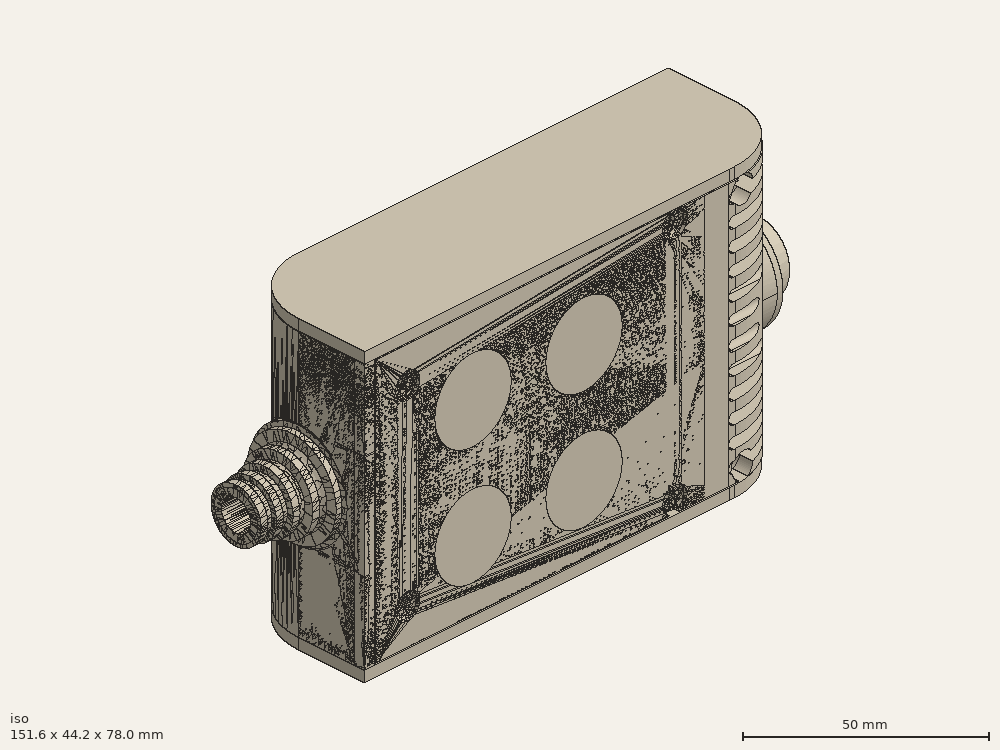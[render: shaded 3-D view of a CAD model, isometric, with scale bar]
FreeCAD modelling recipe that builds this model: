
FCSTD DOCUMENT  (FreeCAD 0.19R0.19.2)
Label: enclosure_192FCStd
License: All rights reserved
LicenseURL: http://en.wikipedia.org/wiki/All_rights_reserved
objects: Part::Revolution×152, Part::MultiFuse×146, Part::Feature×146, Sketcher::SketchObject×84, Part::Cut×70, Part::Cylinder×70, Part::Extrusion×67, Part::Fillet×58, Part::Box×36, App::MeasureDistance×4, PartDesign::Body×2, Image::ImagePlane×1
note: 831 computed .brp shape members not serialized (recipe doc carries the construction recipe); baked Part::Feature solids carry a one-line shape summary decoded from their .brp

FEATURE [Sketcher::SketchObject] Sketch  label="topSketch"
  FullyConstrained = true
  sketch-geometry (20):
    g0: LineSegment StartX=5.21097e-06 StartY=3 StartZ=0 EndX=5.21097e-06 EndY=19 EndZ=0
    g1: ArcOfCircle CenterX=19 CenterY=19 CenterZ=0 NormalX=0 NormalY=0 NormalZ=1 AngleXU=0 Radius=19 StartAngle=1.5708 EndAngle=3.14159
    g2: ArcOfCircle CenterX=19 CenterY=19 CenterZ=0 NormalX=0 NormalY=0 NormalZ=1 AngleXU=0 Radius=16 StartAngle=1.5708 EndAngle=3.14159
    g3: LineSegment StartX=114 StartY=35 StartZ=0 EndX=19 EndY=35 EndZ=0
    g4: LineSegment StartX=5.21097e-06 StartY=3 StartZ=0 EndX=5.21097e-06 EndY=0 EndZ=0
    g5: LineSegment StartX=3 StartY=0 StartZ=0 EndX=5.21097e-06 EndY=0 EndZ=0
    g6: LineSegment StartX=3 StartY=19 StartZ=0 EndX=3 EndY=0 EndZ=0
    g7: LineSegment StartX=19 StartY=38 StartZ=0 EndX=124 EndY=38 EndZ=0
    g8: Circle CenterX=119 CenterY=35 CenterZ=0 NormalX=0 NormalY=0 NormalZ=1 AngleXU=0 Radius=1
    g9: Circle CenterX=121 CenterY=35 CenterZ=0 NormalX=0 NormalY=0 NormalZ=1 AngleXU=0 Radius=1
    g10: Circle CenterX=121 CenterY=33 CenterZ=0 NormalX=0 NormalY=0 NormalZ=1 AngleXU=0 Radius=1
    g11: BSplineCurve PolesCount=3 KnotsCount=2 Degree=2 IsPeriodic=0
    g12: GeomPoint X=119 Y=35 Z=0
    g13: GeomPoint X=121 Y=33 Z=0
    g14: LineSegment StartX=119 StartY=35 StartZ=0 EndX=114 EndY=35 EndZ=0
    g15: ArcOfCircle CenterX=105 CenterY=19 CenterZ=0 NormalX=0 NormalY=0 NormalZ=1 AngleXU=0 Radius=19 StartAngle=5.7297 EndAngle=6.28319
    g16: ArcOfCircle CenterX=105 CenterY=19 CenterZ=0 NormalX=0 NormalY=0 NormalZ=1 AngleXU=0 Radius=16 StartAngle=5.60905 EndAngle=6.28319
    g17: LineSegment StartX=121 StartY=33 StartZ=0 EndX=121 EndY=19 EndZ=0
    g18: LineSegment StartX=124 StartY=38 StartZ=0 EndX=124 EndY=19 EndZ=0
    g19: LineSegment StartX=117.5 StartY=9.01251 StartZ=0 EndX=121.163 EndY=9.0125 EndZ=0
  constraints (46):
    c: Vertical(g0)
    c: Block(g0)
    c: Coincident(g1,g0)
    c: Block(g1)
    c: Coincident(g2,g1)
    c: Block(g2)
    c: Coincident(g3,g2)
    c: Horizontal(g3)
    c: Tangent(g3,g2)
    c: Coincident(g4,g0)
    c: Distance(g4) = 3
    c: Vertical(g4)
    c: Coincident(g5,g4)
    c: Horizontal(g5)
    c: Coincident(g6,g2)
    c: Coincident(g6,g5)
    c: Vertical(g6)
    c: Horizontal(g7)
    c: Distance(g7) = 105
    c: Coincident(g7,g1)
    c: Block(g3)
    c: Weight(g8) = 1
    c: Equal(g8,g9)
    c: Equal(g8,g10)
    c: InternalAlignment(g8,g11)
    c: InternalAlignment(g9,g11)
    c: InternalAlignment(g10,g11)
    c: InternalAlignment(g12,g11)
    c: InternalAlignment(g13,g11)
    c: Block(g11)
    c: Coincident(g14,g11)
    c: Coincident(g14,g3)
    c: Horizontal(g14)
    c: Block(g15)
    c: Coincident(g16,g15)
    c: Block(g16)
    c: Coincident(g17,g11)
    c: Coincident(g17,g16)
    c: Vertical(g17)
    c: Distance(g17) = 14
    c: Coincident(g18,g7)
    c: Coincident(g18,g15)
    c: Vertical(g18)
    c: Distance(g18) = 19
    c: Coincident(g19,g16)
    c: Coincident(g19,g15)
FEATURE [Sketcher::SketchObject] Sketch001  label="bottomSketch"
  FullyConstrained = true
  sketch-geometry (32):
    g0: LineSegment StartX=3.3 StartY=-6.03275e-07 StartZ=0 EndX=98 EndY=-6.03275e-07 EndZ=0
    g1: ArcOfCircle CenterX=98 CenterY=19 CenterZ=0 NormalX=0 NormalY=0 NormalZ=1 AngleXU=0 Radius=19 StartAngle=4.71239 EndAngle=5.71103
    g2: LineSegment StartX=6.3 StartY=8 StartZ=0 EndX=3.3 EndY=8 EndZ=0
    g3: LineSegment StartX=3.3 StartY=8 StartZ=0 EndX=3.3 EndY=-6.03275e-07 EndZ=0
    g4: ArcOfCircle CenterX=8.3 CenterY=5 CenterZ=0 NormalX=0 NormalY=0 NormalZ=1 AngleXU=0 Radius=2 StartAngle=3.14159 EndAngle=4.71239
    g5: LineSegment StartX=6.3 StartY=8 StartZ=0 EndX=6.3 EndY=5 EndZ=0
    g6: ArcOfCircle CenterX=98 CenterY=19 CenterZ=0 NormalX=0 NormalY=0 NormalZ=1 AngleXU=0 Radius=12.7 StartAngle=4.71239 EndAngle=6.28319
    g7: LineSegment StartX=94.7 StartY=3 StartZ=0 EndX=8.3 EndY=3 EndZ=0
    g8-g12: Circle x5 (B-spline internal-alignment scaffolding for g13; pole/knot coordinates omitted)
    g13: BSplineCurve PolesCount=5 KnotsCount=3 Degree=3 IsPeriodic=0
    g14: GeomPoint X=98 Y=6.3 Z=0
    g15: GeomPoint X=96.3938 Y=4.71946 Z=0
    g16: GeomPoint X=94.7 Y=3 Z=0
    g17-g23: Circle x7 (B-spline internal-alignment scaffolding for g24; pole/knot coordinates omitted)
    g24: BSplineCurve PolesCount=7 KnotsCount=5 Degree=3 IsPeriodic=0
    g25-g29: GeomPoint x5 (B-spline internal-alignment scaffolding for g24; pole/knot coordinates omitted)
    g30: ArcOfCircle CenterX=98 CenterY=19 CenterZ=0 NormalX=0 NormalY=0 NormalZ=1 AngleXU=0 Radius=15.7 StartAngle=5.81226 EndAngle=6.28319
    g31: LineSegment StartX=110.7 StartY=19 StartZ=0 EndX=113.7 EndY=19 EndZ=0
  constraints (41):
    c: Horizontal(g0)
    c: Coincident(g1,g0)
    c: Block(g1)
    c: Horizontal(g2)
    c: Distance(g2) = 3
    c: Coincident(g3,g2)
    c: Vertical(g3)
    c: Coincident(g3,g0)
    c: Block(g4)
    c: Block(g2)
    c: Coincident(g5,g2)
    c: Coincident(g5,g4)
    c: Vertical(g5)
    c: Coincident(g6,g1)
    c: Block(g6)
    c: Coincident(g7,g4)
    c: Horizontal(g7)
    c: Block(g0)
    c: Block(g7)
    c: Block(g3)
    c: Coincident(g13,g6)
    c: Weight(g8) = 1
    c: Equal(g8, g9-g12) x4
    c: Coincident(g13,g7)
    c: InternalAlignment(g8-g12 -> g13) x5
    c: InternalAlignment(g14,g13)
    c: InternalAlignment(g15,g13)
    c: InternalAlignment(g16,g13)
    c: Block(g13)
    c: Weight(g17) = 1
    c: Equal(g17, g18-g23) x6
    c: Coincident(g24,g1)
    c: InternalAlignment(g17-g23 -> g24) x7
    c: InternalAlignment(g25-g29 -> g24) x5
    c: Block(g24)
    c: Coincident(g30,g24)
    c: Coincident(g31,g6)
    c: Coincident(g31,g30)
    c: Horizontal(g31)
    c: Block(g31)
    c: Block(g30)
FEATURE [Part::Extrusion] Extrude  label="top"
  Base = -> Sketch
  Dir = (0,0,1)
  DirMode = 2
  FaceMakerClass = Part::FaceMakerBullseye
  LengthFwd = 72
  LengthRev = 0
  Solid = true
  Symmetric = false
FEATURE [Part::Extrusion] Extrude001  label="bottom"
  Base = -> Sketch001
  Dir = (0,0,1)
  DirMode = 2
  FaceMakerClass = Part::FaceMakerBullseye
  LengthFwd = 71.4
  LengthRev = 0
  Placement = pos=(0,0,0.3) rot=(0,0,1;0rad)
  Solid = true
  Symmetric = false
FEATURE [Sketcher::SketchObject] Sketch002  label="topSketch001"
  FullyConstrained = true
  sketch-geometry (8):
    g0: ArcOfCircle CenterX=19 CenterY=19.0975 CenterZ=0 NormalX=0 NormalY=0 NormalZ=1 AngleXU=0 Radius=18.9025 StartAngle=1.5708 EndAngle=3.14674
    g1: LineSegment StartX=0.0977805 StartY=19.0003 StartZ=0 EndX=0.0977805 EndY=0.000251602 EndZ=0
    g2: LineSegment StartX=19 StartY=38 StartZ=0 EndX=124 EndY=38 EndZ=0
    g3: LineSegment StartX=0.0977805 StartY=0.000251602 StartZ=0 EndX=105.098 EndY=0.000251602 EndZ=0
    g4: LineSegment StartX=124 StartY=38 StartZ=0 EndX=125.616 EndY=38 EndZ=0
    g5: LineSegment StartX=105.098 StartY=0.000251602 StartZ=0 EndX=106.713 EndY=0.000251602 EndZ=0
    g6: ArcOfCircle CenterX=106.616 CenterY=19 CenterZ=0 NormalX=0 NormalY=0 NormalZ=1 AngleXU=0 Radius=19 StartAngle=4.71754 EndAngle=6.28319
    g7: LineSegment StartX=125.616 StartY=38 StartZ=0 EndX=125.616 EndY=19 EndZ=0
  constraints (21):
    c: Block(g0)
    c: Coincident(g1,g0)
    c: Vertical(g1)
    c: Horizontal(g2)
    c: Distance(g2) = 105
    c: Coincident(g2,g0)
    c: Distance(g1) = 19
    c: Coincident(g3,g1)
    c: Horizontal(g3)
    c: Distance(g3) = 105
    c: Coincident(g4,g2)
    c: Horizontal(g4)
    c: Distance(g4) = 1.61553
    c: Horizontal(g5)
    c: Equal(g4,g5) = 1.61553
    c: Coincident(g5,g3)
    c: Block(g6)
    c: Coincident(g6,g5)
    c: Coincident(g7,g4)
    c: Coincident(g7,g6)
    c: Vertical(g7)
FEATURE [Part::Extrusion] Extrude002  label="sideA"
  Base = -> Sketch002
  Dir = (0,0,1)
  DirMode = 2
  FaceMakerClass = Part::FaceMakerBullseye
  LengthFwd = 3
  LengthRev = 0
  Placement = pos=(0,0,-3) rot=(0,0,1;0rad)
  Solid = true
  Symmetric = false
FEATURE [Sketcher::SketchObject] Sketch003  label="topSketch002"
  FullyConstrained = true
  sketch-geometry (6):
    g0: LineSegment StartX=19 StartY=38 StartZ=0 EndX=117 EndY=38 EndZ=0
    g1: ArcOfCircle CenterX=19 CenterY=19 CenterZ=0 NormalX=0 NormalY=0 NormalZ=1 AngleXU=0 Radius=19 StartAngle=1.5708 EndAngle=3.14159
    g2: LineSegment StartX=117 StartY=38 StartZ=0 EndX=117 EndY=19 EndZ=0
    g3: LineSegment StartX=98 StartY=1.0161e-12 StartZ=0 EndX=5.22862e-06 EndY=1.0161e-12 EndZ=0
    g4: LineSegment StartX=5.22862e-06 StartY=19 StartZ=0 EndX=5.22862e-06 EndY=1.0161e-12 EndZ=0
    g5: ArcOfCircle CenterX=98 CenterY=19 CenterZ=0 NormalX=0 NormalY=0 NormalZ=1 AngleXU=0 Radius=19 StartAngle=4.71239 EndAngle=6.28319
  constraints (16):
    c: Horizontal(g0)
    c: Distance(g0) = 98
    c: Coincident(g1,g0)
    c: Block(g1)
    c: Coincident(g2,g0)
    c: Vertical(g2)
    c: Distance(g2) = 19
    c: Horizontal(g3)
    c: Coincident(g4,g1)
    c: Vertical(g4)
    c: Coincident(g3,g4)
    c: Block(g3)
    c: Coincident(g5,g2)
    c: Coincident(g5,g3)
    c: Block(g0)
    c: Block(g5)
FEATURE [Sketcher::SketchObject] Sketch004
  FullyConstrained = true
  MapMode = 3
  Placement = pos=(0,0,0) rot=(1,0,0;1.5708rad)
  Support = -> [Extrude]
  sketch-geometry (8):
    g0: Circle CenterX=80.351 CenterY=-67.6202 CenterZ=0 NormalX=0 NormalY=0 NormalZ=1 AngleXU=0 Radius=2
    g1: Circle CenterX=80.351 CenterY=-67.6202 CenterZ=0 NormalX=0 NormalY=0 NormalZ=1 AngleXU=0 Radius=3
    g2: Circle CenterX=80.351 CenterY=-4.92017 CenterZ=0 NormalX=0 NormalY=0 NormalZ=1 AngleXU=0 Radius=2
    g3: Circle CenterX=80.351 CenterY=-4.92017 CenterZ=0 NormalX=0 NormalY=0 NormalZ=1 AngleXU=0 Radius=3
    g4: Circle CenterX=23.851 CenterY=-4.92017 CenterZ=0 NormalX=0 NormalY=0 NormalZ=1 AngleXU=0 Radius=2
    g5: Circle CenterX=23.851 CenterY=-4.92017 CenterZ=0 NormalX=0 NormalY=0 NormalZ=1 AngleXU=0 Radius=3
    g6: Circle CenterX=23.851 CenterY=-67.6202 CenterZ=0 NormalX=0 NormalY=0 NormalZ=1 AngleXU=0 Radius=2
    g7: Circle CenterX=23.851 CenterY=-67.6202 CenterZ=0 NormalX=0 NormalY=0 NormalZ=1 AngleXU=0 Radius=3
  constraints (8):
    c: Block(g3)
    c: Block(g2)
    c: Block(g1)
    c: Block(g0)
    c: Block(g6)
    c: Block(g7)
    c: Block(g4)
    c: Block(g5)
FEATURE [Part::Extrusion] Extrude004
  Base = -> Sketch004
  Dir = (0,-1,2e-16)
  DirMode = 2
  FaceMakerClass = Part::FaceMakerBullseye
  LengthFwd = 6
  LengthRev = 0
  Placement = pos=(0,9,0) rot=(0,0,1;0rad)
  Solid = true
  Symmetric = false
FEATURE [Sketcher::SketchObject] Sketch005
  FullyConstrained = true
  MapMode = 3
  Placement = pos=(0,0,0) rot=(1,0,0;1.5708rad)
  Support = -> [Extrude]
  sketch-geometry (8):
    g0: Circle CenterX=80.351 CenterY=-67.6202 CenterZ=0 NormalX=0 NormalY=0 NormalZ=1 AngleXU=0 Radius=3
    g1: Circle CenterX=80.351 CenterY=-4.92017 CenterZ=0 NormalX=0 NormalY=0 NormalZ=1 AngleXU=0 Radius=3
    g2: Circle CenterX=23.851 CenterY=-4.92017 CenterZ=0 NormalX=0 NormalY=0 NormalZ=1 AngleXU=0 Radius=3
    g3: Circle CenterX=23.851 CenterY=-67.6202 CenterZ=0 NormalX=0 NormalY=0 NormalZ=1 AngleXU=0 Radius=3
    g4: Circle CenterX=23.851 CenterY=-67.6202 CenterZ=0 NormalX=0 NormalY=0 NormalZ=1 AngleXU=0 Radius=5
    g5: Circle CenterX=80.351 CenterY=-67.6202 CenterZ=0 NormalX=0 NormalY=0 NormalZ=1 AngleXU=0 Radius=5
    g6: Circle CenterX=23.851 CenterY=-4.92017 CenterZ=0 NormalX=0 NormalY=0 NormalZ=1 AngleXU=0 Radius=5
    g7: Circle CenterX=80.351 CenterY=-4.92017 CenterZ=0 NormalX=0 NormalY=0 NormalZ=1 AngleXU=0 Radius=5
  constraints (8):
    c: Block(g1)
    c: Block(g0)
    c: Block(g3)
    c: Block(g2)
    c: Block(g5)
    c: Block(g4)
    c: Block(g6)
    c: Block(g7)
FEATURE [Part::Extrusion] Extrude005
  Base = -> Sketch005
  Dir = (0,-1,2e-16)
  DirMode = 2
  FaceMakerClass = Part::FaceMakerBullseye
  LengthFwd = 2
  LengthRev = 0
  Solid = true
  Symmetric = false
FEATURE [Sketcher::SketchObject] Sketch006
  FullyConstrained = true
  MapMode = 3
  Placement = pos=(0,0,0) rot=(1,0,0;1.5708rad)
  sketch-geometry (8):
    g0: Circle CenterX=80.351 CenterY=-67.6202 CenterZ=0 NormalX=0 NormalY=0 NormalZ=1 AngleXU=0 Radius=3
    g1: Circle CenterX=80.351 CenterY=-4.92017 CenterZ=0 NormalX=0 NormalY=0 NormalZ=1 AngleXU=0 Radius=3
    g2: Circle CenterX=23.851 CenterY=-4.92017 CenterZ=0 NormalX=0 NormalY=0 NormalZ=1 AngleXU=0 Radius=3
    g3: Circle CenterX=23.851 CenterY=-67.6202 CenterZ=0 NormalX=0 NormalY=0 NormalZ=1 AngleXU=0 Radius=3
    g4: Circle CenterX=23.851 CenterY=-67.6202 CenterZ=0 NormalX=0 NormalY=0 NormalZ=1 AngleXU=0 Radius=5
    g5: Circle CenterX=80.351 CenterY=-67.6202 CenterZ=0 NormalX=0 NormalY=0 NormalZ=1 AngleXU=0 Radius=5
    g6: Circle CenterX=23.851 CenterY=-4.92017 CenterZ=0 NormalX=0 NormalY=0 NormalZ=1 AngleXU=0 Radius=5
    g7: Circle CenterX=80.351 CenterY=-4.92017 CenterZ=0 NormalX=0 NormalY=0 NormalZ=1 AngleXU=0 Radius=5
  constraints (8):
    c: Block(g1)
    c: Block(g0)
    c: Block(g3)
    c: Block(g2)
    c: Block(g5)
    c: Block(g4)
    c: Block(g6)
    c: Block(g7)
FEATURE [Part::Extrusion] Extrude007
  Base = -> Sketch006
  Dir = (0,-1,2e-16)
  DirMode = 2
  FaceMakerClass = Part::FaceMakerBullseye
  LengthFwd = 2
  LengthRev = 0
  Solid = true
  Symmetric = false
FEATURE [Part::Fillet] Fillet
  Base = -> Extrude007
  Edges = 4 edges r=1.99: [Edge6,Edge12,Edge18,Edge24]
FEATURE [Part::Cut] Cut
  Base = -> Extrude005
  Placement = pos=(0,5,0) rot=(0,0,1;0rad)
  Tool = -> Fillet
FEATURE [Part::MultiFuse] Fusion  label="pCBScrews"
  Placement = pos=(-2.5,0,72.3) rot=(0,0,1;0rad)
  Shapes = -> [Extrude004,Cut]
FEATURE [App::MeasureDistance] Distance  label="Distance: 0.69 mm"
  Distance = 0.685967
  P1 = (24.0138,2.9647,0.3)
  P2 = (23.8901,3,-0.373787)
FEATURE [App::MeasureDistance] Distance001  label="Distance: 0.53 mm"
  Distance = 0.533607
  P1 = (80.2939,3,72.2334)
  P2 = (80.281,2.99661,71.7)
FEATURE [Part::Fillet] Fillet001
  Base = -> Extrude001
  Edges = 1 edges r=2.4: [Edge17]
FEATURE [Part::Fillet] Fillet002  label="bottom001"
  Base = -> Fillet001
  Edges = 1 edges r=2.4: [Edge36]
FEATURE [Part::Fillet] Fillet003  label="top001"
  Base = -> Extrude
  Edges = 1 edges r=2: [Edge1]
FEATURE [Sketcher::SketchObject] Sketch007
  FullyConstrained = true
  sketch-geometry (16):
    g0: LineSegment StartX=4 StartY=0 StartZ=0 EndX=4 EndY=2.4 EndZ=0
    g1: LineSegment StartX=4 StartY=2.4 StartZ=0 EndX=7 EndY=2.4 EndZ=0
    g2: LineSegment StartX=4 StartY=0 StartZ=0 EndX=5.7 EndY=0 EndZ=0
    g3: LineSegment StartX=5.7 StartY=0 StartZ=0 EndX=5.7 EndY=-5.6 EndZ=0
    g4-g8: Circle x5 (B-spline internal-alignment scaffolding for g9; pole/knot coordinates omitted)
    g9: BSplineCurve PolesCount=5 KnotsCount=3 Degree=3 IsPeriodic=0
    g10: GeomPoint X=7 Y=2.4 Z=0
    g11: GeomPoint X=10.4582 Y=-1.55472 Z=0
    g12: GeomPoint X=14 Y=-5.6 Z=0
    g13: LineSegment StartX=14 StartY=-5.6 StartZ=0 EndX=14 EndY=-14.1 EndZ=0
    g14: LineSegment StartX=14 StartY=-14.1 StartZ=0 EndX=6.5 EndY=-14.1 EndZ=0
    g15: LineSegment StartX=5.7 StartY=-5.6 StartZ=0 EndX=6.5 EndY=-14.1 EndZ=0
  constraints (28):
    c: Distance(g0) = 2.4
    c: Vertical(g0)
    c: Block(g0)
    c: Coincident(g1,g0)
    c: Horizontal(g1)
    c: Distance(g1) = 3
    c: Coincident(g2,g0)
    c: Horizontal(g2)
    c: Distance(g2) = 1.7
    c: Coincident(g3,g2)
    c: Vertical(g3)
    c: Distance(g3) = 5.6
    c: Coincident(g9,g1)
    c: Weight(g4) = 1
    c: Equal(g4, g5-g8) x4
    c: InternalAlignment(g4-g8 -> g9) x5
    c: InternalAlignment(g10,g9)
    c: InternalAlignment(g11,g9)
    c: InternalAlignment(g12,g9)
    c: Block(g9)
    c: Coincident(g13,g9)
    c: Vertical(g13)
    c: Distance(g13) = 8.5
    c: Coincident(g14,g13)
    c: Horizontal(g14)
    c: Distance(g14) = 7.5
    c: Coincident(g15,g3)
    c: Coincident(g15,g14)
FEATURE [Part::Feature] Face
  shape: bbox 10 x 16.5 x 2e-07 mm, 1 faces, 0 solids (baked)
FEATURE [Part::Revolution] Revolve  label="plugHousing"
  Angle = 360
  Axis = (0,1,0)
  Base = (0,0,0)
  FaceMakerClass = Part::FaceMakerBullseye
  Placement = pos=(0,0,36.15) rot=(0,0,1;0rad)
  Solid = false
  Source = -> Face
  Symmetric = false
FEATURE [Part::Feature] Face001
  shape: bbox 10 x 16.5 x 2e-07 mm, 1 faces, 0 solids (baked)
FEATURE [Part::Revolution] Revolve001  label="plugHousing001"
  Angle = 360
  Axis = (0,1,0)
  Base = (0,0,0)
  FaceMakerClass = Part::FaceMakerBullseye
  Placement = pos=(0,0,36.15) rot=(0,0,1;0rad)
  Solid = false
  Source = -> Face001
  Symmetric = false
FEATURE [Part::MultiFuse] Fusion001  label="plugHousing002"
  Placement = pos=(0,0,0) rot=(0,0,1;1.5708rad)
  Shapes = -> [Revolve001,Revolve]
FEATURE [Part::Feature] Face002
  shape: bbox 10 x 16.5 x 2e-07 mm, 1 faces, 0 solids (baked)
FEATURE [Part::Revolution] Revolve003  label="plugHousing005"
  Angle = 360
  Axis = (0,1,0)
  Base = (0,0,0)
  FaceMakerClass = Part::FaceMakerBullseye
  Placement = pos=(0,0,36.15) rot=(0,0,1;0rad)
  Solid = false
  Source = -> Face002
  Symmetric = false
FEATURE [Part::Feature] Face003
  shape: bbox 10 x 16.5 x 2e-07 mm, 1 faces, 0 solids (baked)
FEATURE [Part::Revolution] Revolve002  label="plugHousing003"
  Angle = 360
  Axis = (0,1,0)
  Base = (0,0,0)
  FaceMakerClass = Part::FaceMakerBullseye
  Placement = pos=(0,0,36.15) rot=(0,0,1;0rad)
  Solid = false
  Source = -> Face003
  Symmetric = false
FEATURE [Part::MultiFuse] Fusion002  label="plugHousing004"
  Placement = pos=(0,0,0) rot=(0,0,1;1.5708rad)
  Shapes = -> [Revolve002,Revolve003]
FEATURE [Part::MultiFuse] Fusion003  label="plugHousing006"
  Placement = pos=(0,19,0) rot=(0,0,1;3.14159rad)
  Shapes = -> [Fusion002,Fusion001]
FEATURE [Part::Feature] Face004
  shape: bbox 10 x 16.5 x 2e-07 mm, 1 faces, 0 solids (baked)
FEATURE [Part::Revolution] Revolve006  label="plugHousing010"
  Angle = 360
  Axis = (0,1,0)
  Base = (0,0,0)
  FaceMakerClass = Part::FaceMakerBullseye
  Placement = pos=(0,0,36.15) rot=(0,0,1;0rad)
  Solid = false
  Source = -> Face004
  Symmetric = false
FEATURE [Part::Feature] Face005
  shape: bbox 10 x 16.5 x 2e-07 mm, 1 faces, 0 solids (baked)
FEATURE [Part::Revolution] Revolve007  label="plugHousing011"
  Angle = 360
  Axis = (0,1,0)
  Base = (0,0,0)
  FaceMakerClass = Part::FaceMakerBullseye
  Placement = pos=(0,0,36.15) rot=(0,0,1;0rad)
  Solid = false
  Source = -> Face005
  Symmetric = false
FEATURE [Part::Feature] Face006
  shape: bbox 10 x 16.5 x 2e-07 mm, 1 faces, 0 solids (baked)
FEATURE [Part::Revolution] Revolve004  label="plugHousing007"
  Angle = 360
  Axis = (0,1,0)
  Base = (0,0,0)
  FaceMakerClass = Part::FaceMakerBullseye
  Placement = pos=(0,0,36.15) rot=(0,0,1;0rad)
  Solid = false
  Source = -> Face006
  Symmetric = false
FEATURE [Part::MultiFuse] Fusion004  label="plugHousing009"
  Placement = pos=(0,0,0) rot=(0,0,1;1.5708rad)
  Shapes = -> [Revolve004,Revolve007]
FEATURE [Part::Feature] Face007
  shape: bbox 10 x 16.5 x 2e-07 mm, 1 faces, 0 solids (baked)
FEATURE [Part::Revolution] Revolve005  label="plugHousing008"
  Angle = 360
  Axis = (0,1,0)
  Base = (0,0,0)
  FaceMakerClass = Part::FaceMakerBullseye
  Placement = pos=(0,0,36.15) rot=(0,0,1;0rad)
  Solid = false
  Source = -> Face007
  Symmetric = false
FEATURE [Part::MultiFuse] Fusion005  label="plugHousing012"
  Placement = pos=(0,0,0) rot=(0,0,1;1.5708rad)
  Shapes = -> [Revolve006,Revolve005]
FEATURE [Part::MultiFuse] Fusion006  label="plugHousing013"
  Placement = pos=(0,19,0) rot=(0,0,1;3.14159rad)
  Shapes = -> [Fusion005,Fusion004]
FEATURE [Part::MultiFuse] Fusion007  label="plugHousing014"
  Placement = pos=(122.621,0,-0.15) rot=(0,0,1;0rad)
  Shapes = -> [Fusion003,Fusion006]
FEATURE [Part::Cylinder] Cylinder002
  Angle = 360
  AttacherType = Attacher::AttachEngine3D
  Height = 20
  Placement = pos=(0,0,36.15) rot=(0,0,1;0rad)
  Radius = 4
FEATURE [Part::Cylinder] Cylinder003
  Angle = 360
  AttacherType = Attacher::AttachEngine3D
  Height = 10
  Placement = pos=(0,0,36.15) rot=(0,0,1;0rad)
  Radius = 4
FEATURE [Part::MultiFuse] Fusion009  label="removeToCreateHoleForPlugHousing"
  Placement = pos=(70,19,36.15) rot=(0,1,0;1.5708rad)
  Shapes = -> [Cylinder002,Cylinder003]
FEATURE [Part::Cylinder] Cylinder004
  Angle = 360
  AttacherType = Attacher::AttachEngine3D
  Height = 20
  Placement = pos=(0,0,36.15) rot=(0,0,1;0rad)
  Radius = 4
FEATURE [Part::Cylinder] Cylinder005
  Angle = 360
  AttacherType = Attacher::AttachEngine3D
  Height = 10
  Placement = pos=(0,0,36.15) rot=(0,0,1;0rad)
  Radius = 4
FEATURE [Part::MultiFuse] Fusion010  label="removeToCreateHoleForPlugHousing001"
  Placement = pos=(70,19,36.15) rot=(0,1,0;1.5708rad)
  Shapes = -> [Cylinder004,Cylinder005]
FEATURE [Part::Cut] Cut001
  Base = -> Fillet003
  Tool = -> Fusion010
FEATURE [Part::Cut] Cut002  label="Bottom"
  Base = -> Fillet002
  Tool = -> Fusion009
FEATURE [Part::Feature] Face008
  shape: bbox 10 x 16.5 x 2e-07 mm, 1 faces, 0 solids (baked)
FEATURE [Part::Revolution] Revolve011  label="plugHousing021"
  Angle = 360
  Axis = (0,1,0)
  Base = (0,0,0)
  FaceMakerClass = Part::FaceMakerBullseye
  Placement = pos=(0,0,36.15) rot=(0,0,1;0rad)
  Solid = false
  Source = -> Face008
  Symmetric = false
FEATURE [Part::Feature] Face009
  shape: bbox 10 x 16.5 x 2e-07 mm, 1 faces, 0 solids (baked)
FEATURE [Part::Revolution] Revolve012  label="plugHousing022"
  Angle = 360
  Axis = (0,1,0)
  Base = (0,0,0)
  FaceMakerClass = Part::FaceMakerBullseye
  Placement = pos=(0,0,36.15) rot=(0,0,1;0rad)
  Solid = false
  Source = -> Face009
  Symmetric = false
FEATURE [Part::Feature] Face010 .. Face013  x4 (patterned run collapsed; names and placements below)
  shape: bbox 10 x 16.5 x 2e-07 mm, 1 faces, 0 solids (baked)
FEATURE [Part::Revolution] Revolve015  label="plugHousing027"
  Angle = 360
  Axis = (0,1,0)
  Base = (0,0,0)
  FaceMakerClass = Part::FaceMakerBullseye
  Placement = pos=(0,0,36.15) rot=(0,0,1;0rad)
  Solid = false
  Source = -> Face013
  Symmetric = false
FEATURE [Part::Feature] Face014
  shape: bbox 10 x 16.5 x 2e-07 mm, 1 faces, 0 solids (baked)
FEATURE [Part::Feature] Face015
  shape: bbox 10 x 16.5 x 2e-07 mm, 1 faces, 0 solids (baked)
FEATURE [Part::Feature] Face016
  shape: bbox 10 x 16.5 x 2e-07 mm, 1 faces, 0 solids (baked)
FEATURE [Part::Revolution] Revolve019  label="plugHousing033"
  Angle = 360
  Axis = (0,1,0)
  Base = (0,0,0)
  FaceMakerClass = Part::FaceMakerBullseye
  Placement = pos=(0,0,36.15) rot=(0,0,1;0rad)
  Solid = false
  Source = -> Face016
  Symmetric = false
FEATURE [Part::Feature] Face017
  shape: bbox 10 x 16.5 x 2e-07 mm, 1 faces, 0 solids (baked)
FEATURE [Part::Revolution] Revolve020  label="plugHousing034"
  Angle = 360
  Axis = (0,1,0)
  Base = (0,0,0)
  FaceMakerClass = Part::FaceMakerBullseye
  Placement = pos=(0,0,36.15) rot=(0,0,1;0rad)
  Solid = false
  Source = -> Face017
  Symmetric = false
FEATURE [Part::Feature] Face018
  shape: bbox 10 x 16.5 x 2e-07 mm, 1 faces, 0 solids (baked)
FEATURE [Part::Revolution] Revolve016  label="plugHousing030"
  Angle = 360
  Axis = (0,1,0)
  Base = (0,0,0)
  FaceMakerClass = Part::FaceMakerBullseye
  Placement = pos=(0,0,36.15) rot=(0,0,1;0rad)
  Solid = false
  Source = -> Face018
  Symmetric = false
FEATURE [Part::MultiFuse] Fusion020  label="plugHousing038"
  Placement = pos=(0,0,0) rot=(0,0,1;1.5708rad)
  Shapes = -> [Revolve016,Revolve020]
FEATURE [Part::Feature] Face019
  shape: bbox 10 x 16.5 x 2e-07 mm, 1 faces, 0 solids (baked)
FEATURE [Part::Feature] Face020
  shape: bbox 10 x 16.5 x 2e-07 mm, 1 faces, 0 solids (baked)
FEATURE [Part::Revolution] Revolve017  label="plugHousing031"
  Angle = 360
  Axis = (0,1,0)
  Base = (0,0,0)
  FaceMakerClass = Part::FaceMakerBullseye
  Placement = pos=(0,0,36.15) rot=(0,0,1;0rad)
  Solid = false
  Source = -> Face020
  Symmetric = false
FEATURE [Part::MultiFuse] Fusion021  label="plugHousing039"
  Placement = pos=(0,0,0) rot=(0,0,1;1.5708rad)
  Shapes = -> [Revolve019,Revolve017]
FEATURE [Part::MultiFuse] Fusion023  label="plugHousing041"
  Placement = pos=(0,19,0) rot=(0,0,1;3.14159rad)
  Shapes = -> [Fusion021,Fusion020]
FEATURE [Part::Revolution] Revolve022  label="plugHousing043"
  Angle = 360
  Axis = (0,1,0)
  Base = (0,0,0)
  FaceMakerClass = Part::FaceMakerBullseye
  Placement = pos=(0,0,36.15) rot=(0,0,1;0rad)
  Solid = false
  Source = -> Face019
  Symmetric = false
FEATURE [Part::Feature] Face021
  shape: bbox 10 x 16.5 x 2e-07 mm, 1 faces, 0 solids (baked)
FEATURE [Part::Revolution] Revolve023  label="plugHousing044"
  Angle = 360
  Axis = (0,1,0)
  Base = (0,0,0)
  FaceMakerClass = Part::FaceMakerBullseye
  Placement = pos=(0,0,36.15) rot=(0,0,1;0rad)
  Solid = false
  Source = -> Face021
  Symmetric = false
FEATURE [Part::Feature] Face022
  shape: bbox 10 x 16.5 x 2e-07 mm, 1 faces, 0 solids (baked)
FEATURE [Part::Revolution] Revolve018  label="plugHousing032"
  Angle = 360
  Axis = (0,1,0)
  Base = (0,0,0)
  FaceMakerClass = Part::FaceMakerBullseye
  Placement = pos=(0,0,36.15) rot=(0,0,1;0rad)
  Solid = false
  Source = -> Face022
  Symmetric = false
FEATURE [Part::MultiFuse] Fusion022  label="plugHousing040"
  Placement = pos=(0,0,0) rot=(0,0,1;1.5708rad)
  Shapes = -> [Revolve018,Revolve023]
FEATURE [Part::Feature] Face023
  shape: bbox 10 x 16.5 x 2e-07 mm, 1 faces, 0 solids (baked)
FEATURE [Part::Revolution] Revolve021  label="plugHousing035"
  Angle = 360
  Axis = (0,1,0)
  Base = (0,0,0)
  FaceMakerClass = Part::FaceMakerBullseye
  Placement = pos=(0,0,36.15) rot=(0,0,1;0rad)
  Solid = false
  Source = -> Face023
  Symmetric = false
FEATURE [Part::MultiFuse] Fusion018  label="plugHousing036"
  Placement = pos=(0,0,0) rot=(0,0,1;1.5708rad)
  Shapes = -> [Revolve022,Revolve021]
FEATURE [Part::MultiFuse] Fusion019  label="plugHousing037"
  Placement = pos=(0,19,0) rot=(0,0,1;3.14159rad)
  Shapes = -> [Fusion018,Fusion022]
FEATURE [Part::MultiFuse] Fusion024  label="plugHousing042"
  Placement = pos=(122.621,0,-0.15) rot=(0,0,1;0rad)
  Shapes = -> [Fusion023,Fusion019]
FEATURE [Part::Cylinder] Cylinder006
  Angle = 360
  AttacherType = Attacher::AttachEngine3D
  Height = 20
  Placement = pos=(0,0,36.15) rot=(0,0,1;0rad)
  Radius = 14.3
FEATURE [Part::Cylinder] Cylinder007
  Angle = 360
  AttacherType = Attacher::AttachEngine3D
  Height = 10
  Placement = pos=(0,0,36.15) rot=(0,0,1;0rad)
  Radius = 4
FEATURE [Part::MultiFuse] Fusion026  label="removeToCreteHoleForPlugHousing"
  Placement = pos=(70,19,36) rot=(0,1,0;1.5708rad)
  Shapes = -> [Cylinder006,Cylinder007]
FEATURE [Part::Box] Box001  label="Cube001"
  AttacherType = Attacher::AttachEngine3D
  Height = 28
  Length = 3
  Placement = pos=(110.7,19,22) rot=(0,0,1;0rad)
  Width = 15.7
FEATURE [Part::Cut] Cut003  label="top002"
  Base = -> Cut001
  Tool = -> Fusion007
FEATURE [Part::Revolution] Revolve008  label="plugHousing015"
  Angle = 360
  Axis = (0,1,0)
  Base = (0,0,0)
  FaceMakerClass = Part::FaceMakerBullseye
  Placement = pos=(0,0,36.15) rot=(0,0,1;0rad)
  Solid = false
  Source = -> Face010
  Symmetric = false
FEATURE [Part::MultiFuse] Fusion013  label="plugHousing020"
  Placement = pos=(0,0,0) rot=(0,0,1;1.5708rad)
  Shapes = -> [Revolve008,Revolve012]
FEATURE [Part::Cut] Cut004  label="top003"
  Base = -> Cut003
  Placement = pos=(1,0,0) rot=(0,0,1;0rad)
  Tool = -> Fusion026
FEATURE [Part::Cylinder] Cylinder008
  Angle = 360
  AttacherType = Attacher::AttachEngine3D
  Height = 20
  Placement = pos=(0,0,36.15) rot=(0,0,1;0rad)
  Radius = 10.3
FEATURE [Part::Cylinder] Cylinder009
  Angle = 360
  AttacherType = Attacher::AttachEngine3D
  Height = 10
  Placement = pos=(0,0,36.15) rot=(0,0,1;0rad)
  Radius = 4
FEATURE [Part::MultiFuse] Fusion027  label="removeToCreteHoleForPlugHousing001"
  Placement = pos=(70,19,36) rot=(0,1,0;1.5708rad)
  Shapes = -> [Cylinder008,Cylinder009]
FEATURE [Part::Cut] Cut005  label="plugHousingTab"
  Base = -> Box001
  Tool = -> Fusion027
FEATURE [Part::MultiFuse] Fusion028  label="plugHousing045"
  Shapes = -> [Fusion024,Cut005]
FEATURE [Part::Box] Box002  label="Cube002"
  AttacherType = Attacher::AttachEngine3D
  Height = 28.8
  Length = 3
  Placement = pos=(107.3,28,21.6) rot=(0,0,1;0rad)
  Width = 7
FEATURE [Part::Box] Box003  label="Cube003"
  AttacherType = Attacher::AttachEngine3D
  Height = 3
  Length = 6.4
  Placement = pos=(107.3,28,18.6) rot=(0,0,1;0rad)
  Width = 7
FEATURE [Part::Box] Box004  label="Cube004"
  AttacherType = Attacher::AttachEngine3D
  Height = 3
  Length = 6.4
  Placement = pos=(107.3,28,50.4) rot=(0,0,1;0rad)
  Width = 7
FEATURE [Part::MultiFuse] Fusion029  label="plugHousingBracketHolder"
  Shapes = -> [Box004,Box002,Box003]
FEATURE [Part::Cylinder] Cylinder010
  Angle = 360
  AttacherType = Attacher::AttachEngine3D
  Height = 20
  Placement = pos=(0,0,36.15) rot=(0,0,1;0rad)
  Radius = 14.3
FEATURE [Part::Cylinder] Cylinder011
  Angle = 360
  AttacherType = Attacher::AttachEngine3D
  Height = 10
  Placement = pos=(0,0,36.15) rot=(0,0,1;0rad)
  Radius = 4
FEATURE [Part::MultiFuse] Fusion030  label="removeToCreteHoleForPlugHousing002"
  Placement = pos=(70,19,36) rot=(0,1,0;1.5708rad)
  Shapes = -> [Cylinder010,Cylinder011]
FEATURE [Part::Cut] Cut006  label="plugHousingBracketHolder001"
  Base = -> Fusion029
  Tool = -> Fusion030
FEATURE [Part::Cylinder] Cylinder012
  Angle = 360
  AttacherType = Attacher::AttachEngine3D
  Height = 20
  Placement = pos=(0,0,36.15) rot=(0,0,1;0rad)
  Radius = 7
FEATURE [Part::Cylinder] Cylinder013
  Angle = 360
  AttacherType = Attacher::AttachEngine3D
  Height = 10
  Placement = pos=(0,0,36.15) rot=(0,0,1;0rad)
  Radius = 4
FEATURE [Part::MultiFuse] Fusion032  label="removeToCreteHoleForPlugHousing003"
  Placement = pos=(70,19,36) rot=(0,1,0;1.5708rad)
  Shapes = -> [Cylinder012,Cylinder013]
FEATURE [Part::Cut] Cut007  label="bottom002"
  Base = -> Cut002
  Tool = -> Fusion032
FEATURE [Sketcher::SketchObject] Sketch008
  FullyConstrained = true
  sketch-geometry (54):
    g0: LineSegment StartX=-4.2 StartY=0 StartZ=0 EndX=-6.2 EndY=0 EndZ=0
    g1: LineSegment StartX=-14 StartY=-18 StartZ=0 EndX=-14 EndY=-26.5 EndZ=0
    g2: LineSegment StartX=-4.2 StartY=0 StartZ=0 EndX=-4.2 EndY=-13.4877 EndZ=0
    g3: Circle CenterX=-4.2 CenterY=-13.4877 CenterZ=0 NormalX=0 NormalY=0 NormalZ=1 AngleXU=0 Radius=1
    g4: Circle CenterX=-4.2 CenterY=-26.5 CenterZ=0 NormalX=0 NormalY=0 NormalZ=1 AngleXU=0 Radius=1
    g5: Circle CenterX=-8.2 CenterY=-26.5 CenterZ=0 NormalX=0 NormalY=0 NormalZ=1 AngleXU=0 Radius=1
    g6: BSplineCurve PolesCount=3 KnotsCount=2 Degree=2 IsPeriodic=0
    g7: GeomPoint X=-4.2 Y=-13.4877 Z=0
    g8: GeomPoint X=-8.2 Y=-26.5 Z=0
    g9: LineSegment StartX=-14 StartY=-26.5 StartZ=0 EndX=-8.2 EndY=-26.5 EndZ=0
    g10: LineSegment StartX=-10.15 StartY=-12 StartZ=0 EndX=-10.15 EndY=-14 EndZ=0
    g11: LineSegment StartX=-12.8401 StartY=-16 StartZ=0 EndX=-10.1571 EndY=-16 EndZ=0
    g12: LineSegment StartX=-10.15 StartY=-14 StartZ=0 EndX=-8.70761 EndY=-14 EndZ=0
    g13: LineSegment StartX=-12.8401 StartY=-16 StartZ=0 EndX=-12.8401 EndY=-17.6958 EndZ=0
    g14: LineSegment StartX=-10.15 StartY=-12 StartZ=0 EndX=-7.79258 EndY=-12 EndZ=0
    g15: Circle CenterX=-6.2215 CenterY=-2 CenterZ=0 NormalX=0 NormalY=0 NormalZ=1 AngleXU=0 Radius=1
    g16: Circle CenterX=-6.22762 CenterY=-2.58724 CenterZ=0 NormalX=0 NormalY=0 NormalZ=1 AngleXU=0 Radius=1
    g17: Circle CenterX=-6.32538 CenterY=-4 CenterZ=0 NormalX=0 NormalY=0 NormalZ=1 AngleXU=0 Radius=1
    g18: BSplineCurve PolesCount=3 KnotsCount=2 Degree=2 IsPeriodic=0
    g19: GeomPoint X=-6.2215 Y=-2 Z=0
    g20: GeomPoint X=-6.32538 Y=-4 Z=0
    g21: Circle CenterX=-6.48644 CenterY=-5.99526 CenterZ=0 NormalX=0 NormalY=0 NormalZ=1 AngleXU=0 Radius=1
    g22: Circle CenterX=-6.58486 CenterY=-6.99526 CenterZ=0 NormalX=0 NormalY=0 NormalZ=1 AngleXU=0 Radius=1
    g23: Circle CenterX=-6.77343 CenterY=-8 CenterZ=0 NormalX=0 NormalY=0 NormalZ=1 AngleXU=0 Radius=1
    g24: BSplineCurve PolesCount=3 KnotsCount=2 Degree=2 IsPeriodic=0
    g25: GeomPoint X=-6.48644 Y=-5.99526 Z=0
    g26: GeomPoint X=-6.77343 Y=-8 Z=0
    g27: Circle CenterX=-7.19003 CenterY=-10 CenterZ=0 NormalX=0 NormalY=0 NormalZ=1 AngleXU=0 Radius=1
    g28: Circle CenterX=-7.44407 CenterY=-11.0915 CenterZ=0 NormalX=0 NormalY=0 NormalZ=1 AngleXU=0 Radius=1
    g29: Circle CenterX=-7.79258 CenterY=-12 CenterZ=0 NormalX=0 NormalY=0 NormalZ=1 AngleXU=0 Radius=1
    g30: BSplineCurve PolesCount=3 KnotsCount=2 Degree=2 IsPeriodic=0
    g31: GeomPoint X=-7.19003 Y=-10 Z=0
    g32: GeomPoint X=-7.79258 Y=-12 Z=0
    g33: Circle CenterX=-8.70761 CenterY=-14 CenterZ=0 NormalX=0 NormalY=0 NormalZ=1 AngleXU=0 Radius=1
    g34: Circle CenterX=-9.33087 CenterY=-15.1837 CenterZ=0 NormalX=0 NormalY=0 NormalZ=1 AngleXU=0 Radius=1
    g35: Circle CenterX=-10.1571 CenterY=-16 CenterZ=0 NormalX=0 NormalY=0 NormalZ=1 AngleXU=0 Radius=1
    g36: BSplineCurve PolesCount=3 KnotsCount=2 Degree=2 IsPeriodic=0
    g37: GeomPoint X=-8.70761 Y=-14 Z=0
    g38: GeomPoint X=-10.1571 Y=-16 Z=0
    g39: Circle CenterX=-12.8401 CenterY=-17.6958 CenterZ=0 NormalX=0 NormalY=0 NormalZ=1 AngleXU=0 Radius=1
    g40: Circle CenterX=-13.3521 CenterY=-17.9027 CenterZ=0 NormalX=0 NormalY=0 NormalZ=1 AngleXU=0 Radius=1
    g41: Circle CenterX=-14 CenterY=-18 CenterZ=0 NormalX=0 NormalY=0 NormalZ=1 AngleXU=0 Radius=1
    g42: BSplineCurve PolesCount=3 KnotsCount=2 Degree=2 IsPeriodic=0
    g43: GeomPoint X=-12.8401 Y=-17.6958 Z=0
    g44: GeomPoint X=-14 Y=-18 Z=0
    g45: LineSegment StartX=-6.2 StartY=0 StartZ=0 EndX=-7.2 EndY=0 EndZ=0
    g46: LineSegment StartX=-7.2 StartY=0 StartZ=0 EndX=-7.2 EndY=-2 EndZ=0
    g47: LineSegment StartX=-7.2 StartY=-2 StartZ=0 EndX=-6.2215 EndY=-2 EndZ=0
    g48: LineSegment StartX=-6.32538 StartY=-4 StartZ=0 EndX=-7.65538 EndY=-4 EndZ=0
    g49: LineSegment StartX=-7.65538 StartY=-4 StartZ=0 EndX=-7.65538 EndY=-5.99526 EndZ=0
    g50: LineSegment StartX=-7.65538 StartY=-5.99526 StartZ=0 EndX=-6.48644 EndY=-5.99526 EndZ=0
    g51: LineSegment StartX=-6.77343 StartY=-8 StartZ=0 EndX=-8.43343 EndY=-8 EndZ=0
    g52: LineSegment StartX=-8.43343 StartY=-8 StartZ=0 EndX=-8.43343 EndY=-10 EndZ=0
    g53: LineSegment StartX=-8.43343 StartY=-10 StartZ=0 EndX=-7.19003 EndY=-10 EndZ=0
  constraints (112):
    c: Horizontal(g0)
    c: Distance(g0) = 2
    c: Block(g0)
    c: Vertical(g1)
    c: Coincident(g2,g0)
    c: Vertical(g2)
    c: Block(g2)
    c: Coincident(g6,g2)
    c: Weight(g3) = 1
    c: Equal(g3,g4)
    c: Equal(g3,g5)
    c: InternalAlignment(g3,g6)
    c: InternalAlignment(g4,g6)
    c: InternalAlignment(g5,g6)
    c: InternalAlignment(g7,g6)
    c: InternalAlignment(g8,g6)
    c: Block(g6)
    c: Coincident(g9,g1)
    c: Coincident(g9,g6)
    c: Horizontal(g9)
    c: Vertical(g10)
    c: Block(g10)
    c: Horizontal(g11)
    c: Block(g11)
    c: Coincident(g12,g10)
    c: Horizontal(g12)
    c: Block(g12)
    c: Coincident(g13,g11)
    c: Vertical(g13)
    c: Block(g13)
    c: Coincident(g14,g10)
    c: Horizontal(g14)
    c: Block(g14)
    c: Block(g9)
    c: Block(g1)
    c: Weight(g15) = 1
    c: Equal(g15,g16)
    c: Equal(g15,g17)
    c: InternalAlignment(g15,g18)
    c: InternalAlignment(g16,g18)
    c: InternalAlignment(g17,g18)
    c: InternalAlignment(g19,g18)
    c: InternalAlignment(g20,g18)
    c: Weight(g21) = 1
    c: Equal(g21,g22)
    c: Equal(g21,g23)
    c: InternalAlignment(g21,g24)
    c: InternalAlignment(g22,g24)
    c: InternalAlignment(g23,g24)
    c: InternalAlignment(g25,g24)
    c: InternalAlignment(g26,g24)
    c: Weight(g27) = 1
    c: Equal(g27,g28)
    c: Equal(g27,g29)
    c: Coincident(g30,g14)
    c: InternalAlignment(g27,g30)
    c: InternalAlignment(g28,g30)
    c: InternalAlignment(g29,g30)
    c: InternalAlignment(g31,g30)
    c: InternalAlignment(g32,g30)
    c: Coincident(g36,g12)
    c: Weight(g33) = 1
    c: Equal(g33,g34)
    c: Equal(g33,g35)
    c: Coincident(g36,g11)
    c: InternalAlignment(g33,g36)
    c: InternalAlignment(g34,g36)
    c: InternalAlignment(g35,g36)
    c: InternalAlignment(g37,g36)
    c: InternalAlignment(g38,g36)
    c: Coincident(g42,g13)
    c: Weight(g39) = 1
    c: Equal(g39,g40)
    c: Equal(g39,g41)
    c: Coincident(g42,g1)
    c: InternalAlignment(g39,g42)
    c: InternalAlignment(g40,g42)
    c: InternalAlignment(g41,g42)
    c: InternalAlignment(g43,g42)
    c: InternalAlignment(g44,g42)
    c: Block(g18)
    c: Block(g24)
    c: Block(g30)
    c: Block(g36)
    c: Block(g42)
    c: Horizontal(g45)
    c: Coincident(g45,g0)
    c: Vertical(g46)
    c: Coincident(g46,g45)
    c: Coincident(g47,g46)
    c: Coincident(g47,g18)
    c: Horizontal(g47)
    c: Block(g46)
    c: Coincident(g48,g18)
    c: Horizontal(g48)
    c: Distance(g48) = 1.33
    c: Vertical(g49)
    c: Coincident(g49,g48)
    c: Coincident(g50,g49)
    c: Coincident(g50,g24)
    c: Horizontal(g50)
    c: Tangent(g50,g22)
    c: Horizontal(g51)
    c: Coincident(g51,g24)
    c: Block(g51)
    c: Vertical(g52)
    c: Block(g52)
    c: Coincident(g52,g51)
    c: Coincident(g53,g52)
    c: Coincident(g53,g30)
    c: Horizontal(g53)
    c: Distance(g1) = 8.5
FEATURE [Part::Feature] Face024
  shape: bbox 9.8 x 26.5 x 2e-07 mm, 1 faces, 0 solids (baked)
FEATURE [Part::Revolution] Revolve024
  Angle = 360
  Axis = (0,1,0)
  Base = (0,0,0)
  FaceMakerClass = Part::FaceMakerBullseye
  Placement = pos=(0,0,0) rot=(0,0,1;1.5708rad)
  Solid = false
  Source = -> Face024
  Symmetric = false
FEATURE [Part::Feature] Face025
  shape: bbox 9.8 x 26.5 x 2e-07 mm, 1 faces, 0 solids (baked)
FEATURE [Part::Revolution] Revolve025
  Angle = 360
  Axis = (0,1,0)
  Base = (0,0,0)
  FaceMakerClass = Part::FaceMakerBullseye
  Placement = pos=(0,0,0) rot=(0,0,1;1.5708rad)
  Solid = false
  Source = -> Face025
  Symmetric = false
FEATURE [Part::MultiFuse] Fusion033
  Placement = pos=(-18,19,36) rot=(0,0,1;0rad)
  Shapes = -> [Revolve025,Revolve024]
FEATURE [Part::Cylinder] Cylinder014
  Angle = 360
  AttacherType = Attacher::AttachEngine3D
  Height = 20
  Placement = pos=(0,0,36.15) rot=(0,0,1;0rad)
  Radius = 14.3
FEATURE [Part::Cylinder] Cylinder015
  Angle = 360
  AttacherType = Attacher::AttachEngine3D
  Height = 10
  Placement = pos=(0,0,36.15) rot=(0,0,1;0rad)
  Radius = 4
FEATURE [Part::MultiFuse] Fusion034  label="removeToCreteHoleForPlugHousing004"
  Placement = pos=(-42,19,36) rot=(0,1,0;1.5708rad)
  Shapes = -> [Cylinder014,Cylinder015]
FEATURE [Part::Cut] Cut008  label="top004"
  Base = -> Cut004
  Placement = pos=(-1,0,0) rot=(0,0,1;0rad)
  Tool = -> Fusion034
FEATURE [Part::Box] Box005  label="Cube005"
  AttacherType = Attacher::AttachEngine3D
  Height = 28
  Length = 3
  Placement = pos=(110.7,19,22) rot=(0,0,1;0rad)
  Width = 15.7
FEATURE [Part::Cylinder] Cylinder016
  Angle = 360
  AttacherType = Attacher::AttachEngine3D
  Height = 10
  Placement = pos=(0,0,36.15) rot=(0,0,1;0rad)
  Radius = 4
FEATURE [Part::Cylinder] Cylinder017
  Angle = 360
  AttacherType = Attacher::AttachEngine3D
  Height = 20
  Placement = pos=(0,0,36.15) rot=(0,0,1;0rad)
  Radius = 10.3
FEATURE [Part::MultiFuse] Fusion035  label="removeToCreteHoleForPlugHousing005"
  Placement = pos=(70,19,36) rot=(0,1,0;1.5708rad)
  Shapes = -> [Cylinder017,Cylinder016]
FEATURE [Part::Cut] Cut009  label="plugHousingTab001"
  Base = -> Box005
  Placement = pos=(-107.4,-14,0) rot=(0,0,1;0rad)
  Tool = -> Fusion035
FEATURE [Part::Box] Box006  label="Cube006"
  AttacherType = Attacher::AttachEngine3D
  Height = 28
  Length = 3
  Placement = pos=(110.7,19,22) rot=(0,0,1;0rad)
  Width = 15.7
FEATURE [Part::Cylinder] Cylinder018
  Angle = 360
  AttacherType = Attacher::AttachEngine3D
  Height = 10
  Placement = pos=(0,0,36.15) rot=(0,0,1;0rad)
  Radius = 4
FEATURE [Part::Cylinder] Cylinder019
  Angle = 360
  AttacherType = Attacher::AttachEngine3D
  Height = 20
  Placement = pos=(0,0,36.15) rot=(0,0,1;0rad)
  Radius = 10.3
FEATURE [Part::MultiFuse] Fusion036  label="removeToCreteHoleForPlugHousing006"
  Placement = pos=(70,19,36) rot=(0,1,0;1.5708rad)
  Shapes = -> [Cylinder019,Cylinder018]
FEATURE [Part::Cut] Cut010  label="plugHousingTab002"
  Base = -> Box006
  Placement = pos=(-107.4,-14,0) rot=(0,0,1;0rad)
  Tool = -> Fusion036
FEATURE [Part::MultiFuse] Fusion037
  Placement = pos=(9.6,23,0) rot=(0,0,1;3.14159rad)
  Shapes = -> [Cut009,Cut010]
FEATURE [Part::Box] Box  label="Cube"
  AttacherType = Attacher::AttachEngine3D
  Height = 10
  Length = 3
  Placement = pos=(3.3,4,12) rot=(0,0,1;0rad)
  Width = 10
FEATURE [Part::Fillet] Fillet004
  Base = -> Fusion028
  Edges = 1 edges r=2: [Edge25]
FEATURE [Part::Fillet] Fillet005  label="plugHousing046"
  Base = -> Fillet004
  Edges = 1 edges r=2: [Edge8]
FEATURE [Part::Fillet] Fillet006
  Base = -> Box
  Edges = 1 edges r=2: [Edge11]
FEATURE [Part::Box] Box007  label="Cube007"
  AttacherType = Attacher::AttachEngine3D
  Height = 10
  Length = 3
  Placement = pos=(3.3,4,50) rot=(0,0,1;0rad)
  Width = 10
FEATURE [Part::Fillet] Fillet007
  Base = -> Box007
  Edges = 1 edges r=2: [Edge12]
FEATURE [Part::Box] Box008  label="Cube008"
  AttacherType = Attacher::AttachEngine3D
  Height = 28
  Length = 4
  Placement = pos=(5,0,22) rot=(0,0,1;0rad)
  Width = 10
FEATURE [Part::Fillet] Fillet008
  Base = -> Box008
  Edges = 1 edges r=1: [Edge7]
FEATURE [Part::Fillet] Fillet009
  Base = -> Fillet008
  Edges = 1 edges r=2: [Edge5]
FEATURE [Part::Fillet] Fillet010
  Base = -> Fillet009
  Edges = 1 edges r=2: [Edge2]
FEATURE [Sketcher::SketchObject] Sketch009  label="topSketch003"
  FullyConstrained = true
  sketch-geometry (4):
    g0: LineSegment StartX=16.8446 StartY=31.512 StartZ=0 EndX=16.3251 EndY=34.4666 EndZ=0
    g1: ArcOfCircle CenterX=19 CenterY=19.2524 CenterZ=0 NormalX=0 NormalY=0 NormalZ=1 AngleXU=0 Radius=15.4476 StartAngle=1.74483 EndAngle=2.72717
    g2: ArcOfCircle CenterX=19 CenterY=19.2524 CenterZ=0 NormalX=0 NormalY=0 NormalZ=1 AngleXU=0 Radius=12.4476 StartAngle=1.74483 EndAngle=2.73189
    g3: LineSegment StartX=4.86004 StartY=25.4725 StartZ=0 EndX=7.58253 EndY=24.2107 EndZ=0
  constraints (7):
    c: Block(g0)
    c: Coincident(g1,g0)
    c: Coincident(g2,g0)
    c: Coincident(g3,g1)
    c: Coincident(g3,g2)
    c: Block(g1)
    c: Block(g2)
FEATURE [Part::Extrusion] Extrude008
  Base = -> Sketch009
  Dir = (0,0,1)
  DirMode = 2
  FaceMakerClass = Part::FaceMakerBullseye
  LengthFwd = 10
  LengthRev = 0
  Placement = pos=(0,0,31) rot=(0,0,1;0rad)
  Solid = true
  Symmetric = false
FEATURE [Part::Cylinder] Cylinder020
  Angle = 360
  AttacherType = Attacher::AttachEngine3D
  Height = 20
  Placement = pos=(0,0,36.15) rot=(0,0,1;0rad)
  Radius = 8.2
FEATURE [Part::Cylinder] Cylinder021
  Angle = 360
  AttacherType = Attacher::AttachEngine3D
  Height = 10
  Placement = pos=(0,0,36.15) rot=(0,0,1;0rad)
  Radius = 4
FEATURE [Part::MultiFuse] Fusion038  label="removeToCreteHoleForPlugHousing007"
  Placement = pos=(-42,19,36) rot=(0,1,0;1.5708rad)
  Shapes = -> [Cylinder020,Cylinder021]
FEATURE [Part::Cut] Cut011
  Base = -> Extrude008
  Tool = -> Fusion038
FEATURE [Part::Fillet] Fillet011
  Base = -> Cut011
  Edges = 1 edges r=2: [Edge1]
FEATURE [Part::Fillet] Fillet012
  Base = -> Fillet011
  Edges = 1 edges r=2.5: [Edge1]
FEATURE [Part::Fillet] Fillet013
  Base = -> Fillet012
  Edges = 1 edges r=2.5: [Edge2]
FEATURE [Part::Box] Box010  label="Cube010"
  AttacherType = Attacher::AttachEngine3D
  Height = 16
  Length = 8
  Placement = pos=(12.7,31.52,28) rot=(0,0,1;0rad)
  Width = 4
FEATURE [Sketcher::SketchObject] Sketch010  label="topSketch004"
  FullyConstrained = true
  sketch-geometry (4):
    g0: LineSegment StartX=16.8446 StartY=31.512 StartZ=0 EndX=16.3251 EndY=34.4666 EndZ=0
    g1: ArcOfCircle CenterX=19 CenterY=19.2524 CenterZ=0 NormalX=0 NormalY=0 NormalZ=1 AngleXU=0 Radius=15.4476 StartAngle=1.74483 EndAngle=2.72717
    g2: ArcOfCircle CenterX=19 CenterY=19.2524 CenterZ=0 NormalX=0 NormalY=0 NormalZ=1 AngleXU=0 Radius=12.4476 StartAngle=1.74483 EndAngle=2.73189
    g3: LineSegment StartX=4.86004 StartY=25.4725 StartZ=0 EndX=7.58253 EndY=24.2107 EndZ=0
  constraints (7):
    c: Block(g0)
    c: Coincident(g1,g0)
    c: Coincident(g2,g0)
    c: Coincident(g3,g1)
    c: Coincident(g3,g2)
    c: Block(g1)
    c: Block(g2)
FEATURE [Part::Cylinder] Cylinder022
  Angle = 360
  AttacherType = Attacher::AttachEngine3D
  Height = 10
  Placement = pos=(0,0,36.15) rot=(0,0,1;0rad)
  Radius = 4
FEATURE [Sketcher::SketchObject] Sketch011  label="topSketch005"
  FullyConstrained = true
  sketch-geometry (4):
    g0: LineSegment StartX=16.8446 StartY=31.512 StartZ=0 EndX=16.3251 EndY=34.4666 EndZ=0
    g1: ArcOfCircle CenterX=19 CenterY=19.2524 CenterZ=0 NormalX=0 NormalY=0 NormalZ=1 AngleXU=0 Radius=15.4476 StartAngle=1.74483 EndAngle=2.72717
    g2: ArcOfCircle CenterX=19 CenterY=19.2524 CenterZ=0 NormalX=0 NormalY=0 NormalZ=1 AngleXU=0 Radius=12.4476 StartAngle=1.74483 EndAngle=2.73189
    g3: LineSegment StartX=4.86004 StartY=25.4725 StartZ=0 EndX=7.58253 EndY=24.2107 EndZ=0
  constraints (7):
    c: Block(g0)
    c: Coincident(g1,g0)
    c: Coincident(g2,g0)
    c: Coincident(g3,g1)
    c: Coincident(g3,g2)
    c: Block(g1)
    c: Block(g2)
FEATURE [Part::Extrusion] Extrude010
  Base = -> Sketch011
  Dir = (0,0,1)
  DirMode = 2
  FaceMakerClass = Part::FaceMakerBullseye
  LengthFwd = 10.6
  LengthRev = 0
  Placement = pos=(0,0,31) rot=(0,0,1;0rad)
  Solid = true
  Symmetric = false
FEATURE [Part::Cylinder] Cylinder023
  Angle = 360
  AttacherType = Attacher::AttachEngine3D
  Height = 20
  Placement = pos=(0,0,36.15) rot=(0,0,1;0rad)
  Radius = 8.2
FEATURE [Part::MultiFuse] Fusion039  label="removeToCreteHoleForPlugHousing008"
  Placement = pos=(-42,19,36) rot=(0,1,0;1.5708rad)
  Shapes = -> [Cylinder023,Cylinder022]
FEATURE [Part::Cut] Cut012
  Base = -> Extrude010
  Placement = pos=(0,0,-0.3) rot=(0,0,1;0rad)
  Tool = -> Fusion039
FEATURE [Part::Cut] Cut013
  Base = -> Box010
  Tool = -> Cut012
FEATURE [Part::Fillet] Fillet014
  Base = -> Cut013
  Edges = 1 edges r=0.7: [Edge13]
FEATURE [Part::Fillet] Fillet015
  Base = -> Fillet014
  Edges = 1 edges r=0.7: [Edge13]
FEATURE [Part::Fillet] Fillet016
  Base = -> Fillet015
  Edges = 1 edges r=0.7: [Edge16]
FEATURE [Part::Fillet] Fillet017
  Base = -> Fillet016
  Edges = 1 edges r=0.7: [Edge11]
FEATURE [Part::Fillet] Fillet018
  Base = -> Fillet017
  Edges = 1 edges r=0.7: [Edge10]
FEATURE [Part::Fillet] Fillet019
  Base = -> Fillet018
  Edges = 1 edges r=1.2: [Edge5]
FEATURE [Part::Fillet] Fillet020
  Base = -> Fillet019
  Edges = 1 edges r=1.2: [Edge12]
FEATURE [Part::Fillet] Fillet021
  Base = -> Fillet020
  Edges = 1 edges r=2: [Edge1]
  Placement = pos=(0.3,0,0) rot=(0,0,1;0rad)
FEATURE [Part::MultiFuse] Fusion040  label="top005"
  Shapes = -> [Cut008,Fillet021]
FEATURE [Part::MultiFuse] Fusion041  label="wireHolder"
  Shapes = -> [Fusion033,Fillet013]
FEATURE [Part::MultiFuse] Fusion042
  Shapes = -> [Fillet007,Fusion041]
FEATURE [Part::MultiFuse] Fusion043  label="wireHolder001"
  Shapes = -> [Fusion042,Fillet010]
FEATURE [Part::MultiFuse] Fusion044  label="wireHolder002"
  Shapes = -> [Fillet006,Fusion037,Fusion043]
FEATURE [Part::Feature] Face026
  shape: bbox 11 x 6 x 2e-07 mm, 1 faces, 0 solids (baked)
FEATURE [Part::Revolution] Revolve026
  Angle = 360
  Axis = (0,1,0)
  Base = (0,0,0)
  FaceMakerClass = Part::FaceMakerBullseye
  Placement = pos=(30.3,-1,19.7) rot=(0,0,1;0rad)
  Solid = false
  Source = -> Face026
  Symmetric = false
FEATURE [Sketcher::SketchObject] Sketch013  label="topSketch006"
  FullyConstrained = true
  sketch-geometry (13):
    g0: LineSegment StartX=117 StartY=19 StartZ=0 EndX=117 EndY=38 EndZ=0
    g1: ArcOfCircle CenterX=98 CenterY=19 CenterZ=0 NormalX=0 NormalY=0 NormalZ=1 AngleXU=0 Radius=19 StartAngle=5.7297 EndAngle=6.28319
    g2: LineSegment StartX=0 StartY=3 StartZ=0 EndX=0 EndY=19 EndZ=0
    g3: LineSegment StartX=19 StartY=38 StartZ=0 EndX=117 EndY=38 EndZ=0
    g4: ArcOfCircle CenterX=19 CenterY=19 CenterZ=0 NormalX=0 NormalY=0 NormalZ=1 AngleXU=0 Radius=19 StartAngle=1.5708 EndAngle=3.14159
    g5: ArcOfCircle CenterX=19 CenterY=19 CenterZ=0 NormalX=0 NormalY=0 NormalZ=1 AngleXU=0 Radius=16 StartAngle=1.5708 EndAngle=3.14159
    g6: ArcOfCircle CenterX=98 CenterY=19 CenterZ=0 NormalX=0 NormalY=0 NormalZ=1 AngleXU=0 Radius=16 StartAngle=5.60905 EndAngle=6.28319
    g7: LineSegment StartX=114 StartY=19 StartZ=0 EndX=114 EndY=35 EndZ=0
    g8: LineSegment StartX=110.5 StartY=9.01251 StartZ=0 EndX=114.163 EndY=9.01251 EndZ=0
    g9: LineSegment StartX=114 StartY=35 StartZ=0 EndX=19 EndY=35 EndZ=0
    g10: LineSegment StartX=0 StartY=3 StartZ=0 EndX=0 EndY=0 EndZ=0
    g11: LineSegment StartX=3 StartY=0 StartZ=0 EndX=0 EndY=0 EndZ=0
    g12: LineSegment StartX=3 StartY=19 StartZ=0 EndX=3 EndY=0 EndZ=0
  constraints (33):
    c: Vertical(g0)
    c: Distance(g0) = 19
    c: Block(g0)
    c: Coincident(g1,g0)
    c: Block(g1)
    c: Vertical(g2)
    c: Block(g2)
    c: Coincident(g3,g0)
    c: Horizontal(g3)
    c: Distance(g3) = 98
    c: Coincident(g4,g3)
    c: Coincident(g4,g2)
    c: Block(g4)
    c: Coincident(g5,g4)
    c: Coincident(g6,g1)
    c: Block(g6)
    c: Block(g5)
    c: Coincident(g7,g6)
    c: Vertical(g7)
    c: Coincident(g8,g6)
    c: Coincident(g8,g1)
    c: Coincident(g9,g7)
    c: Coincident(g9,g5)
    c: Horizontal(g9)
    c: Tangent(g9,g5)
    c: Coincident(g10,g2)
    c: Distance(g10) = 3
    c: Vertical(g10)
    c: Coincident(g11,g10)
    c: Horizontal(g11)
    c: Coincident(g12,g5)
    c: Coincident(g12,g11)
    c: Vertical(g12)
FEATURE [Part::Extrusion] Extrude011  label="top006"
  Base = -> Sketch013
  Dir = (0,0,1)
  DirMode = 2
  FaceMakerClass = Part::FaceMakerBullseye
  LengthFwd = 72
  LengthRev = 0
  Solid = true
  Symmetric = false
FEATURE [Sketcher::SketchObject] Sketch014
  FullyConstrained = true
  MapMode = 3
  Placement = pos=(0,0,0) rot=(1,0,0;1.5708rad)
  Support = -> [Extrude011]
  sketch-geometry (8):
    g0: Circle CenterX=80.351 CenterY=-67.6202 CenterZ=0 NormalX=0 NormalY=0 NormalZ=1 AngleXU=0 Radius=2
    g1: Circle CenterX=80.351 CenterY=-67.6202 CenterZ=0 NormalX=0 NormalY=0 NormalZ=1 AngleXU=0 Radius=3
    g2: Circle CenterX=80.351 CenterY=-4.92017 CenterZ=0 NormalX=0 NormalY=0 NormalZ=1 AngleXU=0 Radius=2
    g3: Circle CenterX=80.351 CenterY=-4.92017 CenterZ=0 NormalX=0 NormalY=0 NormalZ=1 AngleXU=0 Radius=3
    g4: Circle CenterX=23.851 CenterY=-4.92017 CenterZ=0 NormalX=0 NormalY=0 NormalZ=1 AngleXU=0 Radius=2
    g5: Circle CenterX=23.851 CenterY=-4.92017 CenterZ=0 NormalX=0 NormalY=0 NormalZ=1 AngleXU=0 Radius=3
    g6: Circle CenterX=23.851 CenterY=-67.6202 CenterZ=0 NormalX=0 NormalY=0 NormalZ=1 AngleXU=0 Radius=2
    g7: Circle CenterX=23.851 CenterY=-67.6202 CenterZ=0 NormalX=0 NormalY=0 NormalZ=1 AngleXU=0 Radius=3
  constraints (8):
    c: Block(g3)
    c: Block(g2)
    c: Block(g1)
    c: Block(g0)
    c: Block(g6)
    c: Block(g7)
    c: Block(g4)
    c: Block(g5)
FEATURE [Part::Feature] Face027
  shape: bbox 11 x 6 x 2e-07 mm, 1 faces, 0 solids (baked)
FEATURE [Part::Revolution] Revolve027
  Angle = 360
  Axis = (0,1,0)
  Base = (0,0,0)
  FaceMakerClass = Part::FaceMakerBullseye
  Placement = pos=(30.3,-1,51.7) rot=(0,0,1;0rad)
  Solid = false
  Source = -> Face027
  Symmetric = false
FEATURE [Part::Feature] Face028
  shape: bbox 11 x 6 x 2e-07 mm, 1 faces, 0 solids (baked)
FEATURE [Part::Revolution] Revolve028
  Angle = 360
  Axis = (0,1,0)
  Base = (0,0,0)
  FaceMakerClass = Part::FaceMakerBullseye
  Placement = pos=(62.3,-1,19.7) rot=(0,0,1;0rad)
  Solid = false
  Source = -> Face028
  Symmetric = false
FEATURE [Part::Feature] Face029
  shape: bbox 11 x 6 x 2e-07 mm, 1 faces, 0 solids (baked)
FEATURE [Part::Revolution] Revolve029
  Angle = 360
  Axis = (0,1,0)
  Base = (0,0,0)
  FaceMakerClass = Part::FaceMakerBullseye
  Placement = pos=(62.3,-1,51.7) rot=(0,0,1;0rad)
  Solid = false
  Source = -> Face029
  Symmetric = false
FEATURE [Part::Feature] Wire
  shape: bbox 11 x 5.2 x 2e-07 mm, 0 faces, 0 solids (baked)
FEATURE [Part::Revolution] Revolve030
  Angle = 360
  Axis = (0,1,0)
  Base = (0,0,0)
  FaceMakerClass = Part::FaceMakerBullseye
  Placement = pos=(30.3,38,19.7) rot=(0,0,1;0rad)
  Solid = true
  Source = -> Wire
  Symmetric = false
FEATURE [Part::Feature] Wire001
  shape: bbox 11 x 5.2 x 2e-07 mm, 0 faces, 0 solids (baked)
FEATURE [Part::Revolution] Revolve031
  Angle = 360
  Axis = (0,1,0)
  Base = (0,0,0)
  FaceMakerClass = Part::FaceMakerBullseye
  Placement = pos=(30.3,38,51.7) rot=(0,0,1;0rad)
  Solid = true
  Source = -> Wire001
  Symmetric = false
FEATURE [Part::Feature] Wire002
  shape: bbox 11 x 5.2 x 2e-07 mm, 0 faces, 0 solids (baked)
FEATURE [Part::Revolution] Revolve032
  Angle = 360
  Axis = (0,1,0)
  Base = (0,0,0)
  FaceMakerClass = Part::FaceMakerBullseye
  Placement = pos=(62.3,38,51.7) rot=(0,0,1;0rad)
  Solid = true
  Source = -> Wire002
  Symmetric = false
FEATURE [Part::Feature] Wire003
  shape: bbox 11 x 5.2 x 2e-07 mm, 0 faces, 0 solids (baked)
FEATURE [Part::Revolution] Revolve033
  Angle = 360
  Axis = (0,1,0)
  Base = (0,0,0)
  FaceMakerClass = Part::FaceMakerBullseye
  Placement = pos=(62.3,38,19.7) rot=(0,0,1;0rad)
  Solid = true
  Source = -> Wire003
  Symmetric = false
FEATURE [Part::MultiFuse] Fusion045  label="altRandScrewHousing"
  Shapes = -> [Revolve029,Revolve027,Revolve028,Revolve026]
FEATURE [Part::MultiFuse] Fusion046  label="fanScrewHousing"
  Shapes = -> [Revolve033,Revolve032,Revolve031,Revolve030]
FEATURE [Sketcher::SketchObject] Sketch015
  FullyConstrained = true
  sketch-geometry (17):
    g0: Circle CenterX=-3.5 CenterY=23.5 CenterZ=0 NormalX=0 NormalY=0 NormalZ=1 AngleXU=0 Radius=1
    g1: Circle CenterX=-1 CenterY=15.25 CenterZ=0 NormalX=0 NormalY=0 NormalZ=1 AngleXU=0 Radius=1
    g2: Circle CenterX=-3.5 CenterY=7 CenterZ=0 NormalX=0 NormalY=0 NormalZ=1 AngleXU=0 Radius=1
    g3: BSplineCurve PolesCount=3 KnotsCount=2 Degree=2 IsPeriodic=0
    g4: GeomPoint X=-3.5 Y=23.5 Z=0
    g5: GeomPoint X=-3.5 Y=7 Z=0
    g6: Circle CenterX=-4.8 CenterY=30.5 CenterZ=0 NormalX=0 NormalY=0 NormalZ=1 AngleXU=0 Radius=1
    g7: Circle CenterX=-3.5 CenterY=30.5 CenterZ=0 NormalX=0 NormalY=0 NormalZ=1 AngleXU=0 Radius=1
    g8: Circle CenterX=-3.5 CenterY=29.2 CenterZ=0 NormalX=0 NormalY=0 NormalZ=1 AngleXU=0 Radius=1
    g9: BSplineCurve PolesCount=3 KnotsCount=2 Degree=2 IsPeriodic=0
    g10: GeomPoint X=-4.8 Y=30.5 Z=0
    g11: GeomPoint X=-3.5 Y=29.2 Z=0
    g12: LineSegment StartX=-3.5 StartY=29.2 StartZ=0 EndX=-3.5 EndY=23.5 EndZ=0
    g13: LineSegment StartX=-4.8 StartY=30.5 StartZ=0 EndX=0 EndY=30.5 EndZ=0
    g14: LineSegment StartX=-3.5 StartY=0.3 StartZ=0 EndX=0 EndY=0.3 EndZ=0
    g15: LineSegment StartX=-3.5 StartY=0.3 StartZ=0 EndX=-3.5 EndY=7 EndZ=0
    g16: LineSegment StartX=0 StartY=0.3 StartZ=0 EndX=0 EndY=30.5 EndZ=0
  constraints (33):
    c: Weight(g0) = 1
    c: Equal(g0,g1)
    c: Equal(g0,g2)
    c: InternalAlignment(g0,g3)
    c: InternalAlignment(g1,g3)
    c: InternalAlignment(g2,g3)
    c: InternalAlignment(g4,g3)
    c: InternalAlignment(g5,g3)
    c: Block(g3)
    c: Weight(g6) = 1
    c: Equal(g6,g7)
    c: Equal(g6,g8)
    c: InternalAlignment(g6,g9)
    c: InternalAlignment(g7,g9)
    c: InternalAlignment(g8,g9)
    c: InternalAlignment(g10,g9)
    c: InternalAlignment(g11,g9)
    c: Block(g9)
    c: Coincident(g12,g9)
    c: Coincident(g12,g3)
    c: Vertical(g12)
    c: Coincident(g13,g9)
    c: Horizontal(g13)
    c: Distance(g13) = 4.8
    c: Horizontal(g14)
    c: Block(g14)
    c: Coincident(g15,g14)
    c: Coincident(g15,g3)
    c: Vertical(g15)
    c: Coincident(g16,g14)
    c: Coincident(g16,g13)
    c: Vertical(g16)
    c: Tangent(g16,g1)
FEATURE [Sketcher::SketchObject] Sketch016
  FullyConstrained = true
  sketch-geometry (16):
    g0: Circle CenterX=-3.5 CenterY=23.5 CenterZ=0 NormalX=0 NormalY=0 NormalZ=1 AngleXU=0 Radius=1
    g1: Circle CenterX=-1 CenterY=15.25 CenterZ=0 NormalX=0 NormalY=0 NormalZ=1 AngleXU=0 Radius=1
    g2: Circle CenterX=-3.5 CenterY=7 CenterZ=0 NormalX=0 NormalY=0 NormalZ=1 AngleXU=0 Radius=1
    g3: BSplineCurve PolesCount=3 KnotsCount=2 Degree=2 IsPeriodic=0
    g4: GeomPoint X=-3.5 Y=23.5 Z=0
    g5: GeomPoint X=-3.5 Y=7 Z=0
    g6: LineSegment StartX=-3.5 StartY=28.2 StartZ=0 EndX=-3.5 EndY=23.5 EndZ=0
    g7: LineSegment StartX=0 StartY=29.5 StartZ=0 EndX=0 EndY=30 EndZ=0
    g8: LineSegment StartX=-3.5 StartY=28.2 StartZ=0 EndX=-3.5 EndY=30 EndZ=0
    g9: LineSegment StartX=0 StartY=30 StartZ=0 EndX=0 EndY=30.5 EndZ=0
    g10: LineSegment StartX=0 StartY=30.5 StartZ=0 EndX=-3.5 EndY=30.5 EndZ=0
    g11: LineSegment StartX=-3.5 StartY=30.5 StartZ=0 EndX=-3.5 EndY=30 EndZ=0
    g12: LineSegment StartX=0 StartY=29.5 StartZ=0 EndX=0 EndY=5 EndZ=0
    g13: LineSegment StartX=-3.5 StartY=0.3 StartZ=0 EndX=-3.5 EndY=7 EndZ=0
    g14: LineSegment StartX=-3.5 StartY=0.3 StartZ=0 EndX=0 EndY=0.3 EndZ=0
    g15: LineSegment StartX=0 StartY=5 StartZ=0 EndX=0 EndY=0.3 EndZ=0
  constraints (39):
    c: Weight(g0) = 1
    c: Equal(g0,g1)
    c: Equal(g0,g2)
    c: InternalAlignment(g0,g3)
    c: InternalAlignment(g1,g3)
    c: InternalAlignment(g2,g3)
    c: InternalAlignment(g4,g3)
    c: InternalAlignment(g5,g3)
    c: Block(g3)
    c: Coincident(g6,g3)
    c: Vertical(g6)
    c: Vertical(g7)
    c: Distance(g7) = 0.5
    c: Coincident(g8,g6)
    c: Vertical(g8)
    c: Block(g6)
    c: Block(g7)
    c: Vertical(g9)
    c: Equal(g7,g9) = 0.5
    c: Block(g9)
    c: Coincident(g9,g7)
    c: Horizontal(g10)
    c: Coincident(g10,g9)
    c: Coincident(g11,g10)
    c: Coincident(g11,g8)
    c: Vertical(g11)
    c: Block(g11)
    c: Coincident(g12,g7)
    c: Vertical(g12)
    c: Coincident(g13,g3)
    c: Vertical(g13)
    c: Distance(g13) = 6.7
    c: Coincident(g14,g13)
    c: Horizontal(g14)
    c: Block(g14)
    c: Coincident(g15,g12)
    c: Coincident(g15,g14)
    c: Vertical(g15)
    c: Block(g15)
FEATURE [Sketcher::SketchObject] Sketch017
  FullyConstrained = true
  sketch-geometry (11):
    g0: LineSegment StartX=-3.5 StartY=1e-16 StartZ=0 EndX=-1.6 EndY=1e-16 EndZ=0
    g1: LineSegment StartX=-1.6 StartY=1e-16 StartZ=0 EndX=-1.6 EndY=1.5 EndZ=0
    g2: LineSegment StartX=-3.5 StartY=1.5 StartZ=0 EndX=-1.6 EndY=1.5 EndZ=0
    g3: LineSegment StartX=-3.5 StartY=1e-16 StartZ=0 EndX=-4.8 EndY=1e-16 EndZ=0
    g4: Circle CenterX=-3.5 CenterY=1.3 CenterZ=0 NormalX=0 NormalY=0 NormalZ=1 AngleXU=0 Radius=1
    g5: Circle CenterX=-3.5 CenterY=1e-16 CenterZ=0 NormalX=0 NormalY=0 NormalZ=1 AngleXU=0 Radius=1
    g6: Circle CenterX=-4.8 CenterY=1e-16 CenterZ=0 NormalX=0 NormalY=0 NormalZ=1 AngleXU=0 Radius=1
    g7: BSplineCurve PolesCount=3 KnotsCount=2 Degree=2 IsPeriodic=0
    g8: GeomPoint X=-3.5 Y=1.3 Z=0
    g9: GeomPoint X=-4.8 Y=1e-16 Z=0
    g10: LineSegment StartX=-3.5 StartY=1.3 StartZ=0 EndX=-3.5 EndY=1.5 EndZ=0
  constraints (24):
    c: Horizontal(g0)
    c: Distance(g0) = 1.9
    c: Block(g0)
    c: Coincident(g1,g0)
    c: Vertical(g1)
    c: Coincident(g2,g1)
    c: Horizontal(g2)
    c: Coincident(g3,g0)
    c: Horizontal(g3)
    c: Distance(g3) = 1.3
    c: Weight(g4) = 1
    c: Equal(g4,g5)
    c: Coincident(g5,g0)
    c: Equal(g4,g6)
    c: Coincident(g7,g3)
    c: InternalAlignment(g4,g7)
    c: InternalAlignment(g5,g7)
    c: InternalAlignment(g6,g7)
    c: InternalAlignment(g8,g7)
    c: InternalAlignment(g9,g7)
    c: Coincident(g10,g7)
    c: Coincident(g10,g2)
    c: Vertical(g10)
    c: Block(g10)
FEATURE [Part::Feature] Face035
  shape: bbox 3.2 x 1.5 x 2e-07 mm, 1 faces, 0 solids (baked)
FEATURE [Part::Revolution] Revolve039  label="backCaseScrewRetainer"
  Angle = 360
  Axis = (0,1,0)
  Base = (0,0,0)
  FaceMakerClass = Part::FaceMakerBullseye
  Placement = pos=(12.5,3,62) rot=(0,0,1;0rad)
  Solid = false
  Source = -> Face035
  Symmetric = false
FEATURE [Part::Feature] Face036
  shape: bbox 3.2 x 1.5 x 2e-07 mm, 1 faces, 0 solids (baked)
FEATURE [Part::Feature] Face039
  shape: bbox 4.8 x 30.2 x 2e-07 mm, 1 faces, 0 solids (baked)
FEATURE [Part::Revolution] Revolve043  label="frontCaseScrewPost002"
  Angle = 360
  Axis = (0,1,0)
  Base = (0,0,0)
  FaceMakerClass = Part::FaceMakerBullseye
  Placement = pos=(89.5,4.5,3.5) rot=(0,0,1;0rad)
  Solid = false
  Source = -> Face039
  Symmetric = false
FEATURE [Part::Feature] Face042
  shape: bbox 4.8 x 30.2 x 2e-07 mm, 1 faces, 0 solids (baked)
FEATURE [Part::Revolution] Revolve046  label="frontCaseScrewPost003"
  Angle = 360
  Axis = (0,1,0)
  Base = (0,0,0)
  FaceMakerClass = Part::FaceMakerBullseye
  Placement = pos=(89.5,4.5,68.5) rot=(0,0,1;0rad)
  Solid = false
  Source = -> Face042
  Symmetric = false
FEATURE [Part::Feature] Face043
  shape: bbox 3.2 x 1.5 x 2e-07 mm, 1 faces, 0 solids (baked)
FEATURE [Part::Revolution] Revolve047  label="frontCaseScrewRetainer002"
  Angle = 360
  Axis = (0,1,0)
  Base = (0,0,0)
  FaceMakerClass = Part::FaceMakerBullseye
  Placement = pos=(89.5,3,68.5) rot=(0,0,1;0rad)
  Solid = false
  Source = -> Face043
  Symmetric = false
FEATURE [Part::Feature] Face044
  shape: bbox 3.2 x 1.5 x 2e-07 mm, 1 faces, 0 solids (baked)
FEATURE [Part::Revolution] Revolve048  label="frontCaseScrewRetainer003"
  Angle = 360
  Axis = (0,1,0)
  Base = (0,0,0)
  FaceMakerClass = Part::FaceMakerBullseye
  Placement = pos=(89.5,3,3.5) rot=(0,0,1;0rad)
  Solid = false
  Source = -> Face044
  Symmetric = false
FEATURE [App::MeasureDistance] Distance002  label="Distance: 1.67 mm"
  Distance = 1.66921
  P1 = (99.2361,4.7524,71.7)
  P2 = (99.2347,6.42161,71.7)
FEATURE [Sketcher::SketchObject] Sketch018
  FullyConstrained = true
  sketch-geometry (7):
    g0: LineSegment StartX=0 StartY=0 StartZ=0 EndX=0 EndY=6 EndZ=0
    g1: Circle CenterX=0 CenterY=0 CenterZ=0 NormalX=0 NormalY=0 NormalZ=1 AngleXU=0 Radius=1
    g2: Circle CenterX=8 CenterY=6 CenterZ=0 NormalX=0 NormalY=0 NormalZ=1 AngleXU=0 Radius=1
    g3: BSplineCurve PolesCount=3 KnotsCount=2 Degree=2 IsPeriodic=0
    g4: GeomPoint X=0 Y=0 Z=0
    g5: GeomPoint X=8 Y=6 Z=0
    g6: LineSegment StartX=0 StartY=6 StartZ=0 EndX=8 EndY=6 EndZ=0
  constraints (14):
    c: Coincident(g0,g-1)
    c: Distance(g0) = 6
    c: Vertical(g0)
    c: Coincident(g3,g0)
    c: Weight(g1) = 1
    c: Equal(g1,g2)
    c: InternalAlignment(g1,g3)
    c: InternalAlignment(g2,g3)
    c: InternalAlignment(g4,g3)
    c: InternalAlignment(g5,g3)
    c: Block(g3)
    c: Coincident(g6,g0)
    c: Coincident(g6,g3)
    c: Horizontal(g6)
FEATURE [Part::Extrusion] Extrude012  label="caseScrewPillarBracket"
  Base = -> Sketch018
  Dir = (0,0,1)
  DirMode = 2
  FaceMakerClass = Part::FaceMakerBullseye
  LengthFwd = 2.4
  LengthRev = 0
  Placement = pos=(15.76,29,8.8) rot=(0,1,0;0rad)
  Solid = true
  Symmetric = false
FEATURE [Sketcher::SketchObject] Sketch019
  FullyConstrained = true
  sketch-geometry (7):
    g0: LineSegment StartX=0 StartY=0 StartZ=0 EndX=0 EndY=6 EndZ=0
    g1: Circle CenterX=0 CenterY=0 CenterZ=0 NormalX=0 NormalY=0 NormalZ=1 AngleXU=0 Radius=1
    g2: Circle CenterX=8 CenterY=6 CenterZ=0 NormalX=0 NormalY=0 NormalZ=1 AngleXU=0 Radius=1
    g3: BSplineCurve PolesCount=3 KnotsCount=2 Degree=2 IsPeriodic=0
    g4: GeomPoint X=0 Y=0 Z=0
    g5: GeomPoint X=8 Y=6 Z=0
    g6: LineSegment StartX=0 StartY=6 StartZ=0 EndX=8 EndY=6 EndZ=0
  constraints (14):
    c: Coincident(g0,g-1)
    c: Distance(g0) = 6
    c: Vertical(g0)
    c: Coincident(g3,g0)
    c: Weight(g1) = 1
    c: Equal(g1,g2)
    c: InternalAlignment(g1,g3)
    c: InternalAlignment(g2,g3)
    c: InternalAlignment(g4,g3)
    c: InternalAlignment(g5,g3)
    c: Block(g3)
    c: Coincident(g6,g0)
    c: Coincident(g6,g3)
    c: Horizontal(g6)
FEATURE [Part::Extrusion] Extrude013  label="caseScrewPillarBracket001"
  Base = -> Sketch019
  Dir = (0,0,1)
  DirMode = 2
  FaceMakerClass = Part::FaceMakerBullseye
  LengthFwd = 2.4
  LengthRev = 0
  Placement = pos=(15.76,29,60.8) rot=(0,0,1;0rad)
  Solid = true
  Symmetric = false
FEATURE [Sketcher::SketchObject] Sketch020
  FullyConstrained = true
  sketch-geometry (7):
    g0: LineSegment StartX=0 StartY=0 StartZ=0 EndX=0 EndY=6 EndZ=0
    g1: Circle CenterX=0 CenterY=0 CenterZ=0 NormalX=0 NormalY=0 NormalZ=1 AngleXU=0 Radius=1
    g2: Circle CenterX=8 CenterY=6 CenterZ=0 NormalX=0 NormalY=0 NormalZ=1 AngleXU=0 Radius=1
    g3: BSplineCurve PolesCount=3 KnotsCount=2 Degree=2 IsPeriodic=0
    g4: GeomPoint X=0 Y=0 Z=0
    g5: GeomPoint X=8 Y=6 Z=0
    g6: LineSegment StartX=0 StartY=6 StartZ=0 EndX=8 EndY=6 EndZ=0
  constraints (14):
    c: Coincident(g0,g-1)
    c: Distance(g0) = 6
    c: Vertical(g0)
    c: Coincident(g3,g0)
    c: Weight(g1) = 1
    c: Equal(g1,g2)
    c: InternalAlignment(g1,g3)
    c: InternalAlignment(g2,g3)
    c: InternalAlignment(g4,g3)
    c: InternalAlignment(g5,g3)
    c: Block(g3)
    c: Coincident(g6,g0)
    c: Coincident(g6,g3)
    c: Horizontal(g6)
FEATURE [Part::Extrusion] Extrude014  label="caseScrewPillarBracket002"
  Base = -> Sketch020
  Dir = (0,0,1)
  DirMode = 2
  FaceMakerClass = Part::FaceMakerBullseye
  LengthFwd = 2.4
  LengthRev = 0
  Placement = pos=(13.7,29,13.26) rot=(0,-1,0;1.5708rad)
  Solid = true
  Symmetric = false
FEATURE [Sketcher::SketchObject] Sketch021
  FullyConstrained = true
  sketch-geometry (7):
    g0: LineSegment StartX=0 StartY=0 StartZ=0 EndX=0 EndY=6 EndZ=0
    g1: Circle CenterX=0 CenterY=0 CenterZ=0 NormalX=0 NormalY=0 NormalZ=1 AngleXU=0 Radius=1
    g2: Circle CenterX=8 CenterY=6 CenterZ=0 NormalX=0 NormalY=0 NormalZ=1 AngleXU=0 Radius=1
    g3: BSplineCurve PolesCount=3 KnotsCount=2 Degree=2 IsPeriodic=0
    g4: GeomPoint X=0 Y=0 Z=0
    g5: GeomPoint X=8 Y=6 Z=0
    g6: LineSegment StartX=0 StartY=6 StartZ=0 EndX=8 EndY=6 EndZ=0
  constraints (14):
    c: Coincident(g0,g-1)
    c: Distance(g0) = 6
    c: Vertical(g0)
    c: Coincident(g3,g0)
    c: Weight(g1) = 1
    c: Equal(g1,g2)
    c: InternalAlignment(g1,g3)
    c: InternalAlignment(g2,g3)
    c: InternalAlignment(g4,g3)
    c: InternalAlignment(g5,g3)
    c: Block(g3)
    c: Coincident(g6,g0)
    c: Coincident(g6,g3)
    c: Horizontal(g6)
FEATURE [Part::Extrusion] Extrude015  label="caseScrewPillarBracket003"
  Base = -> Sketch021
  Dir = (0,0,1)
  DirMode = 2
  FaceMakerClass = Part::FaceMakerBullseye
  LengthFwd = 2.4
  LengthRev = 0
  Placement = pos=(11.3,29,58.74) rot=(0,1,0;1.5708rad)
  Solid = true
  Symmetric = false
FEATURE [Sketcher::SketchObject] Sketch022
  FullyConstrained = true
  sketch-geometry (7):
    g0: LineSegment StartX=0 StartY=0 StartZ=0 EndX=0 EndY=6 EndZ=0
    g1: Circle CenterX=0 CenterY=0 CenterZ=0 NormalX=0 NormalY=0 NormalZ=1 AngleXU=0 Radius=1
    g2: Circle CenterX=8 CenterY=6 CenterZ=0 NormalX=0 NormalY=0 NormalZ=1 AngleXU=0 Radius=1
    g3: BSplineCurve PolesCount=3 KnotsCount=2 Degree=2 IsPeriodic=0
    g4: GeomPoint X=0 Y=0 Z=0
    g5: GeomPoint X=8 Y=6 Z=0
    g6: LineSegment StartX=0 StartY=6 StartZ=0 EndX=8 EndY=6 EndZ=0
  constraints (14):
    c: Coincident(g0,g-1)
    c: Distance(g0) = 6
    c: Vertical(g0)
    c: Coincident(g3,g0)
    c: Weight(g1) = 1
    c: Equal(g1,g2)
    c: InternalAlignment(g1,g3)
    c: InternalAlignment(g2,g3)
    c: InternalAlignment(g4,g3)
    c: InternalAlignment(g5,g3)
    c: Block(g3)
    c: Coincident(g6,g0)
    c: Coincident(g6,g3)
    c: Horizontal(g6)
FEATURE [Part::Extrusion] Extrude016  label="caseScrewPillarBracket004"
  Base = -> Sketch022
  Dir = (0,0,1)
  DirMode = 2
  FaceMakerClass = Part::FaceMakerBullseye
  LengthFwd = 2.4
  LengthRev = 0
  Placement = pos=(88.3,29,65.23) rot=(0,1,0;1.5708rad)
  Solid = true
  Symmetric = false
FEATURE [Sketcher::SketchObject] Sketch023
  FullyConstrained = true
  sketch-geometry (7):
    g0: LineSegment StartX=0 StartY=0 StartZ=0 EndX=0 EndY=6 EndZ=0
    g1: Circle CenterX=0 CenterY=0 CenterZ=0 NormalX=0 NormalY=0 NormalZ=1 AngleXU=0 Radius=1
    g2: Circle CenterX=8 CenterY=6 CenterZ=0 NormalX=0 NormalY=0 NormalZ=1 AngleXU=0 Radius=1
    g3: BSplineCurve PolesCount=3 KnotsCount=2 Degree=2 IsPeriodic=0
    g4: GeomPoint X=0 Y=0 Z=0
    g5: GeomPoint X=8 Y=6 Z=0
    g6: LineSegment StartX=0 StartY=6 StartZ=0 EndX=8 EndY=6 EndZ=0
  constraints (14):
    c: Coincident(g0,g-1)
    c: Distance(g0) = 6
    c: Vertical(g0)
    c: Coincident(g3,g0)
    c: Weight(g1) = 1
    c: Equal(g1,g2)
    c: InternalAlignment(g1,g3)
    c: InternalAlignment(g2,g3)
    c: InternalAlignment(g4,g3)
    c: InternalAlignment(g5,g3)
    c: Block(g3)
    c: Coincident(g6,g0)
    c: Coincident(g6,g3)
    c: Horizontal(g6)
FEATURE [Part::Extrusion] Extrude017  label="caseScrewPillarBracket005"
  Base = -> Sketch023
  Dir = (0,0,1)
  DirMode = 2
  FaceMakerClass = Part::FaceMakerBullseye
  LengthFwd = 2.4
  LengthRev = 0
  Placement = pos=(90.7,29,6.77) rot=(0,-1,0;1.5708rad)
  Solid = true
  Symmetric = false
FEATURE [Sketcher::SketchObject] Sketch024
  FullyConstrained = true
  sketch-geometry (7):
    g0: LineSegment StartX=0 StartY=0 StartZ=0 EndX=0 EndY=6 EndZ=0
    g1: Circle CenterX=0 CenterY=0 CenterZ=0 NormalX=0 NormalY=0 NormalZ=1 AngleXU=0 Radius=1
    g2: Circle CenterX=8 CenterY=6 CenterZ=0 NormalX=0 NormalY=0 NormalZ=1 AngleXU=0 Radius=1
    g3: BSplineCurve PolesCount=3 KnotsCount=2 Degree=2 IsPeriodic=0
    g4: GeomPoint X=0 Y=0 Z=0
    g5: GeomPoint X=8 Y=6 Z=0
    g6: LineSegment StartX=0 StartY=6 StartZ=0 EndX=8 EndY=6 EndZ=0
  constraints (14):
    c: Coincident(g0,g-1)
    c: Distance(g0) = 6
    c: Vertical(g0)
    c: Coincident(g3,g0)
    c: Weight(g1) = 1
    c: Equal(g1,g2)
    c: InternalAlignment(g1,g3)
    c: InternalAlignment(g2,g3)
    c: InternalAlignment(g4,g3)
    c: InternalAlignment(g5,g3)
    c: Block(g3)
    c: Coincident(g6,g0)
    c: Coincident(g6,g3)
    c: Horizontal(g6)
FEATURE [Part::Extrusion] Extrude018  label="caseScrewPillarBracket006"
  Base = -> Sketch024
  Dir = (0,0,1)
  DirMode = 2
  FaceMakerClass = Part::FaceMakerBullseye
  LengthFwd = 2.4
  LengthRev = 0
  Placement = pos=(103.7,29,6.77) rot=(0,-1,0;1.5708rad)
  Solid = true
  Symmetric = false
FEATURE [Sketcher::SketchObject] Sketch025
  FullyConstrained = true
  sketch-geometry (7):
    g0: LineSegment StartX=0 StartY=0 StartZ=0 EndX=0 EndY=6 EndZ=0
    g1: Circle CenterX=0 CenterY=0 CenterZ=0 NormalX=0 NormalY=0 NormalZ=1 AngleXU=0 Radius=1
    g2: Circle CenterX=8 CenterY=6 CenterZ=0 NormalX=0 NormalY=0 NormalZ=1 AngleXU=0 Radius=1
    g3: BSplineCurve PolesCount=3 KnotsCount=2 Degree=2 IsPeriodic=0
    g4: GeomPoint X=0 Y=0 Z=0
    g5: GeomPoint X=8 Y=6 Z=0
    g6: LineSegment StartX=0 StartY=6 StartZ=0 EndX=8 EndY=6 EndZ=0
  constraints (14):
    c: Coincident(g0,g-1)
    c: Distance(g0) = 6
    c: Vertical(g0)
    c: Coincident(g3,g0)
    c: Weight(g1) = 1
    c: Equal(g1,g2)
    c: InternalAlignment(g1,g3)
    c: InternalAlignment(g2,g3)
    c: InternalAlignment(g4,g3)
    c: InternalAlignment(g5,g3)
    c: Block(g3)
    c: Coincident(g6,g0)
    c: Coincident(g6,g3)
    c: Horizontal(g6)
FEATURE [Part::Extrusion] Extrude019  label="caseScrewPillarBracket007"
  Base = -> Sketch025
  Dir = (0,0,1)
  DirMode = 2
  FaceMakerClass = Part::FaceMakerBullseye
  LengthFwd = 2.4
  LengthRev = 0
  Placement = pos=(101.3,29,65.23) rot=(0,1,0;1.5708rad)
  Solid = true
  Symmetric = false
FEATURE [Part::Box] Box011  label="frontCaseScrewPillarBracket"
  AttacherType = Attacher::AttachEngine3D
  Height = 2.4
  Length = 16
  Placement = pos=(87,28,2.3) rot=(0,0,1;0rad)
  Width = 7
FEATURE [Part::Box] Box012  label="frontCaseScrewPillarBracket001"
  AttacherType = Attacher::AttachEngine3D
  Height = 2.4
  Length = 16
  Placement = pos=(87,28,67.3) rot=(0,0,1;0rad)
  Width = 7
FEATURE [Sketcher::SketchObject] Sketch026
  FullyConstrained = true
  sketch-geometry (17):
    g0: Circle CenterX=-3.5 CenterY=23.5 CenterZ=0 NormalX=0 NormalY=0 NormalZ=1 AngleXU=0 Radius=1
    g1: Circle CenterX=-1 CenterY=15.25 CenterZ=0 NormalX=0 NormalY=0 NormalZ=1 AngleXU=0 Radius=1
    g2: Circle CenterX=-3.5 CenterY=7 CenterZ=0 NormalX=0 NormalY=0 NormalZ=1 AngleXU=0 Radius=1
    g3: BSplineCurve PolesCount=3 KnotsCount=2 Degree=2 IsPeriodic=0
    g4: GeomPoint X=-3.5 Y=23.5 Z=0
    g5: GeomPoint X=-3.5 Y=7 Z=0
    g6: Circle CenterX=-4.8 CenterY=30.5 CenterZ=0 NormalX=0 NormalY=0 NormalZ=1 AngleXU=0 Radius=1
    g7: Circle CenterX=-3.5 CenterY=30.5 CenterZ=0 NormalX=0 NormalY=0 NormalZ=1 AngleXU=0 Radius=1
    g8: Circle CenterX=-3.5 CenterY=29.2 CenterZ=0 NormalX=0 NormalY=0 NormalZ=1 AngleXU=0 Radius=1
    g9: BSplineCurve PolesCount=3 KnotsCount=2 Degree=2 IsPeriodic=0
    g10: GeomPoint X=-4.8 Y=30.5 Z=0
    g11: GeomPoint X=-3.5 Y=29.2 Z=0
    g12: LineSegment StartX=-3.5 StartY=29.2 StartZ=0 EndX=-3.5 EndY=23.5 EndZ=0
    g13: LineSegment StartX=-4.8 StartY=30.5 StartZ=0 EndX=0 EndY=30.5 EndZ=0
    g14: LineSegment StartX=-3.5 StartY=5 StartZ=0 EndX=-3.5 EndY=7 EndZ=0
    g15: LineSegment StartX=0 StartY=5 StartZ=0 EndX=0 EndY=30.5 EndZ=0
    g16: LineSegment StartX=-3.5 StartY=5 StartZ=0 EndX=0 EndY=5 EndZ=0
  constraints (33):
    c: Weight(g0) = 1
    c: Equal(g0,g1)
    c: Equal(g0,g2)
    c: InternalAlignment(g0,g3)
    c: InternalAlignment(g1,g3)
    c: InternalAlignment(g2,g3)
    c: InternalAlignment(g4,g3)
    c: InternalAlignment(g5,g3)
    c: Block(g3)
    c: Weight(g6) = 1
    c: Equal(g6,g7)
    c: Equal(g6,g8)
    c: InternalAlignment(g6,g9)
    c: InternalAlignment(g7,g9)
    c: InternalAlignment(g8,g9)
    c: InternalAlignment(g10,g9)
    c: InternalAlignment(g11,g9)
    c: Block(g9)
    c: Coincident(g12,g9)
    c: Coincident(g12,g3)
    c: Vertical(g12)
    c: Coincident(g13,g9)
    c: Horizontal(g13)
    c: Distance(g13) = 4.8
    c: Coincident(g14,g3)
    c: Vertical(g14)
    c: Coincident(g15,g13)
    c: Vertical(g15)
    c: Tangent(g15,g1)
    c: Distance(g14) = 2
    c: Coincident(g16,g14)
    c: Horizontal(g16)
    c: Coincident(g15,g16)
FEATURE [Part::Feature] Face050
  shape: bbox 4.8 x 25.5 x 2e-07 mm, 1 faces, 0 solids (baked)
FEATURE [Part::Revolution] Revolve054  label="moreFrontCaseScrewPost001"
  Angle = 360
  Axis = (0,1,0)
  Base = (0,0,0)
  FaceMakerClass = Part::FaceMakerBullseye
  Placement = pos=(102.5,4.5,3.5) rot=(0,0,1;0rad)
  Solid = false
  Source = -> Face050
  Symmetric = false
FEATURE [Part::Feature] Face051
  shape: bbox 4.8 x 25.5 x 2e-07 mm, 1 faces, 0 solids (baked)
FEATURE [Part::Revolution] Revolve055  label="moreFrontCaseScrewPost002"
  Angle = 360
  Axis = (0,1,0)
  Base = (0,0,0)
  FaceMakerClass = Part::FaceMakerBullseye
  Placement = pos=(102.5,4.5,68.5) rot=(0,0,1;0rad)
  Solid = false
  Source = -> Face051
  Symmetric = false
FEATURE [Sketcher::SketchObject] Sketch027
  FullyConstrained = true
  sketch-geometry (10):
    g0: LineSegment StartX=-1.6 StartY=4.7 StartZ=0 EndX=-1.6 EndY=1.7 EndZ=0
    g1: LineSegment StartX=-3.5 StartY=4.7 StartZ=0 EndX=-1.6 EndY=4.7 EndZ=0
    g2: LineSegment StartX=-1.6 StartY=1.7 StartZ=0 EndX=-1.6 EndY=1.5 EndZ=0
    g3: LineSegment StartX=-1.6 StartY=1.5 StartZ=0 EndX=-5.2 EndY=1.5 EndZ=0
    g4: Circle CenterX=-3.5 CenterY=4.7 CenterZ=0 NormalX=0 NormalY=0 NormalZ=1 AngleXU=0 Radius=1
    g5: Circle CenterX=-3.59627 CenterY=2.99743 CenterZ=0 NormalX=0 NormalY=0 NormalZ=1 AngleXU=0 Radius=1
    g6: Circle CenterX=-5.2 CenterY=1.5 CenterZ=0 NormalX=0 NormalY=0 NormalZ=1 AngleXU=0 Radius=1
    g7: BSplineCurve PolesCount=3 KnotsCount=2 Degree=2 IsPeriodic=0
    g8: GeomPoint X=-3.5 Y=4.7 Z=0
    g9: GeomPoint X=-5.2 Y=1.5 Z=0
  constraints (23):
    c: Vertical(g0)
    c: Distance(g0) = 3
    c: Coincident(g1,g0)
    c: Horizontal(g1)
    c: Block(g0)
    c: Block(g1)
    c: Coincident(g2,g0)
    c: Vertical(g2)
    c: Distance(g2) = 0.2
    c: Coincident(g3,g2)
    c: Horizontal(g3)
    c: Block(g3)
    c: Coincident(g7,g1)
    c: Weight(g4) = 1
    c: Equal(g4,g5)
    c: Equal(g4,g6)
    c: Coincident(g7,g3)
    c: InternalAlignment(g4,g7)
    c: InternalAlignment(g5,g7)
    c: InternalAlignment(g6,g7)
    c: InternalAlignment(g8,g7)
    c: InternalAlignment(g9,g7)
    c: Block(g7)
FEATURE [Sketcher::SketchObject] Sketch028
  FullyConstrained = true
  sketch-geometry (18):
    g0: LineSegment StartX=0 StartY=3e-16 StartZ=0 EndX=0 EndY=1.7 EndZ=0
    g1: LineSegment StartX=-3.5 StartY=0 StartZ=0 EndX=-3.5 EndY=0.9 EndZ=0
    g2: Circle CenterX=-2.7 CenterY=1.7 CenterZ=0 NormalX=0 NormalY=0 NormalZ=1 AngleXU=0 Radius=1
    g3: Circle CenterX=-3.5 CenterY=1.7 CenterZ=0 NormalX=0 NormalY=0 NormalZ=1 AngleXU=0 Radius=1
    g4: Circle CenterX=-3.5 CenterY=0.9 CenterZ=0 NormalX=0 NormalY=0 NormalZ=1 AngleXU=0 Radius=1
    g5: BSplineCurve PolesCount=3 KnotsCount=2 Degree=2 IsPeriodic=0
    g6: GeomPoint X=-2.7 Y=1.7 Z=0
    g7: GeomPoint X=-3.5 Y=0.9 Z=0
    g8: LineSegment StartX=-3.5 StartY=0 StartZ=0 EndX=-3.5 EndY=-7 EndZ=0
    g9: LineSegment StartX=0 StartY=3e-16 StartZ=0 EndX=0 EndY=-7 EndZ=0
    g10: LineSegment StartX=-3.5 StartY=-7 StartZ=0 EndX=0 EndY=-7 EndZ=0
    g11: LineSegment StartX=-2.7 StartY=1.7 StartZ=0 EndX=-1.6 EndY=1.7 EndZ=0
    g12: LineSegment StartX=0 StartY=1.7 StartZ=0 EndX=0 EndY=4.5 EndZ=0
    g13: LineSegment StartX=0 StartY=4.5 StartZ=0 EndX=0 EndY=10.8 EndZ=0
    g14: LineSegment StartX=0 StartY=10.8 StartZ=0 EndX=-2 EndY=10.8 EndZ=0
    g15: LineSegment StartX=-1.6 StartY=4.7 StartZ=0 EndX=-1.6 EndY=1.7 EndZ=0
    g16: LineSegment StartX=-1.6 StartY=4.7 StartZ=0 EndX=-2 EndY=4.7 EndZ=0
    g17: LineSegment StartX=-2 StartY=4.7 StartZ=0 EndX=-2 EndY=10.8 EndZ=0
  constraints (44):
    c: Vertical(g0)
    c: Vertical(g1)
    c: Distance(g1) = 0.9
    c: Block(g0)
    c: Distance(g0) = 1.7
    c: Weight(g2) = 1
    c: Equal(g2,g3)
    c: Equal(g2,g4)
    c: Coincident(g5,g1)
    c: InternalAlignment(g2,g5)
    c: InternalAlignment(g3,g5)
    c: InternalAlignment(g4,g5)
    c: InternalAlignment(g6,g5)
    c: InternalAlignment(g7,g5)
    c: Block(g5)
    c: Coincident(g8,g1)
    c: Vertical(g8)
    c: Distance(g8) = 7
    c: Vertical(g9)
    c: Equal(g8,g9) = 7
    c: Coincident(g9,g0)
    c: Coincident(g10,g8)
    c: Coincident(g10,g9)
    c: Horizontal(g10)
    c: Coincident(g11,g5)
    c: Horizontal(g11)
    c: Coincident(g12,g0)
    c: Vertical(g12)
    c: Distance(g12) = 2.8
    c: Coincident(g13,g12)
    c: Vertical(g13)
    c: Distance(g13) = 6.3
    c: Coincident(g14,g13)
    c: Horizontal(g14)
    c: Distance(g14) = 2
    c: Vertical(g15)
    c: Distance(g15) = 3
    c: Block(g11)
    c: Coincident(g15,g11)
    c: Coincident(g16,g15)
    c: Horizontal(g16)
    c: Coincident(g17,g16)
    c: Coincident(g17,g14)
    c: Vertical(g17)
FEATURE [Part::Revolution] Revolve040  label="backCaseScrewRetainer001"
  Angle = 360
  Axis = (0,1,0)
  Base = (0,0,0)
  FaceMakerClass = Part::FaceMakerBullseye
  Placement = pos=(12.5,3,10) rot=(0,0,1;0rad)
  Solid = false
  Source = -> Face036
  Symmetric = false
FEATURE [Part::Feature] Face055
  shape: bbox 3.5 x 30.2 x 2e-07 mm, 1 faces, 0 solids (baked)
FEATURE [Part::Revolution] Revolve059  label="backCaseScrewPost"
  Angle = 360
  Axis = (0,1,0)
  Base = (0,0,0)
  FaceMakerClass = Part::FaceMakerBullseye
  Placement = pos=(12.5,4.5,10) rot=(0,0,1;0rad)
  Solid = false
  Source = -> Face055
  Symmetric = false
FEATURE [Part::Feature] Face056
  shape: bbox 3.5 x 30.2 x 2e-07 mm, 1 faces, 0 solids (baked)
FEATURE [Part::Revolution] Revolve060  label="backCaseScrewPost001"
  Angle = 360
  Axis = (0,1,0)
  Base = (0,0,0)
  FaceMakerClass = Part::FaceMakerBullseye
  Placement = pos=(12.5,4.5,62) rot=(0,0,1;0rad)
  Solid = false
  Source = -> Face056
  Symmetric = false
FEATURE [Part::Feature] Face057
  shape: bbox 3.5 x 17.8 x 2e-07 mm, 1 faces, 0 solids (baked)
FEATURE [Part::Revolution] Revolve061  label="removeToCreateScrewAndThreadedInsertHole"
  Angle = 360
  Axis = (0,1,0)
  Base = (0,0,0)
  FaceMakerClass = Part::FaceMakerBullseye
  Placement = pos=(12.5,0,10) rot=(0,0,1;0rad)
  Solid = false
  Source = -> Face057
  Symmetric = false
FEATURE [Part::Feature] Face058
  shape: bbox 3.5 x 17.8 x 2e-07 mm, 1 faces, 0 solids (baked)
FEATURE [Part::Revolution] Revolve062  label="removeToCreateScrewAndThreadedInsertHole001"
  Angle = 360
  Axis = (0,1,0)
  Base = (0,0,0)
  FaceMakerClass = Part::FaceMakerBullseye
  Placement = pos=(12.5,0,62) rot=(0,0,1;0rad)
  Solid = false
  Source = -> Face058
  Symmetric = false
FEATURE [Part::Feature] Face059
  shape: bbox 3.5 x 17.8 x 2e-07 mm, 1 faces, 0 solids (baked)
FEATURE [Part::Revolution] Revolve063  label="removeToCreateScrewAndThreadedInsertHole002"
  Angle = 360
  Axis = (0,1,0)
  Base = (0,0,0)
  FaceMakerClass = Part::FaceMakerBullseye
  Placement = pos=(89.5,0,68.5) rot=(0,0,1;0rad)
  Solid = false
  Source = -> Face059
  Symmetric = false
FEATURE [Part::Feature] Face060
  shape: bbox 3.5 x 17.8 x 2e-07 mm, 1 faces, 0 solids (baked)
FEATURE [Part::Revolution] Revolve064  label="removeToCreateScrewAndThreadedInsertHole003"
  Angle = 360
  Axis = (0,1,0)
  Base = (0,0,0)
  FaceMakerClass = Part::FaceMakerBullseye
  Placement = pos=(89.5,0,3.5) rot=(0,0,1;0rad)
  Solid = false
  Source = -> Face060
  Symmetric = false
FEATURE [Part::Feature] Face061
  shape: bbox 3.5 x 17.8 x 2e-07 mm, 1 faces, 0 solids (baked)
FEATURE [Part::Revolution] Revolve065  label="removeToCreateScrewAndThreadedInsertHole004"
  Angle = 360
  Axis = (0,1,0)
  Base = (0,0,0)
  FaceMakerClass = Part::FaceMakerBullseye
  Placement = pos=(102.5,4.7,3.5) rot=(0,0,1;0rad)
  Solid = false
  Source = -> Face061
  Symmetric = false
FEATURE [Part::Feature] Face062
  shape: bbox 3.5 x 17.8 x 2e-07 mm, 1 faces, 0 solids (baked)
FEATURE [Part::Revolution] Revolve066  label="removeToCreateScrewAndThreadedInsertHole005"
  Angle = 360
  Axis = (0,1,0)
  Base = (0,0,0)
  FaceMakerClass = Part::FaceMakerBullseye
  Placement = pos=(102.5,4.7,68.5) rot=(0,0,1;0rad)
  Solid = false
  Source = -> Face062
  Symmetric = false
FEATURE [Part::MultiFuse] Fusion047  label="makeHoles"
  Shapes = -> [Revolve066,Revolve065,Revolve064,Revolve063,Revolve062,Revolve061]
FEATURE [Part::Feature] Face063
  shape: bbox 3.6 x 3.2 x 2e-07 mm, 1 faces, 0 solids (baked)
FEATURE [Part::Revolution] Revolve067  label="moreFrontCaseScrewRetainer002"
  Angle = 360
  Axis = (0,1,0)
  Base = (0,0,0)
  FaceMakerClass = Part::FaceMakerBullseye
  Placement = pos=(102.5,4.5,68.5) rot=(0,0,1;0rad)
  Solid = false
  Source = -> Face063
  Symmetric = false
FEATURE [Part::Feature] Face064
  shape: bbox 3.6 x 3.2 x 2e-07 mm, 1 faces, 0 solids (baked)
FEATURE [Part::Revolution] Revolve068  label="moreFrontCaseScrewRetainer003"
  Angle = 360
  Axis = (0,1,0)
  Base = (0,0,0)
  FaceMakerClass = Part::FaceMakerBullseye
  Placement = pos=(102.5,4.5,3.5) rot=(0,0,1;0rad)
  Solid = false
  Source = -> Face064
  Symmetric = false
FEATURE [Part::Feature] Face065
  shape: bbox 3.5 x 17.8 x 2e-07 mm, 1 faces, 0 solids (baked)
FEATURE [Part::Revolution] Revolve069  label="removeToCreateScrewAndThreadedInsertHole006"
  Angle = 360
  Axis = (0,1,0)
  Base = (0,0,0)
  FaceMakerClass = Part::FaceMakerBullseye
  Placement = pos=(12.5,0,10) rot=(0,0,1;0rad)
  Solid = false
  Source = -> Face065
  Symmetric = false
FEATURE [Part::Feature] Face066
  shape: bbox 3.5 x 17.8 x 2e-07 mm, 1 faces, 0 solids (baked)
FEATURE [Part::Revolution] Revolve070  label="removeToCreateScrewAndThreadedInsertHole007"
  Angle = 360
  Axis = (0,1,0)
  Base = (0,0,0)
  FaceMakerClass = Part::FaceMakerBullseye
  Placement = pos=(12.5,0,62) rot=(0,0,1;0rad)
  Solid = false
  Source = -> Face066
  Symmetric = false
FEATURE [Part::Feature] Face067
  shape: bbox 3.5 x 17.8 x 2e-07 mm, 1 faces, 0 solids (baked)
FEATURE [Part::Revolution] Revolve071  label="removeToCreateScrewAndThreadedInsertHole008"
  Angle = 360
  Axis = (0,1,0)
  Base = (0,0,0)
  FaceMakerClass = Part::FaceMakerBullseye
  Placement = pos=(89.5,0,68.5) rot=(0,0,1;0rad)
  Solid = false
  Source = -> Face067
  Symmetric = false
FEATURE [Part::Feature] Face068
  shape: bbox 3.5 x 17.8 x 2e-07 mm, 1 faces, 0 solids (baked)
FEATURE [Part::Revolution] Revolve072  label="removeToCreateScrewAndThreadedInsertHole009"
  Angle = 360
  Axis = (0,1,0)
  Base = (0,0,0)
  FaceMakerClass = Part::FaceMakerBullseye
  Placement = pos=(89.5,0,3.5) rot=(0,0,1;0rad)
  Solid = false
  Source = -> Face068
  Symmetric = false
FEATURE [Part::Feature] Face069
  shape: bbox 3.5 x 17.8 x 2e-07 mm, 1 faces, 0 solids (baked)
FEATURE [Part::Feature] Face070
  shape: bbox 3.5 x 17.8 x 2e-07 mm, 1 faces, 0 solids (baked)
FEATURE [Part::Revolution] Revolve073  label="removeToCreateScrewAndThreadedInsertHole010"
  Angle = 360
  Axis = (0,1,0)
  Base = (0,0,0)
  FaceMakerClass = Part::FaceMakerBullseye
  Placement = pos=(102.5,4.7,3.5) rot=(0,0,1;0rad)
  Solid = false
  Source = -> Face069
  Symmetric = false
FEATURE [Part::Revolution] Revolve074  label="removeToCreateScrewAndThreadedInsertHole011"
  Angle = 360
  Axis = (0,1,0)
  Base = (0,0,0)
  FaceMakerClass = Part::FaceMakerBullseye
  Placement = pos=(102.5,4.7,68.5) rot=(0,0,1;0rad)
  Solid = false
  Source = -> Face070
  Symmetric = false
FEATURE [Part::MultiFuse] Fusion048  label="makeHoles001"
  Shapes = -> [Revolve074,Revolve073,Revolve072,Revolve071,Revolve070,Revolve069]
FEATURE [Part::MultiFuse] Fusion049  label="caseScrewRetainers"
  Shapes = -> [Revolve067,Revolve068,Revolve048,Revolve047,Revolve039,Revolve040]
FEATURE [Part::Cut] Cut015  label="caseScrewRetainers001"
  Base = -> Fusion049
  Tool = -> Fusion048
FEATURE [Part::MultiFuse] Fusion050  label="casePillars"
  Shapes = -> [Revolve055,Revolve054,Revolve043,Revolve046,Revolve059,Revolve060]
FEATURE [Part::Feature] Face071 .. Face076  x6 (patterned run collapsed; names and placements below)
  shape: bbox 3.5 x 17.8 x 2e-07 mm, 1 faces, 0 solids (baked)
FEATURE [Part::Revolution] Revolve075  label="removeToCreateScrewAndThreadedInsertHole012"
  Angle = 360
  Axis = (0,1,0)
  Base = (0,0,0)
  FaceMakerClass = Part::FaceMakerBullseye
  Placement = pos=(12.5,0,10) rot=(0,0,1;0rad)
  Solid = false
  Source = -> Face071
  Symmetric = false
FEATURE [Part::Revolution] Revolve076  label="removeToCreateScrewAndThreadedInsertHole013"
  Angle = 360
  Axis = (0,1,0)
  Base = (0,0,0)
  FaceMakerClass = Part::FaceMakerBullseye
  Placement = pos=(12.5,0,62) rot=(0,0,1;0rad)
  Solid = false
  Source = -> Face072
  Symmetric = false
FEATURE [Part::Revolution] Revolve077  label="removeToCreateScrewAndThreadedInsertHole014"
  Angle = 360
  Axis = (0,1,0)
  Base = (0,0,0)
  FaceMakerClass = Part::FaceMakerBullseye
  Placement = pos=(89.5,0,68.5) rot=(0,0,1;0rad)
  Solid = false
  Source = -> Face073
  Symmetric = false
FEATURE [Part::Revolution] Revolve078  label="removeToCreateScrewAndThreadedInsertHole015"
  Angle = 360
  Axis = (0,1,0)
  Base = (0,0,0)
  FaceMakerClass = Part::FaceMakerBullseye
  Placement = pos=(89.5,0,3.5) rot=(0,0,1;0rad)
  Solid = false
  Source = -> Face074
  Symmetric = false
FEATURE [Part::Revolution] Revolve079  label="removeToCreateScrewAndThreadedInsertHole016"
  Angle = 360
  Axis = (0,1,0)
  Base = (0,0,0)
  FaceMakerClass = Part::FaceMakerBullseye
  Placement = pos=(102.5,4.7,3.5) rot=(0,0,1;0rad)
  Solid = false
  Source = -> Face075
  Symmetric = false
FEATURE [Part::Revolution] Revolve080  label="removeToCreateScrewAndThreadedInsertHole017"
  Angle = 360
  Axis = (0,1,0)
  Base = (0,0,0)
  FaceMakerClass = Part::FaceMakerBullseye
  Placement = pos=(102.5,4.7,68.5) rot=(0,0,1;0rad)
  Solid = false
  Source = -> Face076
  Symmetric = false
FEATURE [Part::MultiFuse] Fusion051  label="makeHoles002"
  Shapes = -> [Revolve080,Revolve079,Revolve078,Revolve077,Revolve076,Revolve075]
FEATURE [Part::Cut] Cut016  label="caesPillars"
  Base = -> Fusion050
  Tool = -> Fusion051
FEATURE [Part::Revolution] Revolve009  label="plugHousing016"
  Angle = 360
  Axis = (0,1,0)
  Base = (0,0,0)
  FaceMakerClass = Part::FaceMakerBullseye
  Placement = pos=(0,0,36.15) rot=(0,0,1;0rad)
  Solid = false
  Source = -> Face012
  Symmetric = false
FEATURE [Part::MultiFuse] Fusion014  label="plugHousing023"
  Placement = pos=(0,0,0) rot=(0,0,1;1.5708rad)
  Shapes = -> [Revolve011,Revolve009]
FEATURE [Part::Revolution] Revolve010  label="plugHousing017"
  Angle = 360
  Axis = (0,1,0)
  Base = (0,0,0)
  FaceMakerClass = Part::FaceMakerBullseye
  Placement = pos=(0,0,36.15) rot=(0,0,1;0rad)
  Solid = false
  Source = -> Face014
  Symmetric = false
FEATURE [Part::MultiFuse] Fusion015  label="plugHousing024"
  Placement = pos=(0,0,0) rot=(0,0,1;1.5708rad)
  Shapes = -> [Revolve010,Revolve015]
FEATURE [Part::Revolution] Revolve014  label="plugHousing026"
  Angle = 360
  Axis = (0,1,0)
  Base = (0,0,0)
  FaceMakerClass = Part::FaceMakerBullseye
  Placement = pos=(0,0,36.15) rot=(0,0,1;0rad)
  Solid = false
  Source = -> Face011
  Symmetric = false
FEATURE [Part::Revolution] Revolve013  label="plugHousing025"
  Angle = 360
  Axis = (0,1,0)
  Base = (0,0,0)
  FaceMakerClass = Part::FaceMakerBullseye
  Placement = pos=(0,0,36.15) rot=(0,0,1;0rad)
  Solid = false
  Source = -> Face015
  Symmetric = false
FEATURE [Part::MultiFuse] Fusion016  label="plugHousing028"
  Placement = pos=(0,19,0) rot=(0,0,1;3.14159rad)
  Shapes = -> [Fusion014,Fusion013]
FEATURE [Part::MultiFuse] Fusion011  label="plugHousing018"
  Placement = pos=(0,0,0) rot=(0,0,1;1.5708rad)
  Shapes = -> [Revolve014,Revolve013]
FEATURE [Part::MultiFuse] Fusion012  label="plugHousing019"
  Placement = pos=(0,19,0) rot=(0,0,1;3.14159rad)
  Shapes = -> [Fusion011,Fusion015]
FEATURE [Part::MultiFuse] Fusion017  label="plugHousing029"
  Placement = pos=(122.621,0,-0.15) rot=(0,0,1;0rad)
  Shapes = -> [Fusion016,Fusion012]
FEATURE [Part::MultiFuse] Fusion052  label="casePillarRetainers"
  Shapes = -> [Extrude012,Extrude013,Extrude014,Extrude015,Extrude016,Extrude017,Extrude018,Extrude019,Box011,Box012]
FEATURE [Part::Feature] Face077
  shape: bbox 3.5 x 17.8 x 2e-07 mm, 1 faces, 0 solids (baked)
FEATURE [Part::Revolution] Revolve081  label="removeToCreateScrewAndThreadedInsertHole018"
  Angle = 360
  Axis = (0,1,0)
  Base = (0,0,0)
  FaceMakerClass = Part::FaceMakerBullseye
  Placement = pos=(62.3,30.3,19.7) rot=(0,0,1;0rad)
  Solid = false
  Source = -> Face077
  Symmetric = false
FEATURE [Part::Feature] Face078
  shape: bbox 3.5 x 17.8 x 2e-07 mm, 1 faces, 0 solids (baked)
FEATURE [Part::Revolution] Revolve082  label="removeToCreateScrewAndThreadedInsertHole019"
  Angle = 360
  Axis = (0,1,0)
  Base = (0,0,0)
  FaceMakerClass = Part::FaceMakerBullseye
  Placement = pos=(62.3,30.3,51.7) rot=(0,0,1;0rad)
  Solid = false
  Source = -> Face078
  Symmetric = false
FEATURE [Part::Feature] Face079
  shape: bbox 3.5 x 17.8 x 2e-07 mm, 1 faces, 0 solids (baked)
FEATURE [Part::Revolution] Revolve083  label="removeToCreateScrewAndThreadedInsertHole020"
  Angle = 360
  Axis = (0,1,0)
  Base = (0,0,0)
  FaceMakerClass = Part::FaceMakerBullseye
  Placement = pos=(30.3,30.3,19.7) rot=(0,0,1;0rad)
  Solid = false
  Source = -> Face079
  Symmetric = false
FEATURE [Part::Feature] Face080
  shape: bbox 3.5 x 17.8 x 2e-07 mm, 1 faces, 0 solids (baked)
FEATURE [Part::Revolution] Revolve084  label="removeToCreateScrewAndThreadedInsertHole021"
  Angle = 360
  Axis = (0,1,0)
  Base = (0,0,0)
  FaceMakerClass = Part::FaceMakerBullseye
  Placement = pos=(30.3,30.3,51.7) rot=(0,0,1;0rad)
  Solid = false
  Source = -> Face080
  Symmetric = false
FEATURE [Part::MultiFuse] Fusion053  label="createThreadedInsertHolesForFan"
  Shapes = -> [Revolve081,Revolve082,Revolve083,Revolve084]
FEATURE [Part::Cut] Cut017  label="fanScrewHousing001"
  Base = -> Fusion046
  Tool = -> Fusion053
FEATURE [Part::Feature] Face081
  shape: bbox 3.5 x 17.8 x 2e-07 mm, 1 faces, 0 solids (baked)
FEATURE [Part::Revolution] Revolve085  label="removeToCreateScrewAndThreadedInsertHole022"
  Angle = 360
  Axis = (0,1,0)
  Base = (0,0,0)
  FaceMakerClass = Part::FaceMakerBullseye
  Placement = pos=(62.3,30.3,19.7) rot=(0,0,1;0rad)
  Solid = false
  Source = -> Face081
  Symmetric = false
FEATURE [Part::Feature] Face082
  shape: bbox 3.5 x 17.8 x 2e-07 mm, 1 faces, 0 solids (baked)
FEATURE [Part::Revolution] Revolve086  label="removeToCreateScrewAndThreadedInsertHole023"
  Angle = 360
  Axis = (0,1,0)
  Base = (0,0,0)
  FaceMakerClass = Part::FaceMakerBullseye
  Placement = pos=(62.3,30.3,51.7) rot=(0,0,1;0rad)
  Solid = false
  Source = -> Face082
  Symmetric = false
FEATURE [Part::Feature] Face083
  shape: bbox 3.5 x 17.8 x 2e-07 mm, 1 faces, 0 solids (baked)
FEATURE [Part::Revolution] Revolve087  label="removeToCreateScrewAndThreadedInsertHole024"
  Angle = 360
  Axis = (0,1,0)
  Base = (0,0,0)
  FaceMakerClass = Part::FaceMakerBullseye
  Placement = pos=(30.3,30.3,19.7) rot=(0,0,1;0rad)
  Solid = false
  Source = -> Face083
  Symmetric = false
FEATURE [Part::Feature] Face084
  shape: bbox 3.5 x 17.8 x 2e-07 mm, 1 faces, 0 solids (baked)
FEATURE [Part::Revolution] Revolve088  label="removeToCreateScrewAndThreadedInsertHole025"
  Angle = 360
  Axis = (0,1,0)
  Base = (0,0,0)
  FaceMakerClass = Part::FaceMakerBullseye
  Placement = pos=(30.3,30.3,51.7) rot=(0,0,1;0rad)
  Solid = false
  Source = -> Face084
  Symmetric = false
FEATURE [Part::MultiFuse] Fusion054  label="createThreadedInsertHolesForFan001"
  Shapes = -> [Revolve085,Revolve086,Revolve087,Revolve088]
FEATURE [Part::Cut] Cut018  label="top007"
  Base = -> Fusion040
  Tool = -> Fusion054
FEATURE [Sketcher::SketchObject] Sketch029
  FullyConstrained = false
  Placement = pos=(0,0,0) rot=(1,0,0;1.5708rad)
  sketch-geometry (24):
    g0: ArcOfCircle CenterX=-4 CenterY=-10.5 CenterZ=0 NormalX=0 NormalY=0 NormalZ=1 AngleXU=0 Radius=1.5 StartAngle=6e-16 EndAngle=3.14159
    g1: ArcOfCircle CenterX=-34.2 CenterY=-10.5 CenterZ=0 NormalX=0 NormalY=0 NormalZ=1 AngleXU=0 Radius=1.5 StartAngle=0 EndAngle=3.14159
    g2: ArcOfCircle CenterX=-34.2 CenterY=-27.7 CenterZ=0 NormalX=0 NormalY=0 NormalZ=1 AngleXU=0 Radius=1.5 StartAngle=3.14159 EndAngle=6.28319
    g3: ArcOfCircle CenterX=-4 CenterY=-27.7 CenterZ=0 NormalX=0 NormalY=0 NormalZ=1 AngleXU=0 Radius=1.5 StartAngle=3.1416 EndAngle=6.28319
    g4: ArcOfCircle CenterX=-10 CenterY=-4.3 CenterZ=0 NormalX=0 NormalY=0 NormalZ=1 AngleXU=0 Radius=1.5 StartAngle=2e-16 EndAngle=3.14159
    g5: ArcOfCircle CenterX=-16.1 CenterY=-1.8 CenterZ=0 NormalX=0 NormalY=0 NormalZ=1 AngleXU=0 Radius=1.5 StartAngle=5e-16 EndAngle=3.14159
    g6: ArcOfCircle CenterX=-22.1 CenterY=-1.8 CenterZ=0 NormalX=0 NormalY=0 NormalZ=1 AngleXU=0 Radius=1.5 StartAngle=5e-16 EndAngle=3.14159
    g7: ArcOfCircle CenterX=-28.2 CenterY=-4.3 CenterZ=0 NormalX=0 NormalY=0 NormalZ=1 AngleXU=0 Radius=1.5 StartAngle=2e-16 EndAngle=3.14159
    g8: ArcOfCircle CenterX=-10 CenterY=-33.9 CenterZ=0 NormalX=0 NormalY=0 NormalZ=1 AngleXU=0 Radius=1.5 StartAngle=3.14159 EndAngle=6.28319
    g9: ArcOfCircle CenterX=-16.1 CenterY=-36.4 CenterZ=0 NormalX=0 NormalY=0 NormalZ=1 AngleXU=0 Radius=1.5 StartAngle=3.14159 EndAngle=6.28319
    g10: ArcOfCircle CenterX=-22.1 CenterY=-36.4 CenterZ=0 NormalX=0 NormalY=0 NormalZ=1 AngleXU=0 Radius=1.5 StartAngle=3.14159 EndAngle=6.28319
    g11: ArcOfCircle CenterX=-28.2 CenterY=-33.9 CenterZ=0 NormalX=0 NormalY=0 NormalZ=1 AngleXU=0 Radius=1.5 StartAngle=3.14159 EndAngle=6.28319
    g12: LineSegment StartX=-35.7 StartY=-10.5 StartZ=0 EndX=-35.7 EndY=-27.7 EndZ=0
    g13: LineSegment StartX=-32.7 StartY=-10.5 StartZ=0 EndX=-32.7 EndY=-27.7 EndZ=0
    g14: LineSegment StartX=-29.7 StartY=-33.9 StartZ=0 EndX=-29.7 EndY=-4.3 EndZ=0
    g15: LineSegment StartX=-26.7 StartY=-33.9 StartZ=0 EndX=-26.7 EndY=-4.3 EndZ=0
    g16: LineSegment StartX=-2.5 StartY=-10.5 StartZ=0 EndX=-2.5 EndY=-27.7 EndZ=0
    g17: LineSegment StartX=-8.5 StartY=-4.3 StartZ=0 EndX=-8.5 EndY=-33.9 EndZ=0
    g18: LineSegment StartX=-5.5 StartY=-10.5 StartZ=0 EndX=-5.5 EndY=-27.7 EndZ=0
    g19: LineSegment StartX=-11.5 StartY=-4.3 StartZ=0 EndX=-11.5 EndY=-33.9 EndZ=0
    g20: LineSegment StartX=-14.6 StartY=-1.8 StartZ=0 EndX=-14.6 EndY=-36.4 EndZ=0
    g21: LineSegment StartX=-17.6 StartY=-1.8 StartZ=0 EndX=-17.6 EndY=-36.4 EndZ=0
    g22: LineSegment StartX=-20.6 StartY=-36.4 StartZ=0 EndX=-20.6 EndY=-1.8 EndZ=0
    g23: LineSegment StartX=-23.6 StartY=-1.8 StartZ=0 EndX=-23.6 EndY=-36.4 EndZ=0
  constraints (48):
    c: Block(g0)
    c: Block(g1)
    c: Block(g2)
    c: Block(g3)
    c: Block(g4)
    c: Block(g5)
    c: Block(g6)
    c: Block(g7)
    c: Block(g8)
    c: Block(g9)
    c: Block(g10)
    c: Block(g11)
    c: Coincident(g12,g1)
    c: Coincident(g12,g2)
    c: Vertical(g12)
    c: Coincident(g13,g1)
    c: Coincident(g13,g2)
    c: Vertical(g13)
    c: Coincident(g14,g11)
    c: Coincident(g14,g7)
    c: Vertical(g14)
    c: Coincident(g15,g11)
    c: Coincident(g15,g7)
    c: Vertical(g15)
    c: Coincident(g16,g0)
    c: Coincident(g16,g3)
    c: Vertical(g16)
    c: Coincident(g17,g4)
    c: Coincident(g17,g8)
    c: Vertical(g17)
    c: Coincident(g18,g0)
    c: Coincident(g18,g3)
    c: Vertical(g18)
    c: Coincident(g19,g4)
    c: Coincident(g19,g8)
    c: Vertical(g19)
    c: Coincident(g20,g5)
    c: Coincident(g20,g9)
    c: Vertical(g20)
    c: Coincident(g21,g5)
    c: Coincident(g21,g9)
    c: Vertical(g21)
    c: Coincident(g22,g10)
    c: Coincident(g22,g6)
    c: Vertical(g22)
    c: Coincident(g23,g6)
    c: Coincident(g23,g10)
    c: Vertical(g23)
FEATURE [Part::Extrusion] Extrude020  label="removeToCreateFanGrillHoles"
  Base = -> Sketch029
  Dir = (0,-1,6e-16)
  DirMode = 2
  FaceMakerClass = Part::FaceMakerBullseye
  LengthFwd = 10
  LengthRev = 0
  Placement = pos=(65.4,44,54.82) rot=(0,0,1;0rad)
  Solid = true
  Symmetric = false
FEATURE [Part::MultiFuse] Fusion055  label="top008"
  Shapes = -> [Cut017,Cut018]
FEATURE [Part::Cut] Cut019  label="top009"
  Base = -> Fusion055
  Tool = -> Extrude020
FEATURE [App::MeasureDistance] Distance003  label="Distance: 71.95 mm"
  Distance = 71.9513
  P1 = (117,38,72)
  P2 = (117,38,0.0487319)
FEATURE [Sketcher::SketchObject] Sketch030
  FullyConstrained = true
  Placement = pos=(117,19,0) rot=(0.57735,0.57735,0.57735;2.0944rad)
  sketch-geometry (48):
    g0: LineSegment StartX=-49.19 StartY=69.25 StartZ=0 EndX=-49.19 EndY=66.25 EndZ=0
    g1: LineSegment StartX=-49.19 StartY=63.5 StartZ=0 EndX=-49.19 EndY=60.5 EndZ=0
    g2: LineSegment StartX=-49.19 StartY=57.75 StartZ=0 EndX=-49.19 EndY=54.75 EndZ=0
    g3: LineSegment StartX=-49.19 StartY=52 StartZ=0 EndX=-49.19 EndY=49 EndZ=0
    g4: LineSegment StartX=-49.19 StartY=46.25 StartZ=0 EndX=-49.19 EndY=43.25 EndZ=0
    g5: LineSegment StartX=-49.19 StartY=40.5 StartZ=0 EndX=-49.19 EndY=37.5 EndZ=0
    g6: LineSegment StartX=-49.19 StartY=34.5 StartZ=0 EndX=-49.19 EndY=31.5 EndZ=0
    g7: LineSegment StartX=-49.19 StartY=28.75 StartZ=0 EndX=-49.19 EndY=25.75 EndZ=0
    g8: LineSegment StartX=-49.19 StartY=23 StartZ=0 EndX=-49.19 EndY=20 EndZ=0
    g9: LineSegment StartX=-49.19 StartY=17.25 StartZ=0 EndX=-49.19 EndY=14.25 EndZ=0
    g10: LineSegment StartX=-49.19 StartY=11.5 StartZ=0 EndX=-49.19 EndY=8.5 EndZ=0
    g11: LineSegment StartX=-49.19 StartY=5.75 StartZ=0 EndX=-49.19 EndY=2.75 EndZ=0
    g12: ArcOfCircle CenterX=-1.5 CenterY=67.75 CenterZ=0 NormalX=0 NormalY=0 NormalZ=1 AngleXU=0 Radius=1.5 StartAngle=4.71239 EndAngle=7.85398
    g13: ArcOfCircle CenterX=-1.5 CenterY=62 CenterZ=0 NormalX=0 NormalY=0 NormalZ=1 AngleXU=0 Radius=1.5 StartAngle=4.71239 EndAngle=7.85398
    g14: ArcOfCircle CenterX=-1.5 CenterY=56.25 CenterZ=0 NormalX=0 NormalY=0 NormalZ=1 AngleXU=0 Radius=1.5 StartAngle=4.71239 EndAngle=7.85398
    g15: ArcOfCircle CenterX=-11.49 CenterY=50.5 CenterZ=0 NormalX=0 NormalY=0 NormalZ=1 AngleXU=0 Radius=1.5 StartAngle=4.71239 EndAngle=7.85398
    g16: ArcOfCircle CenterX=-16.28 CenterY=44.75 CenterZ=0 NormalX=0 NormalY=0 NormalZ=1 AngleXU=0 Radius=1.5 StartAngle=4.71239 EndAngle=7.85398
    g17: ArcOfCircle CenterX=-18.2337 CenterY=39 CenterZ=0 NormalX=0 NormalY=0 NormalZ=1 AngleXU=0 Radius=1.5 StartAngle=4.71485 EndAngle=7.85398
    g18: ArcOfCircle CenterX=-16.2837 CenterY=27.25 CenterZ=0 NormalX=0 NormalY=0 NormalZ=1 AngleXU=0 Radius=1.5 StartAngle=4.71485 EndAngle=7.85398
    g19: ArcOfCircle CenterX=-18.2337 CenterY=33 CenterZ=0 NormalX=0 NormalY=0 NormalZ=1 AngleXU=0 Radius=1.5 StartAngle=4.71485 EndAngle=7.85398
    g20: ArcOfCircle CenterX=-11.49 CenterY=21.5 CenterZ=0 NormalX=0 NormalY=0 NormalZ=1 AngleXU=0 Radius=1.5 StartAngle=4.71239 EndAngle=7.85398
    g21: ArcOfCircle CenterX=-1.5 CenterY=4.25 CenterZ=0 NormalX=0 NormalY=0 NormalZ=1 AngleXU=0 Radius=1.5 StartAngle=4.71239 EndAngle=7.85398
    g22: ArcOfCircle CenterX=-1.5 CenterY=10 CenterZ=0 NormalX=0 NormalY=0 NormalZ=1 AngleXU=0 Radius=1.5 StartAngle=4.71239 EndAngle=7.85398
    g23: ArcOfCircle CenterX=-1.5 CenterY=15.75 CenterZ=0 NormalX=0 NormalY=0 NormalZ=1 AngleXU=0 Radius=1.5 StartAngle=4.71239 EndAngle=7.85398
    g24: LineSegment StartX=-49.19 StartY=69.25 StartZ=0 EndX=-1.5 EndY=69.25 EndZ=0
    g25: LineSegment StartX=-49.19 StartY=66.25 StartZ=0 EndX=-1.5 EndY=66.25 EndZ=0
    g26: LineSegment StartX=-49.19 StartY=63.5 StartZ=0 EndX=-1.5 EndY=63.5 EndZ=0
    g27: LineSegment StartX=-49.19 StartY=60.5 StartZ=0 EndX=-1.5 EndY=60.5 EndZ=0
    g28: LineSegment StartX=-49.19 StartY=57.75 StartZ=0 EndX=-1.5 EndY=57.75 EndZ=0
    g29: LineSegment StartX=-49.19 StartY=54.75 StartZ=0 EndX=-1.5 EndY=54.75 EndZ=0
    g30: LineSegment StartX=-49.19 StartY=52 StartZ=0 EndX=-11.49 EndY=52 EndZ=0
    g31: LineSegment StartX=-49.19 StartY=49 StartZ=0 EndX=-11.49 EndY=49 EndZ=0
    g32: LineSegment StartX=-49.19 StartY=46.25 StartZ=0 EndX=-16.28 EndY=46.25 EndZ=0
    g33: LineSegment StartX=-49.19 StartY=43.25 StartZ=0 EndX=-16.28 EndY=43.25 EndZ=0
    g34: LineSegment StartX=-49.19 StartY=40.5 StartZ=0 EndX=-18.2337 EndY=40.5 EndZ=0
    g35: LineSegment StartX=-49.19 StartY=37.5 StartZ=0 EndX=-18.23 EndY=37.5 EndZ=0
    g36: LineSegment StartX=-49.19 StartY=34.5 StartZ=0 EndX=-18.2337 EndY=34.5 EndZ=0
    g37: LineSegment StartX=-49.19 StartY=31.5 StartZ=0 EndX=-18.23 EndY=31.5 EndZ=0
    g38: LineSegment StartX=-49.19 StartY=28.75 StartZ=0 EndX=-16.2837 EndY=28.75 EndZ=0
    g39: LineSegment StartX=-49.19 StartY=25.75 StartZ=0 EndX=-16.28 EndY=25.75 EndZ=0
    g40: LineSegment StartX=-49.19 StartY=23 StartZ=0 EndX=-11.49 EndY=23 EndZ=0
    g41: LineSegment StartX=-49.19 StartY=20 StartZ=0 EndX=-11.49 EndY=20 EndZ=0
    g42: LineSegment StartX=-49.19 StartY=17.25 StartZ=0 EndX=-1.5 EndY=17.25 EndZ=0
    g43: LineSegment StartX=-49.19 StartY=14.25 StartZ=0 EndX=-1.5 EndY=14.25 EndZ=0
    g44: LineSegment StartX=-49.19 StartY=11.5 StartZ=0 EndX=-1.5 EndY=11.5 EndZ=0
    g45: LineSegment StartX=-49.19 StartY=8.5 StartZ=0 EndX=-1.5 EndY=8.5 EndZ=0
    g46: LineSegment StartX=-49.19 StartY=5.75 StartZ=0 EndX=-1.5 EndY=5.75 EndZ=0
    g47: LineSegment StartX=-49.19 StartY=2.75 StartZ=0 EndX=-1.5 EndY=2.75 EndZ=0
  constraints (120):
    c: Vertical(g0)
    c: Distance(g0) = 3
    c: Block(g0)
    c: Vertical(g1)
    c: Distance(g1) = 3
    c: Vertical(g2)
    c: Equal(g0,g2) = 3
    c: Block(g2)
    c: Vertical(g3)
    c: Equal(g1,g3) = 3
    c: Vertical(g4)
    c: Equal(g0,g4) = 3
    c: Block(g4)
    c: Vertical(g5)
    c: Equal(g1,g5) = 3
    c: Vertical(g6)
    c: Equal(g0,g6) = 3
    c: Block(g6)
    c: Vertical(g7)
    c: Equal(g1,g7) = 3
    c: Vertical(g8)
    c: Equal(g0,g8) = 3
    c: Block(g8)
    c: Vertical(g9)
    c: Equal(g1,g9) = 3
    c: Vertical(g10)
    c: Equal(g0,g10) = 3
    c: Block(g10)
    c: Vertical(g11)
    c: Equal(g1,g11) = 3
    c: Block(g12)
    c: Block(g13)
    c: Block(g14)
    c: Block(g15)
    c: Block(g16)
    c: Block(g17)
    c: Block(g18)
    c: Block(g19)
    c: Block(g20)
    c: Block(g21)
    c: Block(g22)
    c: Block(g23)
    c: Block(g11)
    c: Block(g9)
    c: Block(g7)
    c: Block(g5)
    c: Block(g3)
    c: Block(g1)
    c: Coincident(g24,g0)
    c: Coincident(g24,g12)
    c: Horizontal(g24)
    c: Coincident(g25,g0)
    c: Coincident(g25,g12)
    c: Horizontal(g25)
    c: Coincident(g26,g1)
    c: Coincident(g26,g13)
    c: Horizontal(g26)
    c: Coincident(g27,g1)
    c: Coincident(g27,g13)
    c: Horizontal(g27)
    c: Coincident(g28,g2)
    c: Coincident(g28,g14)
    c: Horizontal(g28)
    c: Coincident(g29,g2)
    c: Coincident(g29,g14)
    c: Horizontal(g29)
    c: Coincident(g30,g3)
    c: Coincident(g30,g15)
    c: Horizontal(g30)
    c: Coincident(g31,g3)
    c: Coincident(g31,g15)
    c: Horizontal(g31)
    c: Coincident(g32,g4)
    c: Coincident(g32,g16)
    c: Horizontal(g32)
    c: Coincident(g33,g4)
    c: Coincident(g33,g16)
    c: Horizontal(g33)
    c: Coincident(g34,g5)
    c: Coincident(g34,g17)
    c: Horizontal(g34)
    c: Coincident(g35,g5)
    c: Coincident(g35,g17)
    c: Horizontal(g35)
    c: Coincident(g36,g6)
    c: Coincident(g36,g19)
    c: Horizontal(g36)
    c: Coincident(g37,g6)
    c: Coincident(g37,g19)
    c: Horizontal(g37)
    c: Coincident(g38,g7)
    c: Coincident(g38,g18)
    c: Horizontal(g38)
    c: Coincident(g39,g7)
    c: Coincident(g39,g18)
    c: Horizontal(g39)
    c: Coincident(g40,g8)
    c: Coincident(g40,g20)
    c: Horizontal(g40)
    c: Coincident(g41,g8)
    c: Coincident(g41,g20)
    c: Horizontal(g41)
    c: Coincident(g42,g9)
    c: Coincident(g42,g23)
    c: Horizontal(g42)
    c: Coincident(g43,g9)
    c: Coincident(g43,g23)
    c: Horizontal(g43)
    c: Coincident(g44,g10)
    c: Coincident(g44,g22)
    c: Horizontal(g44)
    c: Coincident(g45,g10)
    c: Coincident(g45,g22)
    c: Horizontal(g45)
    c: Coincident(g46,g11)
    c: Coincident(g46,g21)
    c: Horizontal(g46)
    c: Coincident(g47,g11)
    c: Coincident(g47,g21)
    c: Horizontal(g47)
FEATURE [Sketcher::SketchObject] Sketch031
  FullyConstrained = true
  Placement = pos=(117,19,0) rot=(0.57735,0.57735,0.57735;2.0944rad)
  sketch-geometry (24):
    g0: ArcOfCircle CenterX=-49.19 CenterY=67.75 CenterZ=0 NormalX=0 NormalY=0 NormalZ=1 AngleXU=0 Radius=1.5 StartAngle=1.5708 EndAngle=4.71239
    g1: ArcOfCircle CenterX=-49.19 CenterY=62 CenterZ=0 NormalX=0 NormalY=0 NormalZ=1 AngleXU=0 Radius=1.5 StartAngle=1.5708 EndAngle=4.71239
    g2: ArcOfCircle CenterX=-49.19 CenterY=56.25 CenterZ=0 NormalX=0 NormalY=0 NormalZ=1 AngleXU=0 Radius=1.5 StartAngle=1.5708 EndAngle=4.71239
    g3: ArcOfCircle CenterX=-49.19 CenterY=50.5 CenterZ=0 NormalX=0 NormalY=0 NormalZ=1 AngleXU=0 Radius=1.5 StartAngle=1.5708 EndAngle=4.71239
    g4: ArcOfCircle CenterX=-49.19 CenterY=44.75 CenterZ=0 NormalX=0 NormalY=0 NormalZ=1 AngleXU=0 Radius=1.5 StartAngle=1.5708 EndAngle=4.71239
    g5: ArcOfCircle CenterX=-49.19 CenterY=39 CenterZ=0 NormalX=0 NormalY=0 NormalZ=1 AngleXU=0 Radius=1.5 StartAngle=1.5708 EndAngle=4.71239
    g6: ArcOfCircle CenterX=-49.19 CenterY=33 CenterZ=0 NormalX=0 NormalY=0 NormalZ=1 AngleXU=0 Radius=1.5 StartAngle=1.5708 EndAngle=4.71239
    g7: ArcOfCircle CenterX=-49.19 CenterY=27.25 CenterZ=0 NormalX=0 NormalY=0 NormalZ=1 AngleXU=0 Radius=1.5 StartAngle=1.5708 EndAngle=4.71239
    g8: ArcOfCircle CenterX=-49.19 CenterY=21.5 CenterZ=0 NormalX=0 NormalY=0 NormalZ=1 AngleXU=0 Radius=1.5 StartAngle=1.5708 EndAngle=4.71239
    g9: ArcOfCircle CenterX=-49.19 CenterY=15.75 CenterZ=0 NormalX=0 NormalY=0 NormalZ=1 AngleXU=0 Radius=1.5 StartAngle=1.5708 EndAngle=4.71239
    g10: ArcOfCircle CenterX=-49.19 CenterY=10 CenterZ=0 NormalX=0 NormalY=0 NormalZ=1 AngleXU=0 Radius=1.5 StartAngle=1.5708 EndAngle=4.71239
    g11: ArcOfCircle CenterX=-49.19 CenterY=4.25 CenterZ=0 NormalX=0 NormalY=0 NormalZ=1 AngleXU=0 Radius=1.5 StartAngle=1.5708 EndAngle=4.71239
    g12: LineSegment StartX=-49.19 StartY=69.25 StartZ=0 EndX=-49.19 EndY=66.25 EndZ=0
    g13: LineSegment StartX=-49.19 StartY=63.5 StartZ=0 EndX=-49.19 EndY=60.5 EndZ=0
    g14: LineSegment StartX=-49.19 StartY=57.75 StartZ=0 EndX=-49.19 EndY=54.75 EndZ=0
    g15: LineSegment StartX=-49.19 StartY=52 StartZ=0 EndX=-49.19 EndY=49 EndZ=0
    g16: LineSegment StartX=-49.19 StartY=46.25 StartZ=0 EndX=-49.19 EndY=43.25 EndZ=0
    g17: LineSegment StartX=-49.19 StartY=40.5 StartZ=0 EndX=-49.19 EndY=37.5 EndZ=0
    g18: LineSegment StartX=-49.19 StartY=34.5 StartZ=0 EndX=-49.19 EndY=31.5 EndZ=0
    g19: LineSegment StartX=-49.19 StartY=28.75 StartZ=0 EndX=-49.19 EndY=25.75 EndZ=0
    g20: LineSegment StartX=-49.19 StartY=23 StartZ=0 EndX=-49.19 EndY=20 EndZ=0
    g21: LineSegment StartX=-49.19 StartY=17.25 StartZ=0 EndX=-49.19 EndY=14.25 EndZ=0
    g22: LineSegment StartX=-49.19 StartY=11.5 StartZ=0 EndX=-49.19 EndY=8.5 EndZ=0
    g23: LineSegment StartX=-49.19 StartY=5.75 StartZ=0 EndX=-49.19 EndY=2.75 EndZ=0
  constraints (48):
    c: Block(g0)
    c: Block(g1)
    c: Block(g2)
    c: Block(g3)
    c: Block(g4)
    c: Block(g5)
    c: Block(g6)
    c: Block(g7)
    c: Block(g8)
    c: Block(g9)
    c: Block(g10)
    c: Block(g11)
    c: Coincident(g12,g0)
    c: Coincident(g12,g0)
    c: Vertical(g12)
    c: Vertical(g13)
    c: Coincident(g13,g1)
    c: Vertical(g14)
    c: Coincident(g14,g2)
    c: Vertical(g15)
    c: Coincident(g15,g3)
    c: Vertical(g16)
    c: Coincident(g16,g4)
    c: Vertical(g17)
    c: Coincident(g17,g5)
    c: Vertical(g18)
    c: Coincident(g18,g6)
    c: Vertical(g19)
    c: Coincident(g19,g7)
    c: Vertical(g20)
    c: Coincident(g20,g8)
    c: Vertical(g21)
    c: Coincident(g21,g9)
    c: Vertical(g22)
    c: Coincident(g22,g10)
    c: Vertical(g23)
    c: Coincident(g23,g11)
    c: Block(g23)
    c: Block(g22)
    c: Block(g21)
    c: Block(g20)
    c: Block(g13)
    c: Block(g14)
    c: Block(g15)
    c: Block(g16)
    c: Block(g17)
    c: Block(g18)
    c: Block(g19)
FEATURE [Part::Extrusion] Extrude022
  Base = -> Sketch030
  Dir = (1,-2e-16,2e-16)
  DirMode = 2
  FaceMakerClass = Part::FaceMakerBullseye
  LengthFwd = 19
  LengthRev = 0
  Placement = pos=(-19,0,0) rot=(0,0,1;0rad)
  Solid = true
  Symmetric = false
FEATURE [Part::Fillet] Fillet022
  Base = -> Extrude022
  Edges = 24 edges r=1.49: [Edge6,Edge11,Edge18,Edge23,Edge30,Edge35,Edge42,Edge47,Edge54,Edge59,Edge66,Edge71,Edge78,Edge83,Edge90,Edge95,Edge102,Edge107,Edge114,Edge119,Edge126,Edge131,Edge138,Edge143]
FEATURE [Part::Cut] Cut020  label="top010"
  Base = -> Cut019
  Tool = -> Fillet022
FEATURE [Sketcher::SketchObject] Sketch032
  FullyConstrained = true
  Placement = pos=(117,19,0) rot=(0.57735,0.57735,0.57735;2.0944rad)
  sketch-geometry (48):
    g0: LineSegment StartX=-49.19 StartY=69.25 StartZ=0 EndX=-49.19 EndY=66.25 EndZ=0
    g1: LineSegment StartX=-49.19 StartY=63.5 StartZ=0 EndX=-49.19 EndY=60.5 EndZ=0
    g2: LineSegment StartX=-49.19 StartY=57.75 StartZ=0 EndX=-49.19 EndY=54.75 EndZ=0
    g3: LineSegment StartX=-49.19 StartY=52 StartZ=0 EndX=-49.19 EndY=49 EndZ=0
    g4: LineSegment StartX=-49.19 StartY=46.25 StartZ=0 EndX=-49.19 EndY=43.25 EndZ=0
    g5: LineSegment StartX=-49.19 StartY=40.5 StartZ=0 EndX=-49.19 EndY=37.5 EndZ=0
    g6: LineSegment StartX=-49.19 StartY=34.5 StartZ=0 EndX=-49.19 EndY=31.5 EndZ=0
    g7: LineSegment StartX=-49.19 StartY=28.75 StartZ=0 EndX=-49.19 EndY=25.75 EndZ=0
    g8: LineSegment StartX=-49.19 StartY=23 StartZ=0 EndX=-49.19 EndY=20 EndZ=0
    g9: LineSegment StartX=-49.19 StartY=17.25 StartZ=0 EndX=-49.19 EndY=14.25 EndZ=0
    g10: LineSegment StartX=-49.19 StartY=11.5 StartZ=0 EndX=-49.19 EndY=8.5 EndZ=0
    g11: LineSegment StartX=-49.19 StartY=5.75 StartZ=0 EndX=-49.19 EndY=2.75 EndZ=0
    g12: ArcOfCircle CenterX=-1.5 CenterY=67.75 CenterZ=0 NormalX=0 NormalY=0 NormalZ=1 AngleXU=0 Radius=1.5 StartAngle=4.71239 EndAngle=7.85398
    g13: ArcOfCircle CenterX=-1.5 CenterY=62 CenterZ=0 NormalX=0 NormalY=0 NormalZ=1 AngleXU=0 Radius=1.5 StartAngle=4.71239 EndAngle=7.85398
    g14: ArcOfCircle CenterX=-1.5 CenterY=56.25 CenterZ=0 NormalX=0 NormalY=0 NormalZ=1 AngleXU=0 Radius=1.5 StartAngle=4.71239 EndAngle=7.85398
    g15: ArcOfCircle CenterX=-11.49 CenterY=50.5 CenterZ=0 NormalX=0 NormalY=0 NormalZ=1 AngleXU=0 Radius=1.5 StartAngle=4.71239 EndAngle=7.85398
    g16: ArcOfCircle CenterX=-16.28 CenterY=44.75 CenterZ=0 NormalX=0 NormalY=0 NormalZ=1 AngleXU=0 Radius=1.5 StartAngle=4.71239 EndAngle=7.85398
    g17: ArcOfCircle CenterX=-18.2337 CenterY=39 CenterZ=0 NormalX=0 NormalY=0 NormalZ=1 AngleXU=0 Radius=1.5 StartAngle=4.71485 EndAngle=7.85398
    g18: ArcOfCircle CenterX=-16.2837 CenterY=27.25 CenterZ=0 NormalX=0 NormalY=0 NormalZ=1 AngleXU=0 Radius=1.5 StartAngle=4.71485 EndAngle=7.85398
    g19: ArcOfCircle CenterX=-18.2337 CenterY=33 CenterZ=0 NormalX=0 NormalY=0 NormalZ=1 AngleXU=0 Radius=1.5 StartAngle=4.71485 EndAngle=7.85398
    g20: ArcOfCircle CenterX=-11.49 CenterY=21.5 CenterZ=0 NormalX=0 NormalY=0 NormalZ=1 AngleXU=0 Radius=1.5 StartAngle=4.71239 EndAngle=7.85398
    g21: ArcOfCircle CenterX=-1.5 CenterY=4.25 CenterZ=0 NormalX=0 NormalY=0 NormalZ=1 AngleXU=0 Radius=1.5 StartAngle=4.71239 EndAngle=7.85398
    g22: ArcOfCircle CenterX=-1.5 CenterY=10 CenterZ=0 NormalX=0 NormalY=0 NormalZ=1 AngleXU=0 Radius=1.5 StartAngle=4.71239 EndAngle=7.85398
    g23: ArcOfCircle CenterX=-1.5 CenterY=15.75 CenterZ=0 NormalX=0 NormalY=0 NormalZ=1 AngleXU=0 Radius=1.5 StartAngle=4.71239 EndAngle=7.85398
    g24: LineSegment StartX=-49.19 StartY=69.25 StartZ=0 EndX=-1.5 EndY=69.25 EndZ=0
    g25: LineSegment StartX=-49.19 StartY=66.25 StartZ=0 EndX=-1.5 EndY=66.25 EndZ=0
    g26: LineSegment StartX=-49.19 StartY=63.5 StartZ=0 EndX=-1.5 EndY=63.5 EndZ=0
    g27: LineSegment StartX=-49.19 StartY=60.5 StartZ=0 EndX=-1.5 EndY=60.5 EndZ=0
    g28: LineSegment StartX=-49.19 StartY=57.75 StartZ=0 EndX=-1.5 EndY=57.75 EndZ=0
    g29: LineSegment StartX=-49.19 StartY=54.75 StartZ=0 EndX=-1.5 EndY=54.75 EndZ=0
    g30: LineSegment StartX=-49.19 StartY=52 StartZ=0 EndX=-11.49 EndY=52 EndZ=0
    g31: LineSegment StartX=-49.19 StartY=49 StartZ=0 EndX=-11.49 EndY=49 EndZ=0
    g32: LineSegment StartX=-49.19 StartY=46.25 StartZ=0 EndX=-16.28 EndY=46.25 EndZ=0
    g33: LineSegment StartX=-49.19 StartY=43.25 StartZ=0 EndX=-16.28 EndY=43.25 EndZ=0
    g34: LineSegment StartX=-49.19 StartY=40.5 StartZ=0 EndX=-18.2337 EndY=40.5 EndZ=0
    g35: LineSegment StartX=-49.19 StartY=37.5 StartZ=0 EndX=-18.23 EndY=37.5 EndZ=0
    g36: LineSegment StartX=-49.19 StartY=34.5 StartZ=0 EndX=-18.2337 EndY=34.5 EndZ=0
    g37: LineSegment StartX=-49.19 StartY=31.5 StartZ=0 EndX=-18.23 EndY=31.5 EndZ=0
    g38: LineSegment StartX=-49.19 StartY=28.75 StartZ=0 EndX=-16.2837 EndY=28.75 EndZ=0
    g39: LineSegment StartX=-49.19 StartY=25.75 StartZ=0 EndX=-16.28 EndY=25.75 EndZ=0
    g40: LineSegment StartX=-49.19 StartY=23 StartZ=0 EndX=-11.49 EndY=23 EndZ=0
    g41: LineSegment StartX=-49.19 StartY=20 StartZ=0 EndX=-11.49 EndY=20 EndZ=0
    g42: LineSegment StartX=-49.19 StartY=17.25 StartZ=0 EndX=-1.5 EndY=17.25 EndZ=0
    g43: LineSegment StartX=-49.19 StartY=14.25 StartZ=0 EndX=-1.5 EndY=14.25 EndZ=0
    g44: LineSegment StartX=-49.19 StartY=11.5 StartZ=0 EndX=-1.5 EndY=11.5 EndZ=0
    g45: LineSegment StartX=-49.19 StartY=8.5 StartZ=0 EndX=-1.5 EndY=8.5 EndZ=0
    g46: LineSegment StartX=-49.19 StartY=5.75 StartZ=0 EndX=-1.5 EndY=5.75 EndZ=0
    g47: LineSegment StartX=-49.19 StartY=2.75 StartZ=0 EndX=-1.5 EndY=2.75 EndZ=0
  constraints (120):
    c: Vertical(g0)
    c: Distance(g0) = 3
    c: Block(g0)
    c: Vertical(g1)
    c: Distance(g1) = 3
    c: Vertical(g2)
    c: Equal(g0,g2) = 3
    c: Block(g2)
    c: Vertical(g3)
    c: Equal(g1,g3) = 3
    c: Vertical(g4)
    c: Equal(g0,g4) = 3
    c: Block(g4)
    c: Vertical(g5)
    c: Equal(g1,g5) = 3
    c: Vertical(g6)
    c: Equal(g0,g6) = 3
    c: Block(g6)
    c: Vertical(g7)
    c: Equal(g1,g7) = 3
    c: Vertical(g8)
    c: Equal(g0,g8) = 3
    c: Block(g8)
    c: Vertical(g9)
    c: Equal(g1,g9) = 3
    c: Vertical(g10)
    c: Equal(g0,g10) = 3
    c: Block(g10)
    c: Vertical(g11)
    c: Equal(g1,g11) = 3
    c: Block(g12)
    c: Block(g13)
    c: Block(g14)
    c: Block(g15)
    c: Block(g16)
    c: Block(g17)
    c: Block(g18)
    c: Block(g19)
    c: Block(g20)
    c: Block(g21)
    c: Block(g22)
    c: Block(g23)
    c: Block(g11)
    c: Block(g9)
    c: Block(g7)
    c: Block(g5)
    c: Block(g3)
    c: Block(g1)
    c: Coincident(g24,g0)
    c: Coincident(g24,g12)
    c: Horizontal(g24)
    c: Coincident(g25,g0)
    c: Coincident(g25,g12)
    c: Horizontal(g25)
    c: Coincident(g26,g1)
    c: Coincident(g26,g13)
    c: Horizontal(g26)
    c: Coincident(g27,g1)
    c: Coincident(g27,g13)
    c: Horizontal(g27)
    c: Coincident(g28,g2)
    c: Coincident(g28,g14)
    c: Horizontal(g28)
    c: Coincident(g29,g2)
    c: Coincident(g29,g14)
    c: Horizontal(g29)
    c: Coincident(g30,g3)
    c: Coincident(g30,g15)
    c: Horizontal(g30)
    c: Coincident(g31,g3)
    c: Coincident(g31,g15)
    c: Horizontal(g31)
    c: Coincident(g32,g4)
    c: Coincident(g32,g16)
    c: Horizontal(g32)
    c: Coincident(g33,g4)
    c: Coincident(g33,g16)
    c: Horizontal(g33)
    c: Coincident(g34,g5)
    c: Coincident(g34,g17)
    c: Horizontal(g34)
    c: Coincident(g35,g5)
    c: Coincident(g35,g17)
    c: Horizontal(g35)
    c: Coincident(g36,g6)
    c: Coincident(g36,g19)
    c: Horizontal(g36)
    c: Coincident(g37,g6)
    c: Coincident(g37,g19)
    c: Horizontal(g37)
    c: Coincident(g38,g7)
    c: Coincident(g38,g18)
    c: Horizontal(g38)
    c: Coincident(g39,g7)
    c: Coincident(g39,g18)
    c: Horizontal(g39)
    c: Coincident(g40,g8)
    c: Coincident(g40,g20)
    c: Horizontal(g40)
    c: Coincident(g41,g8)
    c: Coincident(g41,g20)
    c: Horizontal(g41)
    c: Coincident(g42,g9)
    c: Coincident(g42,g23)
    c: Horizontal(g42)
    c: Coincident(g43,g9)
    c: Coincident(g43,g23)
    c: Horizontal(g43)
    c: Coincident(g44,g10)
    c: Coincident(g44,g22)
    c: Horizontal(g44)
    c: Coincident(g45,g10)
    c: Coincident(g45,g22)
    c: Horizontal(g45)
    c: Coincident(g46,g11)
    c: Coincident(g46,g21)
    c: Horizontal(g46)
    c: Coincident(g47,g11)
    c: Coincident(g47,g21)
    c: Horizontal(g47)
FEATURE [Part::Extrusion] Extrude023
  Base = -> Sketch032
  Dir = (1,-2e-16,2e-16)
  DirMode = 2
  FaceMakerClass = Part::FaceMakerBullseye
  LengthFwd = 19
  LengthRev = 0
  Placement = pos=(-19,0,0) rot=(0,0,1;0rad)
  Solid = true
  Symmetric = false
FEATURE [Part::Fillet] Fillet023
  Base = -> Extrude023
  Edges = <same value as first occurrence — deduplicated (x6 in doc)>
  Placement = pos=(0,0.05,0) rot=(0,0,1;0rad)
FEATURE [Part::Cut] Cut014  label="bottom003"
  Base = -> Cut007
  Tool = -> Fusion047
FEATURE [Part::Cut] Cut021  label="bottom004"
  Base = -> Cut014
  Tool = -> Fillet023
FEATURE [Sketcher::SketchObject] Sketch033
  FullyConstrained = true
  Placement = pos=(117,19,0) rot=(0.57735,0.57735,0.57735;2.0944rad)
  sketch-geometry (8):
    g0: LineSegment StartX=-49.19 StartY=69.25 StartZ=0 EndX=-49.19 EndY=66.25 EndZ=0
    g1: LineSegment StartX=-49.19 StartY=5.75 StartZ=0 EndX=-49.19 EndY=2.75 EndZ=0
    g2: ArcOfCircle CenterX=-1.5 CenterY=67.75 CenterZ=0 NormalX=0 NormalY=0 NormalZ=1 AngleXU=0 Radius=1.5 StartAngle=4.71239 EndAngle=7.85398
    g3: ArcOfCircle CenterX=-1.5 CenterY=4.25 CenterZ=0 NormalX=0 NormalY=0 NormalZ=1 AngleXU=0 Radius=1.5 StartAngle=4.71239 EndAngle=7.85398
    g4: LineSegment StartX=-49.19 StartY=69.25 StartZ=0 EndX=-1.5 EndY=69.25 EndZ=0
    g5: LineSegment StartX=-49.19 StartY=66.25 StartZ=0 EndX=-1.5 EndY=66.25 EndZ=0
    g6: LineSegment StartX=-49.19 StartY=5.75 StartZ=0 EndX=-1.5 EndY=5.75 EndZ=0
    g7: LineSegment StartX=-49.19 StartY=2.75 StartZ=0 EndX=-1.5 EndY=2.75 EndZ=0
  constraints (19):
    c: Vertical(g0)
    c: Distance(g0) = 3
    c: Block(g0)
    c: Vertical(g1)
    c: Block(g2)
    c: Block(g3)
    c: Block(g1)
    c: Coincident(g4,g0)
    c: Coincident(g4,g2)
    c: Horizontal(g4)
    c: Coincident(g5,g0)
    c: Coincident(g5,g2)
    c: Horizontal(g5)
    c: Coincident(g6,g1)
    c: Coincident(g6,g3)
    c: Horizontal(g6)
    c: Coincident(g7,g1)
    c: Coincident(g7,g3)
    c: Horizontal(g7)
FEATURE [Sketcher::SketchObject] Sketch034
  FullyConstrained = true
  Placement = pos=(117,19,0) rot=(0.57735,0.57735,0.57735;2.0944rad)
  sketch-geometry (8):
    g0: LineSegment StartX=-49.19 StartY=63.5 StartZ=0 EndX=-49.19 EndY=60.5 EndZ=0
    g1: LineSegment StartX=-49.19 StartY=11.5 StartZ=0 EndX=-49.19 EndY=8.5 EndZ=0
    g2: ArcOfCircle CenterX=-1.5 CenterY=62 CenterZ=0 NormalX=0 NormalY=0 NormalZ=1 AngleXU=0 Radius=1.5 StartAngle=4.71239 EndAngle=7.85398
    g3: ArcOfCircle CenterX=-1.5 CenterY=10 CenterZ=0 NormalX=0 NormalY=0 NormalZ=1 AngleXU=0 Radius=1.5 StartAngle=4.71239 EndAngle=7.85398
    g4: LineSegment StartX=-49.19 StartY=63.5 StartZ=0 EndX=-1.5 EndY=63.5 EndZ=0
    g5: LineSegment StartX=-49.19 StartY=60.5 StartZ=0 EndX=-1.5 EndY=60.5 EndZ=0
    g6: LineSegment StartX=-49.19 StartY=11.5 StartZ=0 EndX=-1.5 EndY=11.5 EndZ=0
    g7: LineSegment StartX=-49.19 StartY=8.5 StartZ=0 EndX=-1.5 EndY=8.5 EndZ=0
  constraints (19):
    c: Vertical(g0)
    c: Distance(g0) = 3
    c: Vertical(g1)
    c: Block(g1)
    c: Block(g2)
    c: Block(g3)
    c: Block(g0)
    c: Coincident(g4,g0)
    c: Coincident(g4,g2)
    c: Horizontal(g4)
    c: Coincident(g5,g0)
    c: Coincident(g5,g2)
    c: Horizontal(g5)
    c: Coincident(g6,g1)
    c: Coincident(g6,g3)
    c: Horizontal(g6)
    c: Coincident(g7,g1)
    c: Coincident(g7,g3)
    c: Horizontal(g7)
FEATURE [Part::Extrusion] Extrude024
  Base = -> Sketch033
  Dir = (1,0,0)
  DirMode = 2
  FaceMakerClass = Part::FaceMakerBullseye
  LengthFwd = 10
  LengthRev = 0
  Solid = true
  Symmetric = false
FEATURE [Part::Extrusion] Extrude025
  Base = -> Sketch034
  Dir = (1,0,0)
  DirMode = 2
  FaceMakerClass = Part::FaceMakerBullseye
  LengthFwd = 10
  LengthRev = 0
  Solid = true
  Symmetric = false
FEATURE [Part::Fillet] Fillet024  label="removeFromtMoreFrontCaseScrewRetainers"
  Base = -> Extrude024
  Edges = 4 edges r=1.49: [Edge6,Edge11,Edge18,Edge23]
  Placement = pos=(-11,0,0) rot=(0,0,1;0rad)
FEATURE [Part::Fillet] Fillet025  label="removeFromtMoreFrontCaseScrewRetainers001"
  Base = -> Extrude025
  Edges = 4 edges r=1.49: [Edge6,Edge11,Edge18,Edge23]
  Placement = pos=(-19,0,0) rot=(0,0,1;0rad)
FEATURE [Part::Cut] Cut022
  Base = -> Cut015
  Tool = -> Fillet025
FEATURE [Part::Cut] Cut023  label="screwRetainers"
  Base = -> Cut022
  Tool = -> Fillet024
FEATURE [Part::MultiFuse] Fusion056  label="bottom005"
  Shapes = -> [Fusion044,Cut021]
FEATURE [Part::MultiFuse] Fusion057  label="casePillars001"
  Shapes = -> [Cut016,Fusion052]
FEATURE [Part::MultiFuse] Fusion058  label="bottom006"
  Shapes = -> [Fusion056,Cut023]
FEATURE [Part::MultiFuse] Fusion059  label="bottom007"
  Shapes = -> [Fusion058,Fillet005]
FEATURE [Part::MultiFuse] Fusion060  label="bottom008"
  Shapes = -> [Fusion059,Fusion]
FEATURE [Part::MultiFuse] Fusion061  label="top011"
  Shapes = -> [Cut006,Cut020]
FEATURE [Part::MultiFuse] Fusion062  label="top012"
  Shapes = -> [Fusion057,Fusion061]
FEATURE [Sketcher::SketchObject] Sketch035  label="topSketch007"
  FullyConstrained = true
  sketch-geometry (6):
    g0: LineSegment StartX=19 StartY=38 StartZ=0 EndX=117 EndY=38 EndZ=0
    g1: ArcOfCircle CenterX=19 CenterY=19 CenterZ=0 NormalX=0 NormalY=0 NormalZ=1 AngleXU=0 Radius=19 StartAngle=1.5708 EndAngle=3.14159
    g2: LineSegment StartX=117 StartY=38 StartZ=0 EndX=117 EndY=19 EndZ=0
    g3: LineSegment StartX=98 StartY=1.0161e-12 StartZ=0 EndX=5.22862e-06 EndY=1.0161e-12 EndZ=0
    g4: LineSegment StartX=5.22862e-06 StartY=19 StartZ=0 EndX=5.22862e-06 EndY=1.0161e-12 EndZ=0
    g5: ArcOfCircle CenterX=98 CenterY=19 CenterZ=0 NormalX=0 NormalY=0 NormalZ=1 AngleXU=0 Radius=19 StartAngle=4.71239 EndAngle=6.28319
  constraints (16):
    c: Horizontal(g0)
    c: Distance(g0) = 98
    c: Coincident(g1,g0)
    c: Block(g1)
    c: Coincident(g2,g0)
    c: Vertical(g2)
    c: Distance(g2) = 19
    c: Horizontal(g3)
    c: Coincident(g4,g1)
    c: Vertical(g4)
    c: Coincident(g3,g4)
    c: Block(g3)
    c: Coincident(g5,g2)
    c: Coincident(g5,g3)
    c: Block(g0)
    c: Block(g5)
FEATURE [Part::Extrusion] Extrude026  label="sideA001"
  Base = -> Sketch035
  Dir = (0,0,1)
  DirMode = 2
  FaceMakerClass = Part::FaceMakerBullseye
  LengthFwd = 3
  LengthRev = 0
  Placement = pos=(0,0,-2.7) rot=(0,0,1;0rad)
  Solid = true
  Symmetric = false
FEATURE [Sketcher::SketchObject] Sketch036  label="topSketch008"
  FullyConstrained = true
  sketch-geometry (6):
    g0: LineSegment StartX=19 StartY=38 StartZ=0 EndX=117 EndY=38 EndZ=0
    g1: ArcOfCircle CenterX=19 CenterY=19 CenterZ=0 NormalX=0 NormalY=0 NormalZ=1 AngleXU=0 Radius=19 StartAngle=1.5708 EndAngle=3.14159
    g2: LineSegment StartX=117 StartY=38 StartZ=0 EndX=117 EndY=19 EndZ=0
    g3: LineSegment StartX=98 StartY=1.0161e-12 StartZ=0 EndX=5.22862e-06 EndY=1.0161e-12 EndZ=0
    g4: LineSegment StartX=5.22862e-06 StartY=19 StartZ=0 EndX=5.22862e-06 EndY=1.0161e-12 EndZ=0
    g5: ArcOfCircle CenterX=98 CenterY=19 CenterZ=0 NormalX=0 NormalY=0 NormalZ=1 AngleXU=0 Radius=19 StartAngle=4.71239 EndAngle=6.28319
  constraints (16):
    c: Horizontal(g0)
    c: Distance(g0) = 98
    c: Coincident(g1,g0)
    c: Block(g1)
    c: Coincident(g2,g0)
    c: Vertical(g2)
    c: Distance(g2) = 19
    c: Horizontal(g3)
    c: Coincident(g4,g1)
    c: Vertical(g4)
    c: Coincident(g3,g4)
    c: Block(g3)
    c: Coincident(g5,g2)
    c: Coincident(g5,g3)
    c: Block(g0)
    c: Block(g5)
FEATURE [Part::Extrusion] Extrude027  label="sideB001"
  Base = -> Sketch036
  Dir = (0,0,1)
  DirMode = 2
  FaceMakerClass = Part::FaceMakerBullseye
  LengthFwd = 3
  LengthRev = 0
  Placement = pos=(0,0,71.7) rot=(0,0,1;0rad)
  Solid = true
  Symmetric = false
FEATURE [Part::MultiFuse] Fusion064  label="removeFromBottom"
  Shapes = -> [Extrude026,Extrude027]
FEATURE [Part::Cut] Cut024  label="bottom009"
  Base = -> Fusion060
  Tool = -> Fusion064
FEATURE [Sketcher::SketchObject] Sketch037  label="topSketch009"
  FullyConstrained = true
  sketch-geometry (8):
    g0: ArcOfCircle CenterX=19 CenterY=19.1201 CenterZ=0 NormalX=0 NormalY=0 NormalZ=1 AngleXU=0 Radius=18.8799 StartAngle=1.5708 EndAngle=3.14793
    g1: LineSegment StartX=0.120501 StartY=19.0004 StartZ=0 EndX=0.120501 EndY=0.000382114 EndZ=0
    g2: LineSegment StartX=19 StartY=38 StartZ=0 EndX=124 EndY=38 EndZ=0
    g3: LineSegment StartX=0.120501 StartY=0.000382114 StartZ=0 EndX=105.121 EndY=0.000382114 EndZ=0
    g4: LineSegment StartX=124 StartY=38 StartZ=0 EndX=125.616 EndY=38 EndZ=0
    g5: LineSegment StartX=105.121 StartY=0.000382114 StartZ=0 EndX=106.736 EndY=0.000382114 EndZ=0
    g6: ArcOfCircle CenterX=106.616 CenterY=19 CenterZ=0 NormalX=0 NormalY=0 NormalZ=1 AngleXU=0 Radius=19 StartAngle=4.71873 EndAngle=6.28319
    g7: LineSegment StartX=125.616 StartY=38 StartZ=0 EndX=125.616 EndY=19 EndZ=0
  constraints (21):
    c: Block(g0)
    c: Coincident(g1,g0)
    c: Vertical(g1)
    c: Horizontal(g2)
    c: Distance(g2) = 105
    c: Coincident(g2,g0)
    c: Distance(g1) = 19
    c: Coincident(g3,g1)
    c: Horizontal(g3)
    c: Distance(g3) = 105
    c: Coincident(g4,g2)
    c: Horizontal(g4)
    c: Distance(g4) = 1.61553
    c: Horizontal(g5)
    c: Equal(g4,g5) = 1.61553
    c: Coincident(g5,g3)
    c: Block(g6)
    c: Coincident(g6,g5)
    c: Coincident(g7,g4)
    c: Coincident(g7,g6)
    c: Vertical(g7)
FEATURE [Part::Extrusion] Extrude028  label="sideB"
  Base = -> Sketch037
  Dir = (0,0,1)
  DirMode = 2
  FaceMakerClass = Part::FaceMakerBullseye
  LengthFwd = 3
  LengthRev = 0
  Placement = pos=(0,0,72) rot=(0,0,1;0rad)
  Solid = true
  Symmetric = false
FEATURE [Sketcher::SketchObject] Sketch038  label="topSketch010"
  FullyConstrained = true
  sketch-geometry (22):
    g0: LineSegment StartX=5.21097e-06 StartY=3 StartZ=0 EndX=5.21097e-06 EndY=19 EndZ=0
    g1: ArcOfCircle CenterX=19 CenterY=19 CenterZ=0 NormalX=0 NormalY=0 NormalZ=1 AngleXU=0 Radius=19 StartAngle=1.5708 EndAngle=3.14159
    g2: ArcOfCircle CenterX=19 CenterY=19 CenterZ=0 NormalX=0 NormalY=0 NormalZ=1 AngleXU=0 Radius=16 StartAngle=1.5708 EndAngle=3.14159
    g3: LineSegment StartX=114 StartY=35 StartZ=0 EndX=19 EndY=35 EndZ=0
    g4: LineSegment StartX=5.21097e-06 StartY=3 StartZ=0 EndX=5.21097e-06 EndY=0 EndZ=0
    g5: LineSegment StartX=3 StartY=0 StartZ=0 EndX=5.21097e-06 EndY=0 EndZ=0
    g6: LineSegment StartX=3 StartY=19 StartZ=0 EndX=3 EndY=0 EndZ=0
    g7: LineSegment StartX=19 StartY=38 StartZ=0 EndX=124 EndY=38 EndZ=0
    g8: Circle CenterX=119 CenterY=35 CenterZ=0 NormalX=0 NormalY=0 NormalZ=1 AngleXU=0 Radius=1
    g9: Circle CenterX=121 CenterY=35 CenterZ=0 NormalX=0 NormalY=0 NormalZ=1 AngleXU=0 Radius=1
    g10: Circle CenterX=121 CenterY=33 CenterZ=0 NormalX=0 NormalY=0 NormalZ=1 AngleXU=0 Radius=1
    g11: BSplineCurve PolesCount=3 KnotsCount=2 Degree=2 IsPeriodic=0
    g12: GeomPoint X=119 Y=35 Z=0
    g13: GeomPoint X=121 Y=33 Z=0
    g14: LineSegment StartX=119 StartY=35 StartZ=0 EndX=114 EndY=35 EndZ=0
    g15: ArcOfCircle CenterX=105 CenterY=19 CenterZ=0 NormalX=0 NormalY=0 NormalZ=1 AngleXU=0 Radius=16 StartAngle=5.60905 EndAngle=6.28319
    g16: LineSegment StartX=121 StartY=33 StartZ=0 EndX=121 EndY=19 EndZ=0
    g17: LineSegment StartX=117.5 StartY=9.01251 StartZ=0 EndX=121.163 EndY=9.0125 EndZ=0
    g18: ArcOfCircle CenterX=105 CenterY=19 CenterZ=0 NormalX=0 NormalY=0 NormalZ=1 AngleXU=0 Radius=20.6155 StartAngle=5.7297 EndAngle=6.28319
    g19: LineSegment StartX=121.163 StartY=9.0125 StartZ=0 EndX=122.538 EndY=8.16329 EndZ=0
    g20: LineSegment StartX=124 StartY=38 StartZ=0 EndX=125.616 EndY=38 EndZ=0
    g21: LineSegment StartX=125.616 StartY=19 StartZ=0 EndX=125.616 EndY=38 EndZ=0
  constraints (49):
    c: Vertical(g0)
    c: Block(g0)
    c: Coincident(g1,g0)
    c: Block(g1)
    c: Coincident(g2,g1)
    c: Block(g2)
    c: Coincident(g3,g2)
    c: Horizontal(g3)
    c: Tangent(g3,g2)
    c: Coincident(g4,g0)
    c: Distance(g4) = 3
    c: Vertical(g4)
    c: Coincident(g5,g4)
    c: Horizontal(g5)
    c: Coincident(g6,g2)
    c: Coincident(g6,g5)
    c: Vertical(g6)
    c: Horizontal(g7)
    c: Distance(g7) = 105
    c: Coincident(g7,g1)
    c: Block(g3)
    c: Weight(g8) = 1
    c: Equal(g8,g9)
    c: Equal(g8,g10)
    c: InternalAlignment(g8,g11)
    c: InternalAlignment(g9,g11)
    c: InternalAlignment(g10,g11)
    c: InternalAlignment(g12,g11)
    c: InternalAlignment(g13,g11)
    c: Block(g11)
    c: Coincident(g14,g11)
    c: Coincident(g14,g3)
    c: Horizontal(g14)
    c: Block(g15)
    c: Coincident(g16,g11)
    c: Coincident(g16,g15)
    c: Vertical(g16)
    c: Distance(g16) = 14
    c: Coincident(g17,g15)
    c: Block(g18)
    c: Coincident(g19,g18)
    c: Coincident(g20,g7)
    c: Horizontal(g20)
    c: Vertical(g21)
    c: Coincident(g20,g21)
    c: Block(g20)
    c: Block(g21)
    c: Block(g19)
    c: Block(g17)
FEATURE [Part::Extrusion] Extrude029
  Base = -> Sketch038
  Dir = (0,0,1)
  DirMode = 2
  FaceMakerClass = Part::FaceMakerBullseye
  LengthFwd = 72
  LengthRev = 0
  Solid = true
  Symmetric = false
FEATURE [Part::Feature] Face085
  shape: bbox 4.8 x 25.5 x 2e-07 mm, 1 faces, 0 solids (baked)
FEATURE [Part::Revolution] Revolve089  label="moreFrontCaseScrewPost003"
  Angle = 360
  Axis = (0,1,0)
  Base = (0,0,0)
  FaceMakerClass = Part::FaceMakerBullseye
  Placement = pos=(109.5,4.5,3.5) rot=(0,0,1;0rad)
  Solid = false
  Source = -> Face085
  Symmetric = false
FEATURE [Part::Feature] Face086
  shape: bbox 4.8 x 25.5 x 2e-07 mm, 1 faces, 0 solids (baked)
FEATURE [Part::Revolution] Revolve090  label="moreFrontCaseScrewPost004"
  Angle = 360
  Axis = (0,1,0)
  Base = (0,0,0)
  FaceMakerClass = Part::FaceMakerBullseye
  Placement = pos=(109.5,4.5,68.5) rot=(0,0,1;0rad)
  Solid = false
  Source = -> Face086
  Symmetric = false
FEATURE [Part::Fillet] Fillet026  label="top013"
  Base = -> Extrude029
  Edges = 1 edges r=2: [Edge35]
FEATURE [Sketcher::SketchObject] Sketch039
  FullyConstrained = true
  sketch-geometry (7):
    g0: LineSegment StartX=0 StartY=0 StartZ=0 EndX=0 EndY=6 EndZ=0
    g1: Circle CenterX=0 CenterY=0 CenterZ=0 NormalX=0 NormalY=0 NormalZ=1 AngleXU=0 Radius=1
    g2: Circle CenterX=8 CenterY=6 CenterZ=0 NormalX=0 NormalY=0 NormalZ=1 AngleXU=0 Radius=1
    g3: BSplineCurve PolesCount=3 KnotsCount=2 Degree=2 IsPeriodic=0
    g4: GeomPoint X=0 Y=0 Z=0
    g5: GeomPoint X=8 Y=6 Z=0
    g6: LineSegment StartX=0 StartY=6 StartZ=0 EndX=8 EndY=6 EndZ=0
  constraints (14):
    c: Coincident(g0,g-1)
    c: Distance(g0) = 6
    c: Vertical(g0)
    c: Coincident(g3,g0)
    c: Weight(g1) = 1
    c: Equal(g1,g2)
    c: InternalAlignment(g1,g3)
    c: InternalAlignment(g2,g3)
    c: InternalAlignment(g4,g3)
    c: InternalAlignment(g5,g3)
    c: Block(g3)
    c: Coincident(g6,g0)
    c: Coincident(g6,g3)
    c: Horizontal(g6)
FEATURE [Sketcher::SketchObject] Sketch040
  FullyConstrained = true
  sketch-geometry (7):
    g0: LineSegment StartX=0 StartY=0 StartZ=0 EndX=0 EndY=6 EndZ=0
    g1: Circle CenterX=0 CenterY=0 CenterZ=0 NormalX=0 NormalY=0 NormalZ=1 AngleXU=0 Radius=1
    g2: Circle CenterX=8 CenterY=6 CenterZ=0 NormalX=0 NormalY=0 NormalZ=1 AngleXU=0 Radius=1
    g3: BSplineCurve PolesCount=3 KnotsCount=2 Degree=2 IsPeriodic=0
    g4: GeomPoint X=0 Y=0 Z=0
    g5: GeomPoint X=8 Y=6 Z=0
    g6: LineSegment StartX=0 StartY=6 StartZ=0 EndX=8 EndY=6 EndZ=0
  constraints (14):
    c: Coincident(g0,g-1)
    c: Distance(g0) = 6
    c: Vertical(g0)
    c: Coincident(g3,g0)
    c: Weight(g1) = 1
    c: Equal(g1,g2)
    c: InternalAlignment(g1,g3)
    c: InternalAlignment(g2,g3)
    c: InternalAlignment(g4,g3)
    c: InternalAlignment(g5,g3)
    c: Block(g3)
    c: Coincident(g6,g0)
    c: Coincident(g6,g3)
    c: Horizontal(g6)
FEATURE [Sketcher::SketchObject] Sketch041
  FullyConstrained = true
  sketch-geometry (7):
    g0: LineSegment StartX=0 StartY=0 StartZ=0 EndX=0 EndY=6 EndZ=0
    g1: Circle CenterX=0 CenterY=0 CenterZ=0 NormalX=0 NormalY=0 NormalZ=1 AngleXU=0 Radius=1
    g2: Circle CenterX=8 CenterY=6 CenterZ=0 NormalX=0 NormalY=0 NormalZ=1 AngleXU=0 Radius=1
    g3: BSplineCurve PolesCount=3 KnotsCount=2 Degree=2 IsPeriodic=0
    g4: GeomPoint X=0 Y=0 Z=0
    g5: GeomPoint X=8 Y=6 Z=0
    g6: LineSegment StartX=0 StartY=6 StartZ=0 EndX=8 EndY=6 EndZ=0
  constraints (14):
    c: Coincident(g0,g-1)
    c: Distance(g0) = 6
    c: Vertical(g0)
    c: Coincident(g3,g0)
    c: Weight(g1) = 1
    c: Equal(g1,g2)
    c: InternalAlignment(g1,g3)
    c: InternalAlignment(g2,g3)
    c: InternalAlignment(g4,g3)
    c: InternalAlignment(g5,g3)
    c: Block(g3)
    c: Coincident(g6,g0)
    c: Coincident(g6,g3)
    c: Horizontal(g6)
FEATURE [Sketcher::SketchObject] Sketch042
  FullyConstrained = true
  sketch-geometry (7):
    g0: LineSegment StartX=0 StartY=0 StartZ=0 EndX=0 EndY=6 EndZ=0
    g1: Circle CenterX=0 CenterY=0 CenterZ=0 NormalX=0 NormalY=0 NormalZ=1 AngleXU=0 Radius=1
    g2: Circle CenterX=8 CenterY=6 CenterZ=0 NormalX=0 NormalY=0 NormalZ=1 AngleXU=0 Radius=1
    g3: BSplineCurve PolesCount=3 KnotsCount=2 Degree=2 IsPeriodic=0
    g4: GeomPoint X=0 Y=0 Z=0
    g5: GeomPoint X=8 Y=6 Z=0
    g6: LineSegment StartX=0 StartY=6 StartZ=0 EndX=8 EndY=6 EndZ=0
  constraints (14):
    c: Coincident(g0,g-1)
    c: Distance(g0) = 6
    c: Vertical(g0)
    c: Coincident(g3,g0)
    c: Weight(g1) = 1
    c: Equal(g1,g2)
    c: InternalAlignment(g1,g3)
    c: InternalAlignment(g2,g3)
    c: InternalAlignment(g4,g3)
    c: InternalAlignment(g5,g3)
    c: Block(g3)
    c: Coincident(g6,g0)
    c: Coincident(g6,g3)
    c: Horizontal(g6)
FEATURE [Part::Extrusion] Extrude030  label="caseScrewPillarBracket008"
  Base = -> Sketch039
  Dir = (0,0,1)
  DirMode = 2
  FaceMakerClass = Part::FaceMakerBullseye
  LengthFwd = 2.4
  LengthRev = 0
  Placement = pos=(15.76,29,8.8) rot=(0,1,0;0rad)
  Solid = true
  Symmetric = false
FEATURE [Part::Extrusion] Extrude031  label="caseScrewPillarBracket009"
  Base = -> Sketch040
  Dir = (0,0,1)
  DirMode = 2
  FaceMakerClass = Part::FaceMakerBullseye
  LengthFwd = 2.4
  LengthRev = 0
  Placement = pos=(15.76,29,60.8) rot=(0,0,1;0rad)
  Solid = true
  Symmetric = false
FEATURE [Part::Extrusion] Extrude032  label="caseScrewPillarBracket010"
  Base = -> Sketch041
  Dir = (0,0,1)
  DirMode = 2
  FaceMakerClass = Part::FaceMakerBullseye
  LengthFwd = 2.4
  LengthRev = 0
  Placement = pos=(13.7,29,13.26) rot=(0,-1,0;1.5708rad)
  Solid = true
  Symmetric = false
FEATURE [Part::Extrusion] Extrude033  label="caseScrewPillarBracket011"
  Base = -> Sketch042
  Dir = (0,0,1)
  DirMode = 2
  FaceMakerClass = Part::FaceMakerBullseye
  LengthFwd = 2.4
  LengthRev = 0
  Placement = pos=(11.3,29,58.74) rot=(0,1,0;1.5708rad)
  Solid = true
  Symmetric = false
FEATURE [Sketcher::SketchObject] Sketch043
  FullyConstrained = true
  sketch-geometry (7):
    g0: LineSegment StartX=0 StartY=0 StartZ=0 EndX=0 EndY=6 EndZ=0
    g1: Circle CenterX=0 CenterY=0 CenterZ=0 NormalX=0 NormalY=0 NormalZ=1 AngleXU=0 Radius=1
    g2: Circle CenterX=8 CenterY=6 CenterZ=0 NormalX=0 NormalY=0 NormalZ=1 AngleXU=0 Radius=1
    g3: BSplineCurve PolesCount=3 KnotsCount=2 Degree=2 IsPeriodic=0
    g4: GeomPoint X=0 Y=0 Z=0
    g5: GeomPoint X=8 Y=6 Z=0
    g6: LineSegment StartX=0 StartY=6 StartZ=0 EndX=8 EndY=6 EndZ=0
  constraints (14):
    c: Coincident(g0,g-1)
    c: Distance(g0) = 6
    c: Vertical(g0)
    c: Coincident(g3,g0)
    c: Weight(g1) = 1
    c: Equal(g1,g2)
    c: InternalAlignment(g1,g3)
    c: InternalAlignment(g2,g3)
    c: InternalAlignment(g4,g3)
    c: InternalAlignment(g5,g3)
    c: Block(g3)
    c: Coincident(g6,g0)
    c: Coincident(g6,g3)
    c: Horizontal(g6)
FEATURE [Part::Extrusion] Extrude034  label="caseScrewPillarBracket012"
  Base = -> Sketch043
  Dir = (0,0,1)
  DirMode = 2
  FaceMakerClass = Part::FaceMakerBullseye
  LengthFwd = 2.4
  LengthRev = 0
  Placement = pos=(88.3,29,65.23) rot=(0,1,0;1.5708rad)
  Solid = true
  Symmetric = false
FEATURE [Sketcher::SketchObject] Sketch044
  FullyConstrained = true
  sketch-geometry (7):
    g0: LineSegment StartX=0 StartY=0 StartZ=0 EndX=0 EndY=6 EndZ=0
    g1: Circle CenterX=0 CenterY=0 CenterZ=0 NormalX=0 NormalY=0 NormalZ=1 AngleXU=0 Radius=1
    g2: Circle CenterX=8 CenterY=6 CenterZ=0 NormalX=0 NormalY=0 NormalZ=1 AngleXU=0 Radius=1
    g3: BSplineCurve PolesCount=3 KnotsCount=2 Degree=2 IsPeriodic=0
    g4: GeomPoint X=0 Y=0 Z=0
    g5: GeomPoint X=8 Y=6 Z=0
    g6: LineSegment StartX=0 StartY=6 StartZ=0 EndX=8 EndY=6 EndZ=0
  constraints (14):
    c: Coincident(g0,g-1)
    c: Distance(g0) = 6
    c: Vertical(g0)
    c: Coincident(g3,g0)
    c: Weight(g1) = 1
    c: Equal(g1,g2)
    c: InternalAlignment(g1,g3)
    c: InternalAlignment(g2,g3)
    c: InternalAlignment(g4,g3)
    c: InternalAlignment(g5,g3)
    c: Block(g3)
    c: Coincident(g6,g0)
    c: Coincident(g6,g3)
    c: Horizontal(g6)
FEATURE [Part::Extrusion] Extrude035  label="caseScrewPillarBracket013"
  Base = -> Sketch044
  Dir = (0,0,1)
  DirMode = 2
  FaceMakerClass = Part::FaceMakerBullseye
  LengthFwd = 2.4
  LengthRev = 0
  Placement = pos=(90.7,29,6.77) rot=(0,-1,0;1.5708rad)
  Solid = true
  Symmetric = false
FEATURE [Sketcher::SketchObject] Sketch045
  FullyConstrained = true
  sketch-geometry (7):
    g0: LineSegment StartX=0 StartY=0 StartZ=0 EndX=0 EndY=6 EndZ=0
    g1: Circle CenterX=0 CenterY=0 CenterZ=0 NormalX=0 NormalY=0 NormalZ=1 AngleXU=0 Radius=1
    g2: Circle CenterX=8 CenterY=6 CenterZ=0 NormalX=0 NormalY=0 NormalZ=1 AngleXU=0 Radius=1
    g3: BSplineCurve PolesCount=3 KnotsCount=2 Degree=2 IsPeriodic=0
    g4: GeomPoint X=0 Y=0 Z=0
    g5: GeomPoint X=8 Y=6 Z=0
    g6: LineSegment StartX=0 StartY=6 StartZ=0 EndX=8 EndY=6 EndZ=0
  constraints (14):
    c: Coincident(g0,g-1)
    c: Distance(g0) = 6
    c: Vertical(g0)
    c: Coincident(g3,g0)
    c: Weight(g1) = 1
    c: Equal(g1,g2)
    c: InternalAlignment(g1,g3)
    c: InternalAlignment(g2,g3)
    c: InternalAlignment(g4,g3)
    c: InternalAlignment(g5,g3)
    c: Block(g3)
    c: Coincident(g6,g0)
    c: Coincident(g6,g3)
    c: Horizontal(g6)
FEATURE [Sketcher::SketchObject] Sketch046
  FullyConstrained = true
  sketch-geometry (7):
    g0: LineSegment StartX=0 StartY=0 StartZ=0 EndX=0 EndY=6 EndZ=0
    g1: Circle CenterX=0 CenterY=0 CenterZ=0 NormalX=0 NormalY=0 NormalZ=1 AngleXU=0 Radius=1
    g2: Circle CenterX=8 CenterY=6 CenterZ=0 NormalX=0 NormalY=0 NormalZ=1 AngleXU=0 Radius=1
    g3: BSplineCurve PolesCount=3 KnotsCount=2 Degree=2 IsPeriodic=0
    g4: GeomPoint X=0 Y=0 Z=0
    g5: GeomPoint X=8 Y=6 Z=0
    g6: LineSegment StartX=0 StartY=6 StartZ=0 EndX=8 EndY=6 EndZ=0
  constraints (14):
    c: Coincident(g0,g-1)
    c: Distance(g0) = 6
    c: Vertical(g0)
    c: Coincident(g3,g0)
    c: Weight(g1) = 1
    c: Equal(g1,g2)
    c: InternalAlignment(g1,g3)
    c: InternalAlignment(g2,g3)
    c: InternalAlignment(g4,g3)
    c: InternalAlignment(g5,g3)
    c: Block(g3)
    c: Coincident(g6,g0)
    c: Coincident(g6,g3)
    c: Horizontal(g6)
FEATURE [Part::Extrusion] Extrude036  label="caseScrewPillarBracket014"
  Base = -> Sketch045
  Dir = (0,0,1)
  DirMode = 2
  FaceMakerClass = Part::FaceMakerBullseye
  LengthFwd = 2.4
  LengthRev = 0
  Placement = pos=(110.7,29,6.77) rot=(0,-1,0;1.5708rad)
  Solid = true
  Symmetric = false
FEATURE [Part::Extrusion] Extrude037  label="caseScrewPillarBracket015"
  Base = -> Sketch046
  Dir = (0,0,1)
  DirMode = 2
  FaceMakerClass = Part::FaceMakerBullseye
  LengthFwd = 2.4
  LengthRev = 0
  Placement = pos=(108.3,29,65.23) rot=(0,1,0;1.5708rad)
  Solid = true
  Symmetric = false
FEATURE [Part::Box] Box013  label="frontCaseScrewPillarBracket002"
  AttacherType = Attacher::AttachEngine3D
  Height = 2.4
  Length = 22
  Placement = pos=(87,28,2.3) rot=(0,0,1;0rad)
  Width = 7
FEATURE [Part::Box] Box014  label="frontCaseScrewPillarBracket003"
  AttacherType = Attacher::AttachEngine3D
  Height = 2.4
  Length = 22
  Placement = pos=(87,28,67.3) rot=(0,0,1;0rad)
  Width = 7
FEATURE [Part::Feature] Face087
  shape: bbox 4.8 x 30.2 x 2e-07 mm, 1 faces, 0 solids (baked)
FEATURE [Part::Revolution] Revolve091  label="frontCaseScrewPost004"
  Angle = 360
  Axis = (0,1,0)
  Base = (0,0,0)
  FaceMakerClass = Part::FaceMakerBullseye
  Placement = pos=(89.5,4.5,3.5) rot=(0,0,1;0rad)
  Solid = false
  Source = -> Face087
  Symmetric = false
FEATURE [Part::Feature] Face088
  shape: bbox 4.8 x 30.2 x 2e-07 mm, 1 faces, 0 solids (baked)
FEATURE [Part::Revolution] Revolve092  label="frontCaseScrewPost005"
  Angle = 360
  Axis = (0,1,0)
  Base = (0,0,0)
  FaceMakerClass = Part::FaceMakerBullseye
  Placement = pos=(89.5,4.5,68.5) rot=(0,0,1;0rad)
  Solid = false
  Source = -> Face088
  Symmetric = false
FEATURE [Part::Feature] Face089
  shape: bbox 3.5 x 30.2 x 2e-07 mm, 1 faces, 0 solids (baked)
FEATURE [Part::Revolution] Revolve093  label="backCaseScrewPost002"
  Angle = 360
  Axis = (0,1,0)
  Base = (0,0,0)
  FaceMakerClass = Part::FaceMakerBullseye
  Placement = pos=(12.5,4.5,10) rot=(0,0,1;0rad)
  Solid = false
  Source = -> Face089
  Symmetric = false
FEATURE [Part::Feature] Face090
  shape: bbox 3.5 x 30.2 x 2e-07 mm, 1 faces, 0 solids (baked)
FEATURE [Part::Revolution] Revolve094  label="backCaseScrewPost003"
  Angle = 360
  Axis = (0,1,0)
  Base = (0,0,0)
  FaceMakerClass = Part::FaceMakerBullseye
  Placement = pos=(12.5,4.5,62) rot=(0,0,1;0rad)
  Solid = false
  Source = -> Face090
  Symmetric = false
FEATURE [Part::Box] Box015  label="Cube011"
  AttacherType = Attacher::AttachEngine3D
  Height = 28.8
  Length = 3
  Placement = pos=(107.3,28,21.6) rot=(0,0,1;0rad)
  Width = 7
FEATURE [Part::Box] Box016  label="Cube012"
  AttacherType = Attacher::AttachEngine3D
  Height = 3
  Length = 7.4
  Placement = pos=(107.3,28,18.6) rot=(0,0,1;0rad)
  Width = 7
FEATURE [Part::Box] Box017  label="Cube013"
  AttacherType = Attacher::AttachEngine3D
  Height = 3
  Length = 7.4
  Placement = pos=(107.3,28,50.4) rot=(0,0,1;0rad)
  Width = 7
FEATURE [Part::Cylinder] Cylinder024
  Angle = 360
  AttacherType = Attacher::AttachEngine3D
  Height = 20
  Placement = pos=(0,0,36.15) rot=(0,0,1;0rad)
  Radius = 14.3
FEATURE [Part::Cylinder] Cylinder025
  Angle = 360
  AttacherType = Attacher::AttachEngine3D
  Height = 10
  Placement = pos=(0,0,36.15) rot=(0,0,1;0rad)
  Radius = 4
FEATURE [Part::MultiFuse] Fusion066  label="removeToCreteHoleForPlugHousing009"
  Placement = pos=(70,19,36) rot=(0,1,0;1.5708rad)
  Shapes = -> [Cylinder024,Cylinder025]
FEATURE [Part::MultiFuse] Fusion065  label="plugHousingBracketHolder002"
  Shapes = -> [Box017,Box015,Box016]
FEATURE [Part::Cut] Cut025  label="plugHousingBracketHolder003"
  Base = -> Fusion065
  Placement = pos=(7,0,0) rot=(0,0,1;0rad)
  Tool = -> Fusion066
FEATURE [Sketcher::SketchObject] Sketch047
  FullyConstrained = false
  Placement = pos=(0,0,0) rot=(1,0,0;1.5708rad)
  sketch-geometry (24):
    g0: ArcOfCircle CenterX=-4 CenterY=-10.5 CenterZ=0 NormalX=0 NormalY=0 NormalZ=1 AngleXU=0 Radius=1.5 StartAngle=6e-16 EndAngle=3.14159
    g1: ArcOfCircle CenterX=-34.2 CenterY=-10.5 CenterZ=0 NormalX=0 NormalY=0 NormalZ=1 AngleXU=0 Radius=1.5 StartAngle=0 EndAngle=3.14159
    g2: ArcOfCircle CenterX=-34.2 CenterY=-27.7 CenterZ=0 NormalX=0 NormalY=0 NormalZ=1 AngleXU=0 Radius=1.5 StartAngle=3.14159 EndAngle=6.28319
    g3: ArcOfCircle CenterX=-4 CenterY=-27.7 CenterZ=0 NormalX=0 NormalY=0 NormalZ=1 AngleXU=0 Radius=1.5 StartAngle=3.1416 EndAngle=6.28319
    g4: ArcOfCircle CenterX=-10 CenterY=-4.3 CenterZ=0 NormalX=0 NormalY=0 NormalZ=1 AngleXU=0 Radius=1.5 StartAngle=2e-16 EndAngle=3.14159
    g5: ArcOfCircle CenterX=-16.1 CenterY=-1.8 CenterZ=0 NormalX=0 NormalY=0 NormalZ=1 AngleXU=0 Radius=1.5 StartAngle=5e-16 EndAngle=3.14159
    g6: ArcOfCircle CenterX=-22.1 CenterY=-1.8 CenterZ=0 NormalX=0 NormalY=0 NormalZ=1 AngleXU=0 Radius=1.5 StartAngle=5e-16 EndAngle=3.14159
    g7: ArcOfCircle CenterX=-28.2 CenterY=-4.3 CenterZ=0 NormalX=0 NormalY=0 NormalZ=1 AngleXU=0 Radius=1.5 StartAngle=2e-16 EndAngle=3.14159
    g8: ArcOfCircle CenterX=-10 CenterY=-33.9 CenterZ=0 NormalX=0 NormalY=0 NormalZ=1 AngleXU=0 Radius=1.5 StartAngle=3.14159 EndAngle=6.28319
    g9: ArcOfCircle CenterX=-16.1 CenterY=-36.4 CenterZ=0 NormalX=0 NormalY=0 NormalZ=1 AngleXU=0 Radius=1.5 StartAngle=3.14159 EndAngle=6.28319
    g10: ArcOfCircle CenterX=-22.1 CenterY=-36.4 CenterZ=0 NormalX=0 NormalY=0 NormalZ=1 AngleXU=0 Radius=1.5 StartAngle=3.14159 EndAngle=6.28319
    g11: ArcOfCircle CenterX=-28.2 CenterY=-33.9 CenterZ=0 NormalX=0 NormalY=0 NormalZ=1 AngleXU=0 Radius=1.5 StartAngle=3.14159 EndAngle=6.28319
    g12: LineSegment StartX=-35.7 StartY=-10.5 StartZ=0 EndX=-35.7 EndY=-27.7 EndZ=0
    g13: LineSegment StartX=-32.7 StartY=-10.5 StartZ=0 EndX=-32.7 EndY=-27.7 EndZ=0
    g14: LineSegment StartX=-29.7 StartY=-33.9 StartZ=0 EndX=-29.7 EndY=-4.3 EndZ=0
    g15: LineSegment StartX=-26.7 StartY=-33.9 StartZ=0 EndX=-26.7 EndY=-4.3 EndZ=0
    g16: LineSegment StartX=-2.5 StartY=-10.5 StartZ=0 EndX=-2.5 EndY=-27.7 EndZ=0
    g17: LineSegment StartX=-8.5 StartY=-4.3 StartZ=0 EndX=-8.5 EndY=-33.9 EndZ=0
    g18: LineSegment StartX=-5.5 StartY=-10.5 StartZ=0 EndX=-5.5 EndY=-27.7 EndZ=0
    g19: LineSegment StartX=-11.5 StartY=-4.3 StartZ=0 EndX=-11.5 EndY=-33.9 EndZ=0
    g20: LineSegment StartX=-14.6 StartY=-1.8 StartZ=0 EndX=-14.6 EndY=-36.4 EndZ=0
    g21: LineSegment StartX=-17.6 StartY=-1.8 StartZ=0 EndX=-17.6 EndY=-36.4 EndZ=0
    g22: LineSegment StartX=-20.6 StartY=-36.4 StartZ=0 EndX=-20.6 EndY=-1.8 EndZ=0
    g23: LineSegment StartX=-23.6 StartY=-1.8 StartZ=0 EndX=-23.6 EndY=-36.4 EndZ=0
  constraints (48):
    c: Block(g0)
    c: Block(g1)
    c: Block(g2)
    c: Block(g3)
    c: Block(g4)
    c: Block(g5)
    c: Block(g6)
    c: Block(g7)
    c: Block(g8)
    c: Block(g9)
    c: Block(g10)
    c: Block(g11)
    c: Coincident(g12,g1)
    c: Coincident(g12,g2)
    c: Vertical(g12)
    c: Coincident(g13,g1)
    c: Coincident(g13,g2)
    c: Vertical(g13)
    c: Coincident(g14,g11)
    c: Coincident(g14,g7)
    c: Vertical(g14)
    c: Coincident(g15,g11)
    c: Coincident(g15,g7)
    c: Vertical(g15)
    c: Coincident(g16,g0)
    c: Coincident(g16,g3)
    c: Vertical(g16)
    c: Coincident(g17,g4)
    c: Coincident(g17,g8)
    c: Vertical(g17)
    c: Coincident(g18,g0)
    c: Coincident(g18,g3)
    c: Vertical(g18)
    c: Coincident(g19,g4)
    c: Coincident(g19,g8)
    c: Vertical(g19)
    c: Coincident(g20,g5)
    c: Coincident(g20,g9)
    c: Vertical(g20)
    c: Coincident(g21,g5)
    c: Coincident(g21,g9)
    c: Vertical(g21)
    c: Coincident(g22,g10)
    c: Coincident(g22,g6)
    c: Vertical(g22)
    c: Coincident(g23,g6)
    c: Coincident(g23,g10)
    c: Vertical(g23)
FEATURE [Part::Extrusion] Extrude038  label="removeToCreateFanGrillHoles001"
  Base = -> Sketch047
  Dir = (0,-1,6e-16)
  DirMode = 2
  FaceMakerClass = Part::FaceMakerBullseye
  LengthFwd = 10
  LengthRev = 0
  Placement = pos=(65.4,44,54.82) rot=(0,0,1;0rad)
  Solid = true
  Symmetric = false
FEATURE [Part::Feature] Wire004
  shape: bbox 11 x 5.2 x 2e-07 mm, 0 faces, 0 solids (baked)
FEATURE [Part::Revolution] Revolve095
  Angle = 360
  Axis = (0,1,0)
  Base = (0,0,0)
  FaceMakerClass = Part::FaceMakerBullseye
  Placement = pos=(30.3,38,19.7) rot=(0,0,1;0rad)
  Solid = true
  Source = -> Wire004
  Symmetric = false
FEATURE [Part::Feature] Wire005
  shape: bbox 11 x 5.2 x 2e-07 mm, 0 faces, 0 solids (baked)
FEATURE [Part::Revolution] Revolve096
  Angle = 360
  Axis = (0,1,0)
  Base = (0,0,0)
  FaceMakerClass = Part::FaceMakerBullseye
  Placement = pos=(30.3,38,51.7) rot=(0,0,1;0rad)
  Solid = true
  Source = -> Wire005
  Symmetric = false
FEATURE [Part::Feature] Wire006
  shape: bbox 11 x 5.2 x 2e-07 mm, 0 faces, 0 solids (baked)
FEATURE [Part::Revolution] Revolve097
  Angle = 360
  Axis = (0,1,0)
  Base = (0,0,0)
  FaceMakerClass = Part::FaceMakerBullseye
  Placement = pos=(62.3,38,51.7) rot=(0,0,1;0rad)
  Solid = true
  Source = -> Wire006
  Symmetric = false
FEATURE [Part::Feature] Wire007
  shape: bbox 11 x 5.2 x 2e-07 mm, 0 faces, 0 solids (baked)
FEATURE [Part::Revolution] Revolve098
  Angle = 360
  Axis = (0,1,0)
  Base = (0,0,0)
  FaceMakerClass = Part::FaceMakerBullseye
  Placement = pos=(62.3,38,19.7) rot=(0,0,1;0rad)
  Solid = true
  Source = -> Wire007
  Symmetric = false
FEATURE [Part::MultiFuse] Fusion067  label="fanScrewHousing002"
  Shapes = -> [Revolve098,Revolve097,Revolve096,Revolve095]
FEATURE [Part::Feature] Face091 .. Face094  x4 (patterned run collapsed; names and placements below)
  shape: bbox 3.5 x 17.8 x 2e-07 mm, 1 faces, 0 solids (baked)
FEATURE [Part::Revolution] Revolve099  label="removeToCreateScrewAndThreadedInsertHole026"
  Angle = 360
  Axis = (0,1,0)
  Base = (0,0,0)
  FaceMakerClass = Part::FaceMakerBullseye
  Placement = pos=(62.3,30.3,19.7) rot=(0,0,1;0rad)
  Solid = false
  Source = -> Face091
  Symmetric = false
FEATURE [Part::Revolution] Revolve100  label="removeToCreateScrewAndThreadedInsertHole027"
  Angle = 360
  Axis = (0,1,0)
  Base = (0,0,0)
  FaceMakerClass = Part::FaceMakerBullseye
  Placement = pos=(62.3,30.3,51.7) rot=(0,0,1;0rad)
  Solid = false
  Source = -> Face092
  Symmetric = false
FEATURE [Part::Revolution] Revolve101  label="removeToCreateScrewAndThreadedInsertHole028"
  Angle = 360
  Axis = (0,1,0)
  Base = (0,0,0)
  FaceMakerClass = Part::FaceMakerBullseye
  Placement = pos=(30.3,30.3,19.7) rot=(0,0,1;0rad)
  Solid = false
  Source = -> Face093
  Symmetric = false
FEATURE [Part::Revolution] Revolve102  label="removeToCreateScrewAndThreadedInsertHole029"
  Angle = 360
  Axis = (0,1,0)
  Base = (0,0,0)
  FaceMakerClass = Part::FaceMakerBullseye
  Placement = pos=(30.3,30.3,51.7) rot=(0,0,1;0rad)
  Solid = false
  Source = -> Face094
  Symmetric = false
FEATURE [Part::MultiFuse] Fusion068  label="createThreadedInsertHolesForFan002"
  Shapes = -> [Revolve099,Revolve100,Revolve101,Revolve102]
FEATURE [Part::Cut] Cut026  label="fanScrewHousing003"
  Base = -> Fusion067
  Tool = -> Fusion068
FEATURE [Sketcher::SketchObject] Sketch048
  FullyConstrained = false
  Placement = pos=(0,0,0) rot=(1,0,0;1.5708rad)
  sketch-geometry (24):
    g0: ArcOfCircle CenterX=-4 CenterY=-10.5 CenterZ=0 NormalX=0 NormalY=0 NormalZ=1 AngleXU=0 Radius=1.5 StartAngle=6e-16 EndAngle=3.14159
    g1: ArcOfCircle CenterX=-34.2 CenterY=-10.5 CenterZ=0 NormalX=0 NormalY=0 NormalZ=1 AngleXU=0 Radius=1.5 StartAngle=0 EndAngle=3.14159
    g2: ArcOfCircle CenterX=-34.2 CenterY=-27.7 CenterZ=0 NormalX=0 NormalY=0 NormalZ=1 AngleXU=0 Radius=1.5 StartAngle=3.14159 EndAngle=6.28319
    g3: ArcOfCircle CenterX=-4 CenterY=-27.7 CenterZ=0 NormalX=0 NormalY=0 NormalZ=1 AngleXU=0 Radius=1.5 StartAngle=3.1416 EndAngle=6.28319
    g4: ArcOfCircle CenterX=-10 CenterY=-4.3 CenterZ=0 NormalX=0 NormalY=0 NormalZ=1 AngleXU=0 Radius=1.5 StartAngle=2e-16 EndAngle=3.14159
    g5: ArcOfCircle CenterX=-16.1 CenterY=-1.8 CenterZ=0 NormalX=0 NormalY=0 NormalZ=1 AngleXU=0 Radius=1.5 StartAngle=5e-16 EndAngle=3.14159
    g6: ArcOfCircle CenterX=-22.1 CenterY=-1.8 CenterZ=0 NormalX=0 NormalY=0 NormalZ=1 AngleXU=0 Radius=1.5 StartAngle=5e-16 EndAngle=3.14159
    g7: ArcOfCircle CenterX=-28.2 CenterY=-4.3 CenterZ=0 NormalX=0 NormalY=0 NormalZ=1 AngleXU=0 Radius=1.5 StartAngle=2e-16 EndAngle=3.14159
    g8: ArcOfCircle CenterX=-10 CenterY=-33.9 CenterZ=0 NormalX=0 NormalY=0 NormalZ=1 AngleXU=0 Radius=1.5 StartAngle=3.14159 EndAngle=6.28319
    g9: ArcOfCircle CenterX=-16.1 CenterY=-36.4 CenterZ=0 NormalX=0 NormalY=0 NormalZ=1 AngleXU=0 Radius=1.5 StartAngle=3.14159 EndAngle=6.28319
    g10: ArcOfCircle CenterX=-22.1 CenterY=-36.4 CenterZ=0 NormalX=0 NormalY=0 NormalZ=1 AngleXU=0 Radius=1.5 StartAngle=3.14159 EndAngle=6.28319
    g11: ArcOfCircle CenterX=-28.2 CenterY=-33.9 CenterZ=0 NormalX=0 NormalY=0 NormalZ=1 AngleXU=0 Radius=1.5 StartAngle=3.14159 EndAngle=6.28319
    g12: LineSegment StartX=-35.7 StartY=-10.5 StartZ=0 EndX=-35.7 EndY=-27.7 EndZ=0
    g13: LineSegment StartX=-32.7 StartY=-10.5 StartZ=0 EndX=-32.7 EndY=-27.7 EndZ=0
    g14: LineSegment StartX=-29.7 StartY=-33.9 StartZ=0 EndX=-29.7 EndY=-4.3 EndZ=0
    g15: LineSegment StartX=-26.7 StartY=-33.9 StartZ=0 EndX=-26.7 EndY=-4.3 EndZ=0
    g16: LineSegment StartX=-2.5 StartY=-10.5 StartZ=0 EndX=-2.5 EndY=-27.7 EndZ=0
    g17: LineSegment StartX=-8.5 StartY=-4.3 StartZ=0 EndX=-8.5 EndY=-33.9 EndZ=0
    g18: LineSegment StartX=-5.5 StartY=-10.5 StartZ=0 EndX=-5.5 EndY=-27.7 EndZ=0
    g19: LineSegment StartX=-11.5 StartY=-4.3 StartZ=0 EndX=-11.5 EndY=-33.9 EndZ=0
    g20: LineSegment StartX=-14.6 StartY=-1.8 StartZ=0 EndX=-14.6 EndY=-36.4 EndZ=0
    g21: LineSegment StartX=-17.6 StartY=-1.8 StartZ=0 EndX=-17.6 EndY=-36.4 EndZ=0
    g22: LineSegment StartX=-20.6 StartY=-36.4 StartZ=0 EndX=-20.6 EndY=-1.8 EndZ=0
    g23: LineSegment StartX=-23.6 StartY=-1.8 StartZ=0 EndX=-23.6 EndY=-36.4 EndZ=0
  constraints (48):
    c: Block(g0)
    c: Block(g1)
    c: Block(g2)
    c: Block(g3)
    c: Block(g4)
    c: Block(g5)
    c: Block(g6)
    c: Block(g7)
    c: Block(g8)
    c: Block(g9)
    c: Block(g10)
    c: Block(g11)
    c: Coincident(g12,g1)
    c: Coincident(g12,g2)
    c: Vertical(g12)
    c: Coincident(g13,g1)
    c: Coincident(g13,g2)
    c: Vertical(g13)
    c: Coincident(g14,g11)
    c: Coincident(g14,g7)
    c: Vertical(g14)
    c: Coincident(g15,g11)
    c: Coincident(g15,g7)
    c: Vertical(g15)
    c: Coincident(g16,g0)
    c: Coincident(g16,g3)
    c: Vertical(g16)
    c: Coincident(g17,g4)
    c: Coincident(g17,g8)
    c: Vertical(g17)
    c: Coincident(g18,g0)
    c: Coincident(g18,g3)
    c: Vertical(g18)
    c: Coincident(g19,g4)
    c: Coincident(g19,g8)
    c: Vertical(g19)
    c: Coincident(g20,g5)
    c: Coincident(g20,g9)
    c: Vertical(g20)
    c: Coincident(g21,g5)
    c: Coincident(g21,g9)
    c: Vertical(g21)
    c: Coincident(g22,g10)
    c: Coincident(g22,g6)
    c: Vertical(g22)
    c: Coincident(g23,g6)
    c: Coincident(g23,g10)
    c: Vertical(g23)
FEATURE [Part::Extrusion] Extrude039  label="removeToCreateFanGrillHoles002"
  Base = -> Sketch048
  Dir = (0,-1,6e-16)
  DirMode = 2
  FaceMakerClass = Part::FaceMakerBullseye
  LengthFwd = 10
  LengthRev = 0
  Placement = pos=(65.4,44,54.82) rot=(0,0,1;0rad)
  Solid = true
  Symmetric = false
FEATURE [Part::Cut] Cut027  label="fanScrewHousing004"
  Base = -> Cut026
  Tool = -> Extrude038
FEATURE [Part::Cut] Cut028  label="top014"
  Base = -> Fillet026
  Tool = -> Extrude039
FEATURE [Part::Feature] Face095 .. Face098  x4 (patterned run collapsed; names and placements below)
  shape: bbox 3.5 x 17.8 x 2e-07 mm, 1 faces, 0 solids (baked)
FEATURE [Part::Revolution] Revolve103  label="removeToCreateScrewAndThreadedInsertHole030"
  Angle = 360
  Axis = (0,1,0)
  Base = (0,0,0)
  FaceMakerClass = Part::FaceMakerBullseye
  Placement = pos=(62.3,30.3,19.7) rot=(0,0,1;0rad)
  Solid = false
  Source = -> Face095
  Symmetric = false
FEATURE [Part::Revolution] Revolve104  label="removeToCreateScrewAndThreadedInsertHole031"
  Angle = 360
  Axis = (0,1,0)
  Base = (0,0,0)
  FaceMakerClass = Part::FaceMakerBullseye
  Placement = pos=(62.3,30.3,51.7) rot=(0,0,1;0rad)
  Solid = false
  Source = -> Face096
  Symmetric = false
FEATURE [Part::Revolution] Revolve105  label="removeToCreateScrewAndThreadedInsertHole032"
  Angle = 360
  Axis = (0,1,0)
  Base = (0,0,0)
  FaceMakerClass = Part::FaceMakerBullseye
  Placement = pos=(30.3,30.3,19.7) rot=(0,0,1;0rad)
  Solid = false
  Source = -> Face097
  Symmetric = false
FEATURE [Part::Revolution] Revolve106  label="removeToCreateScrewAndThreadedInsertHole033"
  Angle = 360
  Axis = (0,1,0)
  Base = (0,0,0)
  FaceMakerClass = Part::FaceMakerBullseye
  Placement = pos=(30.3,30.3,51.7) rot=(0,0,1;0rad)
  Solid = false
  Source = -> Face098
  Symmetric = false
FEATURE [Part::MultiFuse] Fusion069  label="createThreadedInsertHolesForFan003"
  Shapes = -> [Revolve103,Revolve104,Revolve105,Revolve106]
FEATURE [Part::Cut] Cut029  label="top015"
  Base = -> Cut028
  Tool = -> Fusion054
FEATURE [Part::Cut] Cut030  label="fanScrewHousing005"
  Base = -> Cut027
  Tool = -> Fusion069
FEATURE [Part::Cylinder] Cylinder026  label="removeToCreteHoleForPlugHousing010"
  Angle = 360
  AttacherType = Attacher::AttachEngine3D
  Height = 20
  Placement = pos=(-2,19,36) rot=(0,1,0;1.5708rad)
  Radius = 14.3
FEATURE [Part::Box] Box018  label="removeToCreteHoleForPlugHousing011"
  AttacherType = Attacher::AttachEngine3D
  Height = 28.6
  Length = 10
  Placement = pos=(-2,0,21.7) rot=(0,0,1;0rad)
  Width = 19
FEATURE [Part::Box] Box019  label="wireHolderBottomCaseBit"
  AttacherType = Attacher::AttachEngine3D
  Height = 28
  Length = 3
  Placement = pos=(0,0,22) rot=(0,0,1;0rad)
  Width = 21
FEATURE [Part::Cylinder] Cylinder027  label="removeToCreteHoleForPlugHousing012"
  Angle = 360
  AttacherType = Attacher::AttachEngine3D
  Height = 20
  Placement = pos=(-2,19,36) rot=(0,1,0;1.5708rad)
  Radius = 14.3
FEATURE [Part::Cut] Cut031  label="wireHolderBottomCaseBit001"
  Base = -> Box019
  Tool = -> Cylinder027
FEATURE [Part::MultiFuse] Fusion070  label="removeToCreteHoleForPlugHousing013"
  Shapes = -> [Box018,Cylinder026]
FEATURE [Part::Cut] Cut032  label="top016"
  Base = -> Cut029
  Tool = -> Fusion070
FEATURE [Part::Cylinder] Cylinder028
  Angle = 360
  AttacherType = Attacher::AttachEngine3D
  Height = 20
  Placement = pos=(0,0,36.15) rot=(0,0,1;0rad)
  Radius = 14.3
FEATURE [Part::Cylinder] Cylinder029
  Angle = 360
  AttacherType = Attacher::AttachEngine3D
  Height = 10
  Placement = pos=(0,0,36.15) rot=(0,0,1;0rad)
  Radius = 4
FEATURE [Part::MultiFuse] Fusion071  label="removeToCreteHoleForPlugHousing014"
  Placement = pos=(70,19,36) rot=(0,1,0;1.5708rad)
  Shapes = -> [Cylinder028,Cylinder029]
FEATURE [Sketcher::SketchObject] Sketch049  label="topSketch011"
  FullyConstrained = true
  sketch-geometry (4):
    g0: ArcOfCircle CenterX=105 CenterY=19 CenterZ=0 NormalX=0 NormalY=0 NormalZ=1 AngleXU=0 Radius=20.6155 StartAngle=5.54125 EndAngle=6.28319
    g1: ArcOfCircle CenterX=105 CenterY=19 CenterZ=0 NormalX=0 NormalY=0 NormalZ=1 AngleXU=0 Radius=13 StartAngle=5.54125 EndAngle=6.28319
    g2: LineSegment StartX=118 StartY=19 StartZ=0 EndX=125.616 EndY=19 EndZ=0
    g3: LineSegment StartX=114.583 StartY=10.2157 StartZ=0 EndX=120.197 EndY=5.06982 EndZ=0
  constraints (7):
    c: Block(g0)
    c: Block(g1)
    c: Coincident(g2,g1)
    c: Coincident(g2,g0)
    c: Horizontal(g2)
    c: Coincident(g3,g1)
    c: Coincident(g3,g0)
FEATURE [Part::Box] Box020  label="removeToCreteHoleForPlugHousing015"
  AttacherType = Attacher::AttachEngine3D
  Height = 28.6
  Length = 20
  Placement = pos=(106.15,0,21.7) rot=(0,0,1;0rad)
  Width = 19
FEATURE [Part::MultiFuse] Fusion072  label="removeToCreteHoleForPlugHousing016"
  Shapes = -> [Box020,Fusion071]
FEATURE [Part::Cut] Cut033  label="removeToCreteHoleForPlugHousing017"
  Base = -> Cut032
  Tool = -> Fusion072
FEATURE [Part::Cylinder] Cylinder030
  Angle = 360
  AttacherType = Attacher::AttachEngine3D
  Height = 20
  Placement = pos=(0,0,36.15) rot=(0,0,1;0rad)
  Radius = 14.3
FEATURE [Part::Cylinder] Cylinder031
  Angle = 360
  AttacherType = Attacher::AttachEngine3D
  Height = 10
  Placement = pos=(0,0,36.15) rot=(0,0,1;0rad)
  Radius = 4
FEATURE [Part::Box] Box021  label="removeToCreteHoleForPlugHousing019"
  AttacherType = Attacher::AttachEngine3D
  Height = 28.6
  Length = 20
  Placement = pos=(106.15,0,21.7) rot=(0,0,1;0rad)
  Width = 19
FEATURE [Part::MultiFuse] Fusion074  label="removeToCreteHoleForPlugHousing020"
  Placement = pos=(70,19,36) rot=(0,1,0;1.5708rad)
  Shapes = -> [Cylinder030,Cylinder031]
FEATURE [Part::MultiFuse] Fusion073  label="removeToCreteHoleForPlugHousing018"
  Placement = pos=(0,0,28.3) rot=(0,0,1;0rad)
  Shapes = -> [Box021,Fusion074]
FEATURE [Part::Cylinder] Cylinder032
  Angle = 360
  AttacherType = Attacher::AttachEngine3D
  Height = 20
  Placement = pos=(0,0,36.15) rot=(0,0,1;0rad)
  Radius = 14.3
FEATURE [Part::Cylinder] Cylinder033
  Angle = 360
  AttacherType = Attacher::AttachEngine3D
  Height = 10
  Placement = pos=(0,0,36.15) rot=(0,0,1;0rad)
  Radius = 4
FEATURE [Part::Box] Box022  label="removeToCreteHoleForPlugHousing021"
  AttacherType = Attacher::AttachEngine3D
  Height = 28.6
  Length = 20
  Placement = pos=(106.15,0,21.7) rot=(0,0,1;0rad)
  Width = 19
FEATURE [Part::MultiFuse] Fusion076  label="removeToCreteHoleForPlugHousing023"
  Placement = pos=(70,19,36) rot=(0,1,0;1.5708rad)
  Shapes = -> [Cylinder032,Cylinder033]
FEATURE [Part::MultiFuse] Fusion075  label="removeToCreteHoleForPlugHousing022"
  Placement = pos=(0,0,-28.3) rot=(0,0,1;0rad)
  Shapes = -> [Box022,Fusion076]
FEATURE [Part::MultiFuse] Fusion077  label="removeToCreatePlugHousingBottomBit"
  Shapes = -> [Fusion075,Fusion073]
FEATURE [Part::Cylinder] Cylinder034
  Angle = 360
  AttacherType = Attacher::AttachEngine3D
  Height = 20
  Placement = pos=(0,0,36.15) rot=(0,0,1;0rad)
  Radius = 14
FEATURE [Part::Cylinder] Cylinder035
  Angle = 360
  AttacherType = Attacher::AttachEngine3D
  Height = 10
  Placement = pos=(0,0,36.15) rot=(0,0,1;0rad)
  Radius = 4
FEATURE [Part::MultiFuse] Fusion078  label="removeToCreteHoleForPlugHousing024"
  Placement = pos=(70,19,36) rot=(0,1,0;1.5708rad)
  Shapes = -> [Cylinder034,Cylinder035]
FEATURE [Part::MultiFuse] Fusion079  label="removeToCreatePlugHousingBottomBit001"
  Shapes = -> [Fusion078,Fusion077]
FEATURE [Part::Extrusion] Extrude040  label="bottomPlugHousingBit"
  Base = -> Sketch049
  Dir = (0,0,1)
  DirMode = 2
  FaceMakerClass = Part::FaceMakerBullseye
  LengthFwd = 72
  LengthRev = 0
  Solid = true
  Symmetric = false
FEATURE [Part::Cut] Cut034  label="bottomPlugHousingBit001"
  Base = -> Extrude040
  Placement = pos=(-0.09,0,0) rot=(0,0,1;0rad)
  Tool = -> Fusion079
FEATURE [Part::Box] Box023  label="Cube014"
  AttacherType = Attacher::AttachEngine3D
  Height = 16
  Length = 8
  Placement = pos=(12.7,31.52,28) rot=(0,0,1;0rad)
  Width = 4
FEATURE [Part::Cylinder] Cylinder036
  Angle = 360
  AttacherType = Attacher::AttachEngine3D
  Height = 10
  Placement = pos=(0,0,36.15) rot=(0,0,1;0rad)
  Radius = 4
FEATURE [Part::Cylinder] Cylinder037
  Angle = 360
  AttacherType = Attacher::AttachEngine3D
  Height = 20
  Placement = pos=(0,0,36.15) rot=(0,0,1;0rad)
  Radius = 8.2
FEATURE [Part::MultiFuse] Fusion080  label="removeToCreteHoleForPlugHousing025"
  Placement = pos=(-42,19,36) rot=(0,1,0;1.5708rad)
  Shapes = -> [Cylinder037,Cylinder036]
FEATURE [Sketcher::SketchObject] Sketch050  label="topSketch012"
  FullyConstrained = true
  sketch-geometry (4):
    g0: LineSegment StartX=16.8446 StartY=31.512 StartZ=0 EndX=16.3251 EndY=34.4666 EndZ=0
    g1: ArcOfCircle CenterX=19 CenterY=19.2524 CenterZ=0 NormalX=0 NormalY=0 NormalZ=1 AngleXU=0 Radius=15.4476 StartAngle=1.74483 EndAngle=2.72717
    g2: ArcOfCircle CenterX=19 CenterY=19.2524 CenterZ=0 NormalX=0 NormalY=0 NormalZ=1 AngleXU=0 Radius=12.4476 StartAngle=1.74483 EndAngle=2.73189
    g3: LineSegment StartX=4.86004 StartY=25.4725 StartZ=0 EndX=7.58253 EndY=24.2107 EndZ=0
  constraints (7):
    c: Block(g0)
    c: Coincident(g1,g0)
    c: Coincident(g2,g0)
    c: Coincident(g3,g1)
    c: Coincident(g3,g2)
    c: Block(g1)
    c: Block(g2)
FEATURE [Part::Extrusion] Extrude041
  Base = -> Sketch050
  Dir = (0,0,1)
  DirMode = 2
  FaceMakerClass = Part::FaceMakerBullseye
  LengthFwd = 10.6
  LengthRev = 0
  Placement = pos=(0,0,31) rot=(0,0,1;0rad)
  Solid = true
  Symmetric = false
FEATURE [Part::Cut] Cut035
  Base = -> Extrude041
  Placement = pos=(0,0,-0.3) rot=(0,0,1;0rad)
  Tool = -> Fusion080
FEATURE [Part::Cut] Cut036
  Base = -> Box023
  Tool = -> Cut035
FEATURE [Part::Fillet] Fillet027
  Base = -> Cut036
  Edges = 1 edges r=0.7: [Edge13]
FEATURE [Part::Fillet] Fillet028
  Base = -> Fillet027
  Edges = 1 edges r=0.7: [Edge13]
FEATURE [Part::Fillet] Fillet029
  Base = -> Fillet028
  Edges = 1 edges r=0.7: [Edge16]
FEATURE [Part::Fillet] Fillet030
  Base = -> Fillet029
  Edges = 1 edges r=0.7: [Edge11]
FEATURE [Part::Fillet] Fillet031
  Base = -> Fillet030
  Edges = 1 edges r=0.7: [Edge10]
FEATURE [Part::Fillet] Fillet032
  Base = -> Fillet031
  Edges = 1 edges r=1.2: [Edge5]
FEATURE [Part::Fillet] Fillet033
  Base = -> Fillet032
  Edges = 1 edges r=1.2: [Edge12]
FEATURE [Part::Fillet] Fillet034  label="wireHousingRetainer"
  Base = -> Fillet033
  Edges = 1 edges r=2: [Edge1]
  Placement = pos=(0.3,0,0) rot=(0,0,1;0rad)
FEATURE [Part::Feature] Face099
  shape: bbox 3.5 x 17.8 x 2e-07 mm, 1 faces, 0 solids (baked)
FEATURE [Part::Revolution] Revolve107  label="removeToCreateScrewAndThreadedInsertHole034"
  Angle = 360
  Axis = (0,1,0)
  Base = (0,0,0)
  FaceMakerClass = Part::FaceMakerBullseye
  Placement = pos=(12.5,0,10) rot=(0,0,1;0rad)
  Solid = false
  Source = -> Face099
  Symmetric = false
FEATURE [Part::Feature] Face100
  shape: bbox 3.5 x 17.8 x 2e-07 mm, 1 faces, 0 solids (baked)
FEATURE [Part::Revolution] Revolve108  label="removeToCreateScrewAndThreadedInsertHole035"
  Angle = 360
  Axis = (0,1,0)
  Base = (0,0,0)
  FaceMakerClass = Part::FaceMakerBullseye
  Placement = pos=(12.5,0,62) rot=(0,0,1;0rad)
  Solid = false
  Source = -> Face100
  Symmetric = false
FEATURE [Part::Feature] Face101
  shape: bbox 3.5 x 17.8 x 2e-07 mm, 1 faces, 0 solids (baked)
FEATURE [Part::Revolution] Revolve109  label="removeToCreateScrewAndThreadedInsertHole036"
  Angle = 360
  Axis = (0,1,0)
  Base = (0,0,0)
  FaceMakerClass = Part::FaceMakerBullseye
  Placement = pos=(89.5,0,68.5) rot=(0,0,1;0rad)
  Solid = false
  Source = -> Face101
  Symmetric = false
FEATURE [Part::Feature] Face102
  shape: bbox 3.5 x 17.8 x 2e-07 mm, 1 faces, 0 solids (baked)
FEATURE [Part::Revolution] Revolve110  label="removeToCreateScrewAndThreadedInsertHole037"
  Angle = 360
  Axis = (0,1,0)
  Base = (0,0,0)
  FaceMakerClass = Part::FaceMakerBullseye
  Placement = pos=(89.5,0,3.5) rot=(0,0,1;0rad)
  Solid = false
  Source = -> Face102
  Symmetric = false
FEATURE [Part::Feature] Face103
  shape: bbox 3.5 x 17.8 x 2e-07 mm, 1 faces, 0 solids (baked)
FEATURE [Part::Revolution] Revolve111  label="removeToCreateScrewAndThreadedInsertHole038"
  Angle = 360
  Axis = (0,1,0)
  Base = (0,0,0)
  FaceMakerClass = Part::FaceMakerBullseye
  Placement = pos=(109.5,4.7,3.5) rot=(0,0,1;0rad)
  Solid = false
  Source = -> Face103
  Symmetric = false
FEATURE [Part::Feature] Face104
  shape: bbox 3.5 x 17.8 x 2e-07 mm, 1 faces, 0 solids (baked)
FEATURE [Part::Revolution] Revolve112  label="removeToCreateScrewAndThreadedInsertHole039"
  Angle = 360
  Axis = (0,1,0)
  Base = (0,0,0)
  FaceMakerClass = Part::FaceMakerBullseye
  Placement = pos=(109.5,4.7,68.5) rot=(0,0,1;0rad)
  Solid = false
  Source = -> Face104
  Symmetric = false
FEATURE [Part::MultiFuse] Fusion081  label="removeToCreateScrewAndThreadedInsertHole040"
  Shapes = -> [Revolve107,Revolve108,Revolve109,Revolve110,Revolve111,Revolve112]
FEATURE [Part::MultiFuse] Fusion082  label="casePillars002"
  Shapes = -> [Revolve094,Revolve092,Revolve090,Revolve089,Revolve091,Revolve093]
FEATURE [Part::Cut] Cut037  label="casePillars003"
  Base = -> Fusion082
  Tool = -> Fusion081
FEATURE [Sketcher::SketchObject] Sketch051
  FullyConstrained = true
  Placement = pos=(117,19,0) rot=(0.57735,0.57735,0.57735;2.0944rad)
  sketch-geometry (48):
    g0: LineSegment StartX=-49.19 StartY=69.25 StartZ=0 EndX=-49.19 EndY=66.25 EndZ=0
    g1: LineSegment StartX=-49.19 StartY=63.5 StartZ=0 EndX=-49.19 EndY=60.5 EndZ=0
    g2: LineSegment StartX=-49.19 StartY=57.75 StartZ=0 EndX=-49.19 EndY=54.75 EndZ=0
    g3: LineSegment StartX=-49.19 StartY=52 StartZ=0 EndX=-49.19 EndY=49 EndZ=0
    g4: LineSegment StartX=-49.19 StartY=46.25 StartZ=0 EndX=-49.19 EndY=43.25 EndZ=0
    g5: LineSegment StartX=-49.19 StartY=40.5 StartZ=0 EndX=-49.19 EndY=37.5 EndZ=0
    g6: LineSegment StartX=-49.19 StartY=34.5 StartZ=0 EndX=-49.19 EndY=31.5 EndZ=0
    g7: LineSegment StartX=-49.19 StartY=28.75 StartZ=0 EndX=-49.19 EndY=25.75 EndZ=0
    g8: LineSegment StartX=-49.19 StartY=23 StartZ=0 EndX=-49.19 EndY=20 EndZ=0
    g9: LineSegment StartX=-49.19 StartY=17.25 StartZ=0 EndX=-49.19 EndY=14.25 EndZ=0
    g10: LineSegment StartX=-49.19 StartY=11.5 StartZ=0 EndX=-49.19 EndY=8.5 EndZ=0
    g11: LineSegment StartX=-49.19 StartY=5.75 StartZ=0 EndX=-49.19 EndY=2.75 EndZ=0
    g12: ArcOfCircle CenterX=-1.5 CenterY=67.75 CenterZ=0 NormalX=0 NormalY=0 NormalZ=1 AngleXU=0 Radius=1.5 StartAngle=4.71239 EndAngle=7.85398
    g13: ArcOfCircle CenterX=-1.5 CenterY=62 CenterZ=0 NormalX=0 NormalY=0 NormalZ=1 AngleXU=0 Radius=1.5 StartAngle=4.71239 EndAngle=7.85398
    g14: ArcOfCircle CenterX=-1.5 CenterY=56.25 CenterZ=0 NormalX=0 NormalY=0 NormalZ=1 AngleXU=0 Radius=1.5 StartAngle=4.71239 EndAngle=7.85398
    g15: ArcOfCircle CenterX=-11.49 CenterY=50.5 CenterZ=0 NormalX=0 NormalY=0 NormalZ=1 AngleXU=0 Radius=1.5 StartAngle=4.71239 EndAngle=7.85398
    g16: ArcOfCircle CenterX=-16.28 CenterY=44.75 CenterZ=0 NormalX=0 NormalY=0 NormalZ=1 AngleXU=0 Radius=1.5 StartAngle=4.71239 EndAngle=7.85398
    g17: ArcOfCircle CenterX=-18.2337 CenterY=39 CenterZ=0 NormalX=0 NormalY=0 NormalZ=1 AngleXU=0 Radius=1.5 StartAngle=4.71485 EndAngle=7.85398
    g18: ArcOfCircle CenterX=-16.2837 CenterY=27.25 CenterZ=0 NormalX=0 NormalY=0 NormalZ=1 AngleXU=0 Radius=1.5 StartAngle=4.71485 EndAngle=7.85398
    g19: ArcOfCircle CenterX=-18.2337 CenterY=33 CenterZ=0 NormalX=0 NormalY=0 NormalZ=1 AngleXU=0 Radius=1.5 StartAngle=4.71485 EndAngle=7.85398
    g20: ArcOfCircle CenterX=-11.49 CenterY=21.5 CenterZ=0 NormalX=0 NormalY=0 NormalZ=1 AngleXU=0 Radius=1.5 StartAngle=4.71239 EndAngle=7.85398
    g21: ArcOfCircle CenterX=-1.5 CenterY=4.25 CenterZ=0 NormalX=0 NormalY=0 NormalZ=1 AngleXU=0 Radius=1.5 StartAngle=4.71239 EndAngle=7.85398
    g22: ArcOfCircle CenterX=-1.5 CenterY=10 CenterZ=0 NormalX=0 NormalY=0 NormalZ=1 AngleXU=0 Radius=1.5 StartAngle=4.71239 EndAngle=7.85398
    g23: ArcOfCircle CenterX=-1.5 CenterY=15.75 CenterZ=0 NormalX=0 NormalY=0 NormalZ=1 AngleXU=0 Radius=1.5 StartAngle=4.71239 EndAngle=7.85398
    g24: LineSegment StartX=-49.19 StartY=69.25 StartZ=0 EndX=-1.5 EndY=69.25 EndZ=0
    g25: LineSegment StartX=-49.19 StartY=66.25 StartZ=0 EndX=-1.5 EndY=66.25 EndZ=0
    g26: LineSegment StartX=-49.19 StartY=63.5 StartZ=0 EndX=-1.5 EndY=63.5 EndZ=0
    g27: LineSegment StartX=-49.19 StartY=60.5 StartZ=0 EndX=-1.5 EndY=60.5 EndZ=0
    g28: LineSegment StartX=-49.19 StartY=57.75 StartZ=0 EndX=-1.5 EndY=57.75 EndZ=0
    g29: LineSegment StartX=-49.19 StartY=54.75 StartZ=0 EndX=-1.5 EndY=54.75 EndZ=0
    g30: LineSegment StartX=-49.19 StartY=52 StartZ=0 EndX=-11.49 EndY=52 EndZ=0
    g31: LineSegment StartX=-49.19 StartY=49 StartZ=0 EndX=-11.49 EndY=49 EndZ=0
    g32: LineSegment StartX=-49.19 StartY=46.25 StartZ=0 EndX=-16.28 EndY=46.25 EndZ=0
    g33: LineSegment StartX=-49.19 StartY=43.25 StartZ=0 EndX=-16.28 EndY=43.25 EndZ=0
    g34: LineSegment StartX=-49.19 StartY=40.5 StartZ=0 EndX=-18.2337 EndY=40.5 EndZ=0
    g35: LineSegment StartX=-49.19 StartY=37.5 StartZ=0 EndX=-18.23 EndY=37.5 EndZ=0
    g36: LineSegment StartX=-49.19 StartY=34.5 StartZ=0 EndX=-18.2337 EndY=34.5 EndZ=0
    g37: LineSegment StartX=-49.19 StartY=31.5 StartZ=0 EndX=-18.23 EndY=31.5 EndZ=0
    g38: LineSegment StartX=-49.19 StartY=28.75 StartZ=0 EndX=-16.2837 EndY=28.75 EndZ=0
    g39: LineSegment StartX=-49.19 StartY=25.75 StartZ=0 EndX=-16.28 EndY=25.75 EndZ=0
    g40: LineSegment StartX=-49.19 StartY=23 StartZ=0 EndX=-11.49 EndY=23 EndZ=0
    g41: LineSegment StartX=-49.19 StartY=20 StartZ=0 EndX=-11.49 EndY=20 EndZ=0
    g42: LineSegment StartX=-49.19 StartY=17.25 StartZ=0 EndX=-1.5 EndY=17.25 EndZ=0
    g43: LineSegment StartX=-49.19 StartY=14.25 StartZ=0 EndX=-1.5 EndY=14.25 EndZ=0
    g44: LineSegment StartX=-49.19 StartY=11.5 StartZ=0 EndX=-1.5 EndY=11.5 EndZ=0
    g45: LineSegment StartX=-49.19 StartY=8.5 StartZ=0 EndX=-1.5 EndY=8.5 EndZ=0
    g46: LineSegment StartX=-49.19 StartY=5.75 StartZ=0 EndX=-1.5 EndY=5.75 EndZ=0
    g47: LineSegment StartX=-49.19 StartY=2.75 StartZ=0 EndX=-1.5 EndY=2.75 EndZ=0
  constraints (120):
    c: Vertical(g0)
    c: Distance(g0) = 3
    c: Block(g0)
    c: Vertical(g1)
    c: Distance(g1) = 3
    c: Vertical(g2)
    c: Equal(g0,g2) = 3
    c: Block(g2)
    c: Vertical(g3)
    c: Equal(g1,g3) = 3
    c: Vertical(g4)
    c: Equal(g0,g4) = 3
    c: Block(g4)
    c: Vertical(g5)
    c: Equal(g1,g5) = 3
    c: Vertical(g6)
    c: Equal(g0,g6) = 3
    c: Block(g6)
    c: Vertical(g7)
    c: Equal(g1,g7) = 3
    c: Vertical(g8)
    c: Equal(g0,g8) = 3
    c: Block(g8)
    c: Vertical(g9)
    c: Equal(g1,g9) = 3
    c: Vertical(g10)
    c: Equal(g0,g10) = 3
    c: Block(g10)
    c: Vertical(g11)
    c: Equal(g1,g11) = 3
    c: Block(g12)
    c: Block(g13)
    c: Block(g14)
    c: Block(g15)
    c: Block(g16)
    c: Block(g17)
    c: Block(g18)
    c: Block(g19)
    c: Block(g20)
    c: Block(g21)
    c: Block(g22)
    c: Block(g23)
    c: Block(g11)
    c: Block(g9)
    c: Block(g7)
    c: Block(g5)
    c: Block(g3)
    c: Block(g1)
    c: Coincident(g24,g0)
    c: Coincident(g24,g12)
    c: Horizontal(g24)
    c: Coincident(g25,g0)
    c: Coincident(g25,g12)
    c: Horizontal(g25)
    c: Coincident(g26,g1)
    c: Coincident(g26,g13)
    c: Horizontal(g26)
    c: Coincident(g27,g1)
    c: Coincident(g27,g13)
    c: Horizontal(g27)
    c: Coincident(g28,g2)
    c: Coincident(g28,g14)
    c: Horizontal(g28)
    c: Coincident(g29,g2)
    c: Coincident(g29,g14)
    c: Horizontal(g29)
    c: Coincident(g30,g3)
    c: Coincident(g30,g15)
    c: Horizontal(g30)
    c: Coincident(g31,g3)
    c: Coincident(g31,g15)
    c: Horizontal(g31)
    c: Coincident(g32,g4)
    c: Coincident(g32,g16)
    c: Horizontal(g32)
    c: Coincident(g33,g4)
    c: Coincident(g33,g16)
    c: Horizontal(g33)
    c: Coincident(g34,g5)
    c: Coincident(g34,g17)
    c: Horizontal(g34)
    c: Coincident(g35,g5)
    c: Coincident(g35,g17)
    c: Horizontal(g35)
    c: Coincident(g36,g6)
    c: Coincident(g36,g19)
    c: Horizontal(g36)
    c: Coincident(g37,g6)
    c: Coincident(g37,g19)
    c: Horizontal(g37)
    c: Coincident(g38,g7)
    c: Coincident(g38,g18)
    c: Horizontal(g38)
    c: Coincident(g39,g7)
    c: Coincident(g39,g18)
    c: Horizontal(g39)
    c: Coincident(g40,g8)
    c: Coincident(g40,g20)
    c: Horizontal(g40)
    c: Coincident(g41,g8)
    c: Coincident(g41,g20)
    c: Horizontal(g41)
    c: Coincident(g42,g9)
    c: Coincident(g42,g23)
    c: Horizontal(g42)
    c: Coincident(g43,g9)
    c: Coincident(g43,g23)
    c: Horizontal(g43)
    c: Coincident(g44,g10)
    c: Coincident(g44,g22)
    c: Horizontal(g44)
    c: Coincident(g45,g10)
    c: Coincident(g45,g22)
    c: Horizontal(g45)
    c: Coincident(g46,g11)
    c: Coincident(g46,g21)
    c: Horizontal(g46)
    c: Coincident(g47,g11)
    c: Coincident(g47,g21)
    c: Horizontal(g47)
FEATURE [Part::Extrusion] Extrude042
  Base = -> Sketch051
  Dir = (1,-2e-16,2e-16)
  DirMode = 2
  FaceMakerClass = Part::FaceMakerBullseye
  LengthFwd = 19
  LengthRev = 0
  Placement = pos=(-19,0,0) rot=(0,0,1;0rad)
  Solid = true
  Symmetric = false
FEATURE [Part::Fillet] Fillet035  label="removeToCreateVentalationHoles"
  Base = -> Extrude042
  Edges = <same value as first occurrence — deduplicated (x6 in doc)>
  Placement = pos=(7,0,0) rot=(0,0,1;0rad)
FEATURE [Part::Cut] Cut038  label="top017"
  Base = -> Cut033
  Tool = -> Fillet035
FEATURE [Sketcher::SketchObject] Sketch052  label="bottomSketch001"
  FullyConstrained = true
  sketch-geometry (45):
    g0: LineSegment StartX=6.29999 StartY=8 StartZ=0 EndX=3.29999 EndY=8 EndZ=0
    g1: LineSegment StartX=3.29999 StartY=8 StartZ=0 EndX=3.29999 EndY=-6.03275e-07 EndZ=0
    g2: ArcOfCircle CenterX=8.29999 CenterY=5 CenterZ=0 NormalX=0 NormalY=0 NormalZ=1 AngleXU=0 Radius=2 StartAngle=3.14159 EndAngle=4.71239
    g3: LineSegment StartX=6.29999 StartY=8 StartZ=0 EndX=6.29999 EndY=5 EndZ=0
    g4: ArcOfCircle CenterX=105 CenterY=19 CenterZ=0 NormalX=0 NormalY=0 NormalZ=1 AngleXU=0 Radius=12.7 StartAngle=4.71239 EndAngle=5.94289
    g5-g11: Circle x7 (B-spline internal-alignment scaffolding for g12; pole/knot coordinates omitted)
    g12: BSplineCurve PolesCount=7 KnotsCount=5 Degree=3 IsPeriodic=0
    g13-g17: GeomPoint x5 (B-spline internal-alignment scaffolding for g12; pole/knot coordinates omitted)
    g18: ArcOfCircle CenterX=105 CenterY=19 CenterZ=0 NormalX=0 NormalY=0 NormalZ=1 AngleXU=0 Radius=15.7 StartAngle=5.81226 EndAngle=6.28319
    g19: BSplineCurve PolesCount=5 KnotsCount=3 Degree=3 IsPeriodic=0
    g20: LineSegment StartX=8.29999 StartY=3 StartZ=0 EndX=101.7 EndY=3 EndZ=0
    g21: LineSegment StartX=3.29999 StartY=-6.03275e-07 StartZ=0 EndX=105 EndY=-6.03275e-07 EndZ=0
    g22: LineSegment StartX=120.974 StartY=8.71251 StartZ=0 EndX=122.332 EndY=7.83778 EndZ=0
    g23: LineSegment StartX=105 StartY=-6.03274e-07 StartZ=0 EndX=113 EndY=-6.03274e-07 EndZ=0
    g24: ArcOfCircle CenterX=105 CenterY=19 CenterZ=0 NormalX=0 NormalY=0 NormalZ=1 AngleXU=0 Radius=20.6155 StartAngle=5.11091 EndAngle=5.71103
    g25: ArcOfCircle CenterX=117.7 CenterY=19 CenterZ=0 NormalX=0 NormalY=0 NormalZ=1 AngleXU=0 Radius=3 StartAngle=1.2e-15 EndAngle=2.10468
    g26: Circle CenterX=116.345 CenterY=16.3232 CenterZ=0 NormalX=0 NormalY=0 NormalZ=1 AngleXU=0 Radius=1
    g27: Circle CenterX=117.24 CenterY=15.7584 CenterZ=0 NormalX=0 NormalY=0 NormalZ=1 AngleXU=0 Radius=1
    g28: Circle CenterX=116.972 CenterY=14.7612 CenterZ=0 NormalX=0 NormalY=0 NormalZ=1 AngleXU=0 Radius=1
    g29: BSplineCurve PolesCount=3 KnotsCount=2 Degree=2 IsPeriodic=0
    g30: GeomPoint X=116.345 Y=16.3232 Z=0
    g31: GeomPoint X=116.972 Y=14.7612 Z=0
    g32: Circle CenterX=115.828 CenterY=17.157 CenterZ=0 NormalX=0 NormalY=0 NormalZ=1 AngleXU=0 Radius=1
    g33: Circle CenterX=115.841 CenterY=16.639 CenterZ=0 NormalX=0 NormalY=0 NormalZ=1 AngleXU=0 Radius=1
    g34: Circle CenterX=116.345 CenterY=16.3232 CenterZ=0 NormalX=0 NormalY=0 NormalZ=1 AngleXU=0 Radius=1
    g35: BSplineCurve PolesCount=3 KnotsCount=2 Degree=2 IsPeriodic=0
    g36: GeomPoint X=115.828 Y=17.157 Z=0
    g37: GeomPoint X=116.345 Y=16.3232 Z=0
    g38: LineSegment StartX=115.828 StartY=17.157 StartZ=0 EndX=115.828 EndY=20.8307 EndZ=0
    g39: Circle CenterX=115.828 CenterY=20.8307 CenterZ=0 NormalX=0 NormalY=0 NormalZ=1 AngleXU=0 Radius=1
    g40: Circle CenterX=115.831 CenterY=21.3396 CenterZ=0 NormalX=0 NormalY=0 NormalZ=1 AngleXU=0 Radius=1
    g41: Circle CenterX=116.173 CenterY=21.5825 CenterZ=0 NormalX=0 NormalY=0 NormalZ=1 AngleXU=0 Radius=1
    g42: BSplineCurve PolesCount=3 KnotsCount=2 Degree=2 IsPeriodic=0
    g43: GeomPoint X=115.828 Y=20.8307 Z=0
    g44: GeomPoint X=116.173 Y=21.5825 Z=0
  constraints (70):
    c: Horizontal(g0)
    c: Distance(g0) = 3
    c: Coincident(g1,g0)
    c: Vertical(g1)
    c: Block(g2)
    c: Block(g0)
    c: Coincident(g3,g0)
    c: Coincident(g3,g2)
    c: Vertical(g3)
    c: Block(g1)
    c: Block(g4)
    c: Coincident(g19,g4)
    c: Block(g19)
    c: Equal(g5, g6-g11) x6
    c: InternalAlignment(g5-g11 -> g12) x7
    c: InternalAlignment(g13-g17 -> g12) x5
    c: Block(g12)
    c: Coincident(g18,g12)
    c: Block(g18)
    c: Coincident(g20,g2)
    c: Coincident(g20,g19)
    c: Horizontal(g20)
    c: Distance(g20) = 93.4
    c: Coincident(g21,g1)
    c: Horizontal(g21)
    c: Distance(g21) = 101.7
    c: Horizontal(g23)
    c: Distance(g23) = 8
    c: Coincident(g24,g23)
    c: Block(g23)
    c: Coincident(g22,g24)
    c: Block(g24)
    c: Block(g22)
    c: Distance(g22) = 1.61553
    c: Coincident(g25,g18)
    c: Block(g25)
    c: Weight(g26) = 1
    c: Equal(g26,g27)
    c: Equal(g26,g28)
    c: Coincident(g29,g4)
    c: InternalAlignment(g26,g29)
    c: InternalAlignment(g27,g29)
    c: InternalAlignment(g28,g29)
    c: InternalAlignment(g30,g29)
    c: InternalAlignment(g31,g29)
    c: Block(g29)
    c: Weight(g32) = 1
    c: Equal(g32,g33)
    c: Equal(g32,g34)
    c: Coincident(g35,g29)
    c: InternalAlignment(g32,g35)
    c: InternalAlignment(g33,g35)
    c: InternalAlignment(g34,g35)
    c: InternalAlignment(g36,g35)
    c: InternalAlignment(g37,g35)
    c: Block(g35)
    c: Coincident(g38,g35)
    c: Vertical(g38)
    c: Block(g38)
    c: Coincident(g42,g38)
    c: Weight(g39) = 1
    c: Equal(g39,g40)
    c: Equal(g39,g41)
    c: Coincident(g42,g25)
    c: InternalAlignment(g39,g42)
    c: InternalAlignment(g40,g42)
    c: InternalAlignment(g41,g42)
    c: InternalAlignment(g43,g42)
    c: InternalAlignment(g44,g42)
    c: Block(g42)
FEATURE [Part::Extrusion] Extrude043  label="bottom010"
  Base = -> Sketch052
  Dir = (0,0,1)
  DirMode = 2
  FaceMakerClass = Part::FaceMakerBullseye
  LengthFwd = 71.4
  LengthRev = 0
  Placement = pos=(0,0,0.3) rot=(0,0,1;0rad)
  Solid = true
  Symmetric = false
FEATURE [Sketcher::SketchObject] Sketch053  label="topSketch013"
  FullyConstrained = true
  sketch-geometry (22):
    g0: LineSegment StartX=5.21097e-06 StartY=3 StartZ=0 EndX=5.21097e-06 EndY=19 EndZ=0
    g1: ArcOfCircle CenterX=19 CenterY=19 CenterZ=0 NormalX=0 NormalY=0 NormalZ=1 AngleXU=0 Radius=19 StartAngle=1.5708 EndAngle=3.14159
    g2: ArcOfCircle CenterX=19 CenterY=19 CenterZ=0 NormalX=0 NormalY=0 NormalZ=1 AngleXU=0 Radius=16 StartAngle=1.5708 EndAngle=3.14159
    g3: LineSegment StartX=114 StartY=35 StartZ=0 EndX=19 EndY=35 EndZ=0
    g4: LineSegment StartX=5.21097e-06 StartY=3 StartZ=0 EndX=5.21097e-06 EndY=0 EndZ=0
    g5: LineSegment StartX=3 StartY=0 StartZ=0 EndX=5.21097e-06 EndY=0 EndZ=0
    g6: LineSegment StartX=3 StartY=19 StartZ=0 EndX=3 EndY=0 EndZ=0
    g7: LineSegment StartX=19 StartY=38 StartZ=0 EndX=124 EndY=38 EndZ=0
    g8: Circle CenterX=119 CenterY=35 CenterZ=0 NormalX=0 NormalY=0 NormalZ=1 AngleXU=0 Radius=1
    g9: Circle CenterX=121 CenterY=35 CenterZ=0 NormalX=0 NormalY=0 NormalZ=1 AngleXU=0 Radius=1
    g10: Circle CenterX=121 CenterY=33 CenterZ=0 NormalX=0 NormalY=0 NormalZ=1 AngleXU=0 Radius=1
    g11: BSplineCurve PolesCount=3 KnotsCount=2 Degree=2 IsPeriodic=0
    g12: GeomPoint X=119 Y=35 Z=0
    g13: GeomPoint X=121 Y=33 Z=0
    g14: LineSegment StartX=119 StartY=35 StartZ=0 EndX=114 EndY=35 EndZ=0
    g15: ArcOfCircle CenterX=105 CenterY=19 CenterZ=0 NormalX=0 NormalY=0 NormalZ=1 AngleXU=0 Radius=16 StartAngle=5.60905 EndAngle=6.28319
    g16: LineSegment StartX=121 StartY=33 StartZ=0 EndX=121 EndY=19 EndZ=0
    g17: LineSegment StartX=117.5 StartY=9.01251 StartZ=0 EndX=121.163 EndY=9.0125 EndZ=0
    g18: ArcOfCircle CenterX=105 CenterY=19 CenterZ=0 NormalX=0 NormalY=0 NormalZ=1 AngleXU=0 Radius=20.6155 StartAngle=5.7297 EndAngle=6.28319
    g19: LineSegment StartX=121.163 StartY=9.0125 StartZ=0 EndX=122.538 EndY=8.16329 EndZ=0
    g20: LineSegment StartX=124 StartY=38 StartZ=0 EndX=125.616 EndY=38 EndZ=0
    g21: LineSegment StartX=125.616 StartY=19 StartZ=0 EndX=125.616 EndY=38 EndZ=0
  constraints (50):
    c: Vertical(g0)
    c: Block(g0)
    c: Coincident(g1,g0)
    c: Block(g1)
    c: Coincident(g2,g1)
    c: Block(g2)
    c: Coincident(g3,g2)
    c: Horizontal(g3)
    c: Tangent(g3,g2)
    c: Coincident(g4,g0)
    c: Distance(g4) = 3
    c: Vertical(g4)
    c: Coincident(g5,g4)
    c: Horizontal(g5)
    c: Coincident(g6,g2)
    c: Coincident(g6,g5)
    c: Vertical(g6)
    c: Horizontal(g7)
    c: Distance(g7) = 105
    c: Coincident(g7,g1)
    c: Block(g3)
    c: Weight(g8) = 1
    c: Equal(g8,g9)
    c: Equal(g8,g10)
    c: InternalAlignment(g8,g11)
    c: InternalAlignment(g9,g11)
    c: InternalAlignment(g10,g11)
    c: InternalAlignment(g12,g11)
    c: InternalAlignment(g13,g11)
    c: Block(g11)
    c: Coincident(g14,g11)
    c: Coincident(g14,g3)
    c: Horizontal(g14)
    c: Block(g15)
    c: Coincident(g16,g11)
    c: Coincident(g16,g15)
    c: Vertical(g16)
    c: Distance(g16) = 14
    c: Coincident(g17,g15)
    c: Block(g18)
    c: Coincident(g19,g18)
    c: Coincident(g20,g7)
    c: Horizontal(g20)
    c: Vertical(g21)
    c: Coincident(g20,g21)
    c: Block(g20)
    c: Block(g21)
    c: Block(g19)
    c: Block(g17)
    c: Distance(g20) = 1.61553
FEATURE [Part::Extrusion] Extrude044
  Base = -> Sketch053
  Dir = (0,0,1)
  DirMode = 2
  FaceMakerClass = Part::FaceMakerBullseye
  LengthFwd = 72
  LengthRev = 0
  Solid = true
  Symmetric = false
FEATURE [Part::Fillet] Fillet036  label="top018"
  Base = -> Extrude044
  Edges = 1 edges r=2: [Edge41]
FEATURE [Sketcher::SketchObject] Sketch054
  FullyConstrained = false
  Placement = pos=(0,0,0) rot=(1,0,0;1.5708rad)
  sketch-geometry (24):
    g0: ArcOfCircle CenterX=-4 CenterY=-10.5 CenterZ=0 NormalX=0 NormalY=0 NormalZ=1 AngleXU=0 Radius=1.5 StartAngle=6e-16 EndAngle=3.14159
    g1: ArcOfCircle CenterX=-34.2 CenterY=-10.5 CenterZ=0 NormalX=0 NormalY=0 NormalZ=1 AngleXU=0 Radius=1.5 StartAngle=0 EndAngle=3.14159
    g2: ArcOfCircle CenterX=-34.2 CenterY=-27.7 CenterZ=0 NormalX=0 NormalY=0 NormalZ=1 AngleXU=0 Radius=1.5 StartAngle=3.14159 EndAngle=6.28319
    g3: ArcOfCircle CenterX=-4 CenterY=-27.7 CenterZ=0 NormalX=0 NormalY=0 NormalZ=1 AngleXU=0 Radius=1.5 StartAngle=3.1416 EndAngle=6.28319
    g4: ArcOfCircle CenterX=-10 CenterY=-4.3 CenterZ=0 NormalX=0 NormalY=0 NormalZ=1 AngleXU=0 Radius=1.5 StartAngle=2e-16 EndAngle=3.14159
    g5: ArcOfCircle CenterX=-16.1 CenterY=-1.8 CenterZ=0 NormalX=0 NormalY=0 NormalZ=1 AngleXU=0 Radius=1.5 StartAngle=5e-16 EndAngle=3.14159
    g6: ArcOfCircle CenterX=-22.1 CenterY=-1.8 CenterZ=0 NormalX=0 NormalY=0 NormalZ=1 AngleXU=0 Radius=1.5 StartAngle=5e-16 EndAngle=3.14159
    g7: ArcOfCircle CenterX=-28.2 CenterY=-4.3 CenterZ=0 NormalX=0 NormalY=0 NormalZ=1 AngleXU=0 Radius=1.5 StartAngle=2e-16 EndAngle=3.14159
    g8: ArcOfCircle CenterX=-10 CenterY=-33.9 CenterZ=0 NormalX=0 NormalY=0 NormalZ=1 AngleXU=0 Radius=1.5 StartAngle=3.14159 EndAngle=6.28319
    g9: ArcOfCircle CenterX=-16.1 CenterY=-36.4 CenterZ=0 NormalX=0 NormalY=0 NormalZ=1 AngleXU=0 Radius=1.5 StartAngle=3.14159 EndAngle=6.28319
    g10: ArcOfCircle CenterX=-22.1 CenterY=-36.4 CenterZ=0 NormalX=0 NormalY=0 NormalZ=1 AngleXU=0 Radius=1.5 StartAngle=3.14159 EndAngle=6.28319
    g11: ArcOfCircle CenterX=-28.2 CenterY=-33.9 CenterZ=0 NormalX=0 NormalY=0 NormalZ=1 AngleXU=0 Radius=1.5 StartAngle=3.14159 EndAngle=6.28319
    g12: LineSegment StartX=-35.7 StartY=-10.5 StartZ=0 EndX=-35.7 EndY=-27.7 EndZ=0
    g13: LineSegment StartX=-32.7 StartY=-10.5 StartZ=0 EndX=-32.7 EndY=-27.7 EndZ=0
    g14: LineSegment StartX=-29.7 StartY=-33.9 StartZ=0 EndX=-29.7 EndY=-4.3 EndZ=0
    g15: LineSegment StartX=-26.7 StartY=-33.9 StartZ=0 EndX=-26.7 EndY=-4.3 EndZ=0
    g16: LineSegment StartX=-2.5 StartY=-10.5 StartZ=0 EndX=-2.5 EndY=-27.7 EndZ=0
    g17: LineSegment StartX=-8.5 StartY=-4.3 StartZ=0 EndX=-8.5 EndY=-33.9 EndZ=0
    g18: LineSegment StartX=-5.5 StartY=-10.5 StartZ=0 EndX=-5.5 EndY=-27.7 EndZ=0
    g19: LineSegment StartX=-11.5 StartY=-4.3 StartZ=0 EndX=-11.5 EndY=-33.9 EndZ=0
    g20: LineSegment StartX=-14.6 StartY=-1.8 StartZ=0 EndX=-14.6 EndY=-36.4 EndZ=0
    g21: LineSegment StartX=-17.6 StartY=-1.8 StartZ=0 EndX=-17.6 EndY=-36.4 EndZ=0
    g22: LineSegment StartX=-20.6 StartY=-36.4 StartZ=0 EndX=-20.6 EndY=-1.8 EndZ=0
    g23: LineSegment StartX=-23.6 StartY=-1.8 StartZ=0 EndX=-23.6 EndY=-36.4 EndZ=0
  constraints (48):
    c: Block(g0)
    c: Block(g1)
    c: Block(g2)
    c: Block(g3)
    c: Block(g4)
    c: Block(g5)
    c: Block(g6)
    c: Block(g7)
    c: Block(g8)
    c: Block(g9)
    c: Block(g10)
    c: Block(g11)
    c: Coincident(g12,g1)
    c: Coincident(g12,g2)
    c: Vertical(g12)
    c: Coincident(g13,g1)
    c: Coincident(g13,g2)
    c: Vertical(g13)
    c: Coincident(g14,g11)
    c: Coincident(g14,g7)
    c: Vertical(g14)
    c: Coincident(g15,g11)
    c: Coincident(g15,g7)
    c: Vertical(g15)
    c: Coincident(g16,g0)
    c: Coincident(g16,g3)
    c: Vertical(g16)
    c: Coincident(g17,g4)
    c: Coincident(g17,g8)
    c: Vertical(g17)
    c: Coincident(g18,g0)
    c: Coincident(g18,g3)
    c: Vertical(g18)
    c: Coincident(g19,g4)
    c: Coincident(g19,g8)
    c: Vertical(g19)
    c: Coincident(g20,g5)
    c: Coincident(g20,g9)
    c: Vertical(g20)
    c: Coincident(g21,g5)
    c: Coincident(g21,g9)
    c: Vertical(g21)
    c: Coincident(g22,g10)
    c: Coincident(g22,g6)
    c: Vertical(g22)
    c: Coincident(g23,g6)
    c: Coincident(g23,g10)
    c: Vertical(g23)
FEATURE [Part::Extrusion] Extrude045  label="removeToCreateFanGrillHoles003"
  Base = -> Sketch054
  Dir = (0,-1,6e-16)
  DirMode = 2
  FaceMakerClass = Part::FaceMakerBullseye
  LengthFwd = 10
  LengthRev = 0
  Placement = pos=(65.4,44,54.82) rot=(0,0,1;0rad)
  Solid = true
  Symmetric = false
FEATURE [Part::Feature] Face105 .. Face108  x4 (patterned run collapsed; names and placements below)
  shape: bbox 3.5 x 17.8 x 2e-07 mm, 1 faces, 0 solids (baked)
FEATURE [Part::Revolution] Revolve113  label="removeToCreateScrewAndThreadedInsertHole041"
  Angle = 360
  Axis = (0,1,0)
  Base = (0,0,0)
  FaceMakerClass = Part::FaceMakerBullseye
  Placement = pos=(62.3,30.3,19.7) rot=(0,0,1;0rad)
  Solid = false
  Source = -> Face105
  Symmetric = false
FEATURE [Part::Revolution] Revolve114  label="removeToCreateScrewAndThreadedInsertHole042"
  Angle = 360
  Axis = (0,1,0)
  Base = (0,0,0)
  FaceMakerClass = Part::FaceMakerBullseye
  Placement = pos=(62.3,30.3,51.7) rot=(0,0,1;0rad)
  Solid = false
  Source = -> Face106
  Symmetric = false
FEATURE [Part::Revolution] Revolve115  label="removeToCreateScrewAndThreadedInsertHole043"
  Angle = 360
  Axis = (0,1,0)
  Base = (0,0,0)
  FaceMakerClass = Part::FaceMakerBullseye
  Placement = pos=(30.3,30.3,19.7) rot=(0,0,1;0rad)
  Solid = false
  Source = -> Face107
  Symmetric = false
FEATURE [Part::Revolution] Revolve116  label="removeToCreateScrewAndThreadedInsertHole044"
  Angle = 360
  Axis = (0,1,0)
  Base = (0,0,0)
  FaceMakerClass = Part::FaceMakerBullseye
  Placement = pos=(30.3,30.3,51.7) rot=(0,0,1;0rad)
  Solid = false
  Source = -> Face108
  Symmetric = false
FEATURE [Part::MultiFuse] Fusion083  label="createThreadedInsertHolesForFan004"
  Shapes = -> [Revolve113,Revolve114,Revolve115,Revolve116]
FEATURE [Part::Box] Box024  label="removeToCreteHoleForPlugHousing026"
  AttacherType = Attacher::AttachEngine3D
  Height = 28.6
  Length = 10
  Placement = pos=(-2,0,21.7) rot=(0,0,1;0rad)
  Width = 19
FEATURE [Part::Cylinder] Cylinder038  label="removeToCreteHoleForPlugHousing027"
  Angle = 360
  AttacherType = Attacher::AttachEngine3D
  Height = 20
  Placement = pos=(-2,19,36) rot=(0,1,0;1.5708rad)
  Radius = 14.3
FEATURE [Part::MultiFuse] Fusion084  label="removeToCreteHoleForPlugHousing028"
  Shapes = -> [Box024,Cylinder038]
FEATURE [Part::Cylinder] Cylinder039
  Angle = 360
  AttacherType = Attacher::AttachEngine3D
  Height = 20
  Placement = pos=(0,0,36.15) rot=(0,0,1;0rad)
  Radius = 14.3
FEATURE [Part::Cylinder] Cylinder040
  Angle = 360
  AttacherType = Attacher::AttachEngine3D
  Height = 10
  Placement = pos=(0,0,36.15) rot=(0,0,1;0rad)
  Radius = 4
FEATURE [Part::Box] Box025  label="removeToCreteHoleForPlugHousing030"
  AttacherType = Attacher::AttachEngine3D
  Height = 28.6
  Length = 20
  Placement = pos=(106.15,0,21.7) rot=(0,0,1;0rad)
  Width = 19
FEATURE [Part::MultiFuse] Fusion086  label="removeToCreteHoleForPlugHousing031"
  Placement = pos=(70,19,36) rot=(0,1,0;1.5708rad)
  Shapes = -> [Cylinder039,Cylinder040]
FEATURE [Part::MultiFuse] Fusion085  label="removeToCreteHoleForPlugHousing029"
  Shapes = -> [Box025,Fusion086]
FEATURE [Sketcher::SketchObject] Sketch055
  FullyConstrained = true
  Placement = pos=(117,19,0) rot=(0.57735,0.57735,0.57735;2.0944rad)
  sketch-geometry (48):
    g0: LineSegment StartX=-49.19 StartY=69.25 StartZ=0 EndX=-49.19 EndY=66.25 EndZ=0
    g1: LineSegment StartX=-49.19 StartY=63.5 StartZ=0 EndX=-49.19 EndY=60.5 EndZ=0
    g2: LineSegment StartX=-49.19 StartY=57.75 StartZ=0 EndX=-49.19 EndY=54.75 EndZ=0
    g3: LineSegment StartX=-49.19 StartY=52 StartZ=0 EndX=-49.19 EndY=49 EndZ=0
    g4: LineSegment StartX=-49.19 StartY=46.25 StartZ=0 EndX=-49.19 EndY=43.25 EndZ=0
    g5: LineSegment StartX=-49.19 StartY=40.5 StartZ=0 EndX=-49.19 EndY=37.5 EndZ=0
    g6: LineSegment StartX=-49.19 StartY=34.5 StartZ=0 EndX=-49.19 EndY=31.5 EndZ=0
    g7: LineSegment StartX=-49.19 StartY=28.75 StartZ=0 EndX=-49.19 EndY=25.75 EndZ=0
    g8: LineSegment StartX=-49.19 StartY=23 StartZ=0 EndX=-49.19 EndY=20 EndZ=0
    g9: LineSegment StartX=-49.19 StartY=17.25 StartZ=0 EndX=-49.19 EndY=14.25 EndZ=0
    g10: LineSegment StartX=-49.19 StartY=11.5 StartZ=0 EndX=-49.19 EndY=8.5 EndZ=0
    g11: LineSegment StartX=-49.19 StartY=5.75 StartZ=0 EndX=-49.19 EndY=2.75 EndZ=0
    g12: ArcOfCircle CenterX=-1.5 CenterY=67.75 CenterZ=0 NormalX=0 NormalY=0 NormalZ=1 AngleXU=0 Radius=1.5 StartAngle=4.71239 EndAngle=7.85398
    g13: ArcOfCircle CenterX=-1.5 CenterY=62 CenterZ=0 NormalX=0 NormalY=0 NormalZ=1 AngleXU=0 Radius=1.5 StartAngle=4.71239 EndAngle=7.85398
    g14: ArcOfCircle CenterX=-1.5 CenterY=56.25 CenterZ=0 NormalX=0 NormalY=0 NormalZ=1 AngleXU=0 Radius=1.5 StartAngle=4.71239 EndAngle=7.85398
    g15: ArcOfCircle CenterX=-11.49 CenterY=50.5 CenterZ=0 NormalX=0 NormalY=0 NormalZ=1 AngleXU=0 Radius=1.5 StartAngle=4.71239 EndAngle=7.85398
    g16: ArcOfCircle CenterX=-16.28 CenterY=44.75 CenterZ=0 NormalX=0 NormalY=0 NormalZ=1 AngleXU=0 Radius=1.5 StartAngle=4.71239 EndAngle=7.85398
    g17: ArcOfCircle CenterX=-18.2337 CenterY=39 CenterZ=0 NormalX=0 NormalY=0 NormalZ=1 AngleXU=0 Radius=1.5 StartAngle=4.71485 EndAngle=7.85398
    g18: ArcOfCircle CenterX=-16.2837 CenterY=27.25 CenterZ=0 NormalX=0 NormalY=0 NormalZ=1 AngleXU=0 Radius=1.5 StartAngle=4.71485 EndAngle=7.85398
    g19: ArcOfCircle CenterX=-18.2337 CenterY=33 CenterZ=0 NormalX=0 NormalY=0 NormalZ=1 AngleXU=0 Radius=1.5 StartAngle=4.71485 EndAngle=7.85398
    g20: ArcOfCircle CenterX=-11.49 CenterY=21.5 CenterZ=0 NormalX=0 NormalY=0 NormalZ=1 AngleXU=0 Radius=1.5 StartAngle=4.71239 EndAngle=7.85398
    g21: ArcOfCircle CenterX=-1.5 CenterY=4.25 CenterZ=0 NormalX=0 NormalY=0 NormalZ=1 AngleXU=0 Radius=1.5 StartAngle=4.71239 EndAngle=7.85398
    g22: ArcOfCircle CenterX=-1.5 CenterY=10 CenterZ=0 NormalX=0 NormalY=0 NormalZ=1 AngleXU=0 Radius=1.5 StartAngle=4.71239 EndAngle=7.85398
    g23: ArcOfCircle CenterX=-1.5 CenterY=15.75 CenterZ=0 NormalX=0 NormalY=0 NormalZ=1 AngleXU=0 Radius=1.5 StartAngle=4.71239 EndAngle=7.85398
    g24: LineSegment StartX=-49.19 StartY=69.25 StartZ=0 EndX=-1.5 EndY=69.25 EndZ=0
    g25: LineSegment StartX=-49.19 StartY=66.25 StartZ=0 EndX=-1.5 EndY=66.25 EndZ=0
    g26: LineSegment StartX=-49.19 StartY=63.5 StartZ=0 EndX=-1.5 EndY=63.5 EndZ=0
    g27: LineSegment StartX=-49.19 StartY=60.5 StartZ=0 EndX=-1.5 EndY=60.5 EndZ=0
    g28: LineSegment StartX=-49.19 StartY=57.75 StartZ=0 EndX=-1.5 EndY=57.75 EndZ=0
    g29: LineSegment StartX=-49.19 StartY=54.75 StartZ=0 EndX=-1.5 EndY=54.75 EndZ=0
    g30: LineSegment StartX=-49.19 StartY=52 StartZ=0 EndX=-11.49 EndY=52 EndZ=0
    g31: LineSegment StartX=-49.19 StartY=49 StartZ=0 EndX=-11.49 EndY=49 EndZ=0
    g32: LineSegment StartX=-49.19 StartY=46.25 StartZ=0 EndX=-16.28 EndY=46.25 EndZ=0
    g33: LineSegment StartX=-49.19 StartY=43.25 StartZ=0 EndX=-16.28 EndY=43.25 EndZ=0
    g34: LineSegment StartX=-49.19 StartY=40.5 StartZ=0 EndX=-18.2337 EndY=40.5 EndZ=0
    g35: LineSegment StartX=-49.19 StartY=37.5 StartZ=0 EndX=-18.23 EndY=37.5 EndZ=0
    g36: LineSegment StartX=-49.19 StartY=34.5 StartZ=0 EndX=-18.2337 EndY=34.5 EndZ=0
    g37: LineSegment StartX=-49.19 StartY=31.5 StartZ=0 EndX=-18.23 EndY=31.5 EndZ=0
    g38: LineSegment StartX=-49.19 StartY=28.75 StartZ=0 EndX=-16.2837 EndY=28.75 EndZ=0
    g39: LineSegment StartX=-49.19 StartY=25.75 StartZ=0 EndX=-16.28 EndY=25.75 EndZ=0
    g40: LineSegment StartX=-49.19 StartY=23 StartZ=0 EndX=-11.49 EndY=23 EndZ=0
    g41: LineSegment StartX=-49.19 StartY=20 StartZ=0 EndX=-11.49 EndY=20 EndZ=0
    g42: LineSegment StartX=-49.19 StartY=17.25 StartZ=0 EndX=-1.5 EndY=17.25 EndZ=0
    g43: LineSegment StartX=-49.19 StartY=14.25 StartZ=0 EndX=-1.5 EndY=14.25 EndZ=0
    g44: LineSegment StartX=-49.19 StartY=11.5 StartZ=0 EndX=-1.5 EndY=11.5 EndZ=0
    g45: LineSegment StartX=-49.19 StartY=8.5 StartZ=0 EndX=-1.5 EndY=8.5 EndZ=0
    g46: LineSegment StartX=-49.19 StartY=5.75 StartZ=0 EndX=-1.5 EndY=5.75 EndZ=0
    g47: LineSegment StartX=-49.19 StartY=2.75 StartZ=0 EndX=-1.5 EndY=2.75 EndZ=0
  constraints (120):
    c: Vertical(g0)
    c: Distance(g0) = 3
    c: Block(g0)
    c: Vertical(g1)
    c: Distance(g1) = 3
    c: Vertical(g2)
    c: Equal(g0,g2) = 3
    c: Block(g2)
    c: Vertical(g3)
    c: Equal(g1,g3) = 3
    c: Vertical(g4)
    c: Equal(g0,g4) = 3
    c: Block(g4)
    c: Vertical(g5)
    c: Equal(g1,g5) = 3
    c: Vertical(g6)
    c: Equal(g0,g6) = 3
    c: Block(g6)
    c: Vertical(g7)
    c: Equal(g1,g7) = 3
    c: Vertical(g8)
    c: Equal(g0,g8) = 3
    c: Block(g8)
    c: Vertical(g9)
    c: Equal(g1,g9) = 3
    c: Vertical(g10)
    c: Equal(g0,g10) = 3
    c: Block(g10)
    c: Vertical(g11)
    c: Equal(g1,g11) = 3
    c: Block(g12)
    c: Block(g13)
    c: Block(g14)
    c: Block(g15)
    c: Block(g16)
    c: Block(g17)
    c: Block(g18)
    c: Block(g19)
    c: Block(g20)
    c: Block(g21)
    c: Block(g22)
    c: Block(g23)
    c: Block(g11)
    c: Block(g9)
    c: Block(g7)
    c: Block(g5)
    c: Block(g3)
    c: Block(g1)
    c: Coincident(g24,g0)
    c: Coincident(g24,g12)
    c: Horizontal(g24)
    c: Coincident(g25,g0)
    c: Coincident(g25,g12)
    c: Horizontal(g25)
    c: Coincident(g26,g1)
    c: Coincident(g26,g13)
    c: Horizontal(g26)
    c: Coincident(g27,g1)
    c: Coincident(g27,g13)
    c: Horizontal(g27)
    c: Coincident(g28,g2)
    c: Coincident(g28,g14)
    c: Horizontal(g28)
    c: Coincident(g29,g2)
    c: Coincident(g29,g14)
    c: Horizontal(g29)
    c: Coincident(g30,g3)
    c: Coincident(g30,g15)
    c: Horizontal(g30)
    c: Coincident(g31,g3)
    c: Coincident(g31,g15)
    c: Horizontal(g31)
    c: Coincident(g32,g4)
    c: Coincident(g32,g16)
    c: Horizontal(g32)
    c: Coincident(g33,g4)
    c: Coincident(g33,g16)
    c: Horizontal(g33)
    c: Coincident(g34,g5)
    c: Coincident(g34,g17)
    c: Horizontal(g34)
    c: Coincident(g35,g5)
    c: Coincident(g35,g17)
    c: Horizontal(g35)
    c: Coincident(g36,g6)
    c: Coincident(g36,g19)
    c: Horizontal(g36)
    c: Coincident(g37,g6)
    c: Coincident(g37,g19)
    c: Horizontal(g37)
    c: Coincident(g38,g7)
    c: Coincident(g38,g18)
    c: Horizontal(g38)
    c: Coincident(g39,g7)
    c: Coincident(g39,g18)
    c: Horizontal(g39)
    c: Coincident(g40,g8)
    c: Coincident(g40,g20)
    c: Horizontal(g40)
    c: Coincident(g41,g8)
    c: Coincident(g41,g20)
    c: Horizontal(g41)
    c: Coincident(g42,g9)
    c: Coincident(g42,g23)
    c: Horizontal(g42)
    c: Coincident(g43,g9)
    c: Coincident(g43,g23)
    c: Horizontal(g43)
    c: Coincident(g44,g10)
    c: Coincident(g44,g22)
    c: Horizontal(g44)
    c: Coincident(g45,g10)
    c: Coincident(g45,g22)
    c: Horizontal(g45)
    c: Coincident(g46,g11)
    c: Coincident(g46,g21)
    c: Horizontal(g46)
    c: Coincident(g47,g11)
    c: Coincident(g47,g21)
    c: Horizontal(g47)
FEATURE [Part::Extrusion] Extrude046
  Base = -> Sketch055
  Dir = (1,0,0)
  DirMode = 2
  FaceMakerClass = Part::FaceMakerBullseye
  LengthFwd = 23
  LengthRev = 0
  Placement = pos=(-19,0,0) rot=(0,0,1;0rad)
  Solid = true
  Symmetric = false
FEATURE [Part::Fillet] Fillet038  label="removeToCreateVentalationHoles001"
  Base = -> Extrude046
  Edges = <same value as first occurrence — deduplicated (x6 in doc)>
  Placement = pos=(7,0,0) rot=(0,0,1;0rad)
FEATURE [Sketcher::SketchObject] Sketch056  label="topSketch014"
  FullyConstrained = true
  sketch-geometry (22):
    g0: LineSegment StartX=5.21097e-06 StartY=3 StartZ=0 EndX=5.21097e-06 EndY=19 EndZ=0
    g1: ArcOfCircle CenterX=19 CenterY=19 CenterZ=0 NormalX=0 NormalY=0 NormalZ=1 AngleXU=0 Radius=19 StartAngle=1.5708 EndAngle=3.14159
    g2: ArcOfCircle CenterX=19 CenterY=19 CenterZ=0 NormalX=0 NormalY=0 NormalZ=1 AngleXU=0 Radius=16 StartAngle=1.5708 EndAngle=3.14159
    g3: LineSegment StartX=114 StartY=35 StartZ=0 EndX=19 EndY=35 EndZ=0
    g4: LineSegment StartX=5.21097e-06 StartY=3 StartZ=0 EndX=5.21097e-06 EndY=0 EndZ=0
    g5: LineSegment StartX=3 StartY=0 StartZ=0 EndX=5.21097e-06 EndY=0 EndZ=0
    g6: LineSegment StartX=3 StartY=19 StartZ=0 EndX=3 EndY=0 EndZ=0
    g7: LineSegment StartX=19 StartY=38 StartZ=0 EndX=124 EndY=38 EndZ=0
    g8: Circle CenterX=119 CenterY=35 CenterZ=0 NormalX=0 NormalY=0 NormalZ=1 AngleXU=0 Radius=1
    g9: Circle CenterX=121 CenterY=35 CenterZ=0 NormalX=0 NormalY=0 NormalZ=1 AngleXU=0 Radius=1
    g10: Circle CenterX=121 CenterY=33 CenterZ=0 NormalX=0 NormalY=0 NormalZ=1 AngleXU=0 Radius=1
    g11: BSplineCurve PolesCount=3 KnotsCount=2 Degree=2 IsPeriodic=0
    g12: GeomPoint X=119 Y=35 Z=0
    g13: GeomPoint X=121 Y=33 Z=0
    g14: LineSegment StartX=119 StartY=35 StartZ=0 EndX=114 EndY=35 EndZ=0
    g15: ArcOfCircle CenterX=105 CenterY=19 CenterZ=0 NormalX=0 NormalY=0 NormalZ=1 AngleXU=0 Radius=16 StartAngle=5.60905 EndAngle=6.28319
    g16: LineSegment StartX=121 StartY=33 StartZ=0 EndX=121 EndY=19 EndZ=0
    g17: LineSegment StartX=117.5 StartY=9.01251 StartZ=0 EndX=121.163 EndY=9.0125 EndZ=0
    g18: ArcOfCircle CenterX=105 CenterY=19 CenterZ=0 NormalX=0 NormalY=0 NormalZ=1 AngleXU=0 Radius=20.6155 StartAngle=5.7297 EndAngle=6.28319
    g19: LineSegment StartX=121.163 StartY=9.0125 StartZ=0 EndX=122.538 EndY=8.16329 EndZ=0
    g20: LineSegment StartX=124 StartY=38 StartZ=0 EndX=125.616 EndY=38 EndZ=0
    g21: LineSegment StartX=125.616 StartY=19 StartZ=0 EndX=125.616 EndY=38 EndZ=0
  constraints (49):
    c: Vertical(g0)
    c: Block(g0)
    c: Coincident(g1,g0)
    c: Block(g1)
    c: Coincident(g2,g1)
    c: Block(g2)
    c: Coincident(g3,g2)
    c: Horizontal(g3)
    c: Tangent(g3,g2)
    c: Coincident(g4,g0)
    c: Distance(g4) = 3
    c: Vertical(g4)
    c: Coincident(g5,g4)
    c: Horizontal(g5)
    c: Coincident(g6,g2)
    c: Coincident(g6,g5)
    c: Vertical(g6)
    c: Horizontal(g7)
    c: Distance(g7) = 105
    c: Coincident(g7,g1)
    c: Block(g3)
    c: Weight(g8) = 1
    c: Equal(g8,g9)
    c: Equal(g8,g10)
    c: InternalAlignment(g8,g11)
    c: InternalAlignment(g9,g11)
    c: InternalAlignment(g10,g11)
    c: InternalAlignment(g12,g11)
    c: InternalAlignment(g13,g11)
    c: Block(g11)
    c: Coincident(g14,g11)
    c: Coincident(g14,g3)
    c: Horizontal(g14)
    c: Block(g15)
    c: Coincident(g16,g11)
    c: Coincident(g16,g15)
    c: Vertical(g16)
    c: Distance(g16) = 14
    c: Coincident(g17,g15)
    c: Block(g18)
    c: Coincident(g19,g18)
    c: Coincident(g20,g7)
    c: Horizontal(g20)
    c: Vertical(g21)
    c: Coincident(g20,g21)
    c: Block(g20)
    c: Block(g21)
    c: Block(g19)
    c: Block(g17)
FEATURE [Part::Box] Box026  label="removeToCreteHoleForPlugHousing032"
  AttacherType = Attacher::AttachEngine3D
  Height = 28.6
  Length = 10
  Placement = pos=(-2,0,21.7) rot=(0,0,1;0rad)
  Width = 19
FEATURE [Part::Feature] Face109 .. Face112  x4 (patterned run collapsed; names and placements below)
  shape: bbox 3.5 x 17.8 x 2e-07 mm, 1 faces, 0 solids (baked)
FEATURE [Part::Revolution] Revolve117  label="removeToCreateScrewAndThreadedInsertHole045"
  Angle = 360
  Axis = (0,1,0)
  Base = (0,0,0)
  FaceMakerClass = Part::FaceMakerBullseye
  Placement = pos=(62.3,30.3,19.7) rot=(0,0,1;0rad)
  Solid = false
  Source = -> Face109
  Symmetric = false
FEATURE [Part::Revolution] Revolve118  label="removeToCreateScrewAndThreadedInsertHole046"
  Angle = 360
  Axis = (0,1,0)
  Base = (0,0,0)
  FaceMakerClass = Part::FaceMakerBullseye
  Placement = pos=(62.3,30.3,51.7) rot=(0,0,1;0rad)
  Solid = false
  Source = -> Face110
  Symmetric = false
FEATURE [Part::Revolution] Revolve119  label="removeToCreateScrewAndThreadedInsertHole047"
  Angle = 360
  Axis = (0,1,0)
  Base = (0,0,0)
  FaceMakerClass = Part::FaceMakerBullseye
  Placement = pos=(30.3,30.3,19.7) rot=(0,0,1;0rad)
  Solid = false
  Source = -> Face111
  Symmetric = false
FEATURE [Part::Revolution] Revolve120  label="removeToCreateScrewAndThreadedInsertHole048"
  Angle = 360
  Axis = (0,1,0)
  Base = (0,0,0)
  FaceMakerClass = Part::FaceMakerBullseye
  Placement = pos=(30.3,30.3,51.7) rot=(0,0,1;0rad)
  Solid = false
  Source = -> Face112
  Symmetric = false
FEATURE [Part::MultiFuse] Fusion087  label="createThreadedInsertHolesForFan005"
  Shapes = -> [Revolve117,Revolve118,Revolve119,Revolve120]
FEATURE [Part::Extrusion] Extrude047
  Base = -> Sketch056
  Dir = (0,0,1)
  DirMode = 2
  FaceMakerClass = Part::FaceMakerBullseye
  LengthFwd = 72
  LengthRev = 0
  Solid = true
  Symmetric = false
FEATURE [Part::Fillet] Fillet039  label="top019"
  Base = -> Extrude047
  Edges = 1 edges r=2: [Edge35]
FEATURE [Sketcher::SketchObject] Sketch057
  FullyConstrained = false
  Placement = pos=(0,0,0) rot=(1,0,0;1.5708rad)
  sketch-geometry (24):
    g0: ArcOfCircle CenterX=-4 CenterY=-10.5 CenterZ=0 NormalX=0 NormalY=0 NormalZ=1 AngleXU=0 Radius=1.5 StartAngle=6e-16 EndAngle=3.14159
    g1: ArcOfCircle CenterX=-34.2 CenterY=-10.5 CenterZ=0 NormalX=0 NormalY=0 NormalZ=1 AngleXU=0 Radius=1.5 StartAngle=0 EndAngle=3.14159
    g2: ArcOfCircle CenterX=-34.2 CenterY=-27.7 CenterZ=0 NormalX=0 NormalY=0 NormalZ=1 AngleXU=0 Radius=1.5 StartAngle=3.14159 EndAngle=6.28319
    g3: ArcOfCircle CenterX=-4 CenterY=-27.7 CenterZ=0 NormalX=0 NormalY=0 NormalZ=1 AngleXU=0 Radius=1.5 StartAngle=3.1416 EndAngle=6.28319
    g4: ArcOfCircle CenterX=-10 CenterY=-4.3 CenterZ=0 NormalX=0 NormalY=0 NormalZ=1 AngleXU=0 Radius=1.5 StartAngle=2e-16 EndAngle=3.14159
    g5: ArcOfCircle CenterX=-16.1 CenterY=-1.8 CenterZ=0 NormalX=0 NormalY=0 NormalZ=1 AngleXU=0 Radius=1.5 StartAngle=5e-16 EndAngle=3.14159
    g6: ArcOfCircle CenterX=-22.1 CenterY=-1.8 CenterZ=0 NormalX=0 NormalY=0 NormalZ=1 AngleXU=0 Radius=1.5 StartAngle=5e-16 EndAngle=3.14159
    g7: ArcOfCircle CenterX=-28.2 CenterY=-4.3 CenterZ=0 NormalX=0 NormalY=0 NormalZ=1 AngleXU=0 Radius=1.5 StartAngle=2e-16 EndAngle=3.14159
    g8: ArcOfCircle CenterX=-10 CenterY=-33.9 CenterZ=0 NormalX=0 NormalY=0 NormalZ=1 AngleXU=0 Radius=1.5 StartAngle=3.14159 EndAngle=6.28319
    g9: ArcOfCircle CenterX=-16.1 CenterY=-36.4 CenterZ=0 NormalX=0 NormalY=0 NormalZ=1 AngleXU=0 Radius=1.5 StartAngle=3.14159 EndAngle=6.28319
    g10: ArcOfCircle CenterX=-22.1 CenterY=-36.4 CenterZ=0 NormalX=0 NormalY=0 NormalZ=1 AngleXU=0 Radius=1.5 StartAngle=3.14159 EndAngle=6.28319
    g11: ArcOfCircle CenterX=-28.2 CenterY=-33.9 CenterZ=0 NormalX=0 NormalY=0 NormalZ=1 AngleXU=0 Radius=1.5 StartAngle=3.14159 EndAngle=6.28319
    g12: LineSegment StartX=-35.7 StartY=-10.5 StartZ=0 EndX=-35.7 EndY=-27.7 EndZ=0
    g13: LineSegment StartX=-32.7 StartY=-10.5 StartZ=0 EndX=-32.7 EndY=-27.7 EndZ=0
    g14: LineSegment StartX=-29.7 StartY=-33.9 StartZ=0 EndX=-29.7 EndY=-4.3 EndZ=0
    g15: LineSegment StartX=-26.7 StartY=-33.9 StartZ=0 EndX=-26.7 EndY=-4.3 EndZ=0
    g16: LineSegment StartX=-2.5 StartY=-10.5 StartZ=0 EndX=-2.5 EndY=-27.7 EndZ=0
    g17: LineSegment StartX=-8.5 StartY=-4.3 StartZ=0 EndX=-8.5 EndY=-33.9 EndZ=0
    g18: LineSegment StartX=-5.5 StartY=-10.5 StartZ=0 EndX=-5.5 EndY=-27.7 EndZ=0
    g19: LineSegment StartX=-11.5 StartY=-4.3 StartZ=0 EndX=-11.5 EndY=-33.9 EndZ=0
    g20: LineSegment StartX=-14.6 StartY=-1.8 StartZ=0 EndX=-14.6 EndY=-36.4 EndZ=0
    g21: LineSegment StartX=-17.6 StartY=-1.8 StartZ=0 EndX=-17.6 EndY=-36.4 EndZ=0
    g22: LineSegment StartX=-20.6 StartY=-36.4 StartZ=0 EndX=-20.6 EndY=-1.8 EndZ=0
    g23: LineSegment StartX=-23.6 StartY=-1.8 StartZ=0 EndX=-23.6 EndY=-36.4 EndZ=0
  constraints (48):
    c: Block(g0)
    c: Block(g1)
    c: Block(g2)
    c: Block(g3)
    c: Block(g4)
    c: Block(g5)
    c: Block(g6)
    c: Block(g7)
    c: Block(g8)
    c: Block(g9)
    c: Block(g10)
    c: Block(g11)
    c: Coincident(g12,g1)
    c: Coincident(g12,g2)
    c: Vertical(g12)
    c: Coincident(g13,g1)
    c: Coincident(g13,g2)
    c: Vertical(g13)
    c: Coincident(g14,g11)
    c: Coincident(g14,g7)
    c: Vertical(g14)
    c: Coincident(g15,g11)
    c: Coincident(g15,g7)
    c: Vertical(g15)
    c: Coincident(g16,g0)
    c: Coincident(g16,g3)
    c: Vertical(g16)
    c: Coincident(g17,g4)
    c: Coincident(g17,g8)
    c: Vertical(g17)
    c: Coincident(g18,g0)
    c: Coincident(g18,g3)
    c: Vertical(g18)
    c: Coincident(g19,g4)
    c: Coincident(g19,g8)
    c: Vertical(g19)
    c: Coincident(g20,g5)
    c: Coincident(g20,g9)
    c: Vertical(g20)
    c: Coincident(g21,g5)
    c: Coincident(g21,g9)
    c: Vertical(g21)
    c: Coincident(g22,g10)
    c: Coincident(g22,g6)
    c: Vertical(g22)
    c: Coincident(g23,g6)
    c: Coincident(g23,g10)
    c: Vertical(g23)
FEATURE [Part::Extrusion] Extrude048  label="removeToCreateFanGrillHoles004"
  Base = -> Sketch057
  Dir = (0,-1,6e-16)
  DirMode = 2
  FaceMakerClass = Part::FaceMakerBullseye
  LengthFwd = 10
  LengthRev = 0
  Placement = pos=(65.4,44,54.82) rot=(0,0,1;0rad)
  Solid = true
  Symmetric = false
FEATURE [Part::Cut] Cut040  label="top021"
  Base = -> Fillet039
  Tool = -> Extrude048
FEATURE [Part::Cylinder] Cylinder041  label="removeToCreteHoleForPlugHousing034"
  Angle = 360
  AttacherType = Attacher::AttachEngine3D
  Height = 20
  Placement = pos=(-2,19,36) rot=(0,1,0;1.5708rad)
  Radius = 14.3
FEATURE [Part::MultiFuse] Fusion089  label="removeToCreteHoleForPlugHousing035"
  Shapes = -> [Box026,Cylinder041]
FEATURE [Part::Cylinder] Cylinder042
  Angle = 360
  AttacherType = Attacher::AttachEngine3D
  Height = 20
  Placement = pos=(0,0,36.15) rot=(0,0,1;0rad)
  Radius = 14.3
FEATURE [Part::Cylinder] Cylinder043
  Angle = 360
  AttacherType = Attacher::AttachEngine3D
  Height = 10
  Placement = pos=(0,0,36.15) rot=(0,0,1;0rad)
  Radius = 4
FEATURE [Part::Box] Box027  label="removeToCreteHoleForPlugHousing036"
  AttacherType = Attacher::AttachEngine3D
  Height = 28.6
  Length = 20
  Placement = pos=(106.15,0,21.7) rot=(0,0,1;0rad)
  Width = 19
FEATURE [Part::Cut] Cut041  label="top022"
  Base = -> Cut040
  Tool = -> Fusion087
FEATURE [Part::Cut] Cut039  label="top020"
  Base = -> Cut041
  Tool = -> Fusion089
FEATURE [Part::MultiFuse] Fusion090  label="removeToCreteHoleForPlugHousing037"
  Placement = pos=(70,19,36) rot=(0,1,0;1.5708rad)
  Shapes = -> [Cylinder042,Cylinder043]
FEATURE [Part::MultiFuse] Fusion088  label="removeToCreteHoleForPlugHousing033"
  Shapes = -> [Box027,Fusion090]
FEATURE [Part::Cut] Cut042  label="removeToCreteHoleForPlugHousing038"
  Base = -> Cut039
  Tool = -> Fusion088
FEATURE [Part::MultiFuse] Fusion091  label="removeFromTop"
  Shapes = -> [Fillet038,Fusion085,Fusion084,Fusion083,Extrude045]
FEATURE [Part::Cut] Cut043  label="REAL TOP ====="
  Base = -> Fillet036
  Tool = -> Fusion091
FEATURE [Part::MultiFuse] Fusion092  label="caseScrewPillarBracket016"
  Shapes = -> [Extrude030,Extrude031,Extrude032,Extrude033,Extrude034,Extrude035,Extrude036,Extrude037,Box013,Box014]
FEATURE [Sketcher::SketchObject] Sketch058  label="topSketch015"
  FullyConstrained = true
  sketch-geometry (20):
    g0: LineSegment StartX=5.21097e-06 StartY=3 StartZ=0 EndX=5.21097e-06 EndY=19 EndZ=0
    g1: ArcOfCircle CenterX=19 CenterY=19 CenterZ=0 NormalX=0 NormalY=0 NormalZ=1 AngleXU=0 Radius=19 StartAngle=1.5708 EndAngle=3.14159
    g2: ArcOfCircle CenterX=19 CenterY=19 CenterZ=0 NormalX=0 NormalY=0 NormalZ=1 AngleXU=0 Radius=16 StartAngle=1.5708 EndAngle=3.14159
    g3: LineSegment StartX=114 StartY=35 StartZ=0 EndX=19 EndY=35 EndZ=0
    g4: LineSegment StartX=5.21097e-06 StartY=3 StartZ=0 EndX=5.21097e-06 EndY=0 EndZ=0
    g5: LineSegment StartX=3 StartY=0 StartZ=0 EndX=5.21097e-06 EndY=0 EndZ=0
    g6: LineSegment StartX=3 StartY=19 StartZ=0 EndX=3 EndY=0 EndZ=0
    g7: LineSegment StartX=19 StartY=38 StartZ=0 EndX=124 EndY=38 EndZ=0
    g8: Circle CenterX=119 CenterY=35 CenterZ=0 NormalX=0 NormalY=0 NormalZ=1 AngleXU=0 Radius=1
    g9: Circle CenterX=121 CenterY=35 CenterZ=0 NormalX=0 NormalY=0 NormalZ=1 AngleXU=0 Radius=1
    g10: Circle CenterX=121 CenterY=33 CenterZ=0 NormalX=0 NormalY=0 NormalZ=1 AngleXU=0 Radius=1
    g11: BSplineCurve PolesCount=3 KnotsCount=2 Degree=2 IsPeriodic=0
    g12: GeomPoint X=119 Y=35 Z=0
    g13: GeomPoint X=121 Y=33 Z=0
    g14: LineSegment StartX=119 StartY=35 StartZ=0 EndX=114 EndY=35 EndZ=0
    g15: ArcOfCircle CenterX=105 CenterY=19 CenterZ=0 NormalX=0 NormalY=0 NormalZ=1 AngleXU=0 Radius=19 StartAngle=5.7297 EndAngle=6.28319
    g16: ArcOfCircle CenterX=105 CenterY=19 CenterZ=0 NormalX=0 NormalY=0 NormalZ=1 AngleXU=0 Radius=16 StartAngle=5.60905 EndAngle=6.28319
    g17: LineSegment StartX=121 StartY=33 StartZ=0 EndX=121 EndY=19 EndZ=0
    g18: LineSegment StartX=124 StartY=38 StartZ=0 EndX=124 EndY=19 EndZ=0
    g19: LineSegment StartX=117.5 StartY=9.01251 StartZ=0 EndX=121.163 EndY=9.0125 EndZ=0
  constraints (46):
    c: Vertical(g0)
    c: Block(g0)
    c: Coincident(g1,g0)
    c: Block(g1)
    c: Coincident(g2,g1)
    c: Block(g2)
    c: Coincident(g3,g2)
    c: Horizontal(g3)
    c: Tangent(g3,g2)
    c: Coincident(g4,g0)
    c: Distance(g4) = 3
    c: Vertical(g4)
    c: Coincident(g5,g4)
    c: Horizontal(g5)
    c: Coincident(g6,g2)
    c: Coincident(g6,g5)
    c: Vertical(g6)
    c: Horizontal(g7)
    c: Distance(g7) = 105
    c: Coincident(g7,g1)
    c: Block(g3)
    c: Weight(g8) = 1
    c: Equal(g8,g9)
    c: Equal(g8,g10)
    c: InternalAlignment(g8,g11)
    c: InternalAlignment(g9,g11)
    c: InternalAlignment(g10,g11)
    c: InternalAlignment(g12,g11)
    c: InternalAlignment(g13,g11)
    c: Block(g11)
    c: Coincident(g14,g11)
    c: Coincident(g14,g3)
    c: Horizontal(g14)
    c: Block(g15)
    c: Coincident(g16,g15)
    c: Block(g16)
    c: Coincident(g17,g11)
    c: Coincident(g17,g16)
    c: Vertical(g17)
    c: Distance(g17) = 14
    c: Coincident(g18,g7)
    c: Coincident(g18,g15)
    c: Vertical(g18)
    c: Distance(g18) = 19
    c: Coincident(g19,g16)
    c: Coincident(g19,g15)
FEATURE [Part::Extrusion] Extrude049  label="top023"
  Base = -> Sketch058
  Dir = (0,0,1)
  DirMode = 2
  FaceMakerClass = Part::FaceMakerBullseye
  LengthFwd = 72
  LengthRev = 0
  Solid = true
  Symmetric = false
FEATURE [Sketcher::SketchObject] Sketch059
  FullyConstrained = true
  MapMode = 3
  Placement = pos=(0,0,0) rot=(1,0,0;1.5708rad)
  Support = -> [Extrude049]
  sketch-geometry (8):
    g0: Circle CenterX=80.351 CenterY=-67.6202 CenterZ=0 NormalX=0 NormalY=0 NormalZ=1 AngleXU=0 Radius=2
    g1: Circle CenterX=80.351 CenterY=-67.6202 CenterZ=0 NormalX=0 NormalY=0 NormalZ=1 AngleXU=0 Radius=3
    g2: Circle CenterX=80.351 CenterY=-4.92017 CenterZ=0 NormalX=0 NormalY=0 NormalZ=1 AngleXU=0 Radius=2
    g3: Circle CenterX=80.351 CenterY=-4.92017 CenterZ=0 NormalX=0 NormalY=0 NormalZ=1 AngleXU=0 Radius=3
    g4: Circle CenterX=23.851 CenterY=-4.92017 CenterZ=0 NormalX=0 NormalY=0 NormalZ=1 AngleXU=0 Radius=2
    g5: Circle CenterX=23.851 CenterY=-4.92017 CenterZ=0 NormalX=0 NormalY=0 NormalZ=1 AngleXU=0 Radius=3
    g6: Circle CenterX=23.851 CenterY=-67.6202 CenterZ=0 NormalX=0 NormalY=0 NormalZ=1 AngleXU=0 Radius=2
    g7: Circle CenterX=23.851 CenterY=-67.6202 CenterZ=0 NormalX=0 NormalY=0 NormalZ=1 AngleXU=0 Radius=3
  constraints (8):
    c: Block(g3)
    c: Block(g2)
    c: Block(g1)
    c: Block(g0)
    c: Block(g6)
    c: Block(g7)
    c: Block(g4)
    c: Block(g5)
FEATURE [Sketcher::SketchObject] Sketch060
  FullyConstrained = true
  MapMode = 3
  Placement = pos=(0,0,0) rot=(1,0,0;1.5708rad)
  Support = -> [Extrude049]
  sketch-geometry (8):
    g0: Circle CenterX=80.351 CenterY=-67.6202 CenterZ=0 NormalX=0 NormalY=0 NormalZ=1 AngleXU=0 Radius=3
    g1: Circle CenterX=80.351 CenterY=-4.92017 CenterZ=0 NormalX=0 NormalY=0 NormalZ=1 AngleXU=0 Radius=3
    g2: Circle CenterX=23.851 CenterY=-4.92017 CenterZ=0 NormalX=0 NormalY=0 NormalZ=1 AngleXU=0 Radius=3
    g3: Circle CenterX=23.851 CenterY=-67.6202 CenterZ=0 NormalX=0 NormalY=0 NormalZ=1 AngleXU=0 Radius=3
    g4: Circle CenterX=23.851 CenterY=-67.6202 CenterZ=0 NormalX=0 NormalY=0 NormalZ=1 AngleXU=0 Radius=5
    g5: Circle CenterX=80.351 CenterY=-67.6202 CenterZ=0 NormalX=0 NormalY=0 NormalZ=1 AngleXU=0 Radius=5
    g6: Circle CenterX=23.851 CenterY=-4.92017 CenterZ=0 NormalX=0 NormalY=0 NormalZ=1 AngleXU=0 Radius=5
    g7: Circle CenterX=80.351 CenterY=-4.92017 CenterZ=0 NormalX=0 NormalY=0 NormalZ=1 AngleXU=0 Radius=5
  constraints (8):
    c: Block(g1)
    c: Block(g0)
    c: Block(g3)
    c: Block(g2)
    c: Block(g5)
    c: Block(g4)
    c: Block(g6)
    c: Block(g7)
FEATURE [Sketcher::SketchObject] Sketch061
  FullyConstrained = true
  MapMode = 3
  Placement = pos=(0,0,0) rot=(1,0,0;1.5708rad)
  sketch-geometry (8):
    g0: Circle CenterX=80.351 CenterY=-67.6202 CenterZ=0 NormalX=0 NormalY=0 NormalZ=1 AngleXU=0 Radius=3
    g1: Circle CenterX=80.351 CenterY=-4.92017 CenterZ=0 NormalX=0 NormalY=0 NormalZ=1 AngleXU=0 Radius=3
    g2: Circle CenterX=23.851 CenterY=-4.92017 CenterZ=0 NormalX=0 NormalY=0 NormalZ=1 AngleXU=0 Radius=3
    g3: Circle CenterX=23.851 CenterY=-67.6202 CenterZ=0 NormalX=0 NormalY=0 NormalZ=1 AngleXU=0 Radius=3
    g4: Circle CenterX=23.851 CenterY=-67.6202 CenterZ=0 NormalX=0 NormalY=0 NormalZ=1 AngleXU=0 Radius=5
    g5: Circle CenterX=80.351 CenterY=-67.6202 CenterZ=0 NormalX=0 NormalY=0 NormalZ=1 AngleXU=0 Radius=5
    g6: Circle CenterX=23.851 CenterY=-4.92017 CenterZ=0 NormalX=0 NormalY=0 NormalZ=1 AngleXU=0 Radius=5
    g7: Circle CenterX=80.351 CenterY=-4.92017 CenterZ=0 NormalX=0 NormalY=0 NormalZ=1 AngleXU=0 Radius=5
  constraints (8):
    c: Block(g1)
    c: Block(g0)
    c: Block(g3)
    c: Block(g2)
    c: Block(g5)
    c: Block(g4)
    c: Block(g6)
    c: Block(g7)
FEATURE [Sketcher::SketchObject] Sketch062  label="topSketch016"
  FullyConstrained = true
  sketch-geometry (20):
    g0: LineSegment StartX=5.21097e-06 StartY=3 StartZ=0 EndX=5.21097e-06 EndY=19 EndZ=0
    g1: ArcOfCircle CenterX=19 CenterY=19 CenterZ=0 NormalX=0 NormalY=0 NormalZ=1 AngleXU=0 Radius=19 StartAngle=1.5708 EndAngle=3.14159
    g2: ArcOfCircle CenterX=19 CenterY=19 CenterZ=0 NormalX=0 NormalY=0 NormalZ=1 AngleXU=0 Radius=16 StartAngle=1.5708 EndAngle=3.14159
    g3: LineSegment StartX=114 StartY=35 StartZ=0 EndX=19 EndY=35 EndZ=0
    g4: LineSegment StartX=5.21097e-06 StartY=3 StartZ=0 EndX=5.21097e-06 EndY=0 EndZ=0
    g5: LineSegment StartX=3 StartY=0 StartZ=0 EndX=5.21097e-06 EndY=0 EndZ=0
    g6: LineSegment StartX=3 StartY=19 StartZ=0 EndX=3 EndY=0 EndZ=0
    g7: LineSegment StartX=19 StartY=38 StartZ=0 EndX=124 EndY=38 EndZ=0
    g8: Circle CenterX=119 CenterY=35 CenterZ=0 NormalX=0 NormalY=0 NormalZ=1 AngleXU=0 Radius=1
    g9: Circle CenterX=121 CenterY=35 CenterZ=0 NormalX=0 NormalY=0 NormalZ=1 AngleXU=0 Radius=1
    g10: Circle CenterX=121 CenterY=33 CenterZ=0 NormalX=0 NormalY=0 NormalZ=1 AngleXU=0 Radius=1
    g11: BSplineCurve PolesCount=3 KnotsCount=2 Degree=2 IsPeriodic=0
    g12: GeomPoint X=119 Y=35 Z=0
    g13: GeomPoint X=121 Y=33 Z=0
    g14: LineSegment StartX=119 StartY=35 StartZ=0 EndX=114 EndY=35 EndZ=0
    g15: ArcOfCircle CenterX=105 CenterY=19 CenterZ=0 NormalX=0 NormalY=0 NormalZ=1 AngleXU=0 Radius=19 StartAngle=5.7297 EndAngle=6.28319
    g16: ArcOfCircle CenterX=105 CenterY=19 CenterZ=0 NormalX=0 NormalY=0 NormalZ=1 AngleXU=0 Radius=16 StartAngle=5.60905 EndAngle=6.28319
    g17: LineSegment StartX=121 StartY=33 StartZ=0 EndX=121 EndY=19 EndZ=0
    g18: LineSegment StartX=124 StartY=38 StartZ=0 EndX=124 EndY=19 EndZ=0
    g19: LineSegment StartX=117.5 StartY=9.01251 StartZ=0 EndX=121.163 EndY=9.0125 EndZ=0
  constraints (46):
    c: Vertical(g0)
    c: Block(g0)
    c: Coincident(g1,g0)
    c: Block(g1)
    c: Coincident(g2,g1)
    c: Block(g2)
    c: Coincident(g3,g2)
    c: Horizontal(g3)
    c: Tangent(g3,g2)
    c: Coincident(g4,g0)
    c: Distance(g4) = 3
    c: Vertical(g4)
    c: Coincident(g5,g4)
    c: Horizontal(g5)
    c: Coincident(g6,g2)
    c: Coincident(g6,g5)
    c: Vertical(g6)
    c: Horizontal(g7)
    c: Distance(g7) = 105
    c: Coincident(g7,g1)
    c: Block(g3)
    c: Weight(g8) = 1
    c: Equal(g8,g9)
    c: Equal(g8,g10)
    c: InternalAlignment(g8,g11)
    c: InternalAlignment(g9,g11)
    c: InternalAlignment(g10,g11)
    c: InternalAlignment(g12,g11)
    c: InternalAlignment(g13,g11)
    c: Block(g11)
    c: Coincident(g14,g11)
    c: Coincident(g14,g3)
    c: Horizontal(g14)
    c: Block(g15)
    c: Coincident(g16,g15)
    c: Block(g16)
    c: Coincident(g17,g11)
    c: Coincident(g17,g16)
    c: Vertical(g17)
    c: Distance(g17) = 14
    c: Coincident(g18,g7)
    c: Coincident(g18,g15)
    c: Vertical(g18)
    c: Distance(g18) = 19
    c: Coincident(g19,g16)
    c: Coincident(g19,g15)
FEATURE [Part::Extrusion] Extrude053  label="top024"
  Base = -> Sketch062
  Dir = (0,0,1)
  DirMode = 2
  FaceMakerClass = Part::FaceMakerBullseye
  LengthFwd = 72
  LengthRev = 0
  Solid = true
  Symmetric = false
FEATURE [Sketcher::SketchObject] Sketch063
  FullyConstrained = true
  MapMode = 3
  Placement = pos=(0,0,0) rot=(1,0,0;1.5708rad)
  Support = -> [Extrude053]
  sketch-geometry (8):
    g0: Circle CenterX=80.351 CenterY=-67.6202 CenterZ=0 NormalX=0 NormalY=0 NormalZ=1 AngleXU=0 Radius=2
    g1: Circle CenterX=80.351 CenterY=-67.6202 CenterZ=0 NormalX=0 NormalY=0 NormalZ=1 AngleXU=0 Radius=3
    g2: Circle CenterX=80.351 CenterY=-4.92017 CenterZ=0 NormalX=0 NormalY=0 NormalZ=1 AngleXU=0 Radius=2
    g3: Circle CenterX=80.351 CenterY=-4.92017 CenterZ=0 NormalX=0 NormalY=0 NormalZ=1 AngleXU=0 Radius=3
    g4: Circle CenterX=23.851 CenterY=-4.92017 CenterZ=0 NormalX=0 NormalY=0 NormalZ=1 AngleXU=0 Radius=2
    g5: Circle CenterX=23.851 CenterY=-4.92017 CenterZ=0 NormalX=0 NormalY=0 NormalZ=1 AngleXU=0 Radius=3
    g6: Circle CenterX=23.851 CenterY=-67.6202 CenterZ=0 NormalX=0 NormalY=0 NormalZ=1 AngleXU=0 Radius=2
    g7: Circle CenterX=23.851 CenterY=-67.6202 CenterZ=0 NormalX=0 NormalY=0 NormalZ=1 AngleXU=0 Radius=3
  constraints (8):
    c: Block(g3)
    c: Block(g2)
    c: Block(g1)
    c: Block(g0)
    c: Block(g6)
    c: Block(g7)
    c: Block(g4)
    c: Block(g5)
FEATURE [Part::Extrusion] Extrude054
  Base = -> Sketch063
  Dir = (0,-1,2e-16)
  DirMode = 2
  FaceMakerClass = Part::FaceMakerBullseye
  LengthFwd = 6
  LengthRev = 0
  Placement = pos=(0,9,0) rot=(0,0,1;0rad)
  Solid = true
  Symmetric = false
FEATURE [Sketcher::SketchObject] Sketch064  label="topSketch017"
  FullyConstrained = true
  sketch-geometry (20):
    g0: LineSegment StartX=5.21097e-06 StartY=3 StartZ=0 EndX=5.21097e-06 EndY=19 EndZ=0
    g1: ArcOfCircle CenterX=19 CenterY=19 CenterZ=0 NormalX=0 NormalY=0 NormalZ=1 AngleXU=0 Radius=19 StartAngle=1.5708 EndAngle=3.14159
    g2: ArcOfCircle CenterX=19 CenterY=19 CenterZ=0 NormalX=0 NormalY=0 NormalZ=1 AngleXU=0 Radius=16 StartAngle=1.5708 EndAngle=3.14159
    g3: LineSegment StartX=114 StartY=35 StartZ=0 EndX=19 EndY=35 EndZ=0
    g4: LineSegment StartX=5.21097e-06 StartY=3 StartZ=0 EndX=5.21097e-06 EndY=0 EndZ=0
    g5: LineSegment StartX=3 StartY=0 StartZ=0 EndX=5.21097e-06 EndY=0 EndZ=0
    g6: LineSegment StartX=3 StartY=19 StartZ=0 EndX=3 EndY=0 EndZ=0
    g7: LineSegment StartX=19 StartY=38 StartZ=0 EndX=124 EndY=38 EndZ=0
    g8: Circle CenterX=119 CenterY=35 CenterZ=0 NormalX=0 NormalY=0 NormalZ=1 AngleXU=0 Radius=1
    g9: Circle CenterX=121 CenterY=35 CenterZ=0 NormalX=0 NormalY=0 NormalZ=1 AngleXU=0 Radius=1
    g10: Circle CenterX=121 CenterY=33 CenterZ=0 NormalX=0 NormalY=0 NormalZ=1 AngleXU=0 Radius=1
    g11: BSplineCurve PolesCount=3 KnotsCount=2 Degree=2 IsPeriodic=0
    g12: GeomPoint X=119 Y=35 Z=0
    g13: GeomPoint X=121 Y=33 Z=0
    g14: LineSegment StartX=119 StartY=35 StartZ=0 EndX=114 EndY=35 EndZ=0
    g15: ArcOfCircle CenterX=105 CenterY=19 CenterZ=0 NormalX=0 NormalY=0 NormalZ=1 AngleXU=0 Radius=19 StartAngle=5.7297 EndAngle=6.28319
    g16: ArcOfCircle CenterX=105 CenterY=19 CenterZ=0 NormalX=0 NormalY=0 NormalZ=1 AngleXU=0 Radius=16 StartAngle=5.60905 EndAngle=6.28319
    g17: LineSegment StartX=121 StartY=33 StartZ=0 EndX=121 EndY=19 EndZ=0
    g18: LineSegment StartX=124 StartY=38 StartZ=0 EndX=124 EndY=19 EndZ=0
    g19: LineSegment StartX=117.5 StartY=9.01251 StartZ=0 EndX=121.163 EndY=9.0125 EndZ=0
  constraints (46):
    c: Vertical(g0)
    c: Block(g0)
    c: Coincident(g1,g0)
    c: Block(g1)
    c: Coincident(g2,g1)
    c: Block(g2)
    c: Coincident(g3,g2)
    c: Horizontal(g3)
    c: Tangent(g3,g2)
    c: Coincident(g4,g0)
    c: Distance(g4) = 3
    c: Vertical(g4)
    c: Coincident(g5,g4)
    c: Horizontal(g5)
    c: Coincident(g6,g2)
    c: Coincident(g6,g5)
    c: Vertical(g6)
    c: Horizontal(g7)
    c: Distance(g7) = 105
    c: Coincident(g7,g1)
    c: Block(g3)
    c: Weight(g8) = 1
    c: Equal(g8,g9)
    c: Equal(g8,g10)
    c: InternalAlignment(g8,g11)
    c: InternalAlignment(g9,g11)
    c: InternalAlignment(g10,g11)
    c: InternalAlignment(g12,g11)
    c: InternalAlignment(g13,g11)
    c: Block(g11)
    c: Coincident(g14,g11)
    c: Coincident(g14,g3)
    c: Horizontal(g14)
    c: Block(g15)
    c: Coincident(g16,g15)
    c: Block(g16)
    c: Coincident(g17,g11)
    c: Coincident(g17,g16)
    c: Vertical(g17)
    c: Distance(g17) = 14
    c: Coincident(g18,g7)
    c: Coincident(g18,g15)
    c: Vertical(g18)
    c: Distance(g18) = 19
    c: Coincident(g19,g16)
    c: Coincident(g19,g15)
FEATURE [Sketcher::SketchObject] Sketch065
  FullyConstrained = true
  MapMode = 3
  Placement = pos=(0,0,0) rot=(1,0,0;1.5708rad)
  sketch-geometry (8):
    g0: Circle CenterX=80.351 CenterY=-67.6202 CenterZ=0 NormalX=0 NormalY=0 NormalZ=1 AngleXU=0 Radius=3
    g1: Circle CenterX=80.351 CenterY=-4.92017 CenterZ=0 NormalX=0 NormalY=0 NormalZ=1 AngleXU=0 Radius=3
    g2: Circle CenterX=23.851 CenterY=-4.92017 CenterZ=0 NormalX=0 NormalY=0 NormalZ=1 AngleXU=0 Radius=3
    g3: Circle CenterX=23.851 CenterY=-67.6202 CenterZ=0 NormalX=0 NormalY=0 NormalZ=1 AngleXU=0 Radius=3
    g4: Circle CenterX=23.851 CenterY=-67.6202 CenterZ=0 NormalX=0 NormalY=0 NormalZ=1 AngleXU=0 Radius=5
    g5: Circle CenterX=80.351 CenterY=-67.6202 CenterZ=0 NormalX=0 NormalY=0 NormalZ=1 AngleXU=0 Radius=5
    g6: Circle CenterX=23.851 CenterY=-4.92017 CenterZ=0 NormalX=0 NormalY=0 NormalZ=1 AngleXU=0 Radius=5
    g7: Circle CenterX=80.351 CenterY=-4.92017 CenterZ=0 NormalX=0 NormalY=0 NormalZ=1 AngleXU=0 Radius=5
  constraints (8):
    c: Block(g1)
    c: Block(g0)
    c: Block(g3)
    c: Block(g2)
    c: Block(g5)
    c: Block(g4)
    c: Block(g6)
    c: Block(g7)
FEATURE [Part::Extrusion] Extrude056
  Base = -> Sketch065
  Dir = (0,-1,2e-16)
  DirMode = 2
  FaceMakerClass = Part::FaceMakerBullseye
  LengthFwd = 2
  LengthRev = 0
  Solid = true
  Symmetric = false
FEATURE [Part::Extrusion] Extrude057  label="top025"
  Base = -> Sketch064
  Dir = (0,0,1)
  DirMode = 2
  FaceMakerClass = Part::FaceMakerBullseye
  LengthFwd = 72
  LengthRev = 0
  Solid = true
  Symmetric = false
FEATURE [Sketcher::SketchObject] Sketch066
  FullyConstrained = true
  MapMode = 3
  Placement = pos=(0,0,0) rot=(1,0,0;1.5708rad)
  Support = -> [Extrude057]
  sketch-geometry (8):
    g0: Circle CenterX=80.351 CenterY=-67.6202 CenterZ=0 NormalX=0 NormalY=0 NormalZ=1 AngleXU=0 Radius=3
    g1: Circle CenterX=80.351 CenterY=-4.92017 CenterZ=0 NormalX=0 NormalY=0 NormalZ=1 AngleXU=0 Radius=3
    g2: Circle CenterX=23.851 CenterY=-4.92017 CenterZ=0 NormalX=0 NormalY=0 NormalZ=1 AngleXU=0 Radius=3
    g3: Circle CenterX=23.851 CenterY=-67.6202 CenterZ=0 NormalX=0 NormalY=0 NormalZ=1 AngleXU=0 Radius=3
    g4: Circle CenterX=23.851 CenterY=-67.6202 CenterZ=0 NormalX=0 NormalY=0 NormalZ=1 AngleXU=0 Radius=5
    g5: Circle CenterX=80.351 CenterY=-67.6202 CenterZ=0 NormalX=0 NormalY=0 NormalZ=1 AngleXU=0 Radius=5
    g6: Circle CenterX=23.851 CenterY=-4.92017 CenterZ=0 NormalX=0 NormalY=0 NormalZ=1 AngleXU=0 Radius=5
    g7: Circle CenterX=80.351 CenterY=-4.92017 CenterZ=0 NormalX=0 NormalY=0 NormalZ=1 AngleXU=0 Radius=5
  constraints (8):
    c: Block(g1)
    c: Block(g0)
    c: Block(g3)
    c: Block(g2)
    c: Block(g5)
    c: Block(g4)
    c: Block(g6)
    c: Block(g7)
FEATURE [Part::Extrusion] Extrude055
  Base = -> Sketch066
  Dir = (0,-1,2e-16)
  DirMode = 2
  FaceMakerClass = Part::FaceMakerBullseye
  LengthFwd = 2
  LengthRev = 0
  Solid = true
  Symmetric = false
FEATURE [Part::Fillet] Fillet041
  Base = -> Extrude056
  Edges = 4 edges r=1.99: [Edge6,Edge12,Edge18,Edge24]
FEATURE [Part::Cut] Cut045
  Base = -> Extrude055
  Placement = pos=(0,6,0) rot=(0,0,1;0rad)
  Tool = -> Fillet041
FEATURE [Part::MultiFuse] Fusion095  label="pcbScrewPillars"
  Placement = pos=(-3.2,-1,72.3) rot=(0,0,1;0rad)
  Shapes = -> [Cut045,Extrude054]
FEATURE [Part::Feature] Face113
  shape: bbox 3.2 x 1.5 x 2e-07 mm, 1 faces, 0 solids (baked)
FEATURE [Part::Revolution] Revolve121  label="backCaseScrewRetainer002"
  Angle = 360
  Axis = (0,1,0)
  Base = (0,0,0)
  FaceMakerClass = Part::FaceMakerBullseye
  Placement = pos=(12.5,3,62) rot=(0,0,1;0rad)
  Solid = false
  Source = -> Face113
  Symmetric = false
FEATURE [Part::Feature] Face114
  shape: bbox 3.2 x 1.5 x 2e-07 mm, 1 faces, 0 solids (baked)
FEATURE [Part::Feature] Face115
  shape: bbox 3.2 x 1.5 x 2e-07 mm, 1 faces, 0 solids (baked)
FEATURE [Part::Feature] Face116
  shape: bbox 3.2 x 1.5 x 2e-07 mm, 1 faces, 0 solids (baked)
FEATURE [Part::Revolution] Revolve122  label="frontCaseScrewRetainer004"
  Angle = 360
  Axis = (0,1,0)
  Base = (0,0,0)
  FaceMakerClass = Part::FaceMakerBullseye
  Placement = pos=(89.5,3,68.5) rot=(0,0,1;0rad)
  Solid = false
  Source = -> Face115
  Symmetric = false
FEATURE [Part::Revolution] Revolve123  label="frontCaseScrewRetainer005"
  Angle = 360
  Axis = (0,1,0)
  Base = (0,0,0)
  FaceMakerClass = Part::FaceMakerBullseye
  Placement = pos=(89.5,3,3.5) rot=(0,0,1;0rad)
  Solid = false
  Source = -> Face116
  Symmetric = false
FEATURE [Part::Revolution] Revolve124  label="backCaseScrewRetainer003"
  Angle = 360
  Axis = (0,1,0)
  Base = (0,0,0)
  FaceMakerClass = Part::FaceMakerBullseye
  Placement = pos=(12.5,3,10) rot=(0,0,1;0rad)
  Solid = false
  Source = -> Face114
  Symmetric = false
FEATURE [Part::Feature] Face117
  shape: bbox 3.6 x 3.2 x 2e-07 mm, 1 faces, 0 solids (baked)
FEATURE [Part::Revolution] Revolve125  label="moreFrontCaseScrewRetainer004"
  Angle = 360
  Axis = (0,1,0)
  Base = (0,0,0)
  FaceMakerClass = Part::FaceMakerBullseye
  Placement = pos=(109.5,4.5,68.5) rot=(0,0,1;0rad)
  Solid = false
  Source = -> Face117
  Symmetric = false
FEATURE [Part::Feature] Face118
  shape: bbox 3.6 x 3.2 x 2e-07 mm, 1 faces, 0 solids (baked)
FEATURE [Part::Revolution] Revolve126  label="moreFrontCaseScrewRetainer005"
  Angle = 360
  Axis = (0,1,0)
  Base = (0,0,0)
  FaceMakerClass = Part::FaceMakerBullseye
  Placement = pos=(109.5,4.5,3.5) rot=(0,0,1;0rad)
  Solid = false
  Source = -> Face118
  Symmetric = false
FEATURE [Part::MultiFuse] Fusion096  label="screwRetainers001"
  Shapes = -> [Revolve126,Revolve125,Revolve124,Revolve123,Revolve122,Revolve121]
FEATURE [Part::Feature] Face119
  shape: bbox 10 x 16.5 x 2e-07 mm, 1 faces, 0 solids (baked)
FEATURE [Part::Revolution] Revolve130  label="plugHousing050"
  Angle = 360
  Axis = (0,1,0)
  Base = (0,0,0)
  FaceMakerClass = Part::FaceMakerBullseye
  Placement = pos=(0,0,36.15) rot=(0,0,1;0rad)
  Solid = false
  Source = -> Face119
  Symmetric = false
FEATURE [Part::Feature] Face120
  shape: bbox 10 x 16.5 x 2e-07 mm, 1 faces, 0 solids (baked)
FEATURE [Part::Feature] Face121
  shape: bbox 10 x 16.5 x 2e-07 mm, 1 faces, 0 solids (baked)
FEATURE [Part::Revolution] Revolve127  label="plugHousing047"
  Angle = 360
  Axis = (0,1,0)
  Base = (0,0,0)
  FaceMakerClass = Part::FaceMakerBullseye
  Placement = pos=(0,0,36.15) rot=(0,0,1;0rad)
  Solid = false
  Source = -> Face121
  Symmetric = false
FEATURE [Part::Feature] Face122
  shape: bbox 10 x 16.5 x 2e-07 mm, 1 faces, 0 solids (baked)
FEATURE [Part::Feature] Face123
  shape: bbox 10 x 16.5 x 2e-07 mm, 1 faces, 0 solids (baked)
FEATURE [Part::Revolution] Revolve128  label="plugHousing048"
  Angle = 360
  Axis = (0,1,0)
  Base = (0,0,0)
  FaceMakerClass = Part::FaceMakerBullseye
  Placement = pos=(0,0,36.15) rot=(0,0,1;0rad)
  Solid = false
  Source = -> Face123
  Symmetric = false
FEATURE [Part::MultiFuse] Fusion100  label="plugHousing054"
  Placement = pos=(0,0,0) rot=(0,0,1;1.5708rad)
  Shapes = -> [Revolve130,Revolve128]
FEATURE [Part::Feature] Face124
  shape: bbox 10 x 16.5 x 2e-07 mm, 1 faces, 0 solids (baked)
FEATURE [Part::Feature] Face125
  shape: bbox 10 x 16.5 x 2e-07 mm, 1 faces, 0 solids (baked)
FEATURE [Part::Revolution] Revolve129  label="plugHousing049"
  Angle = 360
  Axis = (0,1,0)
  Base = (0,0,0)
  FaceMakerClass = Part::FaceMakerBullseye
  Placement = pos=(0,0,36.15) rot=(0,0,1;0rad)
  Solid = false
  Source = -> Face125
  Symmetric = false
FEATURE [Part::Feature] Face126
  shape: bbox 10 x 16.5 x 2e-07 mm, 1 faces, 0 solids (baked)
FEATURE [Part::Revolution] Revolve131  label="plugHousing058"
  Angle = 360
  Axis = (0,1,0)
  Base = (0,0,0)
  FaceMakerClass = Part::FaceMakerBullseye
  Placement = pos=(0,0,36.15) rot=(0,0,1;0rad)
  Solid = false
  Source = -> Face120
  Symmetric = false
FEATURE [Part::MultiFuse] Fusion099  label="plugHousing053"
  Placement = pos=(0,0,0) rot=(0,0,1;1.5708rad)
  Shapes = -> [Revolve127,Revolve131]
FEATURE [Part::MultiFuse] Fusion102  label="plugHousing056"
  Placement = pos=(0,19,0) rot=(0,0,1;3.14159rad)
  Shapes = -> [Fusion100,Fusion099]
FEATURE [Part::Revolution] Revolve132  label="plugHousing059"
  Angle = 360
  Axis = (0,1,0)
  Base = (0,0,0)
  FaceMakerClass = Part::FaceMakerBullseye
  Placement = pos=(0,0,36.15) rot=(0,0,1;0rad)
  Solid = false
  Source = -> Face126
  Symmetric = false
FEATURE [Part::Revolution] Revolve133  label="plugHousing060"
  Angle = 360
  Axis = (0,1,0)
  Base = (0,0,0)
  FaceMakerClass = Part::FaceMakerBullseye
  Placement = pos=(0,0,36.15) rot=(0,0,1;0rad)
  Solid = false
  Source = -> Face122
  Symmetric = false
FEATURE [Part::MultiFuse] Fusion097  label="plugHousing051"
  Placement = pos=(0,0,0) rot=(0,0,1;1.5708rad)
  Shapes = -> [Revolve133,Revolve132]
FEATURE [Part::Revolution] Revolve134  label="plugHousing061"
  Angle = 360
  Axis = (0,1,0)
  Base = (0,0,0)
  FaceMakerClass = Part::FaceMakerBullseye
  Placement = pos=(0,0,36.15) rot=(0,0,1;0rad)
  Solid = false
  Source = -> Face124
  Symmetric = false
FEATURE [Part::MultiFuse] Fusion101  label="plugHousing055"
  Placement = pos=(0,0,0) rot=(0,0,1;1.5708rad)
  Shapes = -> [Revolve129,Revolve134]
FEATURE [Part::MultiFuse] Fusion098  label="plugHousing052"
  Placement = pos=(0,19,0) rot=(0,0,1;3.14159rad)
  Shapes = -> [Fusion097,Fusion101]
FEATURE [Part::MultiFuse] Fusion103  label="plugHousing057"
  Placement = pos=(122.621,0,-0.15) rot=(0,0,1;0rad)
  Shapes = -> [Fusion102,Fusion098]
FEATURE [Part::Box] Box028  label="Cube015"
  AttacherType = Attacher::AttachEngine3D
  Height = 28
  Length = 3
  Placement = pos=(110.7,19,22) rot=(0,0,1;0rad)
  Width = 15.7
FEATURE [Part::Cylinder] Cylinder044
  Angle = 360
  AttacherType = Attacher::AttachEngine3D
  Height = 20
  Placement = pos=(0,0,36.15) rot=(0,0,1;0rad)
  Radius = 10.3
FEATURE [Part::Cylinder] Cylinder045
  Angle = 360
  AttacherType = Attacher::AttachEngine3D
  Height = 10
  Placement = pos=(0,0,36.15) rot=(0,0,1;0rad)
  Radius = 4
FEATURE [Part::MultiFuse] Fusion104  label="removeToCreteHoleForPlugHousing040"
  Placement = pos=(70,19,36) rot=(0,1,0;1.5708rad)
  Shapes = -> [Cylinder044,Cylinder045]
FEATURE [Part::Cut] Cut046  label="plugHousingTab003"
  Base = -> Box028
  Tool = -> Fusion104
FEATURE [Part::MultiFuse] Fusion105  label="plugHousing062"
  Shapes = -> [Fusion103,Cut046]
FEATURE [Part::Fillet] Fillet042
  Base = -> Fusion105
  Edges = 1 edges r=2: [Edge25]
FEATURE [Part::Fillet] Fillet043  label="plugHousing063"
  Base = -> Fillet042
  Edges = 1 edges r=2: [Edge8]
  Placement = pos=(7,0,0) rot=(0,0,1;0rad)
FEATURE [Part::Feature] Face127
  shape: bbox 10 x 16.5 x 2e-07 mm, 1 faces, 0 solids (baked)
FEATURE [Part::Feature] Face128
  shape: bbox 10 x 16.5 x 2e-07 mm, 1 faces, 0 solids (baked)
FEATURE [Part::Revolution] Revolve137  label="plugHousing070"
  Angle = 360
  Axis = (0,1,0)
  Base = (0,0,0)
  FaceMakerClass = Part::FaceMakerBullseye
  Placement = pos=(0,0,36.15) rot=(0,0,1;0rad)
  Solid = false
  Source = -> Face127
  Symmetric = false
FEATURE [Part::Revolution] Revolve140  label="plugHousing073"
  Angle = 360
  Axis = (0,1,0)
  Base = (0,0,0)
  FaceMakerClass = Part::FaceMakerBullseye
  Placement = pos=(0,0,36.15) rot=(0,0,1;0rad)
  Solid = false
  Source = -> Face128
  Symmetric = false
FEATURE [Part::Feature] Face129
  shape: bbox 10 x 16.5 x 2e-07 mm, 1 faces, 0 solids (baked)
FEATURE [Part::Revolution] Revolve138  label="plugHousing071"
  Angle = 360
  Axis = (0,1,0)
  Base = (0,0,0)
  FaceMakerClass = Part::FaceMakerBullseye
  Placement = pos=(0,0,36.15) rot=(0,0,1;0rad)
  Solid = false
  Source = -> Face129
  Symmetric = false
FEATURE [Part::Feature] Face130
  shape: bbox 10 x 16.5 x 2e-07 mm, 1 faces, 0 solids (baked)
FEATURE [Part::Revolution] Revolve139  label="plugHousing072"
  Angle = 360
  Axis = (0,1,0)
  Base = (0,0,0)
  FaceMakerClass = Part::FaceMakerBullseye
  Placement = pos=(0,0,36.15) rot=(0,0,1;0rad)
  Solid = false
  Source = -> Face130
  Symmetric = false
FEATURE [Part::Feature] Face131
  shape: bbox 10 x 16.5 x 2e-07 mm, 1 faces, 0 solids (baked)
FEATURE [Part::Revolution] Revolve135  label="plugHousing068"
  Angle = 360
  Axis = (0,1,0)
  Base = (0,0,0)
  FaceMakerClass = Part::FaceMakerBullseye
  Placement = pos=(0,0,36.15) rot=(0,0,1;0rad)
  Solid = false
  Source = -> Face131
  Symmetric = false
FEATURE [Part::MultiFuse] Fusion112  label="plugHousing078"
  Placement = pos=(0,0,0) rot=(0,0,1;1.5708rad)
  Shapes = -> [Revolve135,Revolve139]
FEATURE [Part::Feature] Face132
  shape: bbox 10 x 16.5 x 2e-07 mm, 1 faces, 0 solids (baked)
FEATURE [Part::Revolution] Revolve141  label="plugHousing074"
  Angle = 360
  Axis = (0,1,0)
  Base = (0,0,0)
  FaceMakerClass = Part::FaceMakerBullseye
  Placement = pos=(0,0,36.15) rot=(0,0,1;0rad)
  Solid = false
  Source = -> Face132
  Symmetric = false
FEATURE [Part::MultiFuse] Fusion110  label="plugHousing076"
  Placement = pos=(0,0,0) rot=(0,0,1;1.5708rad)
  Shapes = -> [Revolve141,Revolve140]
FEATURE [Part::Feature] Face133
  shape: bbox 10 x 16.5 x 2e-07 mm, 1 faces, 0 solids (baked)
FEATURE [Part::Revolution] Revolve136  label="plugHousing069"
  Angle = 360
  Axis = (0,1,0)
  Base = (0,0,0)
  FaceMakerClass = Part::FaceMakerBullseye
  Placement = pos=(0,0,36.15) rot=(0,0,1;0rad)
  Solid = false
  Source = -> Face133
  Symmetric = false
FEATURE [Part::MultiFuse] Fusion106  label="plugHousing064"
  Placement = pos=(0,0,0) rot=(0,0,1;1.5708rad)
  Shapes = -> [Revolve138,Revolve136]
FEATURE [Part::MultiFuse] Fusion108  label="plugHousing066"
  Placement = pos=(0,19,0) rot=(0,0,1;3.14159rad)
  Shapes = -> [Fusion106,Fusion112]
FEATURE [Part::Feature] Face134
  shape: bbox 10 x 16.5 x 2e-07 mm, 1 faces, 0 solids (baked)
FEATURE [Part::Revolution] Revolve142  label="plugHousing075"
  Angle = 360
  Axis = (0,1,0)
  Base = (0,0,0)
  FaceMakerClass = Part::FaceMakerBullseye
  Placement = pos=(0,0,36.15) rot=(0,0,1;0rad)
  Solid = false
  Source = -> Face134
  Symmetric = false
FEATURE [Part::MultiFuse] Fusion107  label="plugHousing065"
  Placement = pos=(0,0,0) rot=(0,0,1;1.5708rad)
  Shapes = -> [Revolve137,Revolve142]
FEATURE [Part::MultiFuse] Fusion111  label="plugHousing077"
  Placement = pos=(0,19,0) rot=(0,0,1;3.14159rad)
  Shapes = -> [Fusion110,Fusion107]
FEATURE [Part::MultiFuse] Fusion109  label="plugHousing067"
  Placement = pos=(131.236,0,-0.15) rot=(0,0,1;0rad)
  Shapes = -> [Fusion108,Fusion111]
FEATURE [Part::MultiFuse] Fusion113  label="plugHousing079"
  Shapes = -> [Fillet043,Fusion109]
FEATURE [Part::Feature] Face135
  shape: bbox 3.5 x 17.8 x 2e-07 mm, 1 faces, 0 solids (baked)
FEATURE [Part::Revolution] Revolve143  label="removeToCreateScrewAndThreadedInsertHole049"
  Angle = 360
  Axis = (0,1,0)
  Base = (0,0,0)
  FaceMakerClass = Part::FaceMakerBullseye
  Placement = pos=(12.5,0,10) rot=(0,0,1;0rad)
  Solid = false
  Source = -> Face135
  Symmetric = false
FEATURE [Part::Feature] Face136
  shape: bbox 3.5 x 17.8 x 2e-07 mm, 1 faces, 0 solids (baked)
FEATURE [Part::Revolution] Revolve144  label="removeToCreateScrewAndThreadedInsertHole050"
  Angle = 360
  Axis = (0,1,0)
  Base = (0,0,0)
  FaceMakerClass = Part::FaceMakerBullseye
  Placement = pos=(12.5,0,62) rot=(0,0,1;0rad)
  Solid = false
  Source = -> Face136
  Symmetric = false
FEATURE [Part::Feature] Face137
  shape: bbox 3.5 x 17.8 x 2e-07 mm, 1 faces, 0 solids (baked)
FEATURE [Part::Revolution] Revolve145  label="removeToCreateScrewAndThreadedInsertHole051"
  Angle = 360
  Axis = (0,1,0)
  Base = (0,0,0)
  FaceMakerClass = Part::FaceMakerBullseye
  Placement = pos=(89.5,0,68.5) rot=(0,0,1;0rad)
  Solid = false
  Source = -> Face137
  Symmetric = false
FEATURE [Part::Feature] Face138
  shape: bbox 3.5 x 17.8 x 2e-07 mm, 1 faces, 0 solids (baked)
FEATURE [Part::Revolution] Revolve146  label="removeToCreateScrewAndThreadedInsertHole052"
  Angle = 360
  Axis = (0,1,0)
  Base = (0,0,0)
  FaceMakerClass = Part::FaceMakerBullseye
  Placement = pos=(89.5,0,3.5) rot=(0,0,1;0rad)
  Solid = false
  Source = -> Face138
  Symmetric = false
FEATURE [Part::Feature] Face139
  shape: bbox 3.5 x 17.8 x 2e-07 mm, 1 faces, 0 solids (baked)
FEATURE [Part::Revolution] Revolve147  label="removeToCreateScrewAndThreadedInsertHole053"
  Angle = 360
  Axis = (0,1,0)
  Base = (0,0,0)
  FaceMakerClass = Part::FaceMakerBullseye
  Placement = pos=(109.5,4.7,3.5) rot=(0,0,1;0rad)
  Solid = false
  Source = -> Face139
  Symmetric = false
FEATURE [Part::Feature] Face140
  shape: bbox 3.5 x 17.8 x 2e-07 mm, 1 faces, 0 solids (baked)
FEATURE [Part::Revolution] Revolve148  label="removeToCreateScrewAndThreadedInsertHole054"
  Angle = 360
  Axis = (0,1,0)
  Base = (0,0,0)
  FaceMakerClass = Part::FaceMakerBullseye
  Placement = pos=(109.5,4.7,68.5) rot=(0,0,1;0rad)
  Solid = false
  Source = -> Face140
  Symmetric = false
FEATURE [Part::MultiFuse] Fusion114  label="removeToCreateScrewAndThreadedInsertHole055"
  Shapes = -> [Revolve148,Revolve147,Revolve146,Revolve145,Revolve144,Revolve143]
FEATURE [Part::Cut] Cut047  label="casePillars004"
  Base = -> Cut037
  Tool = -> Fusion114
FEATURE [Part::Feature] Face141
  shape: bbox 3.5 x 17.8 x 2e-07 mm, 1 faces, 0 solids (baked)
FEATURE [Part::Feature] Face142
  shape: bbox 3.5 x 17.8 x 2e-07 mm, 1 faces, 0 solids (baked)
FEATURE [Part::Feature] Face143
  shape: bbox 3.5 x 17.8 x 2e-07 mm, 1 faces, 0 solids (baked)
FEATURE [Part::Revolution] Revolve149  label="removeToCreateScrewAndThreadedInsertHole057"
  Angle = 360
  Axis = (0,1,0)
  Base = (0,0,0)
  FaceMakerClass = Part::FaceMakerBullseye
  Placement = pos=(12.5,0,10) rot=(0,0,1;0rad)
  Solid = false
  Source = -> Face141
  Symmetric = false
FEATURE [Part::Feature] Face144
  shape: bbox 3.5 x 17.8 x 2e-07 mm, 1 faces, 0 solids (baked)
FEATURE [Part::Feature] Face145
  shape: bbox 3.5 x 17.8 x 2e-07 mm, 1 faces, 0 solids (baked)
FEATURE [Part::Feature] Face146
  shape: bbox 3.5 x 17.8 x 2e-07 mm, 1 faces, 0 solids (baked)
FEATURE [Part::Revolution] Revolve150  label="removeToCreateScrewAndThreadedInsertHole058"
  Angle = 360
  Axis = (0,1,0)
  Base = (0,0,0)
  FaceMakerClass = Part::FaceMakerBullseye
  Placement = pos=(12.5,0,62) rot=(0,0,1;0rad)
  Solid = false
  Source = -> Face146
  Symmetric = false
FEATURE [Part::Revolution] Revolve151  label="removeToCreateScrewAndThreadedInsertHole059"
  Angle = 360
  Axis = (0,1,0)
  Base = (0,0,0)
  FaceMakerClass = Part::FaceMakerBullseye
  Placement = pos=(89.5,0,68.5) rot=(0,0,1;0rad)
  Solid = false
  Source = -> Face143
  Symmetric = false
FEATURE [Part::Revolution] Revolve152  label="removeToCreateScrewAndThreadedInsertHole060"
  Angle = 360
  Axis = (0,1,0)
  Base = (0,0,0)
  FaceMakerClass = Part::FaceMakerBullseye
  Placement = pos=(89.5,0,3.5) rot=(0,0,1;0rad)
  Solid = false
  Source = -> Face142
  Symmetric = false
FEATURE [Part::Revolution] Revolve153  label="removeToCreateScrewAndThreadedInsertHole061"
  Angle = 360
  Axis = (0,1,0)
  Base = (0,0,0)
  FaceMakerClass = Part::FaceMakerBullseye
  Placement = pos=(109.5,4.7,3.5) rot=(0,0,1;0rad)
  Solid = false
  Source = -> Face145
  Symmetric = false
FEATURE [Part::Revolution] Revolve154  label="removeToCreateScrewAndThreadedInsertHole062"
  Angle = 360
  Axis = (0,1,0)
  Base = (0,0,0)
  FaceMakerClass = Part::FaceMakerBullseye
  Placement = pos=(109.5,4.7,68.5) rot=(0,0,1;0rad)
  Solid = false
  Source = -> Face144
  Symmetric = false
FEATURE [Part::MultiFuse] Fusion115  label="removeToCreateScrewAndThreadedInsertHole056"
  Shapes = -> [Revolve154,Revolve153,Revolve152,Revolve151,Revolve150,Revolve149]
FEATURE [Part::Feature] Face147
  shape: bbox 9.8 x 26.5 x 2e-07 mm, 1 faces, 0 solids (baked)
FEATURE [Part::Revolution] Revolve155
  Angle = 360
  Axis = (0,1,0)
  Base = (0,0,0)
  FaceMakerClass = Part::FaceMakerBullseye
  Placement = pos=(0,0,0) rot=(0,0,1;1.5708rad)
  Solid = false
  Source = -> Face147
  Symmetric = false
FEATURE [Part::Feature] Face148
  shape: bbox 9.8 x 26.5 x 2e-07 mm, 1 faces, 0 solids (baked)
FEATURE [Part::Revolution] Revolve156
  Angle = 360
  Axis = (0,1,0)
  Base = (0,0,0)
  FaceMakerClass = Part::FaceMakerBullseye
  Placement = pos=(0,0,0) rot=(0,0,1;1.5708rad)
  Solid = false
  Source = -> Face148
  Symmetric = false
FEATURE [Part::MultiFuse] Fusion116
  Placement = pos=(-18,19,36) rot=(0,0,1;0rad)
  Shapes = -> [Revolve156,Revolve155]
FEATURE [Part::Box] Box029  label="Cube016"
  AttacherType = Attacher::AttachEngine3D
  Height = 28
  Length = 3
  Placement = pos=(110.7,19,22) rot=(0,0,1;0rad)
  Width = 15.7
FEATURE [Part::Cylinder] Cylinder046
  Angle = 360
  AttacherType = Attacher::AttachEngine3D
  Height = 10
  Placement = pos=(0,0,36.15) rot=(0,0,1;0rad)
  Radius = 4
FEATURE [Part::Cylinder] Cylinder047
  Angle = 360
  AttacherType = Attacher::AttachEngine3D
  Height = 20
  Placement = pos=(0,0,36.15) rot=(0,0,1;0rad)
  Radius = 10.3
FEATURE [Part::MultiFuse] Fusion117  label="removeToCreteHoleForPlugHousing041"
  Placement = pos=(70,19,36) rot=(0,1,0;1.5708rad)
  Shapes = -> [Cylinder047,Cylinder046]
FEATURE [Part::Cut] Cut049  label="plugHousingTab004"
  Base = -> Box029
  Placement = pos=(-107.4,-14,0) rot=(0,0,1;0rad)
  Tool = -> Fusion117
FEATURE [Part::Box] Box030  label="Cube017"
  AttacherType = Attacher::AttachEngine3D
  Height = 28
  Length = 3
  Placement = pos=(110.7,19,22) rot=(0,0,1;0rad)
  Width = 15.7
FEATURE [Part::Cylinder] Cylinder048
  Angle = 360
  AttacherType = Attacher::AttachEngine3D
  Height = 10
  Placement = pos=(0,0,36.15) rot=(0,0,1;0rad)
  Radius = 4
FEATURE [Part::Cylinder] Cylinder049
  Angle = 360
  AttacherType = Attacher::AttachEngine3D
  Height = 20
  Placement = pos=(0,0,36.15) rot=(0,0,1;0rad)
  Radius = 10.3
FEATURE [Part::MultiFuse] Fusion118  label="removeToCreteHoleForPlugHousing042"
  Placement = pos=(70,19,36) rot=(0,1,0;1.5708rad)
  Shapes = -> [Cylinder049,Cylinder048]
FEATURE [Part::Cut] Cut050  label="plugHousingTab005"
  Base = -> Box030
  Placement = pos=(-107.4,-14,0) rot=(0,0,1;0rad)
  Tool = -> Fusion118
FEATURE [Part::MultiFuse] Fusion119
  Placement = pos=(9.6,23,0) rot=(0,0,1;3.14159rad)
  Shapes = -> [Cut049,Cut050]
FEATURE [Part::Box] Box031  label="Cube018"
  AttacherType = Attacher::AttachEngine3D
  Height = 10
  Length = 3
  Placement = pos=(3.3,4,12) rot=(0,0,1;0rad)
  Width = 10
FEATURE [Part::Fillet] Fillet044
  Base = -> Box031
  Edges = 1 edges r=2: [Edge11]
FEATURE [Part::Box] Box032  label="Cube019"
  AttacherType = Attacher::AttachEngine3D
  Height = 10
  Length = 3
  Placement = pos=(3.3,4,50) rot=(0,0,1;0rad)
  Width = 10
FEATURE [Part::Fillet] Fillet045
  Base = -> Box032
  Edges = 1 edges r=2: [Edge12]
FEATURE [Part::Box] Box033  label="Cube020"
  AttacherType = Attacher::AttachEngine3D
  Height = 28
  Length = 4
  Placement = pos=(5,0,22) rot=(0,0,1;0rad)
  Width = 10
FEATURE [Part::Fillet] Fillet046
  Base = -> Box033
  Edges = 1 edges r=1: [Edge7]
FEATURE [Part::Fillet] Fillet047
  Base = -> Fillet046
  Edges = 1 edges r=2: [Edge5]
FEATURE [Part::Fillet] Fillet048
  Base = -> Fillet047
  Edges = 1 edges r=2: [Edge2]
FEATURE [Part::Cylinder] Cylinder050
  Angle = 360
  AttacherType = Attacher::AttachEngine3D
  Height = 20
  Placement = pos=(0,0,36.15) rot=(0,0,1;0rad)
  Radius = 8.2
FEATURE [Part::Cylinder] Cylinder051
  Angle = 360
  AttacherType = Attacher::AttachEngine3D
  Height = 10
  Placement = pos=(0,0,36.15) rot=(0,0,1;0rad)
  Radius = 4
FEATURE [Part::MultiFuse] Fusion120  label="removeToCreteHoleForPlugHousing043"
  Placement = pos=(-42,19,36) rot=(0,1,0;1.5708rad)
  Shapes = -> [Cylinder050,Cylinder051]
FEATURE [Sketcher::SketchObject] Sketch067  label="topSketch018"
  FullyConstrained = true
  sketch-geometry (4):
    g0: LineSegment StartX=16.8446 StartY=31.512 StartZ=0 EndX=16.3251 EndY=34.4666 EndZ=0
    g1: ArcOfCircle CenterX=19 CenterY=19.2524 CenterZ=0 NormalX=0 NormalY=0 NormalZ=1 AngleXU=0 Radius=15.4476 StartAngle=1.74483 EndAngle=2.72717
    g2: ArcOfCircle CenterX=19 CenterY=19.2524 CenterZ=0 NormalX=0 NormalY=0 NormalZ=1 AngleXU=0 Radius=12.4476 StartAngle=1.74483 EndAngle=2.73189
    g3: LineSegment StartX=4.86004 StartY=25.4725 StartZ=0 EndX=7.58253 EndY=24.2107 EndZ=0
  constraints (7):
    c: Block(g0)
    c: Coincident(g1,g0)
    c: Coincident(g2,g0)
    c: Coincident(g3,g1)
    c: Coincident(g3,g2)
    c: Block(g1)
    c: Block(g2)
FEATURE [Part::Extrusion] Extrude058
  Base = -> Sketch067
  Dir = (0,0,1)
  DirMode = 2
  FaceMakerClass = Part::FaceMakerBullseye
  LengthFwd = 10
  LengthRev = 0
  Placement = pos=(0,0,31) rot=(0,0,1;0rad)
  Solid = true
  Symmetric = false
FEATURE [Part::Cut] Cut051
  Base = -> Extrude058
  Tool = -> Fusion120
FEATURE [Part::Fillet] Fillet049
  Base = -> Cut051
  Edges = 1 edges r=2: [Edge1]
FEATURE [Part::Fillet] Fillet050
  Base = -> Fillet049
  Edges = 1 edges r=2.5: [Edge1]
FEATURE [Part::Fillet] Fillet051
  Base = -> Fillet050
  Edges = 1 edges r=2.5: [Edge2]
FEATURE [Part::MultiFuse] Fusion121  label="wireHolder003"
  Shapes = -> [Fusion116,Fillet051]
FEATURE [Part::MultiFuse] Fusion122
  Shapes = -> [Fillet045,Fusion121]
FEATURE [Part::MultiFuse] Fusion123  label="wireHolder004"
  Shapes = -> [Fusion122,Fillet048]
FEATURE [Part::MultiFuse] Fusion124  label="wireHolder005"
  Shapes = -> [Fillet044,Fusion119,Fusion123]
FEATURE [Sketcher::SketchObject] Sketch068  label="topSketch019"
  FullyConstrained = true
  sketch-geometry (6):
    g0: LineSegment StartX=19 StartY=38 StartZ=0 EndX=117 EndY=38 EndZ=0
    g1: ArcOfCircle CenterX=19 CenterY=19 CenterZ=0 NormalX=0 NormalY=0 NormalZ=1 AngleXU=0 Radius=19 StartAngle=1.5708 EndAngle=3.14159
    g2: LineSegment StartX=117 StartY=38 StartZ=0 EndX=117 EndY=19 EndZ=0
    g3: LineSegment StartX=98 StartY=1.0161e-12 StartZ=0 EndX=5.22862e-06 EndY=1.0161e-12 EndZ=0
    g4: LineSegment StartX=5.22862e-06 StartY=19 StartZ=0 EndX=5.22862e-06 EndY=1.0161e-12 EndZ=0
    g5: ArcOfCircle CenterX=98 CenterY=19 CenterZ=0 NormalX=0 NormalY=0 NormalZ=1 AngleXU=0 Radius=19 StartAngle=4.71239 EndAngle=6.28319
  constraints (16):
    c: Horizontal(g0)
    c: Distance(g0) = 98
    c: Coincident(g1,g0)
    c: Block(g1)
    c: Coincident(g2,g0)
    c: Vertical(g2)
    c: Distance(g2) = 19
    c: Horizontal(g3)
    c: Coincident(g4,g1)
    c: Vertical(g4)
    c: Coincident(g3,g4)
    c: Block(g3)
    c: Coincident(g5,g2)
    c: Coincident(g5,g3)
    c: Block(g0)
    c: Block(g5)
FEATURE [Part::Extrusion] Extrude059  label="sideA002"
  Base = -> Sketch068
  Dir = (0,0,1)
  DirMode = 2
  FaceMakerClass = Part::FaceMakerBullseye
  LengthFwd = 3
  LengthRev = 0
  Placement = pos=(0,0,-2.7) rot=(0,0,1;0rad)
  Solid = true
  Symmetric = false
FEATURE [Sketcher::SketchObject] Sketch069  label="topSketch020"
  FullyConstrained = true
  sketch-geometry (6):
    g0: LineSegment StartX=19 StartY=38 StartZ=0 EndX=117 EndY=38 EndZ=0
    g1: ArcOfCircle CenterX=19 CenterY=19 CenterZ=0 NormalX=0 NormalY=0 NormalZ=1 AngleXU=0 Radius=19 StartAngle=1.5708 EndAngle=3.14159
    g2: LineSegment StartX=117 StartY=38 StartZ=0 EndX=117 EndY=19 EndZ=0
    g3: LineSegment StartX=98 StartY=1.0161e-12 StartZ=0 EndX=5.22862e-06 EndY=1.0161e-12 EndZ=0
    g4: LineSegment StartX=5.22862e-06 StartY=19 StartZ=0 EndX=5.22862e-06 EndY=1.0161e-12 EndZ=0
    g5: ArcOfCircle CenterX=98 CenterY=19 CenterZ=0 NormalX=0 NormalY=0 NormalZ=1 AngleXU=0 Radius=19 StartAngle=4.71239 EndAngle=6.28319
  constraints (16):
    c: Horizontal(g0)
    c: Distance(g0) = 98
    c: Coincident(g1,g0)
    c: Block(g1)
    c: Coincident(g2,g0)
    c: Vertical(g2)
    c: Distance(g2) = 19
    c: Horizontal(g3)
    c: Coincident(g4,g1)
    c: Vertical(g4)
    c: Coincident(g3,g4)
    c: Block(g3)
    c: Coincident(g5,g2)
    c: Coincident(g5,g3)
    c: Block(g0)
    c: Block(g5)
FEATURE [Part::Extrusion] Extrude060  label="sideB002"
  Base = -> Sketch069
  Dir = (0,0,1)
  DirMode = 2
  FaceMakerClass = Part::FaceMakerBullseye
  LengthFwd = 3
  LengthRev = 0
  Placement = pos=(0,0,71.7) rot=(0,0,1;0rad)
  Solid = true
  Symmetric = false
FEATURE [Part::MultiFuse] Fusion127  label="removeFromBottom001"
  Placement = pos=(2,0,0) rot=(0,0,1;0rad)
  Shapes = -> [Extrude059,Extrude060]
FEATURE [Part::Cylinder] Cylinder052
  Angle = 360
  AttacherType = Attacher::AttachEngine3D
  Height = 20
  Placement = pos=(0,0,36.15) rot=(0,0,1;0rad)
  Radius = 14
FEATURE [Part::Cylinder] Cylinder053
  Angle = 360
  AttacherType = Attacher::AttachEngine3D
  Height = 10
  Placement = pos=(0,0,36.15) rot=(0,0,1;0rad)
  Radius = 4
FEATURE [Part::MultiFuse] Fusion128  label="removeToCreteHoleForPlugHousing044"
  Placement = pos=(70,19,36) rot=(0,1,0;1.5708rad)
  Shapes = -> [Cylinder052,Cylinder053]
FEATURE [Part::Cut] Cut052  label="bottom011"
  Base = -> Extrude043
  Tool = -> Fusion128
FEATURE [Part::Cut] Cut054  label="bottom012"
  Base = -> Cut052
  Tool = -> Fusion115
FEATURE [Sketcher::SketchObject] Sketch070
  FullyConstrained = true
  Placement = pos=(117,19,0) rot=(0.57735,0.57735,0.57735;2.0944rad)
  sketch-geometry (48):
    g0: LineSegment StartX=-49.19 StartY=69.25 StartZ=0 EndX=-49.19 EndY=66.25 EndZ=0
    g1: LineSegment StartX=-49.19 StartY=63.5 StartZ=0 EndX=-49.19 EndY=60.5 EndZ=0
    g2: LineSegment StartX=-49.19 StartY=57.75 StartZ=0 EndX=-49.19 EndY=54.75 EndZ=0
    g3: LineSegment StartX=-49.19 StartY=52 StartZ=0 EndX=-49.19 EndY=49 EndZ=0
    g4: LineSegment StartX=-49.19 StartY=46.25 StartZ=0 EndX=-49.19 EndY=43.25 EndZ=0
    g5: LineSegment StartX=-49.19 StartY=40.5 StartZ=0 EndX=-49.19 EndY=37.5 EndZ=0
    g6: LineSegment StartX=-49.19 StartY=34.5 StartZ=0 EndX=-49.19 EndY=31.5 EndZ=0
    g7: LineSegment StartX=-49.19 StartY=28.75 StartZ=0 EndX=-49.19 EndY=25.75 EndZ=0
    g8: LineSegment StartX=-49.19 StartY=23 StartZ=0 EndX=-49.19 EndY=20 EndZ=0
    g9: LineSegment StartX=-49.19 StartY=17.25 StartZ=0 EndX=-49.19 EndY=14.25 EndZ=0
    g10: LineSegment StartX=-49.19 StartY=11.5 StartZ=0 EndX=-49.19 EndY=8.5 EndZ=0
    g11: LineSegment StartX=-49.19 StartY=5.75 StartZ=0 EndX=-49.19 EndY=2.75 EndZ=0
    g12: ArcOfCircle CenterX=-1.5 CenterY=67.75 CenterZ=0 NormalX=0 NormalY=0 NormalZ=1 AngleXU=0 Radius=1.5 StartAngle=4.71239 EndAngle=7.85398
    g13: ArcOfCircle CenterX=-1.5 CenterY=62 CenterZ=0 NormalX=0 NormalY=0 NormalZ=1 AngleXU=0 Radius=1.5 StartAngle=4.71239 EndAngle=7.85398
    g14: ArcOfCircle CenterX=-1.5 CenterY=56.25 CenterZ=0 NormalX=0 NormalY=0 NormalZ=1 AngleXU=0 Radius=1.5 StartAngle=4.71239 EndAngle=7.85398
    g15: ArcOfCircle CenterX=-11.49 CenterY=50.5 CenterZ=0 NormalX=0 NormalY=0 NormalZ=1 AngleXU=0 Radius=1.5 StartAngle=4.71239 EndAngle=7.85398
    g16: ArcOfCircle CenterX=-16.28 CenterY=44.75 CenterZ=0 NormalX=0 NormalY=0 NormalZ=1 AngleXU=0 Radius=1.5 StartAngle=4.71239 EndAngle=7.85398
    g17: ArcOfCircle CenterX=-18.2337 CenterY=39 CenterZ=0 NormalX=0 NormalY=0 NormalZ=1 AngleXU=0 Radius=1.5 StartAngle=4.71485 EndAngle=7.85398
    g18: ArcOfCircle CenterX=-16.2837 CenterY=27.25 CenterZ=0 NormalX=0 NormalY=0 NormalZ=1 AngleXU=0 Radius=1.5 StartAngle=4.71485 EndAngle=7.85398
    g19: ArcOfCircle CenterX=-18.2337 CenterY=33 CenterZ=0 NormalX=0 NormalY=0 NormalZ=1 AngleXU=0 Radius=1.5 StartAngle=4.71485 EndAngle=7.85398
    g20: ArcOfCircle CenterX=-11.49 CenterY=21.5 CenterZ=0 NormalX=0 NormalY=0 NormalZ=1 AngleXU=0 Radius=1.5 StartAngle=4.71239 EndAngle=7.85398
    g21: ArcOfCircle CenterX=-1.5 CenterY=4.25 CenterZ=0 NormalX=0 NormalY=0 NormalZ=1 AngleXU=0 Radius=1.5 StartAngle=4.71239 EndAngle=7.85398
    g22: ArcOfCircle CenterX=-1.5 CenterY=10 CenterZ=0 NormalX=0 NormalY=0 NormalZ=1 AngleXU=0 Radius=1.5 StartAngle=4.71239 EndAngle=7.85398
    g23: ArcOfCircle CenterX=-1.5 CenterY=15.75 CenterZ=0 NormalX=0 NormalY=0 NormalZ=1 AngleXU=0 Radius=1.5 StartAngle=4.71239 EndAngle=7.85398
    g24: LineSegment StartX=-49.19 StartY=69.25 StartZ=0 EndX=-1.5 EndY=69.25 EndZ=0
    g25: LineSegment StartX=-49.19 StartY=66.25 StartZ=0 EndX=-1.5 EndY=66.25 EndZ=0
    g26: LineSegment StartX=-49.19 StartY=63.5 StartZ=0 EndX=-1.5 EndY=63.5 EndZ=0
    g27: LineSegment StartX=-49.19 StartY=60.5 StartZ=0 EndX=-1.5 EndY=60.5 EndZ=0
    g28: LineSegment StartX=-49.19 StartY=57.75 StartZ=0 EndX=-1.5 EndY=57.75 EndZ=0
    g29: LineSegment StartX=-49.19 StartY=54.75 StartZ=0 EndX=-1.5 EndY=54.75 EndZ=0
    g30: LineSegment StartX=-49.19 StartY=52 StartZ=0 EndX=-11.49 EndY=52 EndZ=0
    g31: LineSegment StartX=-49.19 StartY=49 StartZ=0 EndX=-11.49 EndY=49 EndZ=0
    g32: LineSegment StartX=-49.19 StartY=46.25 StartZ=0 EndX=-16.28 EndY=46.25 EndZ=0
    g33: LineSegment StartX=-49.19 StartY=43.25 StartZ=0 EndX=-16.28 EndY=43.25 EndZ=0
    g34: LineSegment StartX=-49.19 StartY=40.5 StartZ=0 EndX=-18.2337 EndY=40.5 EndZ=0
    g35: LineSegment StartX=-49.19 StartY=37.5 StartZ=0 EndX=-18.23 EndY=37.5 EndZ=0
    g36: LineSegment StartX=-49.19 StartY=34.5 StartZ=0 EndX=-18.2337 EndY=34.5 EndZ=0
    g37: LineSegment StartX=-49.19 StartY=31.5 StartZ=0 EndX=-18.23 EndY=31.5 EndZ=0
    g38: LineSegment StartX=-49.19 StartY=28.75 StartZ=0 EndX=-16.2837 EndY=28.75 EndZ=0
    g39: LineSegment StartX=-49.19 StartY=25.75 StartZ=0 EndX=-16.28 EndY=25.75 EndZ=0
    g40: LineSegment StartX=-49.19 StartY=23 StartZ=0 EndX=-11.49 EndY=23 EndZ=0
    g41: LineSegment StartX=-49.19 StartY=20 StartZ=0 EndX=-11.49 EndY=20 EndZ=0
    g42: LineSegment StartX=-49.19 StartY=17.25 StartZ=0 EndX=-1.5 EndY=17.25 EndZ=0
    g43: LineSegment StartX=-49.19 StartY=14.25 StartZ=0 EndX=-1.5 EndY=14.25 EndZ=0
    g44: LineSegment StartX=-49.19 StartY=11.5 StartZ=0 EndX=-1.5 EndY=11.5 EndZ=0
    g45: LineSegment StartX=-49.19 StartY=8.5 StartZ=0 EndX=-1.5 EndY=8.5 EndZ=0
    g46: LineSegment StartX=-49.19 StartY=5.75 StartZ=0 EndX=-1.5 EndY=5.75 EndZ=0
    g47: LineSegment StartX=-49.19 StartY=2.75 StartZ=0 EndX=-1.5 EndY=2.75 EndZ=0
  constraints (120):
    c: Vertical(g0)
    c: Distance(g0) = 3
    c: Block(g0)
    c: Vertical(g1)
    c: Distance(g1) = 3
    c: Vertical(g2)
    c: Equal(g0,g2) = 3
    c: Block(g2)
    c: Vertical(g3)
    c: Equal(g1,g3) = 3
    c: Vertical(g4)
    c: Equal(g0,g4) = 3
    c: Block(g4)
    c: Vertical(g5)
    c: Equal(g1,g5) = 3
    c: Vertical(g6)
    c: Equal(g0,g6) = 3
    c: Block(g6)
    c: Vertical(g7)
    c: Equal(g1,g7) = 3
    c: Vertical(g8)
    c: Equal(g0,g8) = 3
    c: Block(g8)
    c: Vertical(g9)
    c: Equal(g1,g9) = 3
    c: Vertical(g10)
    c: Equal(g0,g10) = 3
    c: Block(g10)
    c: Vertical(g11)
    c: Equal(g1,g11) = 3
    c: Block(g12)
    c: Block(g13)
    c: Block(g14)
    c: Block(g15)
    c: Block(g16)
    c: Block(g17)
    c: Block(g18)
    c: Block(g19)
    c: Block(g20)
    c: Block(g21)
    c: Block(g22)
    c: Block(g23)
    c: Block(g11)
    c: Block(g9)
    c: Block(g7)
    c: Block(g5)
    c: Block(g3)
    c: Block(g1)
    c: Coincident(g24,g0)
    c: Coincident(g24,g12)
    c: Horizontal(g24)
    c: Coincident(g25,g0)
    c: Coincident(g25,g12)
    c: Horizontal(g25)
    c: Coincident(g26,g1)
    c: Coincident(g26,g13)
    c: Horizontal(g26)
    c: Coincident(g27,g1)
    c: Coincident(g27,g13)
    c: Horizontal(g27)
    c: Coincident(g28,g2)
    c: Coincident(g28,g14)
    c: Horizontal(g28)
    c: Coincident(g29,g2)
    c: Coincident(g29,g14)
    c: Horizontal(g29)
    c: Coincident(g30,g3)
    c: Coincident(g30,g15)
    c: Horizontal(g30)
    c: Coincident(g31,g3)
    c: Coincident(g31,g15)
    c: Horizontal(g31)
    c: Coincident(g32,g4)
    c: Coincident(g32,g16)
    c: Horizontal(g32)
    c: Coincident(g33,g4)
    c: Coincident(g33,g16)
    c: Horizontal(g33)
    c: Coincident(g34,g5)
    c: Coincident(g34,g17)
    c: Horizontal(g34)
    c: Coincident(g35,g5)
    c: Coincident(g35,g17)
    c: Horizontal(g35)
    c: Coincident(g36,g6)
    c: Coincident(g36,g19)
    c: Horizontal(g36)
    c: Coincident(g37,g6)
    c: Coincident(g37,g19)
    c: Horizontal(g37)
    c: Coincident(g38,g7)
    c: Coincident(g38,g18)
    c: Horizontal(g38)
    c: Coincident(g39,g7)
    c: Coincident(g39,g18)
    c: Horizontal(g39)
    c: Coincident(g40,g8)
    c: Coincident(g40,g20)
    c: Horizontal(g40)
    c: Coincident(g41,g8)
    c: Coincident(g41,g20)
    c: Horizontal(g41)
    c: Coincident(g42,g9)
    c: Coincident(g42,g23)
    c: Horizontal(g42)
    c: Coincident(g43,g9)
    c: Coincident(g43,g23)
    c: Horizontal(g43)
    c: Coincident(g44,g10)
    c: Coincident(g44,g22)
    c: Horizontal(g44)
    c: Coincident(g45,g10)
    c: Coincident(g45,g22)
    c: Horizontal(g45)
    c: Coincident(g46,g11)
    c: Coincident(g46,g21)
    c: Horizontal(g46)
    c: Coincident(g47,g11)
    c: Coincident(g47,g21)
    c: Horizontal(g47)
FEATURE [Part::Extrusion] Extrude061
  Base = -> Sketch070
  Dir = (1,0,0)
  DirMode = 2
  FaceMakerClass = Part::FaceMakerBullseye
  LengthFwd = 23
  LengthRev = 0
  Placement = pos=(-19,0,0) rot=(0,0,1;0rad)
  Solid = true
  Symmetric = false
FEATURE [Part::Fillet] Fillet052  label="removeToCreateVentalationHoles002"
  Base = -> Extrude061
  Edges = <same value as first occurrence — deduplicated (x6 in doc)>
  Placement = pos=(7,0.02,0) rot=(0,0,1;0rad)
FEATURE [Part::MultiFuse] Fusion130  label="bottom013"
  Shapes = -> [Cut054,Cut034]
FEATURE [Part::Cut] Cut055
  Base = -> Fusion130
  Tool = -> Fillet052
FEATURE [Part::Cylinder] Cylinder054
  Angle = 360
  AttacherType = Attacher::AttachEngine3D
  Height = 20
  Placement = pos=(0,0,36.15) rot=(0,0,1;0rad)
  Radius = 4
FEATURE [Sketcher::SketchObject] Sketch071  label="bottomSketch002"
  FullyConstrained = true
  sketch-geometry (32):
    g0: LineSegment StartX=3.3 StartY=-6.03275e-07 StartZ=0 EndX=98 EndY=-6.03275e-07 EndZ=0
    g1: ArcOfCircle CenterX=98 CenterY=19 CenterZ=0 NormalX=0 NormalY=0 NormalZ=1 AngleXU=0 Radius=19 StartAngle=4.71239 EndAngle=5.71103
    g2: LineSegment StartX=6.3 StartY=8 StartZ=0 EndX=3.3 EndY=8 EndZ=0
    g3: LineSegment StartX=3.3 StartY=8 StartZ=0 EndX=3.3 EndY=-6.03275e-07 EndZ=0
    g4: ArcOfCircle CenterX=8.3 CenterY=5 CenterZ=0 NormalX=0 NormalY=0 NormalZ=1 AngleXU=0 Radius=2 StartAngle=3.14159 EndAngle=4.71239
    g5: LineSegment StartX=6.3 StartY=8 StartZ=0 EndX=6.3 EndY=5 EndZ=0
    g6: ArcOfCircle CenterX=98 CenterY=19 CenterZ=0 NormalX=0 NormalY=0 NormalZ=1 AngleXU=0 Radius=12.7 StartAngle=4.71239 EndAngle=6.28319
    g7: LineSegment StartX=94.7 StartY=3 StartZ=0 EndX=8.3 EndY=3 EndZ=0
    g8-g12: Circle x5 (B-spline internal-alignment scaffolding for g13; pole/knot coordinates omitted)
    g13: BSplineCurve PolesCount=5 KnotsCount=3 Degree=3 IsPeriodic=0
    g14: GeomPoint X=98 Y=6.3 Z=0
    g15: GeomPoint X=96.3938 Y=4.71946 Z=0
    g16: GeomPoint X=94.7 Y=3 Z=0
    g17-g23: Circle x7 (B-spline internal-alignment scaffolding for g24; pole/knot coordinates omitted)
    g24: BSplineCurve PolesCount=7 KnotsCount=5 Degree=3 IsPeriodic=0
    g25-g29: GeomPoint x5 (B-spline internal-alignment scaffolding for g24; pole/knot coordinates omitted)
    g30: ArcOfCircle CenterX=98 CenterY=19 CenterZ=0 NormalX=0 NormalY=0 NormalZ=1 AngleXU=0 Radius=15.7 StartAngle=5.81226 EndAngle=6.28319
    g31: LineSegment StartX=110.7 StartY=19 StartZ=0 EndX=113.7 EndY=19 EndZ=0
  constraints (41):
    c: Horizontal(g0)
    c: Coincident(g1,g0)
    c: Block(g1)
    c: Horizontal(g2)
    c: Distance(g2) = 3
    c: Coincident(g3,g2)
    c: Vertical(g3)
    c: Coincident(g3,g0)
    c: Block(g4)
    c: Block(g2)
    c: Coincident(g5,g2)
    c: Coincident(g5,g4)
    c: Vertical(g5)
    c: Coincident(g6,g1)
    c: Block(g6)
    c: Coincident(g7,g4)
    c: Horizontal(g7)
    c: Block(g0)
    c: Block(g7)
    c: Block(g3)
    c: Coincident(g13,g6)
    c: Weight(g8) = 1
    c: Equal(g8, g9-g12) x4
    c: Coincident(g13,g7)
    c: InternalAlignment(g8-g12 -> g13) x5
    c: InternalAlignment(g14,g13)
    c: InternalAlignment(g15,g13)
    c: InternalAlignment(g16,g13)
    c: Block(g13)
    c: Weight(g17) = 1
    c: Equal(g17, g18-g23) x6
    c: Coincident(g24,g1)
    c: InternalAlignment(g17-g23 -> g24) x7
    c: InternalAlignment(g25-g29 -> g24) x5
    c: Block(g24)
    c: Coincident(g30,g24)
    c: Coincident(g31,g6)
    c: Coincident(g31,g30)
    c: Horizontal(g31)
    c: Block(g31)
    c: Block(g30)
FEATURE [Part::Extrusion] Extrude062  label="bottom014"
  Base = -> Sketch071
  Dir = (0,0,1)
  DirMode = 2
  FaceMakerClass = Part::FaceMakerBullseye
  LengthFwd = 71.4
  LengthRev = 0
  Placement = pos=(0,0,0.3) rot=(0,0,1;0rad)
  Solid = true
  Symmetric = false
FEATURE [Part::Fillet] Fillet054
  Base = -> Extrude062
  Edges = 1 edges r=2.4: [Edge17]
FEATURE [Part::Fillet] Fillet055  label="bottom015"
  Base = -> Fillet054
  Edges = 1 edges r=2.4: [Edge36]
FEATURE [Part::Cylinder] Cylinder055
  Angle = 360
  AttacherType = Attacher::AttachEngine3D
  Height = 10
  Placement = pos=(0,0,36.15) rot=(0,0,1;0rad)
  Radius = 4
FEATURE [Part::MultiFuse] Fusion131  label="removeToCreateHoleForPlugHousing002"
  Placement = pos=(70,19,36.15) rot=(0,1,0;1.5708rad)
  Shapes = -> [Cylinder054,Cylinder055]
FEATURE [Part::Cut] Cut056  label="Bottom001"
  Base = -> Fillet055
  Placement = pos=(9,0,0) rot=(0,0,1;0rad)
  Tool = -> Fusion131
FEATURE [Part::Cut] Cut057
  Base = -> Cut055
  Tool = -> Cut056
FEATURE [Sketcher::SketchObject] Sketch072  label="topSketch021"
  FullyConstrained = true
  sketch-geometry (4):
    g0: ArcOfCircle CenterX=105 CenterY=19 CenterZ=0 NormalX=0 NormalY=0 NormalZ=1 AngleXU=0 Radius=20.6155 StartAngle=5.54125 EndAngle=6.28319
    g1: ArcOfCircle CenterX=105 CenterY=19 CenterZ=0 NormalX=0 NormalY=0 NormalZ=1 AngleXU=0 Radius=13 StartAngle=5.54125 EndAngle=6.28319
    g2: LineSegment StartX=118 StartY=19 StartZ=0 EndX=125.616 EndY=19 EndZ=0
    g3: LineSegment StartX=114.583 StartY=10.2157 StartZ=0 EndX=120.197 EndY=5.06982 EndZ=0
  constraints (7):
    c: Block(g0)
    c: Block(g1)
    c: Coincident(g2,g1)
    c: Coincident(g2,g0)
    c: Horizontal(g2)
    c: Coincident(g3,g1)
    c: Coincident(g3,g0)
FEATURE [Part::Extrusion] Extrude063  label="bottomPlugHousingBit003"
  Base = -> Sketch072
  Dir = (0,0,1)
  DirMode = 2
  FaceMakerClass = Part::FaceMakerBullseye
  LengthFwd = 72
  LengthRev = 0
  Solid = true
  Symmetric = false
FEATURE [Part::Cylinder] Cylinder056
  Angle = 360
  AttacherType = Attacher::AttachEngine3D
  Height = 20
  Placement = pos=(0,0,36.15) rot=(0,0,1;0rad)
  Radius = 14.3
FEATURE [Part::Cylinder] Cylinder057
  Angle = 360
  AttacherType = Attacher::AttachEngine3D
  Height = 10
  Placement = pos=(0,0,36.15) rot=(0,0,1;0rad)
  Radius = 4
FEATURE [Part::Box] Box034  label="removeToCreteHoleForPlugHousing047"
  AttacherType = Attacher::AttachEngine3D
  Height = 28.6
  Length = 20
  Placement = pos=(106.15,0,21.7) rot=(0,0,1;0rad)
  Width = 19
FEATURE [Part::Cylinder] Cylinder058
  Angle = 360
  AttacherType = Attacher::AttachEngine3D
  Height = 20
  Placement = pos=(0,0,36.15) rot=(0,0,1;0rad)
  Radius = 14.3
FEATURE [Part::Cylinder] Cylinder059
  Angle = 360
  AttacherType = Attacher::AttachEngine3D
  Height = 10
  Placement = pos=(0,0,36.15) rot=(0,0,1;0rad)
  Radius = 4
FEATURE [Part::MultiFuse] Fusion134  label="removeToCreteHoleForPlugHousing046"
  Placement = pos=(70,19,36) rot=(0,1,0;1.5708rad)
  Shapes = -> [Cylinder058,Cylinder059]
FEATURE [Part::Cylinder] Cylinder060
  Angle = 360
  AttacherType = Attacher::AttachEngine3D
  Height = 20
  Placement = pos=(0,0,36.15) rot=(0,0,1;0rad)
  Radius = 14
FEATURE [Part::Cylinder] Cylinder061
  Angle = 360
  AttacherType = Attacher::AttachEngine3D
  Height = 10
  Placement = pos=(0,0,36.15) rot=(0,0,1;0rad)
  Radius = 4
FEATURE [Part::MultiFuse] Fusion135  label="removeToCreteHoleForPlugHousing048"
  Placement = pos=(70,19,36) rot=(0,1,0;1.5708rad)
  Shapes = -> [Cylinder060,Cylinder061]
FEATURE [Part::Box] Box035  label="removeToCreteHoleForPlugHousing049"
  AttacherType = Attacher::AttachEngine3D
  Height = 28.6
  Length = 20
  Placement = pos=(106.15,0,21.7) rot=(0,0,1;0rad)
  Width = 19
FEATURE [Part::MultiFuse] Fusion133  label="removeToCreteHoleForPlugHousing045"
  Placement = pos=(0,0,-28.3) rot=(0,0,1;0rad)
  Shapes = -> [Box035,Fusion134]
FEATURE [Part::MultiFuse] Fusion138  label="removeToCreteHoleForPlugHousing051"
  Placement = pos=(70,19,36) rot=(0,1,0;1.5708rad)
  Shapes = -> [Cylinder056,Cylinder057]
FEATURE [Part::MultiFuse] Fusion137  label="removeToCreteHoleForPlugHousing050"
  Placement = pos=(0,0,28.3) rot=(0,0,1;0rad)
  Shapes = -> [Box034,Fusion138]
FEATURE [Part::MultiFuse] Fusion132  label="removeToCreatePlugHousingBottomBit002"
  Shapes = -> [Fusion133,Fusion137]
FEATURE [Part::MultiFuse] Fusion136  label="removeToCreatePlugHousingBottomBit003"
  Shapes = -> [Fusion135,Fusion132]
FEATURE [Part::Cut] Cut058  label="bottomPlugHousingBit002"
  Base = -> Extrude063
  Placement = pos=(-0.09,0,0) rot=(0,0,1;0rad)
  Tool = -> Fusion136
FEATURE [Sketcher::SketchObject] Sketch073  label="bottomSketch003"
  FullyConstrained = true
  sketch-geometry (45):
    g0: LineSegment StartX=6.29999 StartY=8 StartZ=0 EndX=3.29999 EndY=8 EndZ=0
    g1: LineSegment StartX=3.29999 StartY=8 StartZ=0 EndX=3.29999 EndY=-6.03275e-07 EndZ=0
    g2: ArcOfCircle CenterX=8.29999 CenterY=5 CenterZ=0 NormalX=0 NormalY=0 NormalZ=1 AngleXU=0 Radius=2 StartAngle=3.14159 EndAngle=4.71239
    g3: LineSegment StartX=6.29999 StartY=8 StartZ=0 EndX=6.29999 EndY=5 EndZ=0
    g4: ArcOfCircle CenterX=105 CenterY=19 CenterZ=0 NormalX=0 NormalY=0 NormalZ=1 AngleXU=0 Radius=12.7 StartAngle=4.71239 EndAngle=5.94289
    g5-g11: Circle x7 (B-spline internal-alignment scaffolding for g12; pole/knot coordinates omitted)
    g12: BSplineCurve PolesCount=7 KnotsCount=5 Degree=3 IsPeriodic=0
    g13-g17: GeomPoint x5 (B-spline internal-alignment scaffolding for g12; pole/knot coordinates omitted)
    g18: ArcOfCircle CenterX=105 CenterY=19 CenterZ=0 NormalX=0 NormalY=0 NormalZ=1 AngleXU=0 Radius=15.7 StartAngle=5.81226 EndAngle=6.28319
    g19: BSplineCurve PolesCount=5 KnotsCount=3 Degree=3 IsPeriodic=0
    g20: LineSegment StartX=8.29999 StartY=3 StartZ=0 EndX=101.7 EndY=3 EndZ=0
    g21: LineSegment StartX=3.29999 StartY=-6.03275e-07 StartZ=0 EndX=105 EndY=-6.03275e-07 EndZ=0
    g22: LineSegment StartX=120.974 StartY=8.71251 StartZ=0 EndX=122.332 EndY=7.83778 EndZ=0
    g23: LineSegment StartX=105 StartY=-6.03274e-07 StartZ=0 EndX=113 EndY=-6.03274e-07 EndZ=0
    g24: ArcOfCircle CenterX=105 CenterY=19 CenterZ=0 NormalX=0 NormalY=0 NormalZ=1 AngleXU=0 Radius=20.6155 StartAngle=5.11091 EndAngle=5.71103
    g25: ArcOfCircle CenterX=117.7 CenterY=19 CenterZ=0 NormalX=0 NormalY=0 NormalZ=1 AngleXU=0 Radius=3 StartAngle=1.2e-15 EndAngle=2.10468
    g26: Circle CenterX=116.345 CenterY=16.3232 CenterZ=0 NormalX=0 NormalY=0 NormalZ=1 AngleXU=0 Radius=1
    g27: Circle CenterX=117.24 CenterY=15.7584 CenterZ=0 NormalX=0 NormalY=0 NormalZ=1 AngleXU=0 Radius=1
    g28: Circle CenterX=116.972 CenterY=14.7612 CenterZ=0 NormalX=0 NormalY=0 NormalZ=1 AngleXU=0 Radius=1
    g29: BSplineCurve PolesCount=3 KnotsCount=2 Degree=2 IsPeriodic=0
    g30: GeomPoint X=116.345 Y=16.3232 Z=0
    g31: GeomPoint X=116.972 Y=14.7612 Z=0
    g32: Circle CenterX=115.828 CenterY=17.157 CenterZ=0 NormalX=0 NormalY=0 NormalZ=1 AngleXU=0 Radius=1
    g33: Circle CenterX=115.841 CenterY=16.639 CenterZ=0 NormalX=0 NormalY=0 NormalZ=1 AngleXU=0 Radius=1
    g34: Circle CenterX=116.345 CenterY=16.3232 CenterZ=0 NormalX=0 NormalY=0 NormalZ=1 AngleXU=0 Radius=1
    g35: BSplineCurve PolesCount=3 KnotsCount=2 Degree=2 IsPeriodic=0
    g36: GeomPoint X=115.828 Y=17.157 Z=0
    g37: GeomPoint X=116.345 Y=16.3232 Z=0
    g38: LineSegment StartX=115.828 StartY=17.157 StartZ=0 EndX=115.828 EndY=20.8307 EndZ=0
    g39: Circle CenterX=115.828 CenterY=20.8307 CenterZ=0 NormalX=0 NormalY=0 NormalZ=1 AngleXU=0 Radius=1
    g40: Circle CenterX=115.831 CenterY=21.3396 CenterZ=0 NormalX=0 NormalY=0 NormalZ=1 AngleXU=0 Radius=1
    g41: Circle CenterX=116.173 CenterY=21.5825 CenterZ=0 NormalX=0 NormalY=0 NormalZ=1 AngleXU=0 Radius=1
    g42: BSplineCurve PolesCount=3 KnotsCount=2 Degree=2 IsPeriodic=0
    g43: GeomPoint X=115.828 Y=20.8307 Z=0
    g44: GeomPoint X=116.173 Y=21.5825 Z=0
  constraints (70):
    c: Horizontal(g0)
    c: Distance(g0) = 3
    c: Coincident(g1,g0)
    c: Vertical(g1)
    c: Block(g2)
    c: Block(g0)
    c: Coincident(g3,g0)
    c: Coincident(g3,g2)
    c: Vertical(g3)
    c: Block(g1)
    c: Block(g4)
    c: Coincident(g19,g4)
    c: Block(g19)
    c: Equal(g5, g6-g11) x6
    c: InternalAlignment(g5-g11 -> g12) x7
    c: InternalAlignment(g13-g17 -> g12) x5
    c: Block(g12)
    c: Coincident(g18,g12)
    c: Block(g18)
    c: Coincident(g20,g2)
    c: Coincident(g20,g19)
    c: Horizontal(g20)
    c: Distance(g20) = 93.4
    c: Coincident(g21,g1)
    c: Horizontal(g21)
    c: Distance(g21) = 101.7
    c: Horizontal(g23)
    c: Distance(g23) = 8
    c: Coincident(g24,g23)
    c: Block(g23)
    c: Coincident(g22,g24)
    c: Block(g24)
    c: Block(g22)
    c: Distance(g22) = 1.61553
    c: Coincident(g25,g18)
    c: Block(g25)
    c: Weight(g26) = 1
    c: Equal(g26,g27)
    c: Equal(g26,g28)
    c: Coincident(g29,g4)
    c: InternalAlignment(g26,g29)
    c: InternalAlignment(g27,g29)
    c: InternalAlignment(g28,g29)
    c: InternalAlignment(g30,g29)
    c: InternalAlignment(g31,g29)
    c: Block(g29)
    c: Weight(g32) = 1
    c: Equal(g32,g33)
    c: Equal(g32,g34)
    c: Coincident(g35,g29)
    c: InternalAlignment(g32,g35)
    c: InternalAlignment(g33,g35)
    c: InternalAlignment(g34,g35)
    c: InternalAlignment(g36,g35)
    c: InternalAlignment(g37,g35)
    c: Block(g35)
    c: Coincident(g38,g35)
    c: Vertical(g38)
    c: Block(g38)
    c: Coincident(g42,g38)
    c: Weight(g39) = 1
    c: Equal(g39,g40)
    c: Equal(g39,g41)
    c: Coincident(g42,g25)
    c: InternalAlignment(g39,g42)
    c: InternalAlignment(g40,g42)
    c: InternalAlignment(g41,g42)
    c: InternalAlignment(g43,g42)
    c: InternalAlignment(g44,g42)
    c: Block(g42)
FEATURE [Part::Extrusion] Extrude064  label="bottom016"
  Base = -> Sketch073
  Dir = (0,0,1)
  DirMode = 2
  FaceMakerClass = Part::FaceMakerBullseye
  LengthFwd = 71.4
  LengthRev = 0
  Placement = pos=(0,0,0.3) rot=(0,0,1;0rad)
  Solid = true
  Symmetric = false
FEATURE [Part::Revolution] Revolve157  label="removeToCreateScrewAndThreadedInsertHole063"
  Angle = 360
  Axis = (0,1,0)
  Base = (0,0,0)
  FaceMakerClass = Part::FaceMakerBullseye
  Placement = pos=(12.5,0,10) rot=(0,0,1;0rad)
  Solid = false
  Source = -> Face141
  Symmetric = false
FEATURE [Sketcher::SketchObject] Sketch074
  FullyConstrained = true
  Placement = pos=(117,19,0) rot=(0.57735,0.57735,0.57735;2.0944rad)
  sketch-geometry (48):
    g0: LineSegment StartX=-49.19 StartY=69.25 StartZ=0 EndX=-49.19 EndY=66.25 EndZ=0
    g1: LineSegment StartX=-49.19 StartY=63.5 StartZ=0 EndX=-49.19 EndY=60.5 EndZ=0
    g2: LineSegment StartX=-49.19 StartY=57.75 StartZ=0 EndX=-49.19 EndY=54.75 EndZ=0
    g3: LineSegment StartX=-49.19 StartY=52 StartZ=0 EndX=-49.19 EndY=49 EndZ=0
    g4: LineSegment StartX=-49.19 StartY=46.25 StartZ=0 EndX=-49.19 EndY=43.25 EndZ=0
    g5: LineSegment StartX=-49.19 StartY=40.5 StartZ=0 EndX=-49.19 EndY=37.5 EndZ=0
    g6: LineSegment StartX=-49.19 StartY=34.5 StartZ=0 EndX=-49.19 EndY=31.5 EndZ=0
    g7: LineSegment StartX=-49.19 StartY=28.75 StartZ=0 EndX=-49.19 EndY=25.75 EndZ=0
    g8: LineSegment StartX=-49.19 StartY=23 StartZ=0 EndX=-49.19 EndY=20 EndZ=0
    g9: LineSegment StartX=-49.19 StartY=17.25 StartZ=0 EndX=-49.19 EndY=14.25 EndZ=0
    g10: LineSegment StartX=-49.19 StartY=11.5 StartZ=0 EndX=-49.19 EndY=8.5 EndZ=0
    g11: LineSegment StartX=-49.19 StartY=5.75 StartZ=0 EndX=-49.19 EndY=2.75 EndZ=0
    g12: ArcOfCircle CenterX=-1.5 CenterY=67.75 CenterZ=0 NormalX=0 NormalY=0 NormalZ=1 AngleXU=0 Radius=1.5 StartAngle=4.71239 EndAngle=7.85398
    g13: ArcOfCircle CenterX=-1.5 CenterY=62 CenterZ=0 NormalX=0 NormalY=0 NormalZ=1 AngleXU=0 Radius=1.5 StartAngle=4.71239 EndAngle=7.85398
    g14: ArcOfCircle CenterX=-1.5 CenterY=56.25 CenterZ=0 NormalX=0 NormalY=0 NormalZ=1 AngleXU=0 Radius=1.5 StartAngle=4.71239 EndAngle=7.85398
    g15: ArcOfCircle CenterX=-11.49 CenterY=50.5 CenterZ=0 NormalX=0 NormalY=0 NormalZ=1 AngleXU=0 Radius=1.5 StartAngle=4.71239 EndAngle=7.85398
    g16: ArcOfCircle CenterX=-16.28 CenterY=44.75 CenterZ=0 NormalX=0 NormalY=0 NormalZ=1 AngleXU=0 Radius=1.5 StartAngle=4.71239 EndAngle=7.85398
    g17: ArcOfCircle CenterX=-18.2337 CenterY=39 CenterZ=0 NormalX=0 NormalY=0 NormalZ=1 AngleXU=0 Radius=1.5 StartAngle=4.71485 EndAngle=7.85398
    g18: ArcOfCircle CenterX=-16.2837 CenterY=27.25 CenterZ=0 NormalX=0 NormalY=0 NormalZ=1 AngleXU=0 Radius=1.5 StartAngle=4.71485 EndAngle=7.85398
    g19: ArcOfCircle CenterX=-18.2337 CenterY=33 CenterZ=0 NormalX=0 NormalY=0 NormalZ=1 AngleXU=0 Radius=1.5 StartAngle=4.71485 EndAngle=7.85398
    g20: ArcOfCircle CenterX=-11.49 CenterY=21.5 CenterZ=0 NormalX=0 NormalY=0 NormalZ=1 AngleXU=0 Radius=1.5 StartAngle=4.71239 EndAngle=7.85398
    g21: ArcOfCircle CenterX=-1.5 CenterY=4.25 CenterZ=0 NormalX=0 NormalY=0 NormalZ=1 AngleXU=0 Radius=1.5 StartAngle=4.71239 EndAngle=7.85398
    g22: ArcOfCircle CenterX=-1.5 CenterY=10 CenterZ=0 NormalX=0 NormalY=0 NormalZ=1 AngleXU=0 Radius=1.5 StartAngle=4.71239 EndAngle=7.85398
    g23: ArcOfCircle CenterX=-1.5 CenterY=15.75 CenterZ=0 NormalX=0 NormalY=0 NormalZ=1 AngleXU=0 Radius=1.5 StartAngle=4.71239 EndAngle=7.85398
    g24: LineSegment StartX=-49.19 StartY=69.25 StartZ=0 EndX=-1.5 EndY=69.25 EndZ=0
    g25: LineSegment StartX=-49.19 StartY=66.25 StartZ=0 EndX=-1.5 EndY=66.25 EndZ=0
    g26: LineSegment StartX=-49.19 StartY=63.5 StartZ=0 EndX=-1.5 EndY=63.5 EndZ=0
    g27: LineSegment StartX=-49.19 StartY=60.5 StartZ=0 EndX=-1.5 EndY=60.5 EndZ=0
    g28: LineSegment StartX=-49.19 StartY=57.75 StartZ=0 EndX=-1.5 EndY=57.75 EndZ=0
    g29: LineSegment StartX=-49.19 StartY=54.75 StartZ=0 EndX=-1.5 EndY=54.75 EndZ=0
    g30: LineSegment StartX=-49.19 StartY=52 StartZ=0 EndX=-11.49 EndY=52 EndZ=0
    g31: LineSegment StartX=-49.19 StartY=49 StartZ=0 EndX=-11.49 EndY=49 EndZ=0
    g32: LineSegment StartX=-49.19 StartY=46.25 StartZ=0 EndX=-16.28 EndY=46.25 EndZ=0
    g33: LineSegment StartX=-49.19 StartY=43.25 StartZ=0 EndX=-16.28 EndY=43.25 EndZ=0
    g34: LineSegment StartX=-49.19 StartY=40.5 StartZ=0 EndX=-18.2337 EndY=40.5 EndZ=0
    g35: LineSegment StartX=-49.19 StartY=37.5 StartZ=0 EndX=-18.23 EndY=37.5 EndZ=0
    g36: LineSegment StartX=-49.19 StartY=34.5 StartZ=0 EndX=-18.2337 EndY=34.5 EndZ=0
    g37: LineSegment StartX=-49.19 StartY=31.5 StartZ=0 EndX=-18.23 EndY=31.5 EndZ=0
    g38: LineSegment StartX=-49.19 StartY=28.75 StartZ=0 EndX=-16.2837 EndY=28.75 EndZ=0
    g39: LineSegment StartX=-49.19 StartY=25.75 StartZ=0 EndX=-16.28 EndY=25.75 EndZ=0
    g40: LineSegment StartX=-49.19 StartY=23 StartZ=0 EndX=-11.49 EndY=23 EndZ=0
    g41: LineSegment StartX=-49.19 StartY=20 StartZ=0 EndX=-11.49 EndY=20 EndZ=0
    g42: LineSegment StartX=-49.19 StartY=17.25 StartZ=0 EndX=-1.5 EndY=17.25 EndZ=0
    g43: LineSegment StartX=-49.19 StartY=14.25 StartZ=0 EndX=-1.5 EndY=14.25 EndZ=0
    g44: LineSegment StartX=-49.19 StartY=11.5 StartZ=0 EndX=-1.5 EndY=11.5 EndZ=0
    g45: LineSegment StartX=-49.19 StartY=8.5 StartZ=0 EndX=-1.5 EndY=8.5 EndZ=0
    g46: LineSegment StartX=-49.19 StartY=5.75 StartZ=0 EndX=-1.5 EndY=5.75 EndZ=0
    g47: LineSegment StartX=-49.19 StartY=2.75 StartZ=0 EndX=-1.5 EndY=2.75 EndZ=0
  constraints (120):
    c: Vertical(g0)
    c: Distance(g0) = 3
    c: Block(g0)
    c: Vertical(g1)
    c: Distance(g1) = 3
    c: Vertical(g2)
    c: Equal(g0,g2) = 3
    c: Block(g2)
    c: Vertical(g3)
    c: Equal(g1,g3) = 3
    c: Vertical(g4)
    c: Equal(g0,g4) = 3
    c: Block(g4)
    c: Vertical(g5)
    c: Equal(g1,g5) = 3
    c: Vertical(g6)
    c: Equal(g0,g6) = 3
    c: Block(g6)
    c: Vertical(g7)
    c: Equal(g1,g7) = 3
    c: Vertical(g8)
    c: Equal(g0,g8) = 3
    c: Block(g8)
    c: Vertical(g9)
    c: Equal(g1,g9) = 3
    c: Vertical(g10)
    c: Equal(g0,g10) = 3
    c: Block(g10)
    c: Vertical(g11)
    c: Equal(g1,g11) = 3
    c: Block(g12)
    c: Block(g13)
    c: Block(g14)
    c: Block(g15)
    c: Block(g16)
    c: Block(g17)
    c: Block(g18)
    c: Block(g19)
    c: Block(g20)
    c: Block(g21)
    c: Block(g22)
    c: Block(g23)
    c: Block(g11)
    c: Block(g9)
    c: Block(g7)
    c: Block(g5)
    c: Block(g3)
    c: Block(g1)
    c: Coincident(g24,g0)
    c: Coincident(g24,g12)
    c: Horizontal(g24)
    c: Coincident(g25,g0)
    c: Coincident(g25,g12)
    c: Horizontal(g25)
    c: Coincident(g26,g1)
    c: Coincident(g26,g13)
    c: Horizontal(g26)
    c: Coincident(g27,g1)
    c: Coincident(g27,g13)
    c: Horizontal(g27)
    c: Coincident(g28,g2)
    c: Coincident(g28,g14)
    c: Horizontal(g28)
    c: Coincident(g29,g2)
    c: Coincident(g29,g14)
    c: Horizontal(g29)
    c: Coincident(g30,g3)
    c: Coincident(g30,g15)
    c: Horizontal(g30)
    c: Coincident(g31,g3)
    c: Coincident(g31,g15)
    c: Horizontal(g31)
    c: Coincident(g32,g4)
    c: Coincident(g32,g16)
    c: Horizontal(g32)
    c: Coincident(g33,g4)
    c: Coincident(g33,g16)
    c: Horizontal(g33)
    c: Coincident(g34,g5)
    c: Coincident(g34,g17)
    c: Horizontal(g34)
    c: Coincident(g35,g5)
    c: Coincident(g35,g17)
    c: Horizontal(g35)
    c: Coincident(g36,g6)
    c: Coincident(g36,g19)
    c: Horizontal(g36)
    c: Coincident(g37,g6)
    c: Coincident(g37,g19)
    c: Horizontal(g37)
    c: Coincident(g38,g7)
    c: Coincident(g38,g18)
    c: Horizontal(g38)
    c: Coincident(g39,g7)
    c: Coincident(g39,g18)
    c: Horizontal(g39)
    c: Coincident(g40,g8)
    c: Coincident(g40,g20)
    c: Horizontal(g40)
    c: Coincident(g41,g8)
    c: Coincident(g41,g20)
    c: Horizontal(g41)
    c: Coincident(g42,g9)
    c: Coincident(g42,g23)
    c: Horizontal(g42)
    c: Coincident(g43,g9)
    c: Coincident(g43,g23)
    c: Horizontal(g43)
    c: Coincident(g44,g10)
    c: Coincident(g44,g22)
    c: Horizontal(g44)
    c: Coincident(g45,g10)
    c: Coincident(g45,g22)
    c: Horizontal(g45)
    c: Coincident(g46,g11)
    c: Coincident(g46,g21)
    c: Horizontal(g46)
    c: Coincident(g47,g11)
    c: Coincident(g47,g21)
    c: Horizontal(g47)
FEATURE [Part::Extrusion] Extrude065
  Base = -> Sketch074
  Dir = (1,0,0)
  DirMode = 2
  FaceMakerClass = Part::FaceMakerBullseye
  LengthFwd = 23
  LengthRev = 0
  Placement = pos=(-19,0,0) rot=(0,0,1;0rad)
  Solid = true
  Symmetric = false
FEATURE [Part::Fillet] Fillet056  label="removeToCreateVentalationHoles003"
  Base = -> Extrude065
  Edges = <same value as first occurrence — deduplicated (x6 in doc)>
  Placement = pos=(7,0.02,0) rot=(0,0,1;0rad)
FEATURE [Part::Revolution] Revolve158  label="removeToCreateScrewAndThreadedInsertHole065"
  Angle = 360
  Axis = (0,1,0)
  Base = (0,0,0)
  FaceMakerClass = Part::FaceMakerBullseye
  Placement = pos=(12.5,0,62) rot=(0,0,1;0rad)
  Solid = false
  Source = -> Face146
  Symmetric = false
FEATURE [Part::Revolution] Revolve159  label="removeToCreateScrewAndThreadedInsertHole066"
  Angle = 360
  Axis = (0,1,0)
  Base = (0,0,0)
  FaceMakerClass = Part::FaceMakerBullseye
  Placement = pos=(89.5,0,68.5) rot=(0,0,1;0rad)
  Solid = false
  Source = -> Face143
  Symmetric = false
FEATURE [Part::Revolution] Revolve160  label="removeToCreateScrewAndThreadedInsertHole067"
  Angle = 360
  Axis = (0,1,0)
  Base = (0,0,0)
  FaceMakerClass = Part::FaceMakerBullseye
  Placement = pos=(89.5,0,3.5) rot=(0,0,1;0rad)
  Solid = false
  Source = -> Face142
  Symmetric = false
FEATURE [Part::Revolution] Revolve161  label="removeToCreateScrewAndThreadedInsertHole068"
  Angle = 360
  Axis = (0,1,0)
  Base = (0,0,0)
  FaceMakerClass = Part::FaceMakerBullseye
  Placement = pos=(109.5,4.7,3.5) rot=(0,0,1;0rad)
  Solid = false
  Source = -> Face145
  Symmetric = false
FEATURE [Part::Revolution] Revolve162  label="removeToCreateScrewAndThreadedInsertHole069"
  Angle = 360
  Axis = (0,1,0)
  Base = (0,0,0)
  FaceMakerClass = Part::FaceMakerBullseye
  Placement = pos=(109.5,4.7,68.5) rot=(0,0,1;0rad)
  Solid = false
  Source = -> Face144
  Symmetric = false
FEATURE [Part::MultiFuse] Fusion141  label="removeToCreateScrewAndThreadedInsertHole064"
  Shapes = -> [Revolve162,Revolve161,Revolve160,Revolve159,Revolve158,Revolve157]
FEATURE [Part::Cylinder] Cylinder062
  Angle = 360
  AttacherType = Attacher::AttachEngine3D
  Height = 20
  Placement = pos=(0,0,36.15) rot=(0,0,1;0rad)
  Radius = 14
FEATURE [Part::Cylinder] Cylinder063
  Angle = 360
  AttacherType = Attacher::AttachEngine3D
  Height = 10
  Placement = pos=(0,0,36.15) rot=(0,0,1;0rad)
  Radius = 4
FEATURE [Part::MultiFuse] Fusion139  label="removeToCreteHoleForPlugHousing052"
  Placement = pos=(70,19,36) rot=(0,1,0;1.5708rad)
  Shapes = -> [Cylinder062,Cylinder063]
FEATURE [Part::Cut] Cut060  label="bottom017"
  Base = -> Extrude064
  Tool = -> Fusion139
FEATURE [Part::Cut] Cut061  label="bottom019"
  Base = -> Cut060
  Tool = -> Fusion141
FEATURE [Part::MultiFuse] Fusion140  label="bottom018"
  Shapes = -> [Cut061,Cut058]
FEATURE [Part::Cut] Cut059  label="bottom020"
  Base = -> Fusion140
  Tool = -> Fillet056
FEATURE [Part::Box] Box036  label="Cube021"
  AttacherType = Attacher::AttachEngine3D
  Height = 80
  Length = 26
  Placement = pos=(0,-1,-5) rot=(0,0,1;0rad)
  Width = 11
FEATURE [Part::Cut] Cut062  label="removeFromBottom002"
  Base = -> Cut057
  Tool = -> Box036
FEATURE [Part::Cut] Cut063
  Base = -> Cut059
  Tool = -> Cut062
FEATURE [Part::Cut] Cut064  label="pcbStands"
  Base = -> Fusion095
  Tool = -> Fusion127
FEATURE [Sketcher::SketchObject] Sketch075  label="topSketch022"
  FullyConstrained = true
  sketch-geometry (6):
    g0: LineSegment StartX=19 StartY=38 StartZ=0 EndX=117 EndY=38 EndZ=0
    g1: ArcOfCircle CenterX=19 CenterY=19 CenterZ=0 NormalX=0 NormalY=0 NormalZ=1 AngleXU=0 Radius=19 StartAngle=1.5708 EndAngle=3.14159
    g2: LineSegment StartX=117 StartY=38 StartZ=0 EndX=117 EndY=19 EndZ=0
    g3: LineSegment StartX=98 StartY=1.0161e-12 StartZ=0 EndX=5.22862e-06 EndY=1.0161e-12 EndZ=0
    g4: LineSegment StartX=5.22862e-06 StartY=19 StartZ=0 EndX=5.22862e-06 EndY=1.0161e-12 EndZ=0
    g5: ArcOfCircle CenterX=98 CenterY=19 CenterZ=0 NormalX=0 NormalY=0 NormalZ=1 AngleXU=0 Radius=19 StartAngle=4.71239 EndAngle=6.28319
  constraints (16):
    c: Horizontal(g0)
    c: Distance(g0) = 98
    c: Coincident(g1,g0)
    c: Block(g1)
    c: Coincident(g2,g0)
    c: Vertical(g2)
    c: Distance(g2) = 19
    c: Horizontal(g3)
    c: Coincident(g4,g1)
    c: Vertical(g4)
    c: Coincident(g3,g4)
    c: Block(g3)
    c: Coincident(g5,g2)
    c: Coincident(g5,g3)
    c: Block(g0)
    c: Block(g5)
FEATURE [Part::Extrusion] Extrude067  label="sideB003"
  Base = -> Sketch075
  Dir = (0,0,1)
  DirMode = 2
  FaceMakerClass = Part::FaceMakerBullseye
  LengthFwd = 3
  LengthRev = 0
  Placement = pos=(0,0,71.7) rot=(0,0,1;0rad)
  Solid = true
  Symmetric = false
FEATURE [Sketcher::SketchObject] Sketch076  label="topSketch023"
  FullyConstrained = true
  sketch-geometry (6):
    g0: LineSegment StartX=19 StartY=38 StartZ=0 EndX=117 EndY=38 EndZ=0
    g1: ArcOfCircle CenterX=19 CenterY=19 CenterZ=0 NormalX=0 NormalY=0 NormalZ=1 AngleXU=0 Radius=19 StartAngle=1.5708 EndAngle=3.14159
    g2: LineSegment StartX=117 StartY=38 StartZ=0 EndX=117 EndY=19 EndZ=0
    g3: LineSegment StartX=98 StartY=1.0161e-12 StartZ=0 EndX=5.22862e-06 EndY=1.0161e-12 EndZ=0
    g4: LineSegment StartX=5.22862e-06 StartY=19 StartZ=0 EndX=5.22862e-06 EndY=1.0161e-12 EndZ=0
    g5: ArcOfCircle CenterX=98 CenterY=19 CenterZ=0 NormalX=0 NormalY=0 NormalZ=1 AngleXU=0 Radius=19 StartAngle=4.71239 EndAngle=6.28319
  constraints (16):
    c: Horizontal(g0)
    c: Distance(g0) = 98
    c: Coincident(g1,g0)
    c: Block(g1)
    c: Coincident(g2,g0)
    c: Vertical(g2)
    c: Distance(g2) = 19
    c: Horizontal(g3)
    c: Coincident(g4,g1)
    c: Vertical(g4)
    c: Coincident(g3,g4)
    c: Block(g3)
    c: Coincident(g5,g2)
    c: Coincident(g5,g3)
    c: Block(g0)
    c: Block(g5)
FEATURE [Part::Extrusion] Extrude066  label="sideA003"
  Base = -> Sketch076
  Dir = (0,0,1)
  DirMode = 2
  FaceMakerClass = Part::FaceMakerBullseye
  LengthFwd = 3
  LengthRev = 0
  Placement = pos=(0,0,-2.7) rot=(0,0,1;0rad)
  Solid = true
  Symmetric = false
FEATURE [Part::MultiFuse] Fusion142  label="removeFromBottom003"
  Placement = pos=(2,0,0) rot=(0,0,1;0rad)
  Shapes = -> [Extrude066,Extrude067]
FEATURE [Part::Cut] Cut065  label="screwRetainers002"
  Base = -> Fusion096
  Tool = -> Fusion142
FEATURE [Sketcher::SketchObject] Sketch077
  FullyConstrained = true
  Placement = pos=(117,19,0) rot=(0.57735,0.57735,0.57735;2.0944rad)
  sketch-geometry (8):
    g0: LineSegment StartX=-49.19 StartY=63.5 StartZ=0 EndX=-49.19 EndY=60.5 EndZ=0
    g1: LineSegment StartX=-49.19 StartY=11.5 StartZ=0 EndX=-49.19 EndY=8.5 EndZ=0
    g2: ArcOfCircle CenterX=-1.5 CenterY=62 CenterZ=0 NormalX=0 NormalY=0 NormalZ=1 AngleXU=0 Radius=1.5 StartAngle=4.71239 EndAngle=7.85398
    g3: ArcOfCircle CenterX=-1.5 CenterY=10 CenterZ=0 NormalX=0 NormalY=0 NormalZ=1 AngleXU=0 Radius=1.5 StartAngle=4.71239 EndAngle=7.85398
    g4: LineSegment StartX=-49.19 StartY=63.5 StartZ=0 EndX=-1.5 EndY=63.5 EndZ=0
    g5: LineSegment StartX=-49.19 StartY=60.5 StartZ=0 EndX=-1.5 EndY=60.5 EndZ=0
    g6: LineSegment StartX=-49.19 StartY=11.5 StartZ=0 EndX=-1.5 EndY=11.5 EndZ=0
    g7: LineSegment StartX=-49.19 StartY=8.5 StartZ=0 EndX=-1.5 EndY=8.5 EndZ=0
  constraints (19):
    c: Vertical(g0)
    c: Distance(g0) = 3
    c: Vertical(g1)
    c: Block(g1)
    c: Block(g2)
    c: Block(g3)
    c: Block(g0)
    c: Coincident(g4,g0)
    c: Coincident(g4,g2)
    c: Horizontal(g4)
    c: Coincident(g5,g0)
    c: Coincident(g5,g2)
    c: Horizontal(g5)
    c: Coincident(g6,g1)
    c: Coincident(g6,g3)
    c: Horizontal(g6)
    c: Coincident(g7,g1)
    c: Coincident(g7,g3)
    c: Horizontal(g7)
FEATURE [Part::Extrusion] Extrude068
  Base = -> Sketch077
  Dir = (1,0,0)
  DirMode = 2
  FaceMakerClass = Part::FaceMakerBullseye
  LengthFwd = 10
  LengthRev = 0
  Solid = true
  Symmetric = false
FEATURE [Part::Fillet] Fillet057  label="removeFromtMoreFrontCaseScrewRetainers002"
  Base = -> Extrude068
  Edges = 4 edges r=1.49: [Edge6,Edge11,Edge18,Edge23]
  Placement = pos=(-12,0,0) rot=(0,0,1;0rad)
FEATURE [Sketcher::SketchObject] Sketch078
  FullyConstrained = true
  Placement = pos=(117,19,0) rot=(0.57735,0.57735,0.57735;2.0944rad)
  sketch-geometry (8):
    g0: LineSegment StartX=-49.19 StartY=69.25 StartZ=0 EndX=-49.19 EndY=66.25 EndZ=0
    g1: LineSegment StartX=-49.19 StartY=5.75 StartZ=0 EndX=-49.19 EndY=2.75 EndZ=0
    g2: ArcOfCircle CenterX=-1.5 CenterY=67.75 CenterZ=0 NormalX=0 NormalY=0 NormalZ=1 AngleXU=0 Radius=1.5 StartAngle=4.71239 EndAngle=7.85398
    g3: ArcOfCircle CenterX=-1.5 CenterY=4.25 CenterZ=0 NormalX=0 NormalY=0 NormalZ=1 AngleXU=0 Radius=1.5 StartAngle=4.71239 EndAngle=7.85398
    g4: LineSegment StartX=-49.19 StartY=69.25 StartZ=0 EndX=-1.5 EndY=69.25 EndZ=0
    g5: LineSegment StartX=-49.19 StartY=66.25 StartZ=0 EndX=-1.5 EndY=66.25 EndZ=0
    g6: LineSegment StartX=-49.19 StartY=5.75 StartZ=0 EndX=-1.5 EndY=5.75 EndZ=0
    g7: LineSegment StartX=-49.19 StartY=2.75 StartZ=0 EndX=-1.5 EndY=2.75 EndZ=0
  constraints (19):
    c: Vertical(g0)
    c: Distance(g0) = 3
    c: Block(g0)
    c: Vertical(g1)
    c: Block(g2)
    c: Block(g3)
    c: Block(g1)
    c: Coincident(g4,g0)
    c: Coincident(g4,g2)
    c: Horizontal(g4)
    c: Coincident(g5,g0)
    c: Coincident(g5,g2)
    c: Horizontal(g5)
    c: Coincident(g6,g1)
    c: Coincident(g6,g3)
    c: Horizontal(g6)
    c: Coincident(g7,g1)
    c: Coincident(g7,g3)
    c: Horizontal(g7)
FEATURE [Part::Extrusion] Extrude069
  Base = -> Sketch078
  Dir = (1,0,0)
  DirMode = 2
  FaceMakerClass = Part::FaceMakerBullseye
  LengthFwd = 10
  LengthRev = 0
  Solid = true
  Symmetric = false
FEATURE [Part::Fillet] Fillet058  label="removeFromtMoreFrontCaseScrewRetainers003"
  Base = -> Extrude069
  Edges = 4 edges r=1.49: [Edge6,Edge11,Edge18,Edge23]
  Placement = pos=(-4,0,0) rot=(0,0,1;0rad)
FEATURE [Part::Cut] Cut066
  Base = -> Cut065
  Tool = -> Fillet058
FEATURE [Part::Cut] Cut067  label="screwPillars"
  Base = -> Cut066
  Tool = -> Fillet057
FEATURE [Part::MultiFuse] Fusion143  label="bottom021"
  Shapes = -> [Cut031,Cut063]
FEATURE [Part::Cylinder] Cylinder
  Angle = 360
  AttacherType = Attacher::AttachEngine3D
  Height = 10
  Placement = pos=(20.65,12,4.68) rot=(1,0,0;1.5708rad)
  Radius = 2
FEATURE [Part::Cylinder] Cylinder064
  Angle = 360
  AttacherType = Attacher::AttachEngine3D
  Height = 10
  Placement = pos=(20.65,12,67.38) rot=(1,0,0;1.5708rad)
  Radius = 2
FEATURE [Part::Cylinder] Cylinder065
  Angle = 360
  AttacherType = Attacher::AttachEngine3D
  Height = 10
  Placement = pos=(77.15,12,67.38) rot=(1,0,0;1.5708rad)
  Radius = 2
FEATURE [Part::Cylinder] Cylinder066
  Angle = 360
  AttacherType = Attacher::AttachEngine3D
  Height = 10
  Placement = pos=(77.15,12,4.68) rot=(1,0,0;1.5708rad)
  Radius = 2
FEATURE [Part::MultiFuse] Fusion144  label="removeFromThreadedInsertHousing"
  Shapes = -> [Cylinder065,Cylinder064,Cylinder,Cylinder066]
FEATURE [Part::Cut] Cut068  label="pcbStands001"
  Base = -> Cut064
  Tool = -> Fusion144
FEATURE [Part::MultiFuse] Fusion145
  Shapes = -> [Cut068,Fusion143]
FEATURE [Part::MultiFuse] Fusion146
  Shapes = -> [Fusion145]
FEATURE [Part::MultiFuse] Fusion147  label="bottom022"
  Shapes = -> [Cut067,Fusion146]
FEATURE [Part::MultiFuse] Fusion148  label="casePillars005"
  Shapes = -> [Cut047,Fusion092]
FEATURE [Part::MultiFuse] Fusion149  label="bottom023"
  Shapes = -> [Fusion124,Fusion113,Fusion147]
FEATURE [Part::MultiFuse] Fusion150  label="topBits"
  Shapes = -> [Cut025,Fusion148,Cut030,Fillet034]
FEATURE [Part::Feature] Face149 .. Face152  x4 (patterned run collapsed; names and placements below)
  shape: bbox 3.2 x 1.5 x 2e-07 mm, 1 faces, 0 solids (baked)
FEATURE [Part::Feature] Face153
  shape: bbox 3.6 x 3.2 x 2e-07 mm, 1 faces, 0 solids (baked)
FEATURE [Part::Feature] Face154
  shape: bbox 3.6 x 3.2 x 2e-07 mm, 1 faces, 0 solids (baked)
FEATURE [Sketcher::SketchObject] Sketch079  label="topSketch024"
  FullyConstrained = true
  sketch-geometry (6):
    g0: LineSegment StartX=19 StartY=38 StartZ=0 EndX=117 EndY=38 EndZ=0
    g1: ArcOfCircle CenterX=19 CenterY=19 CenterZ=0 NormalX=0 NormalY=0 NormalZ=1 AngleXU=0 Radius=19 StartAngle=1.5708 EndAngle=3.14159
    g2: LineSegment StartX=117 StartY=38 StartZ=0 EndX=117 EndY=19 EndZ=0
    g3: LineSegment StartX=98 StartY=1.0161e-12 StartZ=0 EndX=5.22862e-06 EndY=1.0161e-12 EndZ=0
    g4: LineSegment StartX=5.22862e-06 StartY=19 StartZ=0 EndX=5.22862e-06 EndY=1.0161e-12 EndZ=0
    g5: ArcOfCircle CenterX=98 CenterY=19 CenterZ=0 NormalX=0 NormalY=0 NormalZ=1 AngleXU=0 Radius=19 StartAngle=4.71239 EndAngle=6.28319
  constraints (16):
    c: Horizontal(g0)
    c: Distance(g0) = 98
    c: Coincident(g1,g0)
    c: Block(g1)
    c: Coincident(g2,g0)
    c: Vertical(g2)
    c: Distance(g2) = 19
    c: Horizontal(g3)
    c: Coincident(g4,g1)
    c: Vertical(g4)
    c: Coincident(g3,g4)
    c: Block(g3)
    c: Coincident(g5,g2)
    c: Coincident(g5,g3)
    c: Block(g0)
    c: Block(g5)
FEATURE [Sketcher::SketchObject] Sketch080  label="topSketch025"
  FullyConstrained = true
  sketch-geometry (6):
    g0: LineSegment StartX=19 StartY=38 StartZ=0 EndX=117 EndY=38 EndZ=0
    g1: ArcOfCircle CenterX=19 CenterY=19 CenterZ=0 NormalX=0 NormalY=0 NormalZ=1 AngleXU=0 Radius=19 StartAngle=1.5708 EndAngle=3.14159
    g2: LineSegment StartX=117 StartY=38 StartZ=0 EndX=117 EndY=19 EndZ=0
    g3: LineSegment StartX=98 StartY=1.0161e-12 StartZ=0 EndX=5.22862e-06 EndY=1.0161e-12 EndZ=0
    g4: LineSegment StartX=5.22862e-06 StartY=19 StartZ=0 EndX=5.22862e-06 EndY=1.0161e-12 EndZ=0
    g5: ArcOfCircle CenterX=98 CenterY=19 CenterZ=0 NormalX=0 NormalY=0 NormalZ=1 AngleXU=0 Radius=19 StartAngle=4.71239 EndAngle=6.28319
  constraints (16):
    c: Horizontal(g0)
    c: Distance(g0) = 98
    c: Coincident(g1,g0)
    c: Block(g1)
    c: Coincident(g2,g0)
    c: Vertical(g2)
    c: Distance(g2) = 19
    c: Horizontal(g3)
    c: Coincident(g4,g1)
    c: Vertical(g4)
    c: Coincident(g3,g4)
    c: Block(g3)
    c: Coincident(g5,g2)
    c: Coincident(g5,g3)
    c: Block(g0)
    c: Block(g5)
FEATURE [Part::Extrusion] Extrude070  label="sideA004"
  Base = -> Sketch080
  Dir = (0,0,1)
  DirMode = 2
  FaceMakerClass = Part::FaceMakerBullseye
  LengthFwd = 3
  LengthRev = 0
  Placement = pos=(0,0,-2.7) rot=(0,0,1;0rad)
  Solid = true
  Symmetric = false
FEATURE [Sketcher::SketchObject] Sketch081
  FullyConstrained = true
  Placement = pos=(117,19,0) rot=(0.57735,0.57735,0.57735;2.0944rad)
  sketch-geometry (8):
    g0: LineSegment StartX=-49.19 StartY=63.5 StartZ=0 EndX=-49.19 EndY=60.5 EndZ=0
    g1: LineSegment StartX=-49.19 StartY=11.5 StartZ=0 EndX=-49.19 EndY=8.5 EndZ=0
    g2: ArcOfCircle CenterX=-1.5 CenterY=62 CenterZ=0 NormalX=0 NormalY=0 NormalZ=1 AngleXU=0 Radius=1.5 StartAngle=4.71239 EndAngle=7.85398
    g3: ArcOfCircle CenterX=-1.5 CenterY=10 CenterZ=0 NormalX=0 NormalY=0 NormalZ=1 AngleXU=0 Radius=1.5 StartAngle=4.71239 EndAngle=7.85398
    g4: LineSegment StartX=-49.19 StartY=63.5 StartZ=0 EndX=-1.5 EndY=63.5 EndZ=0
    g5: LineSegment StartX=-49.19 StartY=60.5 StartZ=0 EndX=-1.5 EndY=60.5 EndZ=0
    g6: LineSegment StartX=-49.19 StartY=11.5 StartZ=0 EndX=-1.5 EndY=11.5 EndZ=0
    g7: LineSegment StartX=-49.19 StartY=8.5 StartZ=0 EndX=-1.5 EndY=8.5 EndZ=0
  constraints (19):
    c: Vertical(g0)
    c: Distance(g0) = 3
    c: Vertical(g1)
    c: Block(g1)
    c: Block(g2)
    c: Block(g3)
    c: Block(g0)
    c: Coincident(g4,g0)
    c: Coincident(g4,g2)
    c: Horizontal(g4)
    c: Coincident(g5,g0)
    c: Coincident(g5,g2)
    c: Horizontal(g5)
    c: Coincident(g6,g1)
    c: Coincident(g6,g3)
    c: Horizontal(g6)
    c: Coincident(g7,g1)
    c: Coincident(g7,g3)
    c: Horizontal(g7)
FEATURE [Part::Extrusion] Extrude071  label="sideB004"
  Base = -> Sketch079
  Dir = (0,0,1)
  DirMode = 2
  FaceMakerClass = Part::FaceMakerBullseye
  LengthFwd = 3
  LengthRev = 0
  Placement = pos=(0,0,71.7) rot=(0,0,1;0rad)
  Solid = true
  Symmetric = false
FEATURE [Part::MultiFuse] Fusion152  label="removeFromBottom004"
  Placement = pos=(2,0,0) rot=(0,0,1;0rad)
  Shapes = -> [Extrude070,Extrude071]
FEATURE [Part::Extrusion] Extrude072
  Base = -> Sketch081
  Dir = (1,0,0)
  DirMode = 2
  FaceMakerClass = Part::FaceMakerBullseye
  LengthFwd = 10
  LengthRev = 0
  Solid = true
  Symmetric = false
FEATURE [Part::Fillet] Fillet059  label="removeFromtMoreFrontCaseScrewRetainers004"
  Base = -> Extrude072
  Edges = 4 edges r=1.49: [Edge6,Edge11,Edge18,Edge23]
  Placement = pos=(-12,0,0) rot=(0,0,1;0rad)
FEATURE [Sketcher::SketchObject] Sketch082
  FullyConstrained = true
  Placement = pos=(117,19,0) rot=(0.57735,0.57735,0.57735;2.0944rad)
  sketch-geometry (8):
    g0: LineSegment StartX=-49.19 StartY=69.25 StartZ=0 EndX=-49.19 EndY=66.25 EndZ=0
    g1: LineSegment StartX=-49.19 StartY=5.75 StartZ=0 EndX=-49.19 EndY=2.75 EndZ=0
    g2: ArcOfCircle CenterX=-1.5 CenterY=67.75 CenterZ=0 NormalX=0 NormalY=0 NormalZ=1 AngleXU=0 Radius=1.5 StartAngle=4.71239 EndAngle=7.85398
    g3: ArcOfCircle CenterX=-1.5 CenterY=4.25 CenterZ=0 NormalX=0 NormalY=0 NormalZ=1 AngleXU=0 Radius=1.5 StartAngle=4.71239 EndAngle=7.85398
    g4: LineSegment StartX=-49.19 StartY=69.25 StartZ=0 EndX=-1.5 EndY=69.25 EndZ=0
    g5: LineSegment StartX=-49.19 StartY=66.25 StartZ=0 EndX=-1.5 EndY=66.25 EndZ=0
    g6: LineSegment StartX=-49.19 StartY=5.75 StartZ=0 EndX=-1.5 EndY=5.75 EndZ=0
    g7: LineSegment StartX=-49.19 StartY=2.75 StartZ=0 EndX=-1.5 EndY=2.75 EndZ=0
  constraints (19):
    c: Vertical(g0)
    c: Distance(g0) = 3
    c: Block(g0)
    c: Vertical(g1)
    c: Block(g2)
    c: Block(g3)
    c: Block(g1)
    c: Coincident(g4,g0)
    c: Coincident(g4,g2)
    c: Horizontal(g4)
    c: Coincident(g5,g0)
    c: Coincident(g5,g2)
    c: Horizontal(g5)
    c: Coincident(g6,g1)
    c: Coincident(g6,g3)
    c: Horizontal(g6)
    c: Coincident(g7,g1)
    c: Coincident(g7,g3)
    c: Horizontal(g7)
FEATURE [Part::Extrusion] Extrude073
  Base = -> Sketch082
  Dir = (1,0,0)
  DirMode = 2
  FaceMakerClass = Part::FaceMakerBullseye
  LengthFwd = 10
  LengthRev = 0
  Solid = true
  Symmetric = false
FEATURE [Part::Fillet] Fillet060  label="removeFromtMoreFrontCaseScrewRetainers005"
  Base = -> Extrude073
  Edges = 4 edges r=1.49: [Edge6,Edge11,Edge18,Edge23]
  Placement = pos=(-4,0,0) rot=(0,0,1;0rad)
FEATURE [Part::Revolution] Revolve163  label="backCaseScrewRetainer004"
  Angle = 360
  Axis = (0,1,0)
  Base = (0,0,0)
  FaceMakerClass = Part::FaceMakerBullseye
  Placement = pos=(12.5,3,62) rot=(0,0,1;0rad)
  Solid = false
  Source = -> Face149
  Symmetric = false
FEATURE [Part::Revolution] Revolve164  label="frontCaseScrewRetainer006"
  Angle = 360
  Axis = (0,1,0)
  Base = (0,0,0)
  FaceMakerClass = Part::FaceMakerBullseye
  Placement = pos=(89.5,3,68.5) rot=(0,0,1;0rad)
  Solid = false
  Source = -> Face151
  Symmetric = false
FEATURE [Part::Revolution] Revolve165  label="frontCaseScrewRetainer007"
  Angle = 360
  Axis = (0,1,0)
  Base = (0,0,0)
  FaceMakerClass = Part::FaceMakerBullseye
  Placement = pos=(89.5,3,3.5) rot=(0,0,1;0rad)
  Solid = false
  Source = -> Face152
  Symmetric = false
FEATURE [Part::Revolution] Revolve166  label="backCaseScrewRetainer005"
  Angle = 360
  Axis = (0,1,0)
  Base = (0,0,0)
  FaceMakerClass = Part::FaceMakerBullseye
  Placement = pos=(12.5,3,10) rot=(0,0,1;0rad)
  Solid = false
  Source = -> Face150
  Symmetric = false
FEATURE [Part::Revolution] Revolve167  label="moreFrontCaseScrewRetainer006"
  Angle = 360
  Axis = (0,1,0)
  Base = (0,0,0)
  FaceMakerClass = Part::FaceMakerBullseye
  Placement = pos=(109.5,4.5,68.5) rot=(0,0,1;0rad)
  Solid = false
  Source = -> Face153
  Symmetric = false
FEATURE [Part::Revolution] Revolve168  label="moreFrontCaseScrewRetainer007"
  Angle = 360
  Axis = (0,1,0)
  Base = (0,0,0)
  FaceMakerClass = Part::FaceMakerBullseye
  Placement = pos=(109.5,4.5,3.5) rot=(0,0,1;0rad)
  Solid = false
  Source = -> Face154
  Symmetric = false
FEATURE [Part::MultiFuse] Fusion151  label="screwRetainers003"
  Shapes = -> [Revolve168,Revolve167,Revolve166,Revolve165,Revolve164,Revolve163]
FEATURE [Part::Cut] Cut069  label="screwRetainers004"
  Base = -> Fusion151
  Tool = -> Fusion152
FEATURE [Part::Cut] Cut070
  Base = -> Cut069
  Tool = -> Fillet060
FEATURE [Part::Cut] Cut071  label="screwPillars001"
  Base = -> Cut070
  Tool = -> Fillet059
FEATURE [Part::MultiFuse] Fusion153  label="bottom024"
  Shapes = -> [Fusion149,Cut071]
FEATURE [Part::Cylinder] Cylinder067
  Angle = 360
  AttacherType = Attacher::AttachEngine3D
  Height = 10
  Placement = pos=(20.65,12,4.68) rot=(1,0,0;1.5708rad)
  Radius = 2
FEATURE [Part::Cylinder] Cylinder068
  Angle = 360
  AttacherType = Attacher::AttachEngine3D
  Height = 10
  Placement = pos=(20.65,12,67.38) rot=(1,0,0;1.5708rad)
  Radius = 2
FEATURE [Part::Cylinder] Cylinder069
  Angle = 360
  AttacherType = Attacher::AttachEngine3D
  Height = 10
  Placement = pos=(77.15,12,67.38) rot=(1,0,0;1.5708rad)
  Radius = 2
FEATURE [Part::Cylinder] Cylinder070
  Angle = 360
  AttacherType = Attacher::AttachEngine3D
  Height = 10
  Placement = pos=(77.15,12,4.68) rot=(1,0,0;1.5708rad)
  Radius = 2
FEATURE [Part::MultiFuse] Fusion154  label="removeFromThreadedInsertHousing001"
  Shapes = -> [Cylinder069,Cylinder068,Cylinder067,Cylinder070]
FEATURE [Part::Cut] Cut072  label="bottom025"
  Base = -> Fusion153
  Tool = -> Fusion154
FEATURE [Image::ImagePlane] ImagePlane
  XSize = 339
  YSize = 72
FEATURE [Sketcher::SketchObject] Sketch083
  FullyConstrained = true
  MapMode = 5
  Support = -> [XY_Plane]
  sketch-geometry (205):
    g0: LineSegment StartX=-151.619 StartY=28.8932 StartZ=0 EndX=-140.819 EndY=28.8932 EndZ=0
    g1: LineSegment StartX=-151.619 StartY=24.0313 StartZ=0 EndX=-151.619 EndY=28.8932 EndZ=0
    g2: LineSegment StartX=-140.819 StartY=17.7713 StartZ=0 EndX=-151.619 EndY=17.7713 EndZ=0
    g3: LineSegment StartX=-151.619 StartY=17.7713 StartZ=0 EndX=-151.619 EndY=22.6313 EndZ=0
    g4: LineSegment StartX=-151.619 StartY=22.6313 StartZ=0 EndX=-145.128 EndY=22.6313 EndZ=0
    g5: LineSegment StartX=-145.128 StartY=24.0313 StartZ=0 EndX=-140.819 EndY=28.8932 EndZ=0
    g6: LineSegment StartX=-145.128 StartY=22.6313 StartZ=0 EndX=-140.819 EndY=17.7713 EndZ=0
    g7: ArcOfCircle CenterX=-155.157 CenterY=23.3323 CenterZ=0 NormalX=0 NormalY=0 NormalZ=1 AngleXU=0 Radius=6.92354 StartAngle=1.03434 EndAngle=5.24885
    g8: ArcOfCircle CenterX=-155.157 CenterY=23.3323 CenterZ=0 NormalX=0 NormalY=0 NormalZ=1 AngleXU=0 Radius=12.6269 StartAngle=1.28675 EndAngle=4.99643
    g9: LineSegment StartX=-151.619 StartY=35.4532 StartZ=0 EndX=-151.619 EndY=29.2832 EndZ=0
    g10: LineSegment StartX=-151.619 StartY=17.3813 StartZ=0 EndX=-151.619 EndY=11.2113 EndZ=0
    g11-g21: Circle x11 (B-spline internal-alignment scaffolding for g22; pole/knot coordinates omitted)
    g22: BSplineCurve PolesCount=11 KnotsCount=9 Degree=3 IsPeriodic=0
    g23-g31: GeomPoint x9 (B-spline internal-alignment scaffolding for g22; pole/knot coordinates omitted)
    g32-g49: Circle x18 (B-spline internal-alignment scaffolding for g50; pole/knot coordinates omitted)
    g50: BSplineCurve PolesCount=18 KnotsCount=16 Degree=3 IsPeriodic=0
    g51-g66: GeomPoint x16 (B-spline internal-alignment scaffolding for g50; pole/knot coordinates omitted)
    g67: LineSegment StartX=-117.124 StartY=30.093 StartZ=0 EndX=-117.603 EndY=26.5272 EndZ=0
    g68: LineSegment StartX=-117.603 StartY=17.8472 StartZ=0 EndX=-117.124 EndY=14.2659 EndZ=0
    g69: Ellipse CenterX=-109.671 CenterY=20.025 CenterZ=0 NormalX=0 NormalY=0 NormalZ=1 MajorRadius=3.34798 MinorRadius=2.71052 AngleXU=-1.56793
    g70: GeomPoint X=-109.666 Y=18.0598 Z=0
    g71: GeomPoint X=-109.677 Y=21.9902 Z=0
    g72: Ellipse CenterX=-109.671 CenterY=20.0123 CenterZ=0 NormalX=0 NormalY=0 NormalZ=1 MajorRadius=6.93002 MinorRadius=6.36273 AngleXU=-3.13976
    g73: GeomPoint X=-112.417 Y=20.0073 Z=0
    g74: GeomPoint X=-106.925 Y=20.0173 Z=0
    g75: Ellipse CenterX=-51.7682 CenterY=20.1463 CenterZ=0 NormalX=0 NormalY=0 NormalZ=1 MajorRadius=3.19279 MinorRadius=2.71052 AngleXU=-1.52774
    g76: GeomPoint X=-51.6955 Y=18.4606 Z=0
    g77: GeomPoint X=-51.8408 Y=21.832 Z=0
    g78: GeomPoint X=-54.5142 Y=20.1413 Z=0
    g79: GeomPoint X=-49.0221 Y=20.1513 Z=0
    g80: Ellipse CenterX=-51.7682 CenterY=20.1463 CenterZ=0 NormalX=0 NormalY=0 NormalZ=1 MajorRadius=6.93002 MinorRadius=6.36273 AngleXU=-3.13976
    g81: Ellipse CenterX=-22.8436 CenterY=20.1783 CenterZ=0 NormalX=0 NormalY=0 NormalZ=1 MajorRadius=3.31512 MinorRadius=2.71052 AngleXU=-1.60214
    g82: GeomPoint X=-22.9034 Y=18.2706 Z=0
    g83: GeomPoint X=-22.7838 Y=22.0861 Z=0
    g84: GeomPoint X=-25.5897 Y=20.1733 Z=0
    g85: GeomPoint X=-20.0976 Y=20.1833 Z=0
    g86: Ellipse CenterX=-22.8436 CenterY=20.1783 CenterZ=0 NormalX=0 NormalY=0 NormalZ=1 MajorRadius=6.93002 MinorRadius=6.36273 AngleXU=-3.13976
    g87: LineSegment StartX=-101.889 StartY=14.1107 StartZ=0 EndX=-97.7455 EndY=14.1107 EndZ=0
    g88: LineSegment StartX=-93.8155 StartY=14.1107 StartZ=0 EndX=-89.6755 EndY=14.1107 EndZ=0
    g89: LineSegment StartX=-85.7455 StartY=14.1107 StartZ=0 EndX=-81.6055 EndY=14.1107 EndZ=0
    g90: LineSegment StartX=-101.889 StartY=14.1107 StartZ=0 EndX=-101.889 EndY=25.9907 EndZ=0
    g91: LineSegment StartX=-101.889 StartY=25.9907 StartZ=0 EndX=-97.8594 EndY=25.9907 EndZ=0
    g92: LineSegment StartX=-97.8594 StartY=25.9907 StartZ=0 EndX=-97.8594 EndY=24.0907 EndZ=0
    g93: LineSegment StartX=-97.7455 StartY=14.1107 StartZ=0 EndX=-97.7455 EndY=19.9107 EndZ=0
    g94: LineSegment StartX=-89.6755 StartY=14.1107 StartZ=0 EndX=-89.6755 EndY=19.9107 EndZ=0
    g95: LineSegment StartX=-93.8155 StartY=14.1107 StartZ=0 EndX=-93.8155 EndY=21.0107 EndZ=0
    g96-g106: Circle x11 (B-spline internal-alignment scaffolding for g107; pole/knot coordinates omitted)
    g107: BSplineCurve PolesCount=11 KnotsCount=9 Degree=3 IsPeriodic=0
    g108-g116: GeomPoint x9 (B-spline internal-alignment scaffolding for g107; pole/knot coordinates omitted)
    g117: BSplineCurve PolesCount=11 KnotsCount=9 Degree=3 IsPeriodic=0
    g118-g125: Circle x8 (B-spline internal-alignment scaffolding for g126; pole/knot coordinates omitted)
    g126: BSplineCurve PolesCount=8 KnotsCount=6 Degree=3 IsPeriodic=0
    g127-g132: GeomPoint x6 (B-spline internal-alignment scaffolding for g126; pole/knot coordinates omitted)
    g133: BSplineCurve PolesCount=8 KnotsCount=6 Degree=3 IsPeriodic=0
    g134: LineSegment StartX=-85.7455 StartY=21.0107 StartZ=0 EndX=-85.7455 EndY=14.1107 EndZ=0
    g135: LineSegment StartX=-80.0879 StartY=14.1107 StartZ=0 EndX=-75.944 EndY=14.1107 EndZ=0
    g136: LineSegment StartX=-72.014 StartY=14.1107 StartZ=0 EndX=-67.874 EndY=14.1107 EndZ=0
    g137: LineSegment StartX=-63.944 StartY=14.1107 StartZ=0 EndX=-59.804 EndY=14.1107 EndZ=0
    g138: LineSegment StartX=-80.0879 StartY=14.1107 StartZ=0 EndX=-80.0879 EndY=25.9907 EndZ=0
    g139: LineSegment StartX=-80.0879 StartY=25.9907 StartZ=0 EndX=-76.0579 EndY=25.9907 EndZ=0
    g140: LineSegment StartX=-76.0579 StartY=25.9907 StartZ=0 EndX=-76.0579 EndY=24.0907 EndZ=0
    g141: LineSegment StartX=-75.944 StartY=14.1107 StartZ=0 EndX=-75.944 EndY=19.9107 EndZ=0
    g142: LineSegment StartX=-67.874 StartY=14.1107 StartZ=0 EndX=-67.874 EndY=19.9107 EndZ=0
    g143: LineSegment StartX=-72.014 StartY=14.1107 StartZ=0 EndX=-72.014 EndY=21.0107 EndZ=0
    g144-g148: Circle x5 (B-spline internal-alignment scaffolding for g149; pole/knot coordinates omitted)
    g149: BSplineCurve PolesCount=11 KnotsCount=9 Degree=3 IsPeriodic=0
    g150-g158: GeomPoint x9 (B-spline internal-alignment scaffolding for g149; pole/knot coordinates omitted)
    g159: BSplineCurve PolesCount=11 KnotsCount=9 Degree=3 IsPeriodic=0
    g160-g167: Circle x8 (B-spline internal-alignment scaffolding for g168; pole/knot coordinates omitted)
    g168: BSplineCurve PolesCount=8 KnotsCount=6 Degree=3 IsPeriodic=0
    g169-g174: GeomPoint x6 (B-spline internal-alignment scaffolding for g168; pole/knot coordinates omitted)
    g175: BSplineCurve PolesCount=8 KnotsCount=6 Degree=3 IsPeriodic=0
    g176: LineSegment StartX=-63.944 StartY=21.0107 StartZ=0 EndX=-63.944 EndY=14.1107 EndZ=0
    g177: LineSegment StartX=-59.804 StartY=14.1107 StartZ=0 EndX=-59.804 EndY=21.5868 EndZ=0
    g178: BSplineCurve PolesCount=4 KnotsCount=2 Degree=3 IsPeriodic=0
    g179: GeomPoint X=-59.804 Y=21.5868 Z=0
    g180: GeomPoint X=-60.2379 Y=24.0907 Z=0
    g181: LineSegment StartX=-81.6055 StartY=14.1107 StartZ=0 EndX=-81.6055 EndY=21.5868 EndZ=0
    g182: LineSegment StartX=-151.619 StartY=24.0313 StartZ=0 EndX=-145.128 EndY=24.0313 EndZ=0
    g183: Circle CenterX=-82.0394 CenterY=24.0907 CenterZ=0 NormalX=0 NormalY=0 NormalZ=1 AngleXU=0 Radius=1
    g184: Circle CenterX=-81.7131 CenterY=23.2736 CenterZ=0 NormalX=0 NormalY=0 NormalZ=1 AngleXU=0 Radius=1
    g185: Circle CenterX=-81.6055 CenterY=21.5868 CenterZ=0 NormalX=0 NormalY=0 NormalZ=1 AngleXU=0 Radius=1
    g186: BSplineCurve PolesCount=3 KnotsCount=2 Degree=2 IsPeriodic=0
    g187: GeomPoint X=-82.0394 Y=24.0907 Z=0
    g188: GeomPoint X=-81.6055 Y=21.5868 Z=0
    g189: Ellipse CenterX=-37.3522 CenterY=19.9515 CenterZ=0 NormalX=0 NormalY=0 NormalZ=1 MajorRadius=2.99755 MinorRadius=2.49 AngleXU=1.5708
    g190: GeomPoint X=-37.3522 Y=21.6203 Z=0
    g191: GeomPoint X=-37.3522 Y=18.2826 Z=0
    g192: ArcOfEllipse CenterX=-38.7647 CenterY=20.06 CenterZ=0 NormalX=0 NormalY=0 NormalZ=1 MajorRadius=6.30025 MinorRadius=5.3849 AngleXU=1.57276 StartAngle=5.50632 EndAngle=10.3035
    g193: GeomPoint X=-38.7711 Y=23.3304 Z=0
    g194: GeomPoint X=-38.7583 Y=16.7895 Z=0
    g195: LineSegment StartX=-34.6109 StartY=14.1107 StartZ=0 EndX=-30.8984 EndY=14.1107 EndZ=0
    g196: LineSegment StartX=-30.8984 StartY=14.1107 StartZ=0 EndX=-30.8984 EndY=31.1784 EndZ=0
    g197: LineSegment StartX=-30.8984 StartY=31.1784 StartZ=0 EndX=-34.9984 EndY=31.1784 EndZ=0
    g198: LineSegment StartX=-34.9984 StartY=24.5602 StartZ=0 EndX=-34.9984 EndY=31.1784 EndZ=0
    g199: LineSegment StartX=-34.6109 StartY=16.0476 StartZ=0 EndX=-34.6109 EndY=14.1107 EndZ=0
    g200: LineSegment StartX=-14.8781 StartY=14.1107 StartZ=0 EndX=-10.5106 EndY=14.1107 EndZ=0
    g201: LineSegment StartX=-14.8781 StartY=14.1107 StartZ=0 EndX=-14.8781 EndY=25.8504 EndZ=0
    g202: LineSegment StartX=-14.8781 StartY=25.8504 StartZ=0 EndX=-10.8534 EndY=25.8504 EndZ=0
    g203: LineSegment StartX=-10.8534 StartY=25.8504 StartZ=0 EndX=-10.8534 EndY=24.0923 EndZ=0
    g204: LineSegment StartX=-10.5106 StartY=14.1107 StartZ=0 EndX=-10.5106 EndY=19.7752 EndZ=0
  constraints (209):
    c: Coincident(g1,g0)
    c: Horizontal(g0)
    c: Vertical(g1)
    c: Coincident(g2,g3)
    c: Coincident(g3,g4)
    c: Horizontal(g4)
    c: Horizontal(g2)
    c: Vertical(g3)
    c: Block(g1)
    c: Distance(g3) = 4.86
    c: Block(g4)
    c: Distance(g0) = 10.8
    c: Distance(g2) = 10.8
    c: Coincident(g5,g0)
    c: Coincident(g6,g4)
    c: Coincident(g6,g2)
    c: Block(g8)
    c: Block(g7)
    c: Coincident(g9,g8)
    c: Coincident(g9,g7)
    c: Vertical(g9)
    c: Coincident(g10,g7)
    c: Coincident(g10,g8)
    c: Vertical(g10)
    c: Weight(g11) = 1
    c: Equal(g11, g12-g21) x10
    c: InternalAlignment(g11-g21 -> g22) x11
    c: InternalAlignment(g23-g31 -> g22) x9
    c: Block(g22)
    c: Weight(g32) = 1
    c: Equal(g32, g33-g49) x17
    c: InternalAlignment(g32-g49 -> g50) x18
    c: InternalAlignment(g51-g66 -> g50) x16
    c: Block(g50)
    c: Coincident(g67,g50)
    c: Coincident(g67,g22)
    c: Coincident(g68,g22)
    c: Coincident(g68,g50)
    c: InternalAlignment(g70,g69)
    c: InternalAlignment(g71,g69)
    c: Block(g69)
    c: InternalAlignment(g73,g72)
    c: InternalAlignment(g74,g72)
    c: Block(g72)
    c: InternalAlignment(g76,g75)
    c: InternalAlignment(g77,g75)
    c: InternalAlignment(g78,g80)
    c: InternalAlignment(g79,g80)
    c: Block(g80)
    c: Coincident(g75,g80)
    c: Block(g75)
    c: InternalAlignment(g82,g81)
    c: InternalAlignment(g83,g81)
    c: InternalAlignment(g84,g86)
    c: InternalAlignment(g85,g86)
    c: Block(g86)
    c: Coincident(g81,g86)
    c: Block(g81)
    c: Horizontal(g87)
    c: Block(g87)
    c: Horizontal(g88)
    c: Distance(g88) = 4.14
    c: Horizontal(g89)
    c: Equal(g88,g89) = 4.14
    c: Block(g89)
    c: Block(g88)
    c: Coincident(g90,g87)
    c: Vertical(g90)
    c: Distance(g90) = 11.88
    c: Coincident(g91,g90)
    c: Horizontal(g91)
    c: Coincident(g92,g91)
    c: Vertical(g92)
    c: Distance(g91) = 4.03
    c: Distance(g92) = 1.9
    c: Coincident(g93,g87)
    c: Vertical(g93)
    c: Vertical(g94)
    c: Coincident(g94,g88)
    c: Distance(g93) = 5.8
    c: Distance(g94) = 5.8
    c: Vertical(g95)
    c: Coincident(g95,g88)
    c: Distance(g95) = 6.9
    c: Coincident(g107,g92)
    c: Weight(g96) = 1
    c: Equal(g96, g97-g106) x10
    c: InternalAlignment(g96-g106 -> g107) x11
    c: InternalAlignment(g108-g116 -> g107) x9
    c: Block(g107)
    c: Block(g117)
    c: Coincident(g126,g93)
    c: Weight(g118) = 1
    c: Equal(g118, g119-g125) x7
    c: Coincident(g126,g95)
    c: InternalAlignment(g118-g125 -> g126) x8
    c: InternalAlignment(g127-g132 -> g126) x6
    c: Coincident(g133,g94)
    c: Block(g126)
    c: Block(g133)
    c: Coincident(g134,g133)
    c: Coincident(g134,g89)
    c: Vertical(g134)
    c: Horizontal(g135)
    c: Block(g135)
    c: Horizontal(g136)
    c: Equal(g88,g136) = 4.14
    c: Horizontal(g137)
    c: Equal(g136,g137) = 4.14
    c: Block(g137)
    c: Block(g136)
    c: Coincident(g138,g135)
    c: Vertical(g138)
    c: Equal(g90,g138) = 11.88
    c: Coincident(g139,g138)
    c: Horizontal(g139)
    c: Coincident(g140,g139)
    c: Vertical(g140)
    c: Equal(g91,g139) = 4.03
    c: Equal(g92,g140) = 1.9
    c: Coincident(g141,g135)
    c: Vertical(g141)
    c: Vertical(g142)
    c: Coincident(g142,g136)
    c: Equal(g93,g141) = 5.8
    c: Equal(g94,g142) = 5.8
    c: Vertical(g143)
    c: Coincident(g143,g136)
    c: Equal(g95,g143) = 6.9
    c: Coincident(g149,g140)
    c: Equal(g96,g144) = 1
    c: Equal(g144, g145-g148) x4
    c: InternalAlignment(g144-g148 -> g149) x5
    c: InternalAlignment(g150-g158 -> g149) x9
    c: Block(g149)
    c: Block(g159)
    c: Coincident(g168,g141)
    c: Equal(g118,g160) = 1
    c: Equal(g160, g161-g167) x7
    c: Coincident(g168,g143)
    c: InternalAlignment(g160-g167 -> g168) x8
    c: InternalAlignment(g169-g174 -> g168) x6
    c: Coincident(g175,g142)
    c: Block(g168)
    c: Block(g175)
    c: Coincident(g176,g175)
    c: Coincident(g176,g137)
    c: Vertical(g176)
    c: Coincident(g177,g137)
    c: Vertical(g177)
    c: Coincident(g178,g177)
    c: Coincident(g178,g159)
    c: InternalAlignment(g179,g178)
    c: InternalAlignment(g180,g178)
    c: Block(g178)
    c: Vertical(g181)
    c: Coincident(g181,g89)
    c: Block(g5)
    c: Coincident(g182,g1)
    c: Coincident(g182,g5)
    c: Horizontal(g182)
    c: Coincident(g186,g117)
    c: Weight(g183) = 1
    c: Equal(g183,g184)
    c: Equal(g183,g185)
    c: Coincident(g186,g181)
    c: InternalAlignment(g183,g186)
    c: InternalAlignment(g184,g186)
    c: InternalAlignment(g185,g186)
    c: InternalAlignment(g187,g186)
    c: InternalAlignment(g188,g186)
    c: Block(g186)
    c: InternalAlignment(g190,g189)
    c: InternalAlignment(g191,g189)
    c: Block(g189)
    c: InternalAlignment(g193,g192)
    c: InternalAlignment(g194,g192)
    c: Block(g192)
    c: Horizontal(g195)
    c: Block(g195)
    c: Coincident(g196,g195)
    c: Vertical(g196)
    c: Block(g196)
    c: Distance(g195) = 3.71244
    c: Coincident(g197,g196)
    c: Horizontal(g197)
    c: Distance(g197) = 4.1
    c: Coincident(g198,g192)
    c: Coincident(g198,g197)
    c: Vertical(g198)
    c: Block(g198)
    c: Coincident(g199,g192)
    c: Coincident(g199,g195)
    c: Vertical(g199)
    c: Block(g199)
    c: Horizontal(g200)
    c: Block(g200)
    c: Coincident(g201,g200)
    c: Vertical(g201)
    c: Block(g201)
    c: Coincident(g202,g201)
    c: Horizontal(g202)
    c: Block(g202)
    c: Coincident(g203,g202)
    c: Vertical(g203)
    c: Block(g203)
    c: Coincident(g204,g200)
    c: Vertical(g204)
    c: Block(g204)
FEATURE [PartDesign::Body] Body
  Group = -> [Sketch083]
  Origin = -> Origin
FEATURE [Sketcher::SketchObject] Sketch084
  FullyConstrained = true
  MapMode = 5
  Support = -> [XY_Plane001]
FEATURE [PartDesign::Body] Body001
  Group = -> [Sketch084]
  Origin = -> Origin001
